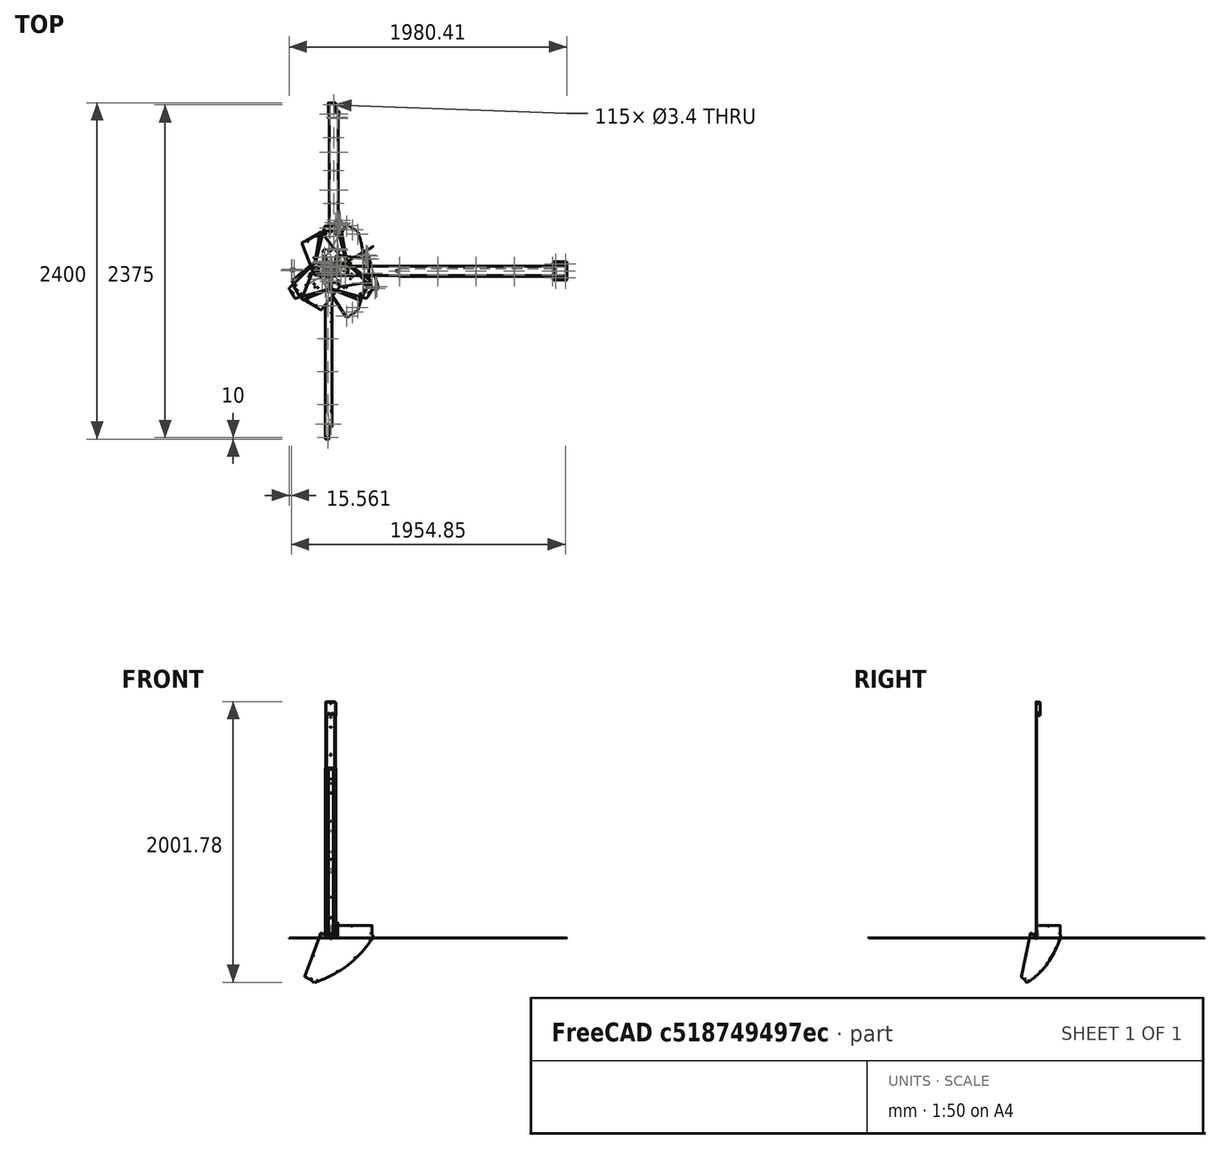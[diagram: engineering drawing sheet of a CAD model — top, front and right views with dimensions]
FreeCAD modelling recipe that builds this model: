
FCSTD DOCUMENT  (FreeCAD 0.22R37100 (Git))
Label: composit_full_size3_ss_unfold
License: All rights reserved
LicenseURL: http://en.wikipedia.org/wiki/All_rights_reserved
objects: Sketcher::SketchObject×72, TechDraw::DrawViewPart×63, TechDraw::DrawViewDimension×42, App::DocumentObjectGroup×27, Part::Feature×25, TechDraw::DrawPage×24, App::Link×23, TechDraw::DrawViewBalloon×16, PartDesign::Body×13, PartDesign::FeatureBase×12, Part::Mirroring×6, TechDraw::DrawSVGTemplate×3, PartDesign::SubShapeBinder×2, PartDesign::Pocket×2, PartDesign::FeatureAdditivePython×1, Measure::MeasureDistance×1
note: 211 computed .brp shape members not serialized (recipe doc carries the construction recipe); baked Part::Feature solids carry a one-line shape summary decoded from their .brp
EXTERNAL_REF file=composit_full_size3.FCStd obj=Body020
EXTERNAL_REF file=composit_full_size3.FCStd obj=Line
EXTERNAL_REF file=composit_full_size3.FCStd obj=Body014
EXTERNAL_REF file=composit_full_size3.FCStd obj=Body011
EXTERNAL_REF file=composit_full_size3.FCStd obj=Body010
EXTERNAL_REF file=composit_full_size3.FCStd obj=Body013
EXTERNAL_REF file=composit_full_size3.FCStd obj=Body012
EXTERNAL_REF file=composit_full_size3.FCStd obj=Body088
EXTERNAL_REF file=composit_full_size3.FCStd obj=Body095
EXTERNAL_REF file=composit_full_size3.FCStd obj=Body105
EXTERNAL_REF file=composit_full_size3.FCStd obj=Body107
EXTERNAL_REF file=composit_full_size3.FCStd obj=Body113
EXTERNAL_REF file=composit_full_size3.FCStd obj=Body112
EXTERNAL_REF file=composit_full_size3.FCStd obj=Body111
EXTERNAL_REF file=composit_full_size3.FCStd obj=Body141
EXTERNAL_REF file=composit_full_size3.FCStd obj=Body144
EXTERNAL_REF file=composit_full_size3.FCStd obj=Body147
EXTERNAL_REF file=composit_full_size3.FCStd obj=Body145
EXTERNAL_REF file=U-fix.FCStd obj=Page
EXTERNAL_REF file=U-fix.FCStd obj=Unfold_Sketch
EXTERNAL_REF file=U-fix.FCStd obj=Unfold_Sketch_Outline
EXTERNAL_REF file=U-fix.FCStd obj=Unfold_Sketch_Internal
EXTERNAL_REF file=U-fix.FCStd obj=Unfold
EXTERNAL_REF file=U-fix.FCStd obj=Unfold_Sketch_bends

FEATURE [App::Link] Link  label="sink_material_0.30ansi"
  LinkedObject = -> <external composit_full_size3.FCStd>#Body020
FEATURE [Part::Feature] Unfold
  Placement = pos=(0,0,0) rot=(-0.056475,0.056475,-0.996805;1.574rad)
  shape: bbox 311.2 x 661.7 x 0.5501 mm, 42 faces (baked)
  expr: Placement = placement(vector(0; 0; 0); rotation(270; 0; -<<composit_full_size3>>#<<sink_bend_line>>.BendAngle))
FEATURE [Sketcher::SketchObject] Unfold_Sketch_Outline
  FullyConstrained = false
  sketch-geometry (43):
    g0: LineSegment StartX=0.386884 StartY=-5.86581 StartZ=0 EndX=-12.2745 EndY=-14.2184 EndZ=0
    g1: ArcOfCircle CenterX=1.16253 CenterY=0.0838406 CenterZ=0 NormalX=0 NormalY=0 NormalZ=1 AngleXU=-1.5708 Radius=6 StartAngle=6.15355 EndAngle=6.28319
    g2: ArcOfCircle CenterX=1.16253 CenterY=0.0838406 CenterZ=0 NormalX=0 NormalY=0 NormalZ=1 AngleXU=-1.5708 Radius=6 StartAngle=0 EndAngle=0.208144
    g3: BSplineCurve PolesCount=15 KnotsCount=13 Degree=3 IsPeriodic=0
    g4: ArcOfCircle CenterX=1.01824 CenterY=-5.68e-14 CenterZ=0 NormalX=0 NormalY=0 NormalZ=1 AngleXU=-1.5708 Radius=6 StartAngle=0.844622 EndAngle=2.29697
    g5: BSplineCurve PolesCount=15 KnotsCount=13 Degree=3 IsPeriodic=0
    g6: ArcOfCircle CenterX=1.16253 CenterY=-0.0838406 CenterZ=0 NormalX=0 NormalY=0 NormalZ=1 AngleXU=-1.5708 Radius=6 StartAngle=2.93345 EndAngle=3.27123
    g7: LineSegment StartX=-12.2745 StartY=14.2184 StartZ=0 EndX=0.386884 EndY=5.86581 EndZ=0
    g8: ArcOfEllipse CenterX=-14.7094 CenterY=10.5287 CenterZ=0 NormalX=0 NormalY=0 NormalZ=1 MajorRadius=4.41375 MinorRadius=4.41323 AngleXU=-0.526269 StartAngle=1.51375 EndAngle=2.56133
    g9: ArcOfEllipse CenterX=-18.6691 CenterY=18.4369 CenterZ=0 NormalX=0 NormalY=0 NormalZ=1 MajorRadius=4.415 MinorRadius=4.41439 AngleXU=-0.524779 StartAngle=4.65412 EndAngle=5.7012
    g10: LineSegment StartX=-21.1041 StartY=14.745 StartZ=0 EndX=-68.9671 EndY=46.32 EndZ=0
    g11: LineSegment StartX=118.179 StartY=-330.006 StartZ=0 EndX=170.673 EndY=-295.376 EndZ=0
    g12: LineSegment StartX=173.776 StartY=-293.573 StartZ=0 EndX=170.673 EndY=-295.376 EndZ=0
    g13: ArcOfCircle CenterX=175.073 CenterY=-292.819 CenterZ=0 NormalX=0 NormalY=0 NormalZ=1 AngleXU=-1.5708 Radius=1.5 StartAngle=5.23877 EndAngle=6.83761
    g14: ArcOfCircle CenterX=146.907 CenterY=-247.333 CenterZ=0 NormalX=0 NormalY=0 NormalZ=1 AngleXU=-1.5708 Radius=55 StartAngle=0.554424 EndAngle=1.26385
    g15: ArcOfCircle CenterX=-630 CenterY=-1.08149 CenterZ=0 NormalX=0 NormalY=0 NormalZ=1 AngleXU=-1.5708 Radius=870 StartAngle=1.26385 EndAngle=1.88123
    g16: ArcOfCircle CenterX=146.043 CenterY=247.88 CenterZ=0 NormalX=0 NormalY=0 NormalZ=1 AngleXU=-1.5708 Radius=55 StartAngle=1.88123 EndAngle=2.56806
    g17: ArcOfCircle CenterX=175.073 CenterY=292.819 CenterZ=0 NormalX=0 NormalY=0 NormalZ=1 AngleXU=-1.5708 Radius=1.5 StartAngle=2.56806 EndAngle=4.18601
    g18: LineSegment StartX=173.776 StartY=293.573 StartZ=0 EndX=173.594 EndY=293.679 EndZ=0
    g19: LineSegment StartX=173.594 StartY=293.679 StartZ=0 EndX=172.802 EndY=294.139 EndZ=0
    g20: LineSegment StartX=172.802 StartY=294.139 StartZ=0 EndX=170.673 EndY=295.376 EndZ=0
    g21: LineSegment StartX=170.673 StartY=295.376 StartZ=0 EndX=118.179 EndY=330.006 EndZ=0
    g22: ArcOfEllipse CenterX=115.426 CenterY=325.833 CenterZ=0 NormalX=0 NormalY=0 NormalZ=1 MajorRadius=4.99274 MinorRadius=4.99229 AngleXU=-0.524687 StartAngle=1.51221 EndAngle=3.08331
    g23: LineSegment StartX=111.252 StartY=328.585 StartZ=0 EndX=-70.3874 EndY=53.2469 EndZ=0
    g24: ArcOfEllipse CenterX=-66.2147 CenterY=50.4931 CenterZ=0 NormalX=0 NormalY=0 NormalZ=1 MajorRadius=4.99283 MinorRadius=4.99237 AngleXU=-0.52491 StartAngle=3.08315 EndAngle=4.65425
    g25: ArcOfEllipse CenterX=-14.7108 CenterY=-10.5045 CenterZ=0 NormalX=0 NormalY=0 NormalZ=1 MajorRadius=4.43407 MinorRadius=4.43348 AngleXU=-2.61467 StartAngle=0.58231 EndAngle=1.62443
    g26: ArcOfEllipse CenterX=-18.6691 CenterY=-18.4349 CenterZ=0 NormalX=0 NormalY=0 NormalZ=1 MajorRadius=4.41385 MinorRadius=4.41333 AngleXU=-2.61724 StartAngle=3.72377 EndAngle=4.77132
    g27: LineSegment StartX=-21.1041 StartY=-14.745 StartZ=0 EndX=-68.9671 EndY=-46.32 EndZ=0
    g28: ArcOfEllipse CenterX=115.432 CenterY=-325.806 CenterZ=0 NormalX=0 NormalY=0 NormalZ=1 MajorRadius=5.01229 MinorRadius=5.01164 AngleXU=-2.61337 StartAngle=0.0587114 EndAngle=1.6218
    g29: LineSegment StartX=-70.3874 StartY=-53.2469 StartZ=0 EndX=111.252 EndY=-328.585 EndZ=0
    g30: ArcOfEllipse CenterX=-66.16 CenterY=-50.5033 CenterZ=0 NormalX=0 NormalY=0 NormalZ=1 MajorRadius=5.03229 MinorRadius=5.03046 AngleXU=-2.62463 StartAngle=4.78641 EndAngle=6.3419
    g31: Ellipse CenterX=-18.7978 CenterY=29.7538 CenterZ=0 NormalX=0 NormalY=0 NormalZ=-1 MajorRadius=1.7 MinorRadius=1.7 AngleXU=-2.61674
    g32: Ellipse CenterX=-18.7978 CenterY=-29.7538 CenterZ=0 NormalX=0 NormalY=0 NormalZ=-1 MajorRadius=1.7 MinorRadius=1.7 AngleXU=-0.524572
    g33: Ellipse CenterX=-60.5341 CenterY=57.2871 CenterZ=0 NormalX=0 NormalY=0 NormalZ=-1 MajorRadius=1.7 MinorRadius=1.7 AngleXU=-2.61674
    g34: Ellipse CenterX=-60.5341 CenterY=-57.2871 CenterZ=0 NormalX=0 NormalY=0 NormalZ=-1 MajorRadius=1.7 MinorRadius=1.7 AngleXU=-0.524572
    g35: Ellipse CenterX=155.902 CenterY=294.573 CenterZ=0 NormalX=0 NormalY=0 NormalZ=-1 MajorRadius=1.7 MinorRadius=1.7 AngleXU=-2.61674
    g36: Ellipse CenterX=155.902 CenterY=-294.573 CenterZ=0 NormalX=0 NormalY=0 NormalZ=-1 MajorRadius=1.7 MinorRadius=1.7 AngleXU=-0.524572
    g37: Ellipse CenterX=114.166 CenterY=322.106 CenterZ=0 NormalX=0 NormalY=0 NormalZ=-1 MajorRadius=1.7 MinorRadius=1.7 AngleXU=-2.61674
    g38: Ellipse CenterX=114.166 CenterY=-322.106 CenterZ=0 NormalX=0 NormalY=0 NormalZ=-1 MajorRadius=1.7 MinorRadius=1.7 AngleXU=-0.524572
    g39: Circle CenterX=228.865 CenterY=-88.3 CenterZ=0 NormalX=0 NormalY=0 NormalZ=-1 AngleXU=-1.5708 Radius=1.7
    g40: Circle CenterX=228.865 CenterY=88.3 CenterZ=0 NormalX=0 NormalY=0 NormalZ=-1 AngleXU=-1.5708 Radius=1.7
    g41: Circle CenterX=193.3 CenterY=-261.291 CenterZ=0 NormalX=0 NormalY=0 NormalZ=-1 AngleXU=-1.5708 Radius=1.7
    g42: Circle CenterX=193.3 CenterY=261.291 CenterZ=0 NormalX=0 NormalY=0 NormalZ=-1 AngleXU=-1.5708 Radius=1.7
FEATURE [Sketcher::SketchObject] Unfold_Sketch_bends
  FullyConstrained = false
  sketch-geometry (2):
    g0: LineSegment StartX=4.10484 StartY=5.14586 StartZ=0 EndX=172.225 EndY=294.474 EndZ=0
    g1: LineSegment StartX=4.10484 StartY=-5.14586 StartZ=0 EndX=172.225 EndY=-294.474 EndZ=0
FEATURE [Sketcher::SketchObject] Unfold_Sketch
  ExternalGeometry = -> [Unfold_Sketch_bends]
  FullyConstrained = false
  sketch-geometry (42):
    g0: LineSegment StartX=-12.2745 StartY=14.2184 StartZ=0 EndX=0.386884 EndY=5.86581 EndZ=0
    g1: LineSegment StartX=-21.1041 StartY=14.745 StartZ=0 EndX=-68.9671 EndY=46.32 EndZ=0
    g2: LineSegment StartX=170.673 StartY=295.376 StartZ=0 EndX=118.179 EndY=330.006 EndZ=0
    g3: ArcOfEllipse CenterX=115.426 CenterY=325.833 CenterZ=0 NormalX=0 NormalY=0 NormalZ=1 MajorRadius=4.99274 MinorRadius=4.99229 AngleXU=-0.524687 StartAngle=1.51221 EndAngle=3.08331
    g4: LineSegment StartX=111.252 StartY=328.585 StartZ=0 EndX=-70.3874 EndY=53.2469 EndZ=0
    g5: ArcOfEllipse CenterX=-66.2147 CenterY=50.4931 CenterZ=0 NormalX=0 NormalY=0 NormalZ=1 MajorRadius=4.99283 MinorRadius=4.99237 AngleXU=-0.52491 StartAngle=3.08315 EndAngle=4.65425
    g6: ArcOfCircle CenterX=175.073 CenterY=292.819 CenterZ=0 NormalX=0 NormalY=0 NormalZ=1 AngleXU=-1.5708 Radius=1.5 StartAngle=2.56806 EndAngle=4.18601
    g7: ArcOfCircle CenterX=146.043 CenterY=247.88 CenterZ=0 NormalX=0 NormalY=0 NormalZ=1 AngleXU=-1.5708 Radius=55 StartAngle=1.88123 EndAngle=2.56806
    g8: ArcOfCircle CenterX=-630 CenterY=-1.08149 CenterZ=0 NormalX=0 NormalY=0 NormalZ=1 AngleXU=-1.5708 Radius=870 StartAngle=1.26385 EndAngle=1.88123
    g9: ArcOfCircle CenterX=146.907 CenterY=-247.333 CenterZ=0 NormalX=0 NormalY=0 NormalZ=1 AngleXU=-1.5708 Radius=55 StartAngle=0.554424 EndAngle=1.26385
    g10: ArcOfCircle CenterX=175.073 CenterY=-292.819 CenterZ=0 NormalX=0 NormalY=0 NormalZ=1 AngleXU=-1.5708 Radius=1.5 StartAngle=5.23877 EndAngle=6.83761
    g11: LineSegment StartX=0.386884 StartY=-5.86581 StartZ=0 EndX=-12.2745 EndY=-14.2184 EndZ=0
    g12: LineSegment StartX=-21.1041 StartY=-14.745 StartZ=0 EndX=-68.9671 EndY=-46.32 EndZ=0
    g13: LineSegment StartX=118.179 StartY=-330.006 StartZ=0 EndX=170.673 EndY=-295.376 EndZ=0
    g14: ArcOfEllipse CenterX=115.432 CenterY=-325.806 CenterZ=0 NormalX=0 NormalY=0 NormalZ=1 MajorRadius=5.01229 MinorRadius=5.01164 AngleXU=-2.61337 StartAngle=0.0587114 EndAngle=1.6218
    g15: LineSegment StartX=-70.3874 StartY=-53.2469 StartZ=0 EndX=111.252 EndY=-328.585 EndZ=0
    g16: ArcOfEllipse CenterX=-66.16 CenterY=-50.5033 CenterZ=0 NormalX=0 NormalY=0 NormalZ=1 MajorRadius=5.03229 MinorRadius=5.03046 AngleXU=-2.62463 StartAngle=4.78641 EndAngle=6.3419
    g17: Ellipse CenterX=-18.7978 CenterY=29.7538 CenterZ=0 NormalX=0 NormalY=0 NormalZ=-1 MajorRadius=1.7 MinorRadius=1.7 AngleXU=-2.61674
    g18: Ellipse CenterX=-18.7978 CenterY=-29.7538 CenterZ=0 NormalX=0 NormalY=0 NormalZ=-1 MajorRadius=1.7 MinorRadius=1.7 AngleXU=-0.524572
    g19: Ellipse CenterX=-60.5341 CenterY=57.2871 CenterZ=0 NormalX=0 NormalY=0 NormalZ=-1 MajorRadius=1.7 MinorRadius=1.7 AngleXU=-2.61674
    g20: Ellipse CenterX=-60.5341 CenterY=-57.2871 CenterZ=0 NormalX=0 NormalY=0 NormalZ=-1 MajorRadius=1.7 MinorRadius=1.7 AngleXU=-0.524572
    g21: Ellipse CenterX=155.902 CenterY=294.573 CenterZ=0 NormalX=0 NormalY=0 NormalZ=-1 MajorRadius=1.7 MinorRadius=1.7 AngleXU=-2.61674
    g22: Ellipse CenterX=155.902 CenterY=-294.573 CenterZ=0 NormalX=0 NormalY=0 NormalZ=-1 MajorRadius=1.7 MinorRadius=1.7 AngleXU=-0.524572
    g23: Ellipse CenterX=114.166 CenterY=322.106 CenterZ=0 NormalX=0 NormalY=0 NormalZ=-1 MajorRadius=1.7 MinorRadius=1.7 AngleXU=-2.61674
    g24: Ellipse CenterX=114.166 CenterY=-322.106 CenterZ=0 NormalX=0 NormalY=0 NormalZ=-1 MajorRadius=1.7 MinorRadius=1.7 AngleXU=-0.524572
    g25: Circle CenterX=228.865 CenterY=-88.3 CenterZ=0 NormalX=0 NormalY=0 NormalZ=-1 AngleXU=-1.5708 Radius=1.7
    g26: Circle CenterX=228.865 CenterY=88.3 CenterZ=0 NormalX=0 NormalY=0 NormalZ=-1 AngleXU=-1.5708 Radius=1.7
    g27: Circle CenterX=193.3 CenterY=-261.291 CenterZ=0 NormalX=0 NormalY=0 NormalZ=-1 AngleXU=-1.5708 Radius=1.7
    g28: Circle CenterX=193.3 CenterY=261.291 CenterZ=0 NormalX=0 NormalY=0 NormalZ=-1 AngleXU=-1.5708 Radius=1.7
    g29: LineSegment StartX=173.776 StartY=-293.573 StartZ=0 EndX=170.673 EndY=-295.376 EndZ=0
    g30: LineSegment StartX=173.776 StartY=293.573 StartZ=0 EndX=173.594 EndY=293.679 EndZ=0
    g31: LineSegment StartX=173.594 StartY=293.679 StartZ=0 EndX=172.802 EndY=294.139 EndZ=0
    g32: LineSegment StartX=172.802 StartY=294.139 StartZ=0 EndX=170.673 EndY=295.376 EndZ=0
    g33: ArcOfCircle CenterX=1.64872 CenterY=3.2079e-12 CenterZ=0 NormalX=0 NormalY=0 NormalZ=1 AngleXU=0 Radius=6 StartAngle=4.5005 EndAngle=8.06587
    g34: ArcOfCircle CenterX=-14.7099 CenterY=10.5267 CenterZ=0 NormalX=0 NormalY=0 NormalZ=1 AngleXU=0 Radius=4.42265 StartAngle=0.987635 EndAngle=2.03483
    g35: ArcOfCircle CenterX=-18.6687 CenterY=18.4367 CenterZ=0 NormalX=0 NormalY=0 NormalZ=1 AngleXU=0 Radius=4.42265 StartAngle=4.12923 EndAngle=5.17643
    g36: ArcOfCircle CenterX=-14.7099 CenterY=-10.5267 CenterZ=0 NormalX=0 NormalY=0 NormalZ=1 AngleXU=0 Radius=4.42265 StartAngle=4.24835 EndAngle=5.29555
    g37: ArcOfCircle CenterX=-18.6687 CenterY=-18.4367 CenterZ=0 NormalX=0 NormalY=0 NormalZ=1 AngleXU=0 Radius=4.42265 StartAngle=1.10676 EndAngle=2.15396
    g38: LineSegment StartX=172.225 StartY=-294.474 StartZ=0 EndX=171.22 EndY=-292.745 EndZ=0
    g39: LineSegment StartX=4.25505 StartY=-5.40436 StartZ=0 EndX=5.25987 EndY=-7.13362 EndZ=0
    g40: LineSegment StartX=4.25505 StartY=5.40436 StartZ=0 EndX=5.25987 EndY=7.13362 EndZ=0
    g41: LineSegment StartX=172.225 StartY=294.474 StartZ=0 EndX=171.22 EndY=292.745 EndZ=0
  constraints (39):
    c: Coincident(g33,g0)
    c: Coincident(g33,g11)
    c: Diameter(g33) = 12
    c: Coincident(g13,g29)
    c: Coincident(g2,g32)
    c: Coincident(g31,g32)
    c: Coincident(g30,g31)
    c: Coincident(g10,g29)
    c: Coincident(g6,g30)
    c: Coincident(g9,g10)
    c: Coincident(g6,g7)
    c: Coincident(g7,g8)
    c: Coincident(g8,g9)
    c: Block(g12)
    c: Block(g11)
    c: Block(g1)
    c: Block(g0)
    c: Tangent(g1,g35) = 1.5708
    c: Tangent(g35,g34) = 1.5708
    c: Tangent(g34,g0) = 1.5708
    c: PointOnObject(g34,g1)
    c: Tangent(g37,g12) = -1.5708
    c: Tangent(g36,g11) = 1.5708
    c: Tangent(g37,g36) = 1.5708
    c: PointOnObject(g37,g11)
    c: Coincident(g41,g-4)
    c: PointOnObject(g41,g-4)
    c: PointOnObject(g40,g33)
    c: PointOnObject(g40,g-4)
    c: PointOnObject(g40,g-4)
    c: PointOnObject(g39,g-3)
    c: PointOnObject(g39,g33)
    c: PointOnObject(g39,g-3)
    c: Coincident(g38,g-3)
    c: PointOnObject(g38,g-3)
    c: Equal(g38,g39)
    c: Equal(g39,g40)
    c: Equal(g40,g41)
    c: Distance(g41) = 2
FEATURE [PartDesign::FeatureBase] BaseFeature
  BaseFeature = -> Unfold
  Placement = pos=(0,0,0) rot=(-0.056475,0.056475,-0.996805;1.574rad)
  Suppressed = false
  expr: Placement = .BaseFeature.Placement
FEATURE [PartDesign::SubShapeBinder] Binder
  BindCopyOnChange = 0
  BindMode = 0
  ClaimChildren = false
  Context = -> Body [Binder.]
  Fuse = false
  MakeFace = true
  OffsetFill = false
  OffsetIntersection = false
  OffsetJoinType = 0
  OffsetOpenResult = false
  PartialLoad = false
  Relative = true
  Support = -> [Unfold_Sketch_bends]
  _Version = 2
FEATURE [Sketcher::SketchObject] Sketch
  AttachmentSupport = -> [XY_Plane]
  ExternalGeometry = -> [Binder]
  FullyConstrained = false
  MapMode = 5
  sketch-geometry (9):
    g0: Circle CenterX=172.913 CenterY=-294.074 CenterZ=0 NormalX=0 NormalY=0 NormalZ=1 AngleXU=0 Radius=1
    g1: Circle CenterX=4.76114 CenterY=-4.69033 CenterZ=0 NormalX=0 NormalY=0 NormalZ=1 AngleXU=0 Radius=1
    g2: Circle CenterX=4.76114 CenterY=4.69033 CenterZ=0 NormalX=0 NormalY=0 NormalZ=1 AngleXU=0 Radius=1
    g3: Circle CenterX=172.913 CenterY=294.074 CenterZ=0 NormalX=0 NormalY=0 NormalZ=1 AngleXU=0 Radius=1
    g4: LineSegment StartX=172.225 StartY=-294.474 StartZ=0 EndX=172.913 EndY=-294.074 EndZ=0
    g5: LineSegment StartX=4.07262 StartY=-5.0904 StartZ=0 EndX=4.76114 EndY=-4.69033 EndZ=0
    g6: LineSegment StartX=4.07262 StartY=5.0904 StartZ=0 EndX=4.76114 EndY=4.69033 EndZ=0
    g7: ArcOfCircle CenterX=1.01937 CenterY=5.2064e-12 CenterZ=0 NormalX=0 NormalY=0 NormalZ=1 AngleXU=0 Radius=6 StartAngle=5.25252 EndAngle=7.31385
    g8: LineSegment StartX=172.225 StartY=294.474 StartZ=0 EndX=172.913 EndY=294.074 EndZ=0
  constraints (25):
    c: Diameter(g0) = 2
    c: Equal(g0,g1)
    c: Equal(g1,g2)
    c: Equal(g2,g3)
    c: Coincident(g4,g-3)
    c: Coincident(g4,g0)
    c: Perpendicular(g-3,g4)
    c: Distance(g4) = 0.796314
    c: PointOnObject(g5,g-3)
    c: Perpendicular(g-3,g5)
    c: PointOnObject(g6,g-4)
    c: Perpendicular(g-4,g6)
    c: Coincident(g7,g-3)
    c: Coincident(g7,g-4)
    c: Coincident(g2,g6)
    c: PointOnObject(g2,g7)
    c: Radius(g7) = 6
    c: Coincident(g5,g1)
    c: PointOnObject(g1,g7)
    c: Equal(g5,g6)
    c: Equal(g6,g4)
    c: Coincident(g8,g-4)
    c: Coincident(g8,g3)
    c: Perpendicular(g-4,g8)
    c: Equal(g8,g6)
FEATURE [PartDesign::Pocket] Pocket
  BaseFeature = -> BaseFeature
  Direction = (0,0,-1)
  Length = 5
  Length2 = 5
  Midplane = true
  Placement = pos=(0,0,0) rot=(-0.056475,0.056475,-0.996805;1.574rad)
  Profile = -> Sketch
  ReferenceAxis = -> Sketch [N_Axis]
  Suppressed = false
  Type = 1
FEATURE [PartDesign::Body] Body
  BaseFeature = -> Unfold
  Group = -> [BaseFeature,Binder,Sketch,Pocket]
  Origin = -> Origin
  Tip = -> Pocket
FEATURE [TechDraw::DrawSVGTemplate] Template
  Height = 210
  Orientation = 1
  Template = <path>
  Width = 297
FEATURE [TechDraw::DrawViewPart] View
  CoarseView = false
  Direction = (-0.866025,0.5,0.0566562)
  Focus = 100
  HardHidden = false
  IsoCount = 0
  IsoHidden = false
  IsoVisible = false
  LockPosition = false
  Perspective = false
  Rotation = 0
  Scale = 0.5
  ScaleType = 1
  ScrubCount = 0
  SeamHidden = false
  SeamVisible = true
  SmoothHidden = false
  SmoothVisible = true
  X = 94
  XDirection = (-0.5,-0.866025,-1.35524e-07)
  XSource = -> [Link]
  Y = 106.6
  expr: .Direction.x = sin(-60)
  expr: .Direction.y = cos(-60)
  expr: .Direction.z = sin(composit_full_size3#<<sink_bend_line>>.FaceAngle)
FEATURE [App::Link] Link001  label="top_dec_corner_0.30ansi"
  LinkedObject = -> <external composit_full_size3.FCStd>#Body014
FEATURE [App::Link] Link002  label="pillar_bottom_material_0.30ansi"
  LinkedObject = -> <external composit_full_size3.FCStd>#Body011
FEATURE [App::Link] Link003  label="pillar_material_0.30ansi"
  LinkedObject = -> <external composit_full_size3.FCStd>#Body010
FEATURE [App::Link] Link004  label="dec_corner_0.30ansi"
  LinkedObject = -> <external composit_full_size3.FCStd>#Body013
FEATURE [App::Link] Link005  label="pillar_top_element_0.30ansi"
  LinkedObject = -> <external composit_full_size3.FCStd>#Body012
FEATURE [Part::Feature] Unfold002  label="top_dec_unfold"
  Placement = pos=(0,0,2) rot=(0.57735,0.57735,0.57735;2.0944rad)
  shape: bbox 96 x 102.9 x 0.5612 mm, 18 faces (baked)
FEATURE [Sketcher::SketchObject] Unfold_Sketch002  label="top_dec_sketch"
  FullyConstrained = false
  sketch-geometry (16):
    g0: LineSegment StartX=1591 StartY=-65.3772 StartZ=0 EndX=1681 EndY=-65.3772 EndZ=0
    g1: LineSegment StartX=1594 StartY=-18.3 StartZ=0 EndX=1594 EndY=34.5 EndZ=0
    g2: ArcOfCircle CenterX=1597 CenterY=34.5 CenterZ=0 NormalX=0 NormalY=0 NormalZ=1 AngleXU=0 Radius=3 StartAngle=1.5708 EndAngle=3.14159
    g3: ArcOfCircle CenterX=1580.17 CenterY=-18.3 CenterZ=0 NormalX=0 NormalY=0 NormalZ=1 AngleXU=1.5708 Radius=13.8267 StartAngle=4.04111 EndAngle=4.71239
    g4: LineSegment StartX=1597 StartY=37.5 StartZ=0 EndX=1681 EndY=37.5 EndZ=0
    g5: ArcOfCircle CenterX=1601.83 CenterY=-35.5 CenterZ=0 NormalX=0 NormalY=0 NormalZ=1 AngleXU=1.5708 Radius=13.8267 StartAngle=0.899519 EndAngle=1.5708
    g6: Circle CenterX=1605 CenterY=12.5 CenterZ=0 NormalX=0 NormalY=0 NormalZ=1 AngleXU=1.5708 Radius=1.8
    g7: Circle CenterX=1605 CenterY=-12.5 CenterZ=0 NormalX=0 NormalY=0 NormalZ=1 AngleXU=1.5708 Radius=1.8
    g8: Circle CenterX=1674 CenterY=-50.3772 CenterZ=0 NormalX=0 NormalY=0 NormalZ=-1 AngleXU=0 Radius=1.7
    g9: Circle CenterX=1604 CenterY=-50.3772 CenterZ=0 NormalX=0 NormalY=0 NormalZ=-1 AngleXU=0 Radius=1.7
    g10: Circle CenterX=1673 CenterY=0 CenterZ=0 NormalX=0 NormalY=0 NormalZ=1 AngleXU=1.5708 Radius=1.7
    g11: LineSegment StartX=1684 StartY=34.5 StartZ=0 EndX=1684 EndY=-62.3772 EndZ=0
    g12: LineSegment StartX=1588 StartY=-62.3772 StartZ=0 EndX=1588 EndY=-35.5 EndZ=0
    g13: ArcOfCircle CenterX=1681 CenterY=-62.3772 CenterZ=0 NormalX=0 NormalY=0 NormalZ=1 AngleXU=0 Radius=3 StartAngle=4.71239 EndAngle=6.28319
    g14: ArcOfCircle CenterX=1681 CenterY=34.5 CenterZ=0 NormalX=0 NormalY=0 NormalZ=1 AngleXU=0 Radius=3 StartAngle=3.02e-14 EndAngle=1.5708
    g15: ArcOfCircle CenterX=1591 CenterY=-62.3772 CenterZ=0 NormalX=0 NormalY=0 NormalZ=1 AngleXU=0 Radius=3 StartAngle=3.14159 EndAngle=4.71239
  constraints (10):
    c: Block(g12)
    c: Block(g0)
    c: Block(g11)
    c: Block(g4)
    c: Tangent(g14,g4) = 1.5708
    c: Tangent(g13,g11) = 1.5708
    c: Tangent(g15,g0) = -1.5708
    c: Coincident(g14,g11)
    c: Coincident(g13,g0)
    c: Coincident(g15,g12)
FEATURE [Sketcher::SketchObject] Unfold_Sketch_bends002  label="top_dec_bends"
  FullyConstrained = false
  Placement = pos=(0,-15.2418,-18.2896) rot=(-1,0,0;0.694754rad)
  sketch-geometry (1):
    g0: LineSegment StartX=1684 StartY=-28.5687 StartZ=0 EndX=1588 EndY=-28.5687 EndZ=0
FEATURE [Part::Feature] Unfold005  label="dec_corner_Unfold"
  Placement = pos=(0,0,2) rot=(0.57735,0.57735,0.57735;2.0944rad)
  shape: bbox 1113 x 56.48 x 0.5612 mm, 20 faces (baked)
FEATURE [Sketcher::SketchObject] Unfold_Sketch005  label="dec_corner_Sketch"
  FullyConstrained = false
  sketch-geometry (18):
    g0: LineSegment StartX=486 StartY=-38.1772 StartZ=0 EndX=1589 EndY=-38.1772 EndZ=0
    g1: BSplineCurve PolesCount=22 KnotsCount=5 Degree=6 IsPeriodic=0
    g2: BSplineCurve PolesCount=22 KnotsCount=5 Degree=6 IsPeriodic=0
    g3: LineSegment StartX=1594 StartY=-33.1772 StartZ=0 EndX=1594 EndY=13.3 EndZ=0
    g4: BSplineCurve PolesCount=22 KnotsCount=5 Degree=6 IsPeriodic=0
    g5: LineSegment StartX=486 StartY=18.3 StartZ=0 EndX=1589 EndY=18.3 EndZ=0
    g6: BSplineCurve PolesCount=22 KnotsCount=5 Degree=6 IsPeriodic=0
    g7: LineSegment StartX=481 StartY=-33.1772 StartZ=0 EndX=481 EndY=13.3 EndZ=0
    g8: Circle CenterX=1584 CenterY=-31.062 CenterZ=0 NormalX=0 NormalY=0 NormalZ=1 AngleXU=1.5708 Radius=1.7
    g9: Circle CenterX=1310.75 CenterY=-31.062 CenterZ=0 NormalX=0 NormalY=0 NormalZ=1 AngleXU=1.5708 Radius=1.7
    g10: Circle CenterX=1037.5 CenterY=-31.062 CenterZ=0 NormalX=0 NormalY=0 NormalZ=1 AngleXU=1.5708 Radius=1.7
    g11: Circle CenterX=764.25 CenterY=-31.062 CenterZ=0 NormalX=0 NormalY=0 NormalZ=1 AngleXU=1.5708 Radius=1.7
    g12: Circle CenterX=1584 CenterY=0 CenterZ=0 NormalX=0 NormalY=0 NormalZ=1 AngleXU=1.5708 Radius=1.7
    g13: Circle CenterX=1310.75 CenterY=0 CenterZ=0 NormalX=0 NormalY=0 NormalZ=1 AngleXU=1.5708 Radius=1.7
    g14: Circle CenterX=1037.5 CenterY=0 CenterZ=0 NormalX=0 NormalY=0 NormalZ=1 AngleXU=1.5708 Radius=1.7
    g15: Circle CenterX=764.25 CenterY=0 CenterZ=0 NormalX=0 NormalY=0 NormalZ=1 AngleXU=1.5708 Radius=1.7
    g16: Circle CenterX=491 CenterY=-31.062 CenterZ=0 NormalX=0 NormalY=0 NormalZ=1 AngleXU=1.5708 Radius=1.7
    g17: Circle CenterX=491 CenterY=0 CenterZ=0 NormalX=0 NormalY=0 NormalZ=1 AngleXU=1.5708 Radius=1.7
FEATURE [Sketcher::SketchObject] Unfold_Sketch_bends005  label="dec_corner_bends"
  FullyConstrained = false
  Placement = pos=(0,-3.14497,-6.83248) rot=(-1,0,0;0.431384rad)
  sketch-geometry (1):
    g0: LineSegment StartX=1594 StartY=-16.3406 StartZ=0 EndX=481 EndY=-16.3406 EndZ=0
FEATURE [PartDesign::SubShapeBinder] Binder001
  BindCopyOnChange = 0
  BindMode = 0
  ClaimChildren = false
  Context = -> Body001 [Binder001.]
  Fuse = false
  MakeFace = true
  OffsetFill = false
  OffsetIntersection = false
  OffsetJoinType = 0
  OffsetOpenResult = false
  PartialLoad = false
  Relative = true
  Support = -> [Unfold_Sketch_bends023]
  _Version = 2
  expr: Support = <<pillar_top_Sketch_bends>>._self
FEATURE [Sketcher::SketchObject] Sketch001
  AttachmentSupport = -> [XY_Plane001]
  ExternalGeometry = -> [Binder001]
  FullyConstrained = true
  MapMode = 5
  sketch-geometry (6):
    g0: Circle CenterX=-34.042 CenterY=-80.0841 CenterZ=0 NormalX=0 NormalY=0 NormalZ=1 AngleXU=0 Radius=1
    g1: Circle CenterX=34.042 CenterY=-80.0841 CenterZ=0 NormalX=0 NormalY=0 NormalZ=1 AngleXU=0 Radius=1
    g2: Circle CenterX=34.042 CenterY=-0.0840704 CenterZ=0 NormalX=0 NormalY=0 NormalZ=1 AngleXU=0 Radius=1
    g3: Circle CenterX=32 CenterY=1.95796 CenterZ=0 NormalX=0 NormalY=0 NormalZ=1 AngleXU=0 Radius=1
    g4: Circle CenterX=-32 CenterY=1.95796 CenterZ=0 NormalX=0 NormalY=0 NormalZ=1 AngleXU=0 Radius=1
    g5: Circle CenterX=-34.042 CenterY=-0.0840704 CenterZ=0 NormalX=0 NormalY=0 NormalZ=1 AngleXU=0 Radius=1
  constraints (12):
    c: Coincident(g0,g-5)
    c: Coincident(g1,g-6)
    c: Coincident(g2,g-6)
    c: Coincident(g3,g-3)
    c: Coincident(g4,g-4)
    c: Coincident(g5,g-5)
    c: Equal(g0,g1)
    c: Equal(g0,g2)
    c: Equal(g0,g3)
    c: Equal(g0,g5)
    c: Equal(g0,g4)
    c: Diameter(g0) = 2
FEATURE [PartDesign::FeatureBase] BaseFeature002
  BaseFeature = -> Unfold002
  Placement = pos=(0,0,2) rot=(0.57735,0.57735,0.57735;2.0944rad)
  Suppressed = false
  expr: Placement = .BaseFeature.Placement
FEATURE [PartDesign::Body] Body002
  BaseFeature = -> Unfold002
  Group = -> [BaseFeature002]
  Origin = -> Origin002
  Tip = -> BaseFeature002
FEATURE [PartDesign::FeatureBase] BaseFeature005
  BaseFeature = -> Unfold005
  Placement = pos=(0,0,2) rot=(0.57735,0.57735,0.57735;2.0944rad)
  Suppressed = false
  expr: Placement = .BaseFeature.Placement
FEATURE [PartDesign::Body] Body005  label="dec_corner_Body"
  BaseFeature = -> Unfold005
  Group = -> [BaseFeature005]
  Origin = -> Origin005
  Tip = -> BaseFeature005
FEATURE [TechDraw::DrawSVGTemplate] Template001
  Height = 210
  Orientation = 1
  Template = <path>
  Width = 297
FEATURE [TechDraw::DrawViewPart] View001
  CoarseView = false
  Direction = (0,0,1)
  Focus = 100
  HardHidden = false
  IsoCount = 0
  IsoHidden = false
  IsoVisible = false
  LockPosition = false
  Perspective = false
  Rotation = 0
  ScaleType = 0
  ScrubCount = 0
  SeamHidden = false
  SeamVisible = true
  SmoothHidden = false
  SmoothVisible = true
  X = 49.8472
  XDirection = (-1,0,0)
  XSource = -> [Link005]
  Y = 56.0363
FEATURE [TechDraw::DrawViewPart] View002
  CoarseView = false
  Direction = (-1,0,0)
  Focus = 100
  HardHidden = false
  IsoCount = 0
  IsoHidden = false
  IsoVisible = false
  LockPosition = false
  Perspective = false
  Rotation = 0
  ScaleType = 0
  ScrubCount = 0
  SeamHidden = false
  SeamVisible = true
  SmoothHidden = false
  SmoothVisible = true
  X = 49.3333
  XDirection = (0,-1,1e-06)
  XSource = -> [Link005]
  Y = 154.075
FEATURE [TechDraw::DrawViewPart] View003
  CoarseView = false
  Direction = (-0.57735,0.57735,0.57735)
  Focus = 100
  HardHidden = false
  IsoCount = 0
  IsoHidden = false
  IsoVisible = false
  LockPosition = false
  Perspective = false
  Rotation = 0
  ScaleType = 0
  ScrubCount = 0
  SeamHidden = false
  SeamVisible = true
  SmoothHidden = false
  SmoothVisible = true
  X = 235.392
  XDirection = (-0.707107,-0.707107,5.7735e-07)
  XSource = -> [Link005]
  Y = 79.5516
FEATURE [TechDraw::DrawViewPart] View004
  CoarseView = false
  Direction = (0,1,0)
  Focus = 100
  HardHidden = false
  IsoCount = 0
  IsoHidden = false
  IsoVisible = false
  LockPosition = false
  Perspective = false
  Rotation = 0
  ScaleType = 0
  ScrubCount = 0
  SeamHidden = false
  SeamVisible = true
  SmoothHidden = false
  SmoothVisible = true
  X = 139.75
  XDirection = (-1,0,1e-06)
  XSource = -> [Link005]
  Y = 155.233
FEATURE [TechDraw::DrawViewDimension] Dimension
  AngleOverride = false
  Arbitrary = false
  ArbitraryTolerances = false
  BoxCorners = (2) [(-36,-35,-1e-07),(36,35,1e-07)]
  EqualTolerance = true
  ExtensionAngle = 0
  FormatSpec = R%.2w
  FormatSpecOverTolerance = %+.2w
  FormatSpecUnderTolerance = %+.2w
  Inverted = false
  LineAngle = 0
  LockPosition = false
  MeasureType = 1
  OverTolerance = 0
  References2D = -> [View001]
  Rotation = 0
  ScaleType = 0
  TheoreticalExact = false
  Type = 4
  UnderTolerance = 0
  X = 0
  Y = -10.2313
FEATURE [TechDraw::DrawViewDimension] Dimension001
  AngleOverride = false
  Arbitrary = false
  ArbitraryTolerances = false
  BoxCorners = (2) [(-36,-35,-1e-07),(36,35,1e-07)]
  EqualTolerance = true
  ExtensionAngle = 0
  FormatSpec = R%.2w
  FormatSpecOverTolerance = %+.2w
  FormatSpecUnderTolerance = %+.2w
  Inverted = false
  LineAngle = 0
  LockPosition = false
  MeasureType = 1
  OverTolerance = 0
  References2D = -> [View001]
  Rotation = 0
  ScaleType = 0
  TheoreticalExact = false
  Type = 4
  UnderTolerance = 0
  X = 20.3807
  Y = 2.20895
FEATURE [TechDraw::DrawViewDimension] Dimension002
  AngleOverride = false
  Arbitrary = false
  ArbitraryTolerances = false
  BoxCorners = (2) [(-35,-42,-1e-07),(35,42,1e-07)]
  EqualTolerance = true
  ExtensionAngle = 0
  FormatSpec = R%.2w
  FormatSpecOverTolerance = %+.2w
  FormatSpecUnderTolerance = %+.2w
  Inverted = false
  LineAngle = 0
  LockPosition = false
  MeasureType = 1
  OverTolerance = 0
  References2D = -> [View002]
  Rotation = 0
  ScaleType = 0
  TheoreticalExact = false
  Type = 4
  UnderTolerance = 0
  X = 17.6168
  Y = -24.0362
FEATURE [TechDraw::DrawSVGTemplate] Template002
  Height = 210
  Orientation = 1
  Template = <path>
  Width = 297
FEATURE [TechDraw::DrawViewPart] View005
  CoarseView = false
  Direction = (-0.57735,-0.57735,0.57735)
  Focus = 100
  HardHidden = false
  IsoCount = 0
  IsoHidden = false
  IsoVisible = false
  LockPosition = false
  Perspective = false
  Rotation = 0
  ScaleType = 0
  ScrubCount = 0
  SeamHidden = false
  SeamVisible = true
  SmoothHidden = false
  SmoothVisible = true
  X = 53.8368
  XDirection = (0.707107,-0.707107,0)
  XSource = -> [Link001]
  Y = 122.409
FEATURE [TechDraw::DrawViewPart] View006
  CoarseView = false
  Direction = (0,-1,0)
  Focus = 100
  HardHidden = false
  IsoCount = 0
  IsoHidden = false
  IsoVisible = false
  LockPosition = false
  Perspective = false
  Rotation = 0
  ScaleType = 0
  ScrubCount = 0
  SeamHidden = false
  SeamVisible = true
  SmoothHidden = false
  SmoothVisible = true
  X = 195.54
  XDirection = (1,0,0)
  XSource = -> [Link001]
  Y = 137.204
FEATURE [TechDraw::DrawViewPart] View007
  CoarseView = false
  Direction = (-1,0,0)
  Focus = 100
  HardHidden = false
  IsoCount = 0
  IsoHidden = false
  IsoVisible = false
  LockPosition = false
  Perspective = false
  Rotation = 0
  ScaleType = 0
  ScrubCount = 0
  SeamHidden = false
  SeamVisible = true
  SmoothHidden = false
  SmoothVisible = true
  X = 263.111
  XDirection = (0,-1,0)
  XSource = -> [Link001]
  Y = 104.275
FEATURE [TechDraw::DrawViewPart] View008
  CoarseView = false
  Direction = (0,0,1)
  Focus = 100
  HardHidden = false
  IsoCount = 0
  IsoHidden = false
  IsoVisible = false
  LockPosition = false
  Perspective = false
  Rotation = 0
  ScaleType = 0
  ScrubCount = 0
  SeamHidden = false
  SeamVisible = true
  SmoothHidden = false
  SmoothVisible = true
  X = 193.175
  XDirection = (1,0,0)
  XSource = -> [Link001]
  Y = 53.7375
FEATURE [TechDraw::DrawViewDimension] Dimension006
  AngleOverride = false
  Arbitrary = false
  ArbitraryTolerances = false
  EqualTolerance = true
  ExtensionAngle = 0
  FormatSpec = R%.2w
  FormatSpecOverTolerance = %+.2w
  FormatSpecUnderTolerance = %+.2w
  Inverted = false
  LineAngle = 0
  LockPosition = false
  MeasureType = 1
  OverTolerance = 0
  References2D = -> [View008]
  Rotation = 0
  ScaleType = 0
  TheoreticalExact = false
  Type = 4
  UnderTolerance = 0
  X = -40.2919
  Y = 3.24179
FEATURE [TechDraw::DrawViewDimension] Dimension007
  AngleOverride = false
  Arbitrary = false
  ArbitraryTolerances = false
  BoxCorners = (2) [(-37.75,-14.5,-1e-07),(37.75,14.5,1e-07)]
  EqualTolerance = true
  ExtensionAngle = 0
  FormatSpec = %.2w
  FormatSpecOverTolerance = %+.2w
  FormatSpecUnderTolerance = %+.2w
  Inverted = false
  LineAngle = 0
  LockPosition = false
  MeasureType = 1
  OverTolerance = 0
  References2D = -> [View008]
  Rotation = 0
  ScaleType = 0
  TheoreticalExact = false
  Type = 2
  UnderTolerance = 0
  X = -55.6811
  Y = 5.19003
FEATURE [TechDraw::DrawViewDimension] Dimension008
  AngleOverride = false
  Arbitrary = false
  ArbitraryTolerances = false
  BoxCorners = (2) [(-37.75,-14.5,-1e-07),(37.75,14.5,1e-07)]
  EqualTolerance = true
  ExtensionAngle = 0
  FormatSpec = %.2w
  FormatSpecOverTolerance = %+.2w
  FormatSpecUnderTolerance = %+.2w
  Inverted = false
  LineAngle = 0
  LockPosition = false
  MeasureType = 1
  OverTolerance = 0
  References2D = -> [View008]
  Rotation = 0
  ScaleType = 0
  TheoreticalExact = false
  Type = 1
  UnderTolerance = 0
  X = -0.304578
  Y = -1.10503
FEATURE [TechDraw::DrawViewDimension] Dimension009
  AngleOverride = false
  Arbitrary = false
  ArbitraryTolerances = false
  BoxCorners = (2) [(-37.75,-48,-1e-07),(37.75,48,1e-07)]
  EqualTolerance = true
  ExtensionAngle = 0
  FormatSpec = %.2w
  FormatSpecOverTolerance = %+.2w
  FormatSpecUnderTolerance = %+.2w
  Inverted = false
  LineAngle = 0
  LockPosition = false
  MeasureType = 1
  OverTolerance = 0
  References2D = -> [View006]
  Rotation = 0
  ScaleType = 0
  TheoreticalExact = false
  Type = 2
  UnderTolerance = 0
  X = -49.503
  Y = 10.7552
FEATURE [TechDraw::DrawViewBalloon] Balloon
  BubbleShape = 3
  EndType = 0
  EndTypeScale = 1
  KinkLength = 5
  LockPosition = false
  OriginX = 18.2143
  OriginY = 13.2347
  Rotation = 0
  ScaleType = 0
  ShapeScale = 1
  SourceView = -> View005
  Text = Лицевая сторона
  TextWrapLen = -1
  X = 56.9862
  Y = 68.2128
FEATURE [TechDraw::DrawPage] Page002  label="top_dec_page"
  KeepUpdated = true
  NextBalloonIndex = 4
  ProjectionType = 0
  Template = -> Template002
  Views = -> [View005,View006,View007,View008,Dimension006,Dimension007,Dimension008,Dimension009,Balloon]
FEATURE [TechDraw::DrawViewPart] View009
  CoarseView = false
  Direction = (-0.57735,0.57735,0.57735)
  Focus = 100
  HardHidden = false
  IsoCount = 0
  IsoHidden = false
  IsoVisible = false
  LockPosition = false
  Perspective = false
  Rotation = 90
  Scale = 0.2
  ScaleType = 2
  ScrubCount = 0
  SeamHidden = false
  SeamVisible = true
  SmoothHidden = false
  SmoothVisible = true
  X = 148.5
  XDirection = (-0.707107,-0.707107,-5.7735e-07)
  XSource = -> [Link003]
  Y = 195
FEATURE [TechDraw::DrawViewPart] View010
  CoarseView = false
  Direction = (0,1,0)
  Focus = 100
  HardHidden = false
  IsoCount = 0
  IsoHidden = false
  IsoVisible = false
  LockPosition = false
  Perspective = false
  Rotation = 90
  Scale = 0.16
  ScaleType = 2
  ScrubCount = 0
  SeamHidden = false
  SeamVisible = true
  SmoothHidden = false
  SmoothVisible = true
  X = 148.5
  XDirection = (-1,0,1e-06)
  XSource = -> [Link003]
  Y = 135
FEATURE [TechDraw::DrawViewPart] View011
  CoarseView = false
  Direction = (1,0,-1e-06)
  Focus = 100
  HardHidden = false
  IsoCount = 0
  IsoHidden = false
  IsoVisible = false
  LockPosition = false
  Perspective = false
  Rotation = 90
  Scale = 0.16
  ScaleType = 2
  ScrubCount = 0
  SeamHidden = false
  SeamVisible = true
  SmoothHidden = false
  SmoothVisible = true
  X = 148.5
  XDirection = (0,1,0)
  XSource = -> [Link003]
  Y = 85
FEATURE [TechDraw::DrawViewPart] View012
  CoarseView = false
  Direction = (0,0,1)
  Focus = 100
  HardHidden = false
  IsoCount = 0
  IsoHidden = false
  IsoVisible = false
  LockPosition = false
  Perspective = false
  Rotation = 90
  ScaleType = 0
  ScrubCount = 0
  SeamHidden = false
  SeamVisible = true
  SmoothHidden = false
  SmoothVisible = true
  X = 150.358
  XDirection = (0,1,0)
  XSource = -> [Link003]
  Y = 48.6118
FEATURE [TechDraw::DrawViewBalloon] Balloon003
  BubbleShape = 3
  EndType = 0
  EndTypeScale = 1
  KinkLength = 5
  LockPosition = false
  OriginX = 3.10544
  OriginY = -9.6917
  Rotation = 0
  ScaleType = 0
  ShapeScale = 1
  SourceView = -> View012
  Text = Лицевая сторона
  TextWrapLen = -1
  X = -34.8869
  Y = -24.2754
FEATURE [TechDraw::DrawViewDimension] Dimension014
  AngleOverride = false
  Arbitrary = false
  ArbitraryTolerances = false
  EqualTolerance = true
  ExtensionAngle = 0
  FormatSpec = R%.2w
  FormatSpecOverTolerance = %+.2w
  FormatSpecUnderTolerance = %+.2w
  Inverted = false
  LineAngle = 0
  LockPosition = false
  MeasureType = 1
  OverTolerance = 0
  References2D = -> [View012]
  Rotation = 0
  ScaleType = 0
  TheoreticalExact = false
  Type = 4
  UnderTolerance = 0
  X = -10.1622
  Y = 0.166593
FEATURE [TechDraw::DrawViewDimension] Dimension015
  AngleOverride = false
  Arbitrary = false
  ArbitraryTolerances = false
  EqualTolerance = true
  ExtensionAngle = 0
  FormatSpec = R%.2w
  FormatSpecOverTolerance = %+.2w
  FormatSpecUnderTolerance = %+.2w
  Inverted = false
  LineAngle = 0
  LockPosition = false
  MeasureType = 1
  OverTolerance = 0
  References2D = -> [View012]
  Rotation = 0
  ScaleType = 0
  TheoreticalExact = false
  Type = 4
  UnderTolerance = 0
  X = 8.66286
  Y = -0.666374
FEATURE [TechDraw::DrawViewBalloon] Balloon004
  BubbleShape = 3
  EndType = 0
  EndTypeScale = 1
  KinkLength = 5
  LockPosition = false
  OriginX = -663.294
  OriginY = -2.93551
  Rotation = 0
  ScaleType = 0
  ShapeScale = 1
  SourceView = -> View009
  Text = Оборотная сторона
  TextWrapLen = -1
  X = -348.376
  Y = -169.899
FEATURE [TechDraw::DrawPage] Page003  label="pillar_page"
  KeepUpdated = true
  NextBalloonIndex = 7
  ProjectionType = 0
  Template = -> Template002
  Views = -> [View009,View010,View011,View012,Balloon003,Dimension014,Dimension015,Balloon004]
FEATURE [TechDraw::DrawViewPart] View013
  CoarseView = false
  Direction = (0.57735,-0.57735,0.57735)
  Focus = 100
  HardHidden = false
  IsoCount = 0
  IsoHidden = false
  IsoVisible = false
  LockPosition = false
  Perspective = false
  Rotation = 0
  ScaleType = 0
  ScrubCount = 0
  SeamHidden = false
  SeamVisible = true
  SmoothHidden = false
  SmoothVisible = true
  X = 182.024
  XDirection = (0.707107,0.707107,0)
  XSource = -> [Link002]
  Y = 111.253
FEATURE [TechDraw::DrawViewPart] View014
  CoarseView = false
  Direction = (1,0,0)
  Focus = 100
  HardHidden = false
  IsoCount = 0
  IsoHidden = false
  IsoVisible = false
  LockPosition = false
  Perspective = false
  Rotation = 0
  ScaleType = 0
  ScrubCount = 0
  SeamHidden = false
  SeamVisible = true
  SmoothHidden = false
  SmoothVisible = true
  X = 71.9436
  XDirection = (0,1,1e-06)
  XSource = -> [Link002]
  Y = 106.184
FEATURE [TechDraw::DrawViewBalloon] Balloon005
  BubbleShape = 3
  EndType = 0
  EndTypeScale = 1
  KinkLength = 5
  LockPosition = false
  OriginX = -20.8037
  OriginY = 1.41747
  Rotation = 0
  ScaleType = 0
  ShapeScale = 1
  SourceView = -> View013
  Text = Лицевая сторона
  TextWrapLen = -1
  X = 33.0581
  Y = 22.871
FEATURE [TechDraw::DrawPage] Page004  label="pillar_bottom_page"
  KeepUpdated = true
  NextBalloonIndex = 2
  ProjectionType = 0
  Template = -> Template002
  Views = -> [View013,View014,Balloon005]
FEATURE [Part::Mirroring] Part__Mirroring  label="pillar_bottom_mirror_body"
  Base = (0,0,0)
  Normal = (1,0,0)
  Source = -> Link002
FEATURE [TechDraw::DrawViewPart] View015
  CoarseView = false
  Direction = (0.57735,-0.57735,0.57735)
  Focus = 100
  HardHidden = false
  IsoCount = 0
  IsoHidden = false
  IsoVisible = false
  LockPosition = false
  Perspective = false
  Rotation = 0
  ScaleType = 0
  ScrubCount = 0
  SeamHidden = false
  SeamVisible = true
  SmoothHidden = false
  SmoothVisible = true
  Source = -> [Part__Mirroring]
  X = 220
  XDirection = (0.707106,0.707107,1.1547e-06)
  Y = 105
FEATURE [TechDraw::DrawViewPart] View016
  CoarseView = false
  Direction = (1,0,0)
  Focus = 100
  HardHidden = false
  IsoCount = 0
  IsoHidden = false
  IsoVisible = false
  LockPosition = false
  Perspective = false
  Rotation = 0
  ScaleType = 0
  ScrubCount = 0
  SeamHidden = false
  SeamVisible = true
  SmoothHidden = false
  SmoothVisible = true
  Source = -> [Part__Mirroring]
  X = 90
  XDirection = (0,1,0)
  Y = 105
FEATURE [TechDraw::DrawViewBalloon] Balloon006
  BubbleShape = 3
  EndType = 0
  EndTypeScale = 1
  KinkLength = 5
  LockPosition = false
  OriginX = -2.73031
  OriginY = -3.23534
  Rotation = 0
  ScaleType = 0
  ShapeScale = 1
  SourceView = -> View015
  Text = Лицевая сторона
  TextWrapLen = -1
  X = -58.3551
  Y = 58.8019
FEATURE [TechDraw::DrawPage] Page006  label="pillar_bottom_mirror_page"
  KeepUpdated = true
  NextBalloonIndex = 3
  ProjectionType = 0
  Template = -> Template002
  Views = -> [View015,View016,Balloon006]
FEATURE [Part::Mirroring] Part__Mirroring002  label="top_dec_corner_mirror"
  Base = (0,0,0)
  Normal = (1,0,0)
  Source = -> Link001
FEATURE [Part::Mirroring] Part__Mirroring003  label="top_dec_corner_mirror_unfold"
  Base = (0,0,0)
  Normal = (0,1,0)
  Source = -> Unfold002
FEATURE [Sketcher::SketchObject] MirroredSketch001  label="top_dec_mirror_sketch"
  FullyConstrained = false
  sketch-geometry (16):
    g0: LineSegment StartX=1591 StartY=65.3772 StartZ=0 EndX=1681 EndY=65.3772 EndZ=0
    g1: BSplineCurve PolesCount=26 KnotsCount=9 Degree=4 IsPeriodic=0
    g2: BSplineCurve PolesCount=26 KnotsCount=9 Degree=4 IsPeriodic=0
    g3: LineSegment StartX=1594 StartY=18.3 StartZ=0 EndX=1594 EndY=-34.5 EndZ=0
    g4: ArcOfCircle CenterX=1597 CenterY=-34.5 CenterZ=0 NormalX=0 NormalY=0 NormalZ=1 AngleXU=0 Radius=3 StartAngle=3.14159 EndAngle=4.71239
    g5: ArcOfCircle CenterX=1580.17 CenterY=18.3 CenterZ=0 NormalX=0 NormalY=0 NormalZ=1 AngleXU=1.5708 Radius=13.8267 StartAngle=4.71239 EndAngle=5.38367
    g6: LineSegment StartX=1597 StartY=-37.5 StartZ=0 EndX=1681 EndY=-37.5 EndZ=0
    g7: ArcOfCircle CenterX=1601.83 CenterY=35.5 CenterZ=0 NormalX=0 NormalY=0 NormalZ=1 AngleXU=1.5708 Radius=13.8267 StartAngle=1.5708 EndAngle=2.24207
    g8: BSplineCurve PolesCount=26 KnotsCount=9 Degree=4 IsPeriodic=0
    g9: Circle CenterX=1605 CenterY=-12.5 CenterZ=0 NormalX=0 NormalY=0 NormalZ=1 AngleXU=1.5708 Radius=1.8
    g10: Circle CenterX=1605 CenterY=12.5 CenterZ=0 NormalX=0 NormalY=0 NormalZ=1 AngleXU=1.5708 Radius=1.8
    g11: Circle CenterX=1674 CenterY=50.3772 CenterZ=0 NormalX=0 NormalY=0 NormalZ=-1 AngleXU=0 Radius=1.7
    g12: Circle CenterX=1604 CenterY=50.3772 CenterZ=0 NormalX=0 NormalY=0 NormalZ=-1 AngleXU=0 Radius=1.7
    g13: Circle CenterX=1673 CenterY=0 CenterZ=0 NormalX=0 NormalY=0 NormalZ=1 AngleXU=1.5708 Radius=1.7
    g14: LineSegment StartX=1684 StartY=-34.5 StartZ=0 EndX=1684 EndY=62.3772 EndZ=0
    g15: LineSegment StartX=1588 StartY=62.3772 StartZ=0 EndX=1588 EndY=35.5 EndZ=0
FEATURE [TechDraw::DrawViewPart] View017
  CoarseView = false
  Direction = (0.57735,-0.57735,0.57735)
  Focus = 100
  HardHidden = false
  IsoCount = 0
  IsoHidden = false
  IsoVisible = false
  LockPosition = false
  Perspective = false
  Rotation = 0
  ScaleType = 0
  ScrubCount = 0
  SeamHidden = false
  SeamVisible = true
  SmoothHidden = false
  SmoothVisible = true
  Source = -> [Part__Mirroring002]
  X = 98.5
  XDirection = (0.707108,0.707104,-3.4641e-06)
  Y = 105
FEATURE [TechDraw::DrawViewPart] View018
  CoarseView = false
  Direction = (0,0,1)
  Focus = 100
  HardHidden = false
  IsoCount = 0
  IsoHidden = false
  IsoVisible = false
  LockPosition = false
  Perspective = false
  Rotation = 0
  ScaleType = 0
  ScrubCount = 0
  SeamHidden = false
  SeamVisible = true
  SmoothHidden = false
  SmoothVisible = true
  Source = -> [Part__Mirroring002]
  X = 208.5
  XDirection = (1,0,0)
  Y = 105
FEATURE [TechDraw::DrawViewBalloon] Balloon007
  BubbleShape = 3
  EndType = 0
  EndTypeScale = 1
  KinkLength = 5
  LockPosition = false
  OriginX = 3.75964
  OriginY = 17.1575
  Rotation = 0
  ScaleType = 0
  ShapeScale = 1
  SourceView = -> View017
  Text = Лицевая сторона
  TextWrapLen = -1
  X = 47.6874
  Y = 45.7211
FEATURE [TechDraw::DrawViewDimension] Dimension020
  AngleOverride = false
  Arbitrary = false
  ArbitraryTolerances = false
  BoxCorners = (2) [(-37.75,-14.5,-1e-07),(37.75,14.5,1e-07)]
  EqualTolerance = true
  ExtensionAngle = 0
  FormatSpec = %.2w
  FormatSpecOverTolerance = %+.2w
  FormatSpecUnderTolerance = %+.2w
  Inverted = false
  LineAngle = 0
  LockPosition = false
  MeasureType = 1
  OverTolerance = 0
  References2D = -> [View018]
  Rotation = 0
  ScaleType = 0
  TheoreticalExact = false
  Type = 1
  UnderTolerance = 0
  X = 0.165203
  Y = -27.4355
FEATURE [TechDraw::DrawViewDimension] Dimension021
  AngleOverride = false
  Arbitrary = false
  ArbitraryTolerances = false
  BoxCorners = (2) [(-37.75,-14.5,-1e-07),(37.75,14.5,1e-07)]
  EqualTolerance = true
  ExtensionAngle = 0
  FormatSpec = %.2w
  FormatSpecOverTolerance = %+.2w
  FormatSpecUnderTolerance = %+.2w
  Inverted = false
  LineAngle = 0
  LockPosition = false
  MeasureType = 1
  OverTolerance = 0
  References2D = -> [View018]
  Rotation = 0
  ScaleType = 0
  TheoreticalExact = false
  Type = 2
  UnderTolerance = 0
  X = 46.8537
  Y = 1.87878
FEATURE [TechDraw::DrawPage] Page007  label="top_dec_mirror_page"
  KeepUpdated = true
  NextBalloonIndex = 5
  ProjectionType = 0
  Template = -> Template002
  Views = -> [View017,View018,Balloon007,Dimension020,Dimension021]
FEATURE [App::DocumentObjectGroup] Group004  label="top_dec_unfolds"
  Group = -> [Unfold002,Unfold_Sketch002,Unfold_Sketch_bends002,Body002,Page002,Part__Mirroring002,Part__Mirroring003,MirroredSketch001,Page007]
FEATURE [TechDraw::DrawViewPart] View019
  CoarseView = false
  Direction = (0,0,1)
  Focus = 100
  HardHidden = false
  IsoCount = 0
  IsoHidden = false
  IsoVisible = false
  LockPosition = false
  Perspective = false
  Rotation = 0
  Scale = 3
  ScaleType = 2
  ScrubCount = 0
  SeamHidden = false
  SeamVisible = true
  SmoothHidden = false
  SmoothVisible = true
  X = 152.489
  XDirection = (1,0,0)
  XSource = -> [Link004]
  Y = 90.1614
FEATURE [TechDraw::DrawViewPart] View020
  CoarseView = false
  Direction = (-0.57735,-0.57735,0.57735)
  Focus = 100
  HardHidden = false
  IsoCount = 0
  IsoHidden = false
  IsoVisible = false
  LockPosition = false
  Perspective = false
  Rotation = 90
  Scale = 0.3
  ScaleType = 2
  ScrubCount = 0
  SeamHidden = false
  SeamVisible = true
  SmoothHidden = false
  SmoothVisible = true
  X = 146.126
  XDirection = (0.707107,-0.707107,0)
  XSource = -> [Link004]
  Y = 147.243
FEATURE [TechDraw::DrawViewDimension] Dimension022
  AngleOverride = false
  Arbitrary = false
  ArbitraryTolerances = false
  BoxCorners = (2) [(-55.65,-31.5,-1e-07),(55.65,31.5,1e-07)]
  EqualTolerance = true
  ExtensionAngle = 0
  FormatSpec = %.2w
  FormatSpecOverTolerance = %+.2w
  FormatSpecUnderTolerance = %+.2w
  Inverted = false
  LineAngle = 0
  LockPosition = false
  MeasureType = 1
  OverTolerance = 0
  References2D = -> [View019]
  Rotation = 0
  ScaleType = 0
  TheoreticalExact = false
  Type = 1
  UnderTolerance = 0
  X = 2.2001
  Y = -54.0026
FEATURE [TechDraw::DrawViewBalloon] Balloon008
  BubbleShape = 3
  EndType = 0
  EndTypeScale = 1
  KinkLength = 5
  LockPosition = false
  OriginX = 65.4387
  OriginY = 5.9603
  Rotation = 0
  ScaleType = 0
  ShapeScale = 1
  SourceView = -> View020
  Text = Лицевая сторона
  TextWrapLen = -1
  X = 289.194
  Y = 108.103
FEATURE [Part::Feature] Unfold006  label="pillar_bottom_unfold"
  shape: bbox 101 x 131.1 x 2.002 mm, 20 faces (baked)
FEATURE [PartDesign::FeatureBase] BaseFeature004
  BaseFeature = -> Unfold006
  Suppressed = false
  expr: BaseFeature = <<pillar_bottom_unfold>>._self
  expr: Placement = .BaseFeature.Placement
FEATURE [PartDesign::Body] Body004  label="pillar_bottom_Body"
  Group = -> [BaseFeature004]
  Origin = -> Origin004
  Tip = -> BaseFeature004
FEATURE [Part::Mirroring] Part__Mirroring001  label="pillar_bottom_mirror_unfold"
  Base = (0,0,0)
  Normal = (1,0,0)
  Source = -> Unfold006
  expr: Source = <<pillar_bottom_unfold>>._self
FEATURE [Sketcher::SketchObject] Unfold_Sketch_bends006  label="pillar_bottom_bends"
  FullyConstrained = false
  Placement = pos=(0,-0.141906,0.50765) rot=(1,0,0;0.272577rad)
  sketch-geometry (1):
    g0: LineSegment StartX=-50.5 StartY=-1.88568 StartZ=0 EndX=50.5 EndY=-1.88568 EndZ=0
FEATURE [Sketcher::SketchObject] Unfold_Sketch006  label="pillar_bottom_Sketch"
  ExternalGeometry = -> [Unfold_Sketch_bends006]
  FullyConstrained = false
  sketch-geometry (20):
    g0: ArcOfCircle CenterX=45.5 CenterY=0.0840704 CenterZ=0 NormalX=0 NormalY=0 NormalZ=1 AngleXU=-2e-16 Radius=5 StartAngle=0 EndAngle=1.13485
    g1: LineSegment StartX=-19.6724 StartY=35.9594 StartZ=0 EndX=47.6113 EndY=4.61643 EndZ=0
    g2: ArcOfCircle CenterX=-8.10401 CenterY=60.7931 CenterZ=0 NormalX=0 NormalY=0 NormalZ=1 AngleXU=-2e-16 Radius=27.396 StartAngle=3.14159 EndAngle=4.27645
    g3: LineSegment StartX=-35.5 StartY=101.084 StartZ=0 EndX=-35.5 EndY=60.7931 EndZ=0
    g4: ArcOfCircle CenterX=-40.5 CenterY=101.084 CenterZ=0 NormalX=0 NormalY=0 NormalZ=1 AngleXU=-2e-16 Radius=5 StartAngle=-2.7e-15 EndAngle=1.5708
    g5: LineSegment StartX=-40.5 StartY=106.084 StartZ=0 EndX=-45.5 EndY=106.084 EndZ=0
    g6: ArcOfCircle CenterX=-45.5 CenterY=101.084 CenterZ=0 NormalX=0 NormalY=0 NormalZ=1 AngleXU=-2e-16 Radius=5 StartAngle=1.5708 EndAngle=3.14159
    g7: LineSegment StartX=50.5 StartY=0.0840704 StartZ=0 EndX=50.5 EndY=-4 EndZ=0
    g8: ArcOfCircle CenterX=29.5 CenterY=-4 CenterZ=0 NormalX=0 NormalY=0 NormalZ=1 AngleXU=0 Radius=21 StartAngle=4.71239 EndAngle=6.28319
    g9: LineSegment StartX=29.5 StartY=-25 StartZ=0 EndX=-29.5 EndY=-25 EndZ=0
    g10: ArcOfCircle CenterX=-29.5 CenterY=-4 CenterZ=0 NormalX=0 NormalY=0 NormalZ=1 AngleXU=0 Radius=21 StartAngle=3.14159 EndAngle=4.71239
    g11: Circle CenterX=-40 CenterY=-12 CenterZ=0 NormalX=0 NormalY=0 NormalZ=1 AngleXU=0 Radius=2.75
    g12: Circle CenterX=40 CenterY=-12 CenterZ=0 NormalX=0 NormalY=0 NormalZ=1 AngleXU=0 Radius=2.75
    g13: Circle CenterX=-43 CenterY=36.4174 CenterZ=0 NormalX=0 NormalY=0 NormalZ=-1 AngleXU=-3.14159 Radius=1.7
    g14: Circle CenterX=-43 CenterY=67.7507 CenterZ=0 NormalX=0 NormalY=0 NormalZ=-1 AngleXU=-3.14159 Radius=1.7
    g15: Circle CenterX=-43 CenterY=99.0841 CenterZ=0 NormalX=0 NormalY=0 NormalZ=-1 AngleXU=-3.14159 Radius=1.7
    g16: Circle CenterX=-43 CenterY=5.08407 CenterZ=0 NormalX=0 NormalY=0 NormalZ=-1 AngleXU=-3.14159 Radius=1.7
    g17: LineSegment StartX=-50.5 StartY=-4 StartZ=0 EndX=-50.5 EndY=101.084 EndZ=0
    g18: LineSegment StartX=-48.5 StartY=-1.95796 StartZ=0 EndX=-50.5 EndY=-1.95796 EndZ=0
    g19: LineSegment StartX=48.5 StartY=-1.95796 StartZ=0 EndX=50.5 EndY=-1.95796 EndZ=0
  constraints (18):
    c: Coincident(g10,g17)
    c: Coincident(g6,g17)
    c: Coincident(g5,g6)
    c: Coincident(g4,g5)
    c: Coincident(g2,g3)
    c: Coincident(g3,g4)
    c: Coincident(g9,g10)
    c: Coincident(g1,g2)
    c: Coincident(g8,g9)
    c: Coincident(g0,g1)
    c: Coincident(g7,g8)
    c: Coincident(g0,g7)
    c: Coincident(g19,g-3)
    c: PointOnObject(g19,g-3)
    c: Coincident(g18,g-3)
    c: PointOnObject(g18,g-3)
    c: Equal(g18,g19)
    c: Distance(g19) = 2
FEATURE [Sketcher::SketchObject] MirroredSketch002  label="pillar_bottom_mirror_sketch"
  FullyConstrained = false
  sketch-geometry (18):
    g0: ArcOfCircle CenterX=-45.5 CenterY=0.0840704 CenterZ=0 NormalX=0 NormalY=0 NormalZ=1 AngleXU=-2e-16 Radius=5 StartAngle=2.00674 EndAngle=3.14159
    g1: LineSegment StartX=19.6724 StartY=35.9594 StartZ=0 EndX=-47.6113 EndY=4.61643 EndZ=0
    g2: ArcOfCircle CenterX=8.10401 CenterY=60.7931 CenterZ=0 NormalX=0 NormalY=0 NormalZ=1 AngleXU=-2e-16 Radius=27.396 StartAngle=5.14833 EndAngle=6.28319
    g3: LineSegment StartX=35.5 StartY=101.084 StartZ=0 EndX=35.5 EndY=60.7931 EndZ=0
    g4: ArcOfCircle CenterX=40.5 CenterY=101.084 CenterZ=0 NormalX=0 NormalY=0 NormalZ=1 AngleXU=-2e-16 Radius=5 StartAngle=1.5708 EndAngle=3.14159
    g5: LineSegment StartX=40.5 StartY=106.084 StartZ=0 EndX=45.5 EndY=106.084 EndZ=0
    g6: ArcOfCircle CenterX=45.5 CenterY=101.084 CenterZ=0 NormalX=0 NormalY=0 NormalZ=1 AngleXU=-2e-16 Radius=5 StartAngle=2e-16 EndAngle=1.5708
    g7: LineSegment StartX=-50.5 StartY=0.0840704 StartZ=0 EndX=-50.5 EndY=-4 EndZ=0
    g8: ArcOfCircle CenterX=-29.5 CenterY=-4 CenterZ=0 NormalX=0 NormalY=0 NormalZ=1 AngleXU=0 Radius=21 StartAngle=3.14159 EndAngle=4.71239
    g9: LineSegment StartX=-29.5 StartY=-25 StartZ=0 EndX=29.5 EndY=-25 EndZ=0
    g10: ArcOfCircle CenterX=29.5 CenterY=-4 CenterZ=0 NormalX=0 NormalY=0 NormalZ=1 AngleXU=0 Radius=21 StartAngle=4.71239 EndAngle=6.28319
    g11: Circle CenterX=40 CenterY=-12 CenterZ=0 NormalX=0 NormalY=0 NormalZ=1 AngleXU=0 Radius=2.75
    g12: Circle CenterX=-40 CenterY=-12 CenterZ=0 NormalX=0 NormalY=0 NormalZ=1 AngleXU=0 Radius=2.75
    g13: Circle CenterX=43 CenterY=36.4174 CenterZ=0 NormalX=0 NormalY=0 NormalZ=-1 AngleXU=-3.14159 Radius=1.7
    g14: Circle CenterX=43 CenterY=67.7507 CenterZ=0 NormalX=0 NormalY=0 NormalZ=-1 AngleXU=-3.14159 Radius=1.7
    g15: Circle CenterX=43 CenterY=99.0841 CenterZ=0 NormalX=0 NormalY=0 NormalZ=-1 AngleXU=-3.14159 Radius=1.7
    g16: Circle CenterX=43 CenterY=5.08407 CenterZ=0 NormalX=0 NormalY=0 NormalZ=-1 AngleXU=-3.14159 Radius=1.7
    g17: LineSegment StartX=50.5 StartY=-4 StartZ=0 EndX=50.5 EndY=101.084 EndZ=0
FEATURE [App::DocumentObjectGroup] Group006  label="pillar_bottom_unfolds"
  Group = -> [Body004,Part__Mirroring001,Part__Mirroring,Unfold_Sketch006,Unfold_Sketch_bends006,MirroredSketch002]
FEATURE [TechDraw::DrawViewBalloon] Balloon009
  BubbleShape = 3
  EndType = 0
  EndTypeScale = 1
  KinkLength = 5
  LockPosition = false
  OriginX = -17.4642
  OriginY = -9.41421
  Rotation = 0
  ScaleType = 0
  ShapeScale = 1
  SourceView = -> View019
  Text = Оборотная сторона
  TextWrapLen = -1
  X = 0.143924
  Y = -5.00672
FEATURE [TechDraw::DrawPage] Page005  label="dec_corner_page"
  KeepUpdated = true
  NextBalloonIndex = 4
  ProjectionType = 0
  Template = -> Template002
  Views = -> [View019,View020,Dimension022,Balloon008,Balloon009]
FEATURE [App::DocumentObjectGroup] Group007  label="dec_corner_unfolds"
  Group = -> [Unfold_Sketch_bends005,Unfold005,Unfold_Sketch005,Body005,Page005]
FEATURE [TechDraw::DrawViewBalloon] Balloon010
  BubbleShape = 3
  EndType = 0
  EndTypeScale = 1
  KinkLength = 5
  LockPosition = false
  OriginX = -28.4686
  OriginY = -32.6313
  Rotation = 0
  ScaleType = 0
  ShapeScale = 1
  SourceView = -> View003
  Text = Оборотная сторона
  TextWrapLen = -1
  X = -84.4203
  Y = -17.114
FEATURE [TechDraw::DrawPage] Page001  label="pillar_top_page"
  KeepUpdated = true
  NextBalloonIndex = 3
  ProjectionType = 0
  Template = -> Template001
  Views = -> [View001,View002,View003,View004,Dimension,Dimension001,Dimension002,Balloon010]
FEATURE [App::Link] Link006  label="basement_amplifier_old"
  LinkedObject = -> <external composit_full_size3.FCStd>#Body088
FEATURE [TechDraw::DrawViewPart] View021
  CoarseView = false
  Direction = (-0.57735,-0.57735,0.57735)
  Focus = 100
  HardHidden = false
  IsoCount = 0
  IsoHidden = false
  IsoVisible = false
  LockPosition = false
  Perspective = false
  Rotation = 0
  ScaleType = 0
  ScrubCount = 0
  SeamHidden = false
  SeamVisible = true
  SmoothHidden = false
  SmoothVisible = true
  X = 148.5
  XDirection = (0.707107,-0.707107,-5.7735e-07)
  XSource = -> [Link006]
  Y = 119.201
FEATURE [TechDraw::DrawViewPart] View022
  CoarseView = false
  Direction = (0,-1,0)
  Focus = 100
  HardHidden = false
  IsoCount = 0
  IsoHidden = false
  IsoVisible = false
  LockPosition = false
  Perspective = false
  Rotation = 0
  ScaleType = 0
  ScrubCount = 0
  SeamHidden = false
  SeamVisible = true
  SmoothHidden = false
  SmoothVisible = true
  X = 62.8212
  XDirection = (1,0,-1e-06)
  XSource = -> [Link006]
  Y = 59.496
FEATURE [TechDraw::DrawViewDimension] Dimension024
  AngleOverride = false
  Arbitrary = false
  ArbitraryTolerances = false
  BoxCorners = (2) [(-18,-7.50002,-1e-07),(18,7.50002,1e-07)]
  EqualTolerance = true
  ExtensionAngle = 0
  FormatSpec = %.2w
  FormatSpecOverTolerance = %+.2w
  FormatSpecUnderTolerance = %+.2w
  Inverted = false
  LineAngle = 0
  LockPosition = false
  MeasureType = 1
  OverTolerance = 0
  References2D = -> [View022]
  Rotation = 0
  ScaleType = 0
  TheoreticalExact = false
  Type = 1
  UnderTolerance = 0
  X = -0.224498
  Y = -17.7255
FEATURE [TechDraw::DrawViewDimension] Dimension025
  AngleOverride = false
  Arbitrary = false
  ArbitraryTolerances = false
  BoxCorners = (2) [(-18,-7.50002,-1e-07),(18,7.50002,1e-07)]
  EqualTolerance = true
  ExtensionAngle = 0
  FormatSpec = %.2w
  FormatSpecOverTolerance = %+.2w
  FormatSpecUnderTolerance = %+.2w
  Inverted = false
  LineAngle = 0
  LockPosition = false
  MeasureType = 1
  OverTolerance = 0
  References2D = -> [View022]
  Rotation = 0
  ScaleType = 0
  TheoreticalExact = false
  Type = 2
  UnderTolerance = 0
  X = 27.4497
  Y = 1.153
FEATURE [TechDraw::DrawPage] Page008  label="basement_amplifier_old_page"
  KeepUpdated = true
  NextBalloonIndex = 7
  ProjectionType = 0
  Template = -> Template002
  Views = -> [View021,View022,Dimension024,Dimension025]
FEATURE [Part::Feature] Unfold008  label="basement_amplifier_old_unfold"
  Placement = pos=(0,0,0) rot=(0,0,-1;1.5708rad)
  shape: bbox 245 x 58.17 x 2 mm, 26 faces (baked)
FEATURE [PartDesign::FeatureBase] BaseFeature006
  BaseFeature = -> Unfold008
  Placement = pos=(0,0,0) rot=(0,0,-1;1.5708rad)
  Suppressed = false
  expr: BaseFeature = <<basement_amplifier_old_unfold>>._self
  expr: Placement = .BaseFeature.Placement
FEATURE [PartDesign::Body] Body006  label="basement_amplifier_old_body"
  Group = -> [BaseFeature006]
  Origin = -> Origin006
  Tip = -> BaseFeature006
FEATURE [Sketcher::SketchObject] Unfold_Sketch008  label="basement_amplifier_old_sketch"
  FullyConstrained = false
  sketch-geometry (24):
    g0: ArcOfCircle CenterX=-117.5 CenterY=18.0841 CenterZ=0 NormalX=0 NormalY=0 NormalZ=1 AngleXU=0 Radius=5 StartAngle=2.35619 EndAngle=3.14159
    g1: LineSegment StartX=-121.036 StartY=21.6196 StartZ=0 EndX=-115.036 EndY=27.6196 EndZ=0
    g2: ArcOfCircle CenterX=-111.5 CenterY=24.0841 CenterZ=0 NormalX=0 NormalY=0 NormalZ=1 AngleXU=0 Radius=5 StartAngle=1.5708 EndAngle=2.35619
    g3: LineSegment StartX=111.5 StartY=29.0841 StartZ=0 EndX=-111.5 EndY=29.0841 EndZ=0
    g4: ArcOfCircle CenterX=111.5 CenterY=24.0841 CenterZ=0 NormalX=0 NormalY=0 NormalZ=1 AngleXU=0 Radius=5 StartAngle=0.785398 EndAngle=1.5708
    g5: LineSegment StartX=121.036 StartY=21.6196 StartZ=0 EndX=115.036 EndY=27.6196 EndZ=0
    g6: ArcOfCircle CenterX=117.5 CenterY=18.0841 CenterZ=0 NormalX=0 NormalY=0 NormalZ=1 AngleXU=0 Radius=5 StartAngle=1e-16 EndAngle=0.785398
    g7: LineSegment StartX=-122.5 StartY=18.0841 StartZ=0 EndX=-122.5 EndY=-18.0841 EndZ=0
    g8: ArcOfCircle CenterX=-117.5 CenterY=-18.0841 CenterZ=0 NormalX=0 NormalY=0 NormalZ=1 AngleXU=0 Radius=5 StartAngle=3.14159 EndAngle=3.92699
    g9: LineSegment StartX=-115.036 StartY=-27.6196 StartZ=0 EndX=-121.036 EndY=-21.6196 EndZ=0
    g10: ArcOfCircle CenterX=-111.5 CenterY=-24.0841 CenterZ=0 NormalX=0 NormalY=0 NormalZ=1 AngleXU=0 Radius=5 StartAngle=3.92699 EndAngle=4.71239
    g11: LineSegment StartX=111.5 StartY=-29.0841 StartZ=0 EndX=-111.5 EndY=-29.0841 EndZ=0
    g12: ArcOfCircle CenterX=111.5 CenterY=-24.0841 CenterZ=0 NormalX=0 NormalY=0 NormalZ=1 AngleXU=0 Radius=5 StartAngle=4.71239 EndAngle=5.49779
    g13: LineSegment StartX=115.036 StartY=-27.6196 StartZ=0 EndX=121.036 EndY=-21.6196 EndZ=0
    g14: ArcOfCircle CenterX=117.5 CenterY=-18.0841 CenterZ=0 NormalX=0 NormalY=0 NormalZ=1 AngleXU=0 Radius=5 StartAngle=5.49779 EndAngle=6.28319
    g15: LineSegment StartX=122.5 StartY=-18.0841 StartZ=0 EndX=122.5 EndY=18.0841 EndZ=0
    g16: Circle CenterX=-92.5 CenterY=0 CenterZ=0 NormalX=0 NormalY=0 NormalZ=-1 AngleXU=-1.5708 Radius=4
    g17: Circle CenterX=-115.5 CenterY=9 CenterZ=0 NormalX=0 NormalY=0 NormalZ=-1 AngleXU=-1.5708 Radius=2.5
    g18: Circle CenterX=-115.5 CenterY=-9 CenterZ=0 NormalX=0 NormalY=0 NormalZ=-1 AngleXU=-1.5708 Radius=2.5
    g19: Circle CenterX=0 CenterY=9 CenterZ=0 NormalX=0 NormalY=0 NormalZ=-1 AngleXU=-1.5708 Radius=2.5
    g20: Circle CenterX=115.5 CenterY=9 CenterZ=0 NormalX=0 NormalY=0 NormalZ=-1 AngleXU=-1.5708 Radius=2.5
    g21: Circle CenterX=0 CenterY=-9 CenterZ=0 NormalX=0 NormalY=0 NormalZ=-1 AngleXU=-1.5708 Radius=2.5
    g22: Circle CenterX=92.5 CenterY=0 CenterZ=0 NormalX=0 NormalY=0 NormalZ=-1 AngleXU=-1.5708 Radius=2.5
    g23: Circle CenterX=115.5 CenterY=-9 CenterZ=0 NormalX=0 NormalY=0 NormalZ=-1 AngleXU=-1.5708 Radius=2.5
  constraints (16):
    c: Coincident(g7,g8)
    c: Coincident(g0,g7)
    c: Coincident(g8,g9)
    c: Coincident(g0,g1)
    c: Coincident(g9,g10)
    c: Coincident(g1,g2)
    c: Coincident(g10,g11)
    c: Coincident(g2,g3)
    c: Coincident(g11,g12)
    c: Coincident(g3,g4)
    c: Coincident(g12,g13)
    c: Coincident(g4,g5)
    c: Coincident(g13,g14)
    c: Coincident(g5,g6)
    c: Coincident(g14,g15)
    c: Coincident(g6,g15)
FEATURE [Sketcher::SketchObject] Unfold_Sketch_bends008  label="basement_amplifier_old_bend"
  FullyConstrained = false
  sketch-geometry (2):
    g0: LineSegment StartX=-122.5 StartY=16.042 StartZ=0 EndX=122.5 EndY=16.042 EndZ=0
    g1: LineSegment StartX=-122.5 StartY=-16.042 StartZ=0 EndX=122.5 EndY=-16.042 EndZ=0
FEATURE [App::DocumentObjectGroup] Group008  label="basement_amplifier_old_unfolds"
  Group = -> [Body006,Page008,Unfold008,Unfold_Sketch008,Unfold_Sketch_bends008]
FEATURE [Part::Feature] Unfold009  label="pillar_unfold"
  Placement = pos=(0,0,0) rot=(0.57735,0.57735,0.57735;2.0944rad)
  shape: bbox 1684 x 75 x 2.247 mm, 52 faces (baked)
FEATURE [PartDesign::FeatureBase] BaseFeature003
  BaseFeature = -> Unfold009
  Placement = pos=(0,0,0) rot=(0.57735,0.57735,0.57735;2.0944rad)
  Suppressed = false
  expr: BaseFeature = <<pillar_unfold>>._self
  expr: Placement = .BaseFeature.Placement
FEATURE [PartDesign::Body] Body003  label="pillar_Body"
  Group = -> [BaseFeature003]
  Origin = -> Origin003
  Tip = -> BaseFeature003
FEATURE [Sketcher::SketchObject] Unfold_Sketch_bends009  label="pillar_bends"
  FullyConstrained = false
  sketch-geometry (2):
    g0: LineSegment StartX=1594 StartY=-16.342 StartZ=0 EndX=0 EndY=-16.342 EndZ=0
    g1: LineSegment StartX=1594 StartY=16.342 StartZ=0 EndX=0 EndY=16.342 EndZ=0
FEATURE [Sketcher::SketchObject] Unfold_Sketch009  label="pillar_Sketch"
  ExternalGeometry = -> [Unfold_Sketch_bends009]
  FullyConstrained = false
  sketch-geometry (54):
    g0: LineSegment StartX=5 StartY=-33.3841 StartZ=0 EndX=1589 EndY=-33.3841 EndZ=0
    g1: LineSegment StartX=1594 StartY=-28.3841 StartZ=0 EndX=1594 EndY=-14.3 EndZ=0
    g2: LineSegment StartX=1596 StartY=-14.3 StartZ=0 EndX=1594 EndY=-14.3 EndZ=0
    g3: LineSegment StartX=1596 StartY=-34.5 StartZ=0 EndX=1596 EndY=-14.3 EndZ=0
    g4: ArcOfCircle CenterX=1599 CenterY=-34.5 CenterZ=0 NormalX=0 NormalY=0 NormalZ=1 AngleXU=1.5708 Radius=3 StartAngle=1.5708 EndAngle=3.14159
    g5: LineSegment StartX=1681 StartY=-37.5 StartZ=0 EndX=1599 EndY=-37.5 EndZ=0
    g6: ArcOfCircle CenterX=1681 CenterY=-34.5 CenterZ=0 NormalX=0 NormalY=0 NormalZ=1 AngleXU=1.5708 Radius=3 StartAngle=3.14159 EndAngle=4.71239
    g7: LineSegment StartX=1684 StartY=34.5 StartZ=0 EndX=1684 EndY=-34.5 EndZ=0
    g8: ArcOfCircle CenterX=1681 CenterY=34.5 CenterZ=0 NormalX=0 NormalY=0 NormalZ=1 AngleXU=1.5708 Radius=3 StartAngle=4.71239 EndAngle=6.28319
    g9: LineSegment StartX=1599 StartY=37.5 StartZ=0 EndX=1681 EndY=37.5 EndZ=0
    g10: ArcOfCircle CenterX=1599 CenterY=34.5 CenterZ=0 NormalX=0 NormalY=0 NormalZ=1 AngleXU=1.5708 Radius=3 StartAngle=8.4928e-12 EndAngle=1.5708
    g11: LineSegment StartX=1596 StartY=14.3 StartZ=0 EndX=1596 EndY=34.5 EndZ=0
    g12: LineSegment StartX=1594 StartY=14.3 StartZ=0 EndX=1596 EndY=14.3 EndZ=0
    g13: LineSegment StartX=1594 StartY=14.3 StartZ=0 EndX=1594 EndY=28.3841 EndZ=0
    g14: LineSegment StartX=5 StartY=33.3841 StartZ=0 EndX=1589 EndY=33.3841 EndZ=0
    g15: LineSegment StartX=-1e-16 StartY=-28.3841 StartZ=0 EndX=-2.85245e-09 EndY=28.3841 EndZ=0
    g16: ArcOfCircle CenterX=473 CenterY=-2.274e-13 CenterZ=0 NormalX=0 NormalY=0 NormalZ=1 AngleXU=1.5708 Radius=1.8 StartAngle=3.14159 EndAngle=6.28319
    g17: LineSegment StartX=473 StartY=-1.8 StartZ=0 EndX=465 EndY=-1.8 EndZ=0
    g18: ArcOfCircle CenterX=465 CenterY=-2.274e-13 CenterZ=0 NormalX=0 NormalY=0 NormalZ=1 AngleXU=1.5708 Radius=1.8 StartAngle=0 EndAngle=3.14159
    g19: LineSegment StartX=465 StartY=1.8 StartZ=0 EndX=473 EndY=1.8 EndZ=0
    g20: Circle CenterX=1605 CenterY=-12.5 CenterZ=0 NormalX=0 NormalY=0 NormalZ=1 AngleXU=1.5708 Radius=1.8
    g21: Circle CenterX=1605 CenterY=12.5 CenterZ=0 NormalX=0 NormalY=0 NormalZ=1 AngleXU=1.5708 Radius=1.8
    g22: Circle CenterX=1673 CenterY=0 CenterZ=0 NormalX=0 NormalY=0 NormalZ=1 AngleXU=1.5708 Radius=1.7
    g23: Circle CenterX=764.25 CenterY=0 CenterZ=0 NormalX=0 NormalY=0 NormalZ=1 AngleXU=1.5708 Radius=1.7
    g24: Circle CenterX=1037.5 CenterY=0 CenterZ=0 NormalX=0 NormalY=0 NormalZ=1 AngleXU=1.5708 Radius=1.7
    g25: Circle CenterX=1310.75 CenterY=0 CenterZ=0 NormalX=0 NormalY=0 NormalZ=1 AngleXU=1.5708 Radius=1.7
    g26: Circle CenterX=1584 CenterY=0 CenterZ=0 NormalX=0 NormalY=0 NormalZ=1 AngleXU=1.5708 Radius=1.7
    g27: Circle CenterX=1584 CenterY=-26.2689 CenterZ=0 NormalX=0 NormalY=0 NormalZ=1 AngleXU=1.5708 Radius=1.7
    g28: Circle CenterX=764.25 CenterY=26.2689 CenterZ=0 NormalX=0 NormalY=0 NormalZ=1 AngleXU=-1.5708 Radius=1.7
    g29: Circle CenterX=1037.5 CenterY=26.2689 CenterZ=0 NormalX=0 NormalY=0 NormalZ=1 AngleXU=-1.5708 Radius=1.7
    g30: Circle CenterX=1310.75 CenterY=26.2689 CenterZ=0 NormalX=0 NormalY=0 NormalZ=1 AngleXU=-1.5708 Radius=1.7
    g31: Circle CenterX=1584 CenterY=26.2689 CenterZ=0 NormalX=0 NormalY=0 NormalZ=1 AngleXU=-1.5708 Radius=1.7
    g32: Circle CenterX=764.25 CenterY=-26.2689 CenterZ=0 NormalX=0 NormalY=0 NormalZ=1 AngleXU=1.5708 Radius=1.7
    g33: Circle CenterX=1037.5 CenterY=-26.2689 CenterZ=0 NormalX=0 NormalY=0 NormalZ=1 AngleXU=1.5708 Radius=1.7
    g34: Circle CenterX=1310.75 CenterY=-26.2689 CenterZ=0 NormalX=0 NormalY=0 NormalZ=1 AngleXU=1.5708 Radius=1.7
    g35: Circle CenterX=40.3333 CenterY=-25.8841 CenterZ=0 NormalX=0 NormalY=0 NormalZ=-1 AngleXU=0 Radius=1.7
    g36: Circle CenterX=71.6667 CenterY=-25.8841 CenterZ=0 NormalX=0 NormalY=0 NormalZ=-1 AngleXU=0 Radius=1.7
    g37: Circle CenterX=103 CenterY=-25.8841 CenterZ=0 NormalX=0 NormalY=0 NormalZ=-1 AngleXU=0 Radius=1.7
    g38: Circle CenterX=103 CenterY=25.8841 CenterZ=0 NormalX=0 NormalY=0 NormalZ=1 AngleXU=-3.14159 Radius=1.7
    g39: Circle CenterX=71.6667 CenterY=25.8841 CenterZ=0 NormalX=0 NormalY=0 NormalZ=1 AngleXU=-3.14159 Radius=1.7
    g40: Circle CenterX=40.3333 CenterY=25.8841 CenterZ=0 NormalX=0 NormalY=0 NormalZ=1 AngleXU=-3.14159 Radius=1.7
    g41: Circle CenterX=9 CenterY=-25.8841 CenterZ=0 NormalX=0 NormalY=0 NormalZ=-1 AngleXU=0 Radius=1.7
    g42: Circle CenterX=9 CenterY=25.8841 CenterZ=0 NormalX=0 NormalY=0 NormalZ=1 AngleXU=-3.14159 Radius=1.7
    g43: Circle CenterX=491 CenterY=0 CenterZ=0 NormalX=0 NormalY=0 NormalZ=1 AngleXU=1.5708 Radius=1.7
    g44: Circle CenterX=491 CenterY=-26.2689 CenterZ=0 NormalX=0 NormalY=0 NormalZ=1 AngleXU=1.5708 Radius=1.7
    g45: Circle CenterX=491 CenterY=26.2689 CenterZ=0 NormalX=0 NormalY=0 NormalZ=1 AngleXU=-1.5708 Radius=1.7
    g46: LineSegment StartX=1594 StartY=-16.342 StartZ=0 EndX=1592 EndY=-16.342 EndZ=0
    g47: LineSegment StartX=1594 StartY=16.342 StartZ=0 EndX=1592 EndY=16.342 EndZ=0
    g48: LineSegment StartX=2 StartY=-16.342 StartZ=0 EndX=0 EndY=-16.342 EndZ=0
    g49: LineSegment StartX=2 StartY=16.342 StartZ=0 EndX=0 EndY=16.342 EndZ=0
    g50: ArcOfCircle CenterX=5 CenterY=-28.3841 CenterZ=0 NormalX=0 NormalY=0 NormalZ=1 AngleXU=0 Radius=5 StartAngle=3.14159 EndAngle=4.71239
    g51: ArcOfCircle CenterX=5 CenterY=28.3841 CenterZ=0 NormalX=0 NormalY=0 NormalZ=1 AngleXU=0 Radius=5 StartAngle=1.5708 EndAngle=3.14159
    g52: ArcOfCircle CenterX=1589 CenterY=28.3841 CenterZ=0 NormalX=0 NormalY=0 NormalZ=1 AngleXU=0 Radius=5 StartAngle=1.20819e-11 EndAngle=1.5708
    g53: ArcOfCircle CenterX=1589 CenterY=-28.3841 CenterZ=0 NormalX=0 NormalY=0 NormalZ=1 AngleXU=0 Radius=5 StartAngle=4.71239 EndAngle=6.28319
  constraints (41):
    c: Equal(g48,g49)
    c: Equal(g49,g46)
    c: Equal(g46,g47)
    c: Distance(g46) = 2
    c: Coincident(g46,g-4)
    c: Coincident(g47,g-3)
    c: Coincident(g48,g-4)
    c: Coincident(g49,g-3)
    c: PointOnObject(g48,g-4)
    c: PointOnObject(g49,g-3)
    c: PointOnObject(g47,g-3)
    c: PointOnObject(g46,g-4)
    c: Coincident(g17,g18)
    c: Coincident(g18,g19)
    c: Coincident(g16,g17)
    c: Coincident(g16,g19)
    c: Coincident(g1,g2)
    c: Coincident(g12,g13)
    c: Coincident(g3,g4)
    c: Coincident(g2,g3)
    c: Coincident(g11,g12)
    c: Coincident(g10,g11)
    c: Coincident(g4,g5)
    c: Coincident(g9,g10)
    c: Coincident(g5,g6)
    c: Coincident(g8,g9)
    c: Coincident(g6,g7)
    c: Coincident(g7,g8)
    c: Block(g0)
    c: Block(g1)
    c: Block(g13)
    c: Block(g14)
    c: Block(g15)
    c: Tangent(g50,g0) = -1.5708
    c: Tangent(g51,g15) = 1.5708
    c: Tangent(g51,g14) = 1.5708
    c: Tangent(g52,g14) = 1.5708
    c: Tangent(g52,g13) = -1.5708
    c: Coincident(g15,g50)
    c: Tangent(g53,g0) = -1.5708
    c: Tangent(g53,g1) = -1.5708
FEATURE [App::DocumentObjectGroup] Group005  label="pillar_unfolds"
  Group = -> [Body003,Page003,Unfold_Sketch009,Unfold_Sketch_bends009,Unfold009]
FEATURE [App::Link] Link007  label="door_base_pillar_material_0.45ansi"
  LinkedObject = -> <external composit_full_size3.FCStd>#Body095
FEATURE [Part::Feature] Unfold010  label="door_conn_unfold"
  Placement = pos=(0,0,287.05) rot=(-0.774597,0.447214,0.447214;1.82348rad)
  shape: bbox 78.8 x 1200 x 1.122 mm, 45 faces (baked)
FEATURE [Sketcher::SketchObject] Unfold_Sketch010  label="door_conn_Sketch"
  FullyConstrained = false
  sketch-geometry (43):
    g0: LineSegment StartX=-12.2485 StartY=1116 StartZ=0 EndX=-15.8985 EndY=1116 EndZ=0
    g1: ArcOfEllipse CenterX=-12.2459 CenterY=1114 CenterZ=0 NormalX=0 NormalY=0 NormalZ=1 MajorRadius=1.98967 MinorRadius=1.98889 AngleXU=-1.56979 StartAngle=1.57213 EndAngle=3.14181
    g2: ArcOfCircle CenterX=-15.8985 CenterY=1118 CenterZ=0 NormalX=0 NormalY=0 NormalZ=1 AngleXU=0 Radius=2 StartAngle=3.14159 EndAngle=4.71239
    g3: LineSegment StartX=-10.2485 StartY=2 StartZ=0 EndX=-10.2485 EndY=1114 EndZ=0
    g4: LineSegment StartX=-17.8985 StartY=1118 StartZ=0 EndX=-17.8985 EndY=1198 EndZ=0
    g5: ArcOfEllipse CenterX=-8.20967 CenterY=2.05669 CenterZ=0 NormalX=0 NormalY=0 NormalZ=1 MajorRadius=2.02499 MinorRadius=2.02067 AngleXU=-1.58995 StartAngle=4.7595 EndAngle=6.28319
    g6: BSplineCurve PolesCount=26 KnotsCount=9 Degree=4 IsPeriodic=0
    g7: ArcOfEllipse CenterX=34.9612 CenterY=1197.94 CenterZ=0 NormalX=0 NormalY=0 NormalZ=1 MajorRadius=2.02499 MinorRadius=2.02067 AngleXU=1.55165 StartAngle=4.7595 EndAngle=6.28319
    g8: LineSegment StartX=37 StartY=1137.47 StartZ=0 EndX=37 EndY=1198 EndZ=0
    g9: LineSegment StartX=53.2485 StartY=2 StartZ=0 EndX=53.2485 EndY=1114 EndZ=0
    g10: ArcOfCircle CenterX=51.2485 CenterY=2 CenterZ=0 NormalX=0 NormalY=0 NormalZ=1 AngleXU=-3.14159 Radius=2 StartAngle=1.5708 EndAngle=3.14159
    g11: ArcOfCircle CenterX=55.2485 CenterY=1114 CenterZ=0 NormalX=0 NormalY=0 NormalZ=1 AngleXU=-3.14159 Radius=2 StartAngle=4.71239 EndAngle=6.28319
    g12: LineSegment StartX=55.2485 StartY=1116 StartZ=0 EndX=58.8985 EndY=1116 EndZ=0
    g13: ArcOfCircle CenterX=58.8985 CenterY=1118 CenterZ=0 NormalX=0 NormalY=0 NormalZ=1 AngleXU=3.14159 Radius=2 StartAngle=1.5708 EndAngle=3.14159
    g14: LineSegment StartX=60.8985 StartY=1118 StartZ=0 EndX=60.8985 EndY=1135.47 EndZ=0
    g15: ArcOfCircle CenterX=58.8985 CenterY=1135.47 CenterZ=0 NormalX=0 NormalY=0 NormalZ=1 AngleXU=-3.14159 Radius=2 StartAngle=3.14159 EndAngle=4.71239
    g16: LineSegment StartX=23.2 StartY=12 StartZ=0 EndX=23.2 EndY=5 EndZ=0
    g17: ArcOfCircle CenterX=21.5 CenterY=5 CenterZ=0 NormalX=0 NormalY=0 NormalZ=1 AngleXU=1e-16 Radius=1.7 StartAngle=3.14159 EndAngle=6.28319
    g18: LineSegment StartX=19.8 StartY=5 StartZ=0 EndX=19.8 EndY=12 EndZ=0
    g19: ArcOfCircle CenterX=21.5 CenterY=12 CenterZ=0 NormalX=0 NormalY=0 NormalZ=1 AngleXU=1e-16 Radius=1.7 StartAngle=-3.38e-14 EndAngle=3.14159
    g20: Circle CenterX=32.5346 CenterY=1133.99 CenterZ=0 NormalX=0 NormalY=0 NormalZ=1 AngleXU=1e-16 Radius=2.5
    g21: Circle CenterX=48.0485 CenterY=578 CenterZ=0 NormalX=0 NormalY=0 NormalZ=1 AngleXU=-3.14159 Radius=1.7
    g22: Circle CenterX=45.0493 CenterY=1097.3 CenterZ=0 NormalX=0 NormalY=0 NormalZ=1 AngleXU=-3.14159 Radius=1.7
    g23: Circle CenterX=48.0485 CenterY=848 CenterZ=0 NormalX=0 NormalY=0 NormalZ=1 AngleXU=-3.14159 Radius=1.7
    g24: Circle CenterX=48.0485 CenterY=1118 CenterZ=0 NormalX=0 NormalY=0 NormalZ=1 AngleXU=-3.14159 Radius=1.7
    g25: Circle CenterX=48.5493 CenterY=1088 CenterZ=0 NormalX=0 NormalY=0 NormalZ=1 AngleXU=-3.14159 Radius=1.7
    g26: Circle CenterX=21.5 CenterY=715.8 CenterZ=0 NormalX=0 NormalY=0 NormalZ=1 AngleXU=1e-16 Radius=1.7
    g27: Circle CenterX=21.5 CenterY=950.4 CenterZ=0 NormalX=0 NormalY=0 NormalZ=1 AngleXU=1e-16 Radius=1.7
    g28: Circle CenterX=21.5 CenterY=1185 CenterZ=0 NormalX=0 NormalY=0 NormalZ=1 AngleXU=1e-16 Radius=1.7
    g29: Ellipse CenterX=-5.04845 CenterY=578 CenterZ=0 NormalX=0 NormalY=0 NormalZ=-1 MajorRadius=1.7 MinorRadius=1.7 AngleXU=-1.5708
    g30: Ellipse CenterX=-5.04845 CenterY=848 CenterZ=0 NormalX=0 NormalY=0 NormalZ=-1 MajorRadius=1.7 MinorRadius=1.7 AngleXU=-1.5708
    g31: Ellipse CenterX=-5.04845 CenterY=1118 CenterZ=0 NormalX=0 NormalY=0 NormalZ=-1 MajorRadius=1.7 MinorRadius=1.7 AngleXU=-1.5708
    g32: Circle CenterX=48.0485 CenterY=38 CenterZ=0 NormalX=0 NormalY=0 NormalZ=1 AngleXU=-3.14159 Radius=1.7
    g33: Ellipse CenterX=-5.04845 CenterY=38 CenterZ=0 NormalX=0 NormalY=0 NormalZ=-1 MajorRadius=1.7 MinorRadius=1.7 AngleXU=-1.5708
    g34: Circle CenterX=48.5493 CenterY=148 CenterZ=0 NormalX=0 NormalY=0 NormalZ=1 AngleXU=-3.14159 Radius=1.7
    g35: Circle CenterX=45.0493 CenterY=157.3 CenterZ=0 NormalX=0 NormalY=0 NormalZ=1 AngleXU=-3.14159 Radius=1.7
    g36: Circle CenterX=48.0485 CenterY=308 CenterZ=0 NormalX=0 NormalY=0 NormalZ=1 AngleXU=-3.14159 Radius=1.7
    g37: Circle CenterX=21.5 CenterY=246.6 CenterZ=0 NormalX=0 NormalY=0 NormalZ=1 AngleXU=1e-16 Radius=1.7
    g38: Circle CenterX=21.5 CenterY=481.2 CenterZ=0 NormalX=0 NormalY=0 NormalZ=1 AngleXU=1e-16 Radius=1.7
    g39: Ellipse CenterX=-5.04845 CenterY=308 CenterZ=0 NormalX=0 NormalY=0 NormalZ=-1 MajorRadius=1.7 MinorRadius=1.7 AngleXU=-1.5708
    g40: LineSegment StartX=-8.24845 StartY=0 StartZ=0 EndX=51.2485 EndY=0 EndZ=0
    g41: LineSegment StartX=37 StartY=1137.47 StartZ=0 EndX=58.8985 EndY=1137.47 EndZ=0
    g42: LineSegment StartX=-15.8985 StartY=1200 StartZ=0 EndX=35 EndY=1200 EndZ=0
FEATURE [Sketcher::SketchObject] Unfold_Sketch_bends010  label="door_conn_bends"
  FullyConstrained = false
  sketch-geometry (2):
    g0: LineSegment StartX=3.07577 StartY=1200 StartZ=0 EndX=3.07577 EndY=0 EndZ=0
    g1: LineSegment StartX=39.9242 StartY=1137.47 StartZ=0 EndX=39.9242 EndY=0 EndZ=0
FEATURE [PartDesign::FeatureBase] BaseFeature007
  BaseFeature = -> Unfold010
  Placement = pos=(0,0,287.05) rot=(-0.774597,0.447214,0.447214;1.82348rad)
  Suppressed = false
  expr: Placement = .BaseFeature.Placement
FEATURE [PartDesign::Body] Body007  label="door_conn_body"
  BaseFeature = -> Unfold010
  Group = -> [BaseFeature007]
  Origin = -> Origin007
  Tip = -> BaseFeature007
FEATURE [Part::Feature] Unfold011  label="door_base_pillar_to_hor_fix_Unfold"
  shape: bbox 44.86 x 40.53 x 1.002 mm, 22 faces (baked)
FEATURE [Sketcher::SketchObject] Unfold_Sketch011  label="door_base_pillar_to_hor_fix_Sketch"
  FullyConstrained = false
  sketch-geometry (20):
    g0: ArcOfCircle CenterX=31.6515 CenterY=338.872 CenterZ=0 NormalX=0 NormalY=0 NormalZ=1 AngleXU=0 Radius=2 StartAngle=3.14159 EndAngle=4.71239
    g1: LineSegment StartX=29.6515 StartY=338.872 StartZ=0 EndX=29.6515 EndY=350.506 EndZ=0
    g2: ArcOfCircle CenterX=31.6515 CenterY=350.506 CenterZ=0 NormalX=0 NormalY=0 NormalZ=1 AngleXU=0 Radius=2 StartAngle=1.5708 EndAngle=3.14159
    g3: LineSegment StartX=43.5 StartY=352.506 StartZ=0 EndX=44.5327 EndY=364.31 EndZ=0
    g4: LineSegment StartX=43.5 StartY=352.506 StartZ=0 EndX=31.6515 EndY=352.506 EndZ=0
    g5: LineSegment StartX=43.5 StartY=336.872 StartZ=0 EndX=31.6515 EndY=336.872 EndZ=0
    g6: LineSegment StartX=59.1109 StartY=326.596 StartZ=0 EndX=43.5 EndY=336.872 EndZ=0
    g7: ArcOfCircle CenterX=62.4098 CenterY=331.608 CenterZ=0 NormalX=0 NormalY=0 NormalZ=1 AngleXU=0 Radius=6 StartAngle=4.13024 EndAngle=5.83473
    g8: LineSegment StartX=67.8165 StartY=329.006 StartZ=0 EndX=73.921 EndY=341.694 EndZ=0
    g9: ArcOfCircle CenterX=68.5143 CenterY=344.295 CenterZ=0 NormalX=0 NormalY=0 NormalZ=1 AngleXU=0 Radius=6 StartAngle=5.83473 EndAngle=7.76672
    g10: LineSegment StartX=69.0372 StartY=350.272 StartZ=0 EndX=70.0699 EndY=362.075 EndZ=0
    g11: ArcOfCircle CenterX=68.0775 CenterY=362.25 CenterZ=0 NormalX=0 NormalY=0 NormalZ=1 AngleXU=-0.0872665 Radius=2 StartAngle=0 EndAngle=1.5708
    g12: LineSegment StartX=46.6994 StartY=366.128 StartZ=0 EndX=68.2518 EndY=364.242 EndZ=0
    g13: ArcOfCircle CenterX=46.525 CenterY=364.135 CenterZ=0 NormalX=0 NormalY=0 NormalZ=1 AngleXU=-0.0872665 Radius=2 StartAngle=1.5708 EndAngle=3.14159
    g14: Circle CenterX=65.0802 CenterY=359.501 CenterZ=0 NormalX=0 NormalY=0 NormalZ=1 AngleXU=-0.0872665 Radius=1.7
    g15: Circle CenterX=49.1411 CenterY=360.895 CenterZ=0 NormalX=0 NormalY=0 NormalZ=1 AngleXU=-0.0872665 Radius=1.7
    g16: Circle CenterX=51.5 CenterY=336.872 CenterZ=0 NormalX=0 NormalY=0 NormalZ=1 AngleXU=0 Radius=1.7
    g17: Circle CenterX=68.34 CenterY=342.303 CenterZ=0 NormalX=0 NormalY=0 NormalZ=1 AngleXU=0 Radius=1.7
    g18: Circle CenterX=34.6515 CenterY=345 CenterZ=0 NormalX=0 NormalY=0 NormalZ=-1 AngleXU=1.5708 Radius=1.7
    g19: Circle CenterX=62.5438 CenterY=331.451 CenterZ=0 NormalX=0 NormalY=0 NormalZ=1 AngleXU=0 Radius=1.7
FEATURE [Sketcher::SketchObject] Unfold_Sketch_bends011  label="door_base_pillar_to_hor_fix_bends"
  FullyConstrained = false
  sketch-geometry (2):
    g0: LineSegment StartX=41.5758 StartY=352.506 StartZ=0 EndX=41.5758 EndY=336.872 EndZ=0
    g1: LineSegment StartX=69.2049 StartY=352.189 StartZ=0 EndX=43.6677 EndY=354.423 EndZ=0
FEATURE [PartDesign::FeatureBase] BaseFeature008
  BaseFeature = -> Unfold011
  Suppressed = false
FEATURE [PartDesign::Body] Body008  label="door_base_pillar_to_hor_fix_body"
  BaseFeature = -> Unfold011
  Group = -> [BaseFeature008]
  Origin = -> Origin008
  Tip = -> BaseFeature008
FEATURE [Part::Feature] Unfold012  label="door_hor_unfold"
  shape: bbox 97.51 x 256 x 1 mm, 25 faces (baked)
FEATURE [Sketcher::SketchObject] Unfold_Sketch012  label="door_hor_Sketch"
  FullyConstrained = false
  sketch-geometry (23):
    g0: ArcOfCircle CenterX=257.838 CenterY=117.511 CenterZ=0 NormalX=0 NormalY=0 NormalZ=1 AngleXU=0.523599 Radius=2 StartAngle=1.8e-15 EndAngle=1.5708
    g1: LineSegment StartX=256.838 StartY=119.243 StartZ=0 EndX=250.43 EndY=115.543 EndZ=0
    g2: ArcOfCircle CenterX=251.43 CenterY=113.811 CenterZ=0 NormalX=0 NormalY=0 NormalZ=1 AngleXU=0.523599 Radius=2 StartAngle=1.5708 EndAngle=3.14159
    g3: LineSegment StartX=249.698 StartY=112.811 StartZ=0 EndX=258.122 EndY=98.2199 EndZ=0
    g4: LineSegment StartX=241.745 StartY=94.2601 StartZ=0 EndX=258.122 EndY=98.2199 EndZ=0
    g5: ArcOfCircle CenterX=242.215 CenterY=92.3161 CenterZ=0 NormalX=0 NormalY=0 NormalZ=1 AngleXU=1.80804 Radius=2 StartAngle=0 EndAngle=1.5708
    g6: LineSegment StartX=240.271 StartY=91.8461 StartZ=0 EndX=294.699 EndY=-133.25 EndZ=0
    g7: ArcOfCircle CenterX=296.643 CenterY=-132.779 CenterZ=0 NormalX=0 NormalY=0 NormalZ=1 AngleXU=1.80804 Radius=2 StartAngle=1.5708 EndAngle=3.14159
    g8: LineSegment StartX=297.113 StartY=-134.723 StartZ=0 EndX=313.489 EndY=-130.764 EndZ=0
    g9: LineSegment StartX=313.489 StartY=-130.764 StartZ=0 EndX=322.304 EndY=-135.853 EndZ=0
    g10: ArcOfCircle CenterX=324.804 CenterY=-131.523 CenterZ=0 NormalX=0 NormalY=0 NormalZ=1 AngleXU=0 Radius=5 StartAngle=4.18879 EndAngle=5.84685
    g11: LineSegment StartX=329.335 StartY=-133.636 StartZ=0 EndX=337.533 EndY=-116.056 EndZ=0
    g12: ArcOfCircle CenterX=335.72 CenterY=-115.211 CenterZ=0 NormalX=0 NormalY=0 NormalZ=1 AngleXU=-1.5708 Radius=2 StartAngle=1.13446 EndAngle=1.87927
    g13: LineSegment StartX=337.626 StartY=-114.604 StartZ=0 EndX=267.995 EndY=103.92 EndZ=0
    g14: LineSegment StartX=259.57 StartY=118.511 StartZ=0 EndX=267.995 EndY=103.92 EndZ=0
    g15: Circle CenterX=261.948 CenterY=107.991 CenterZ=0 NormalX=0 NormalY=0 NormalZ=1 AngleXU=0.523599 Radius=1.7
    g16: Circle CenterX=254.267 CenterY=114.295 CenterZ=0 NormalX=0 NormalY=0 NormalZ=1 AngleXU=0.523599 Radius=1.7
    g17: Circle CenterX=317.489 CenterY=-123.835 CenterZ=0 NormalX=0 NormalY=0 NormalZ=1 AngleXU=1.0472 Radius=1.7
    g18: Circle CenterX=318.317 CenterY=-111.561 CenterZ=0 NormalX=0 NormalY=0 NormalZ=1 AngleXU=1.0472 Radius=1.7
    g19: Circle CenterX=330.613 CenterY=-111.967 CenterZ=0 NormalX=0 NormalY=0 NormalZ=1 AngleXU=1.0472 Radius=1.7
    g20: Circle CenterX=267.044 CenterY=85.865 CenterZ=0 NormalX=0 NormalY=0 NormalZ=1 AngleXU=0 Radius=1.7
    g21: Circle CenterX=249.341 CenterY=87.418 CenterZ=0 NormalX=0 NormalY=0 NormalZ=-1 AngleXU=1.33355 Radius=1.7
    g22: Circle CenterX=295.563 CenterY=-15.8437 CenterZ=0 NormalX=0 NormalY=0 NormalZ=1 AngleXU=0 Radius=1.7
FEATURE [Sketcher::SketchObject] Unfold_Sketch_bends012  label="door_hor_bends"
  FullyConstrained = false
  sketch-geometry (2):
    g0: LineSegment StartX=311.619 StartY=-131.216 StartZ=0 EndX=256.251 EndY=97.7676 EndZ=0
    g1: LineSegment StartX=257.16 StartY=99.8863 StartZ=0 EndX=267.032 EndY=105.586 EndZ=0
FEATURE [PartDesign::FeatureBase] BaseFeature009
  BaseFeature = -> Unfold012
  Suppressed = false
FEATURE [PartDesign::Body] Body009  label="door_hor_body"
  BaseFeature = -> Unfold012
  Group = -> [BaseFeature009]
  Origin = -> Origin009
  Tip = -> BaseFeature009
FEATURE [Part::Feature] Unfold013  label="door_hor_amplifier_unfold"
  Placement = pos=(0,0,-42) rot=(-0.186157,0.694747,-0.694747;3.50969rad)
  shape: bbox 24.66 x 15 x 1.122 mm, 13 faces (baked)
FEATURE [Sketcher::SketchObject] Unfold_Sketch013  label="door_hor_amplifier_Sketch"
  FullyConstrained = false
  sketch-geometry (11):
    g0: LineSegment StartX=-259.388 StartY=13 StartZ=0 EndX=-259.388 EndY=2 EndZ=0
    g1: BSplineCurve PolesCount=26 KnotsCount=9 Degree=4 IsPeriodic=0
    g2: BSplineCurve PolesCount=26 KnotsCount=9 Degree=4 IsPeriodic=0
    g3: LineSegment StartX=-282.05 StartY=15 StartZ=0 EndX=-261.388 EndY=15 EndZ=0
    g4: BSplineCurve PolesCount=26 KnotsCount=9 Degree=4 IsPeriodic=0
    g5: LineSegment StartX=-284.05 StartY=13 StartZ=0 EndX=-284.05 EndY=2 EndZ=0
    g6: BSplineCurve PolesCount=26 KnotsCount=9 Degree=4 IsPeriodic=0
    g7: LineSegment StartX=-282.05 StartY=0 StartZ=0 EndX=-261.388 EndY=0 EndZ=0
    g8: Circle CenterX=-262.352 CenterY=7.22528 CenterZ=0 NormalX=0 NormalY=0 NormalZ=1 AngleXU=-3.14159 Radius=1.7
    g9: Circle CenterX=-280.849 CenterY=2.7 CenterZ=0 NormalX=0 NormalY=0 NormalZ=-1 AngleXU=1e-16 Radius=1.7
    g10: Circle CenterX=-277.349 CenterY=12 CenterZ=0 NormalX=0 NormalY=0 NormalZ=-1 AngleXU=1e-16 Radius=1.7
FEATURE [Sketcher::SketchObject] Unfold_Sketch_bends013  label="door_hor_amplifier_bends"
  FullyConstrained = false
  Placement = pos=(-34.7832,0,-90.782) rot=(0,1,0;0.365897rad)
  sketch-geometry (1):
    g0: LineSegment StartX=-253.732 StartY=0 StartZ=0 EndX=-253.732 EndY=15 EndZ=0
FEATURE [PartDesign::FeatureBase] BaseFeature010
  BaseFeature = -> Unfold013
  Placement = pos=(0,0,-42) rot=(-0.186157,0.694747,-0.694747;3.50969rad)
  Suppressed = false
  expr: BaseFeature = <<door_hor_amplifier_unfold>>._self
  expr: Placement = .BaseFeature.Placement
FEATURE [PartDesign::Body] Body010  label="door_hor_amplifier_body"
  BaseFeature = -> Unfold013
  Group = -> [BaseFeature010]
  Origin = -> Origin010
  Tip = -> BaseFeature010
FEATURE [Part::Feature] Unfold014  label="door_base_pillar_unfold"
  Placement = pos=(0,0,358.956) rot=(0.030858,0.70677,-0.70677;3.0799rad)
  shape: bbox 47.52 x 1200 x 1.351 mm, 32 faces (baked)
FEATURE [Sketcher::SketchObject] Unfold_Sketch014  label="door_base_pillar_Sketch"
  FullyConstrained = false
  sketch-geometry (36):
    g0: LineSegment StartX=-12.7635 StartY=-1111 StartZ=0 EndX=-12.7635 EndY=-1198 EndZ=0
    g1: LineSegment StartX=-12.851 StartY=-1111 StartZ=0 EndX=-12.851 EndY=-1198 EndZ=0
    g2: ArcOfEllipse CenterX=-14.7711 CenterY=-1198 CenterZ=0 NormalX=0 NormalY=0 NormalZ=1 MajorRadius=2.00764 MinorRadius=2 AngleXU=-3.14159 StartAngle=1.5708 EndAngle=3.14159
    g3: LineSegment StartX=-14.7711 StartY=-1200 StartZ=0 EndX=-14.8586 EndY=-1200 EndZ=0
    g4: ArcOfEllipse CenterX=-14.8586 CenterY=-1198 CenterZ=0 NormalX=0 NormalY=0 NormalZ=1 MajorRadius=2.00764 MinorRadius=2 AngleXU=-3.14159 StartAngle=1.5708 EndAngle=3.14159
    g5: LineSegment StartX=-14.8586 StartY=-1200 StartZ=0 EndX=-36.2463 EndY=-1200 EndZ=0
    g6: LineSegment StartX=-12.851 StartY=-2 StartZ=0 EndX=-12.851 EndY=-128 EndZ=0
    g7: LineSegment StartX=-12.7635 StartY=-2 StartZ=0 EndX=-12.7635 EndY=-128 EndZ=0
    g8: ArcOfEllipse CenterX=-14.8586 CenterY=-2 CenterZ=0 NormalX=0 NormalY=0 NormalZ=1 MajorRadius=2.00764 MinorRadius=2 AngleXU=0 StartAngle=0 EndAngle=1.5708
    g9: LineSegment StartX=-14.8586 StartY=4e-16 StartZ=0 EndX=-14.7711 EndY=4e-16 EndZ=0
    g10: ArcOfEllipse CenterX=-14.7711 CenterY=-2 CenterZ=0 NormalX=0 NormalY=0 NormalZ=1 MajorRadius=2.00764 MinorRadius=2 AngleXU=0 StartAngle=0 EndAngle=1.5708
    g11: LineSegment StartX=-14.8586 StartY=0 StartZ=0 EndX=-36.2463 EndY=0 EndZ=0
    g12: BSplineCurve PolesCount=26 KnotsCount=9 Degree=4 IsPeriodic=0
    g13: LineSegment StartX=-38.2463 StartY=-2 StartZ=0 EndX=-38.2463 EndY=-1198 EndZ=0
    g14: BSplineCurve PolesCount=26 KnotsCount=9 Degree=4 IsPeriodic=0
    g15: LineSegment StartX=-12.851 StartY=-128 StartZ=0 EndX=7.26812 EndY=-128 EndZ=0
    g16: LineSegment StartX=7.26812 StartY=-1111 StartZ=0 EndX=-12.851 EndY=-1111 EndZ=0
    g17: ArcOfCircle CenterX=7.26812 CenterY=-1109 CenterZ=0 NormalX=0 NormalY=0 NormalZ=1 AngleXU=1.5708 Radius=2 StartAngle=3.14159 EndAngle=4.71239
    g18: LineSegment StartX=9.26812 StartY=-130 StartZ=0 EndX=9.26812 EndY=-1109 EndZ=0
    g19: ArcOfCircle CenterX=7.26812 CenterY=-130 CenterZ=0 NormalX=0 NormalY=0 NormalZ=1 AngleXU=-1.5708 Radius=2 StartAngle=1.5708 EndAngle=3.14159
    g20: Circle CenterX=2.87731 CenterY=-1063 CenterZ=0 NormalX=0 NormalY=0 NormalZ=1 AngleXU=-3.14159 Radius=2
    g21: Circle CenterX=2.87731 CenterY=-999.8 CenterZ=0 NormalX=0 NormalY=0 NormalZ=1 AngleXU=-3.14159 Radius=2
    g22: Circle CenterX=2.87731 CenterY=-363.2 CenterZ=0 NormalX=0 NormalY=0 NormalZ=1 AngleXU=-3.14159 Radius=2
    g23: Circle CenterX=2.87731 CenterY=-300 CenterZ=0 NormalX=0 NormalY=0 NormalZ=1 AngleXU=-3.14159 Radius=2
    g24: Circle CenterX=-33.5 CenterY=-1094 CenterZ=0 NormalX=0 NormalY=0 NormalZ=1 AngleXU=3.14159 Radius=1.7
    g25: Circle CenterX=-20 CenterY=-1190 CenterZ=0 NormalX=0 NormalY=0 NormalZ=1 AngleXU=3.14159 Radius=1.7
    g26: Circle CenterX=-20 CenterY=-720 CenterZ=0 NormalX=0 NormalY=0 NormalZ=1 AngleXU=3.14159 Radius=1.7
    g27: Circle CenterX=-20 CenterY=-955 CenterZ=0 NormalX=0 NormalY=0 NormalZ=1 AngleXU=3.14159 Radius=1.7
    g28: Circle CenterX=-17.5 CenterY=-1094 CenterZ=0 NormalX=0 NormalY=0 NormalZ=1 AngleXU=3.14159 Radius=1.7
    g29: Circle CenterX=1.1397 CenterY=-1094 CenterZ=0 NormalX=0 NormalY=0 NormalZ=1 AngleXU=-3.14159 Radius=1.7
    g30: Circle CenterX=-20 CenterY=-15 CenterZ=0 NormalX=0 NormalY=0 NormalZ=1 AngleXU=3.14159 Radius=1.7
    g31: Circle CenterX=-33.5 CenterY=-154 CenterZ=0 NormalX=0 NormalY=0 NormalZ=1 AngleXU=3.14159 Radius=1.7
    g32: Circle CenterX=1.1397 CenterY=-154 CenterZ=0 NormalX=0 NormalY=0 NormalZ=1 AngleXU=-3.14159 Radius=1.7
    g33: Circle CenterX=-20 CenterY=-485 CenterZ=0 NormalX=0 NormalY=0 NormalZ=1 AngleXU=3.14159 Radius=1.7
    g34: Circle CenterX=-20 CenterY=-250 CenterZ=0 NormalX=0 NormalY=0 NormalZ=1 AngleXU=3.14159 Radius=1.7
    g35: Circle CenterX=-17.5 CenterY=-154 CenterZ=0 NormalX=0 NormalY=0 NormalZ=1 AngleXU=3.14159 Radius=1.7
FEATURE [Sketcher::SketchObject] Unfold_Sketch_bends014  label="door_base_pillar_bends"
  FullyConstrained = false
  Placement = pos=(-2.34398,0,-4.09243) rot=(0,1,0;0.520149rad)
  sketch-geometry (1):
    g0: LineSegment StartX=-8.2341 StartY=-1111 StartZ=0 EndX=-8.2341 EndY=-128 EndZ=0
FEATURE [PartDesign::FeatureBase] BaseFeature011
  BaseFeature = -> Unfold014
  Placement = pos=(0,0,358.956) rot=(0.030858,0.70677,-0.70677;3.0799rad)
  Suppressed = false
  expr: BaseFeature = <<door_base_pillar_unfold>>._self
  expr: Placement = .BaseFeature.Placement
FEATURE [PartDesign::Body] Body011  label="door_base_pillar_body"
  BaseFeature = -> Unfold014
  Group = -> [BaseFeature011]
  Origin = -> Origin011
  Tip = -> BaseFeature011
FEATURE [TechDraw::DrawViewPart] View023
  CoarseView = false
  Direction = (0,0,1)
  Focus = 100
  HardHidden = false
  IsoCount = 0
  IsoHidden = false
  IsoVisible = false
  LockPosition = false
  Perspective = false
  Rotation = 0
  ScaleType = 0
  ScrubCount = 0
  SeamHidden = false
  SeamVisible = true
  SmoothHidden = false
  SmoothVisible = true
  X = 148.5
  XDirection = (0.5,-0.866025,0)
  Y = 65
FEATURE [TechDraw::DrawViewPart] View024
  CoarseView = false
  Direction = (0.5,-0.866025,0)
  Focus = 100
  HardHidden = false
  IsoCount = 0
  IsoHidden = false
  IsoVisible = false
  LockPosition = false
  Perspective = false
  Rotation = 0
  Scale = 0.2
  ScaleType = 2
  ScrubCount = 0
  SeamHidden = false
  SeamVisible = true
  SmoothHidden = false
  SmoothVisible = true
  X = 148.5
  XDirection = (0,0,-0.999999)
  Y = 185
FEATURE [TechDraw::DrawViewPart] View026
  CoarseView = false
  Direction = (-0.183013,-0.683013,0.707107)
  Focus = 100
  HardHidden = false
  IsoCount = 0
  IsoHidden = false
  IsoVisible = false
  LockPosition = false
  Perspective = false
  Rotation = 90
  Scale = 0.3
  ScaleType = 2
  ScrubCount = 0
  SeamHidden = false
  SeamVisible = true
  SmoothHidden = false
  SmoothVisible = true
  X = 148.5
  XDirection = (0.965927,-0.25882,0)
  Y = 155
FEATURE [TechDraw::DrawPage] Page009  label="door_conn_page"
  KeepUpdated = true
  NextBalloonIndex = 1
  ProjectionType = 0
  Template = -> Template
  Views = -> [View023,View024,View026]
FEATURE [App::DocumentObjectGroup] Group009  label="door_conn_unfolds"
  Group = -> [Body007,Unfold010,Unfold_Sketch010,Unfold_Sketch_bends010,Page009]
FEATURE [TechDraw::DrawViewPart] View027
  CoarseView = false
  Direction = (0,0,1)
  Focus = 100
  HardHidden = false
  IsoCount = 0
  IsoHidden = false
  IsoVisible = false
  LockPosition = false
  Perspective = false
  Rotation = 0
  Scale = 3
  ScaleType = 2
  ScrubCount = 0
  SeamHidden = false
  SeamVisible = true
  SmoothHidden = false
  SmoothVisible = true
  X = 84.9838
  XDirection = (1,0,0)
  Y = 103.549
FEATURE [TechDraw::DrawViewPart] View028
  CoarseView = false
  Direction = (0,-1,0)
  Focus = 100
  HardHidden = false
  IsoCount = 0
  IsoHidden = false
  IsoVisible = false
  LockPosition = false
  Perspective = false
  Rotation = 0
  Scale = 3
  ScaleType = 2
  ScrubCount = 0
  SeamHidden = false
  SeamVisible = true
  SmoothHidden = false
  SmoothVisible = true
  X = 216.601
  XDirection = (1,0,2.4e-05)
  Y = 104.771
FEATURE [TechDraw::DrawPage] Page010  label="door_base_pillar_to_hor_fix_page"
  KeepUpdated = true
  NextBalloonIndex = 1
  ProjectionType = 0
  Template = -> Template
  Views = -> [View027,View028]
FEATURE [App::DocumentObjectGroup] Group010  label="door_base_pillar_to_hor_fix_unfold"
  Group = -> [Unfold011,Unfold_Sketch011,Unfold_Sketch_bends011,Body008,Page010]
FEATURE [TechDraw::DrawViewPart] View029
  CoarseView = false
  Direction = (0,0,1)
  Focus = 100
  HardHidden = false
  IsoCount = 0
  IsoHidden = false
  IsoVisible = false
  LockPosition = false
  Perspective = false
  Rotation = 90
  ScaleType = 0
  ScrubCount = 0
  SeamHidden = false
  SeamVisible = true
  SmoothHidden = false
  SmoothVisible = true
  X = 147.589
  XDirection = (0.97199,0.235024,0)
  Y = 179.717
FEATURE [TechDraw::DrawViewPart] View030
  CoarseView = false
  Direction = (0.235024,-0.97199,0)
  Focus = 100
  HardHidden = false
  IsoCount = 0
  IsoHidden = false
  IsoVisible = false
  LockPosition = false
  Perspective = false
  Rotation = 0
  ScaleType = 0
  ScrubCount = 0
  SeamHidden = false
  SeamVisible = true
  SmoothHidden = false
  SmoothVisible = true
  X = 43.5221
  XDirection = (0.97199,0.235024,0)
  Y = 76.6747
FEATURE [TechDraw::DrawViewPart] View031
  CoarseView = false
  Direction = (0.804812,-0.319808,0.5)
  Focus = 100
  HardHidden = false
  IsoCount = 0
  IsoHidden = false
  IsoVisible = false
  LockPosition = false
  Perspective = false
  Rotation = 0
  ScaleType = 0
  ScrubCount = 0
  SeamHidden = false
  SeamVisible = true
  SmoothHidden = false
  SmoothVisible = true
  X = 182.026
  XDirection = (0.28539,0.947156,0.146446)
  Y = 78.5505
FEATURE [TechDraw::DrawPage] Page011  label="door_hor_page"
  KeepUpdated = true
  NextBalloonIndex = 1
  ProjectionType = 0
  Template = -> Template
  Views = -> [View029,View030,View031]
FEATURE [App::DocumentObjectGroup] Group011  label="door_hor_unfolds"
  Group = -> [Unfold012,Unfold_Sketch012,Unfold_Sketch_bends012,Body009,Page011]
FEATURE [TechDraw::DrawViewPart] View032
  CoarseView = false
  Direction = (0,0,1)
  Focus = 100
  HardHidden = false
  IsoCount = 0
  IsoHidden = false
  IsoVisible = false
  LockPosition = false
  Perspective = false
  Rotation = 0
  Scale = 3
  ScaleType = 2
  ScrubCount = 0
  SeamHidden = false
  SeamVisible = true
  SmoothHidden = false
  SmoothVisible = true
  X = 148.5
  XDirection = (0.469471,0.882948,0)
  Y = 105
FEATURE [TechDraw::DrawViewPart] View033
  CoarseView = false
  Direction = (0.624338,-0.331966,0.707107)
  Focus = 100
  HardHidden = false
  IsoCount = 0
  IsoHidden = false
  IsoVisible = false
  LockPosition = false
  Perspective = false
  Rotation = 0
  Scale = 3
  ScaleType = 2
  ScrubCount = 0
  SeamHidden = false
  SeamVisible = true
  SmoothHidden = false
  SmoothVisible = true
  X = 231.149
  XDirection = (0.469471,0.882948,0)
  Y = 106.924
FEATURE [TechDraw::DrawViewPart] View034
  CoarseView = false
  Direction = (0.882948,-0.469471,0)
  Focus = 100
  HardHidden = false
  IsoCount = 0
  IsoHidden = false
  IsoVisible = false
  LockPosition = false
  Perspective = false
  Rotation = 0
  Scale = 3
  ScaleType = 2
  ScrubCount = 0
  SeamHidden = false
  SeamVisible = true
  SmoothHidden = false
  SmoothVisible = true
  X = 66.4581
  XDirection = (0.469471,0.882948,0)
  Y = 109.877
FEATURE [TechDraw::DrawPage] Page012  label="door_hor_amplifier_page"
  KeepUpdated = true
  NextBalloonIndex = 1
  ProjectionType = 0
  Template = -> Template
  Views = -> [View032,View033,View034]
FEATURE [App::DocumentObjectGroup] Group012  label="door_hor_amplifier_unfolds"
  Group = -> [Unfold013,Unfold_Sketch013,Unfold_Sketch_bends013,Body010,Page012]
FEATURE [TechDraw::DrawViewPart] View035
  CoarseView = false
  Direction = (0,0,1)
  Focus = 100
  HardHidden = false
  IsoCount = 0
  IsoHidden = false
  IsoVisible = false
  LockPosition = false
  Perspective = false
  Rotation = 0
  ScaleType = 0
  ScrubCount = 0
  SeamHidden = false
  SeamVisible = true
  SmoothHidden = false
  SmoothVisible = true
  X = 151.117
  XDirection = (0,1,0)
  XSource = -> [Link007]
  Y = 96.5115
FEATURE [TechDraw::DrawViewPart] View036
  CoarseView = false
  Direction = (-0.087156,-0.996195,0)
  Focus = 100
  HardHidden = false
  IsoCount = 0
  IsoHidden = false
  IsoVisible = false
  LockPosition = false
  Perspective = false
  Rotation = 90
  Scale = 0.22
  ScaleType = 2
  ScrubCount = 0
  SeamHidden = false
  SeamVisible = true
  SmoothHidden = false
  SmoothVisible = true
  X = 149.059
  XDirection = (0.996195,-0.087156,0)
  XSource = -> [Link007]
  Y = 144.89
FEATURE [TechDraw::DrawViewDimension] Dimension037
  AngleOverride = false
  Arbitrary = false
  ArbitraryTolerances = false
  BoxCorners = (2) [(-132,-3.26987,-1e-07),(132,3.26987,1e-07)]
  EqualTolerance = true
  ExtensionAngle = 0
  FormatSpec = %.2w
  FormatSpecOverTolerance = %+.2w
  FormatSpecUnderTolerance = %+.2w
  Inverted = false
  LineAngle = 0
  LockPosition = false
  MeasureType = 1
  OverTolerance = 0
  References2D = -> [View036]
  Rotation = 0
  ScaleType = 0
  TheoreticalExact = false
  Type = 0
  UnderTolerance = 0
  X = 0
  Y = 19.4617
FEATURE [TechDraw::DrawPage] Page013  label="door_base_pillar_page"
  KeepUpdated = true
  NextBalloonIndex = 1
  ProjectionType = 0
  Template = -> Template
  Views = -> [View035,View036,Dimension037]
FEATURE [App::DocumentObjectGroup] Group013  label="door_base_pillar_unfolds"
  Group = -> [Unfold014,Unfold_Sketch014,Unfold_Sketch_bends014,Body011,Page013]
FEATURE [App::Link] Link013  label="basement_amplifier_material_0.30ansi001"
  LinkedObject = -> <external composit_full_size3.FCStd>#Body105
FEATURE [App::Link] Link014  label="basement2_amplifier_material_0.30ansi"
  LinkedObject = -> <external composit_full_size3.FCStd>#Body107
FEATURE [TechDraw::DrawViewPart] View037
  CoarseView = false
  Direction = (0,0,1)
  Focus = 100
  HardHidden = false
  IsoCount = 0
  IsoHidden = false
  IsoVisible = false
  LockPosition = false
  Perspective = false
  Rotation = 0
  Scale = 0.3
  ScaleType = 2
  ScrubCount = 0
  SeamHidden = false
  SeamVisible = true
  SmoothHidden = false
  SmoothVisible = true
  X = 148.5
  XDirection = (1,1.7e-05,0)
  XSource = -> [Link013]
  Y = 126.54
  expr: X = <<Template002>>.Width / 2
FEATURE [TechDraw::DrawViewPart] View038
  CoarseView = false
  Direction = (1,1.7e-05,0)
  Focus = 100
  HardHidden = false
  IsoCount = 0
  IsoHidden = false
  IsoVisible = false
  LockPosition = false
  Perspective = false
  Rotation = 0
  Scale = 0.5
  ScaleType = 1
  ScrubCount = 0
  SeamHidden = false
  SeamVisible = true
  SmoothHidden = false
  SmoothVisible = true
  X = 148.5
  XDirection = (-1.7e-05,1,0)
  XSource = -> [Link013]
  Y = 25
FEATURE [TechDraw::DrawViewPart] View039
  CoarseView = false
  Direction = (1,1.7e-05,0)
  Focus = 100
  HardHidden = false
  IsoCount = 0
  IsoHidden = false
  IsoVisible = false
  LockPosition = false
  Perspective = false
  Rotation = 0
  Scale = 0.45
  ScaleType = 2
  ScrubCount = 0
  SeamHidden = false
  SeamVisible = true
  SmoothHidden = false
  SmoothVisible = true
  X = 157.134
  XDirection = (-1.7e-05,1,0)
  XSource = -> [Link014]
  Y = 31.335
FEATURE [TechDraw::DrawViewPart] View040
  CoarseView = false
  Direction = (0,0,1)
  Focus = 100
  HardHidden = false
  IsoCount = 0
  IsoHidden = false
  IsoVisible = false
  LockPosition = false
  Perspective = false
  Rotation = 0
  Scale = 0.25
  ScaleType = 1
  ScrubCount = 0
  SeamHidden = false
  SeamVisible = true
  SmoothHidden = false
  SmoothVisible = true
  X = 148.5
  XDirection = (1,1.7e-05,0)
  XSource = -> [Link014]
  Y = 125
FEATURE [TechDraw::DrawPage] Page015  label="basement_amplifier_bottom_page"
  KeepUpdated = true
  NextBalloonIndex = 7
  ProjectionType = 0
  Template = -> Template002
  Views = -> [View039,View040]
FEATURE [TechDraw::DrawViewDimension] Dimension041
  AngleOverride = false
  Arbitrary = false
  ArbitraryTolerances = false
  BoxCorners = (2) [(-87.7243,-75.9722,-1e-07),(87.7243,75.9722,1e-07)]
  EqualTolerance = true
  ExtensionAngle = 0
  FormatSpec = %.2w
  FormatSpecOverTolerance = %+.2w
  FormatSpecUnderTolerance = %+.2w
  Inverted = false
  LineAngle = 0
  LockPosition = false
  MeasureType = 1
  OverTolerance = 0
  References2D = -> [View037]
  Rotation = 0
  ScaleType = 0
  TheoreticalExact = false
  Type = 1
  UnderTolerance = 0
  X = -0.815068
  Y = 6.99215
FEATURE [TechDraw::DrawViewDimension] Dimension042
  AngleOverride = false
  Arbitrary = false
  ArbitraryTolerances = false
  EqualTolerance = true
  ExtensionAngle = 0
  FormatSpec = %.2w
  FormatSpecOverTolerance = %+.2w
  FormatSpecUnderTolerance = %+.2w
  Inverted = false
  LineAngle = 0
  LockPosition = false
  MeasureType = 1
  OverTolerance = 0
  References2D = -> [View037]
  Rotation = 0
  ScaleType = 0
  TheoreticalExact = false
  Type = 1
  UnderTolerance = 0
  X = -0.570493
  Y = 72.6283
FEATURE [Part::Feature] Unfold017
  Placement = pos=(0,0,0) rot=(0,0,1;0.523599rad)
  shape: bbox 481.5 x 552.9 x 2 mm, 69 faces (baked)
FEATURE [PartDesign::FeatureAdditivePython] PDW_Add001  # link proxy (typed FeaturePython)
  Body = Body013
  ClaimChildren = true
  EditPlacementAdjustments = false
  Enabled = 1
  LinkedObject = -> Unfold017
  MeshTolerance = 0.1
  PatternBaseOffset = 0
  PatternBaseScale = 1
  PatternBaseScaleXYZ = (1,1,1)
  PatternOffsetCut = false
  PatternOffsetIntersection = false
  PatternOffsetJoin = 0
  PatternOffsetMode = 0
  PatternOffsetSelfIntersection = false
  PatternOperation = 0
  PatternOperationDefault = None
  PatternScaleCut = false
  PatternShapeOffset = 0
  PatternShapeScale = 1
  PatternShapeScaleXYZ = (1,1,1)
  PatternToolOffset = 0
  PatternToolScale = 1
  PatternToolScaleXYZ = (1,1,1)
  RefineMesh = true
  ShapeManagement = 0
  ShowMeshProps = false
  ShowOffsetProps = false
  ShowScaleProps = false
  ShowWarnings = true
  Suppressed = false
  TipBaseOffset = 0
  TipBaseScale = 1
  TipBaseScaleXYZ = (1,1,1)
  TipOffsetCut = false
  TipOffsetIntersection = false
  TipOffsetJoin = 0
  TipOffsetMode = 0
  TipOffsetSelfIntersection = false
  TipOperation = 0
  TipOperationDefault = Fuse
  TipScaleCut = false
  TipShapeOffset = 0
  TipShapeScale = 1
  TipShapeScaleXYZ = (1,1,1)
  TipTool = -> Unfold017
  TipToolOffset = 0
  TipToolScale = 1
  TipToolScaleXYZ = (1,1,1)
  Type = Additive
  UsePatternBaseAddSubShape = false
  UsePatternToolAddSubShape = false
  UseTipBaseAddSubShape = false
  UseTipToolAddSubShape = false
  Version = 0.2023.08.13
FEATURE [Sketcher::SketchObject] Unfold_Sketch_bends017  label="basement2_amplifier_bends"
  FullyConstrained = false
  sketch-geometry (6):
    g0: LineSegment StartX=48.4571 StartY=82.0288 StartZ=0 EndX=273.448 EndY=46.699 EndZ=0
    g1: LineSegment StartX=273.448 StartY=-46.699 StartZ=0 EndX=48.4571 EndY=-82.0288 EndZ=0
    g2: LineSegment StartX=-96.2817 StartY=260.163 StartZ=0 EndX=46.8104 EndY=82.9795 EndZ=0
    g3: LineSegment StartX=46.8104 StartY=-82.9795 StartZ=0 EndX=-96.2817 EndY=-260.163 EndZ=0
    g4: LineSegment StartX=-95.2675 StartY=0.950723 StartZ=0 EndX=-177.167 EndY=213.464 EndZ=0
    g5: LineSegment StartX=-177.167 StartY=-213.464 StartZ=0 EndX=-95.2675 EndY=-0.950723 EndZ=0
FEATURE [Sketcher::SketchObject] Unfold_Sketch017  label="basement2_amplifier_Sketch"
  ExternalGeometry = -> [Unfold_Sketch_bends017]
  FullyConstrained = false
  sketch-geometry (79):
    g0: ArcOfCircle CenterX=70.1267 CenterY=101.256 CenterZ=0 NormalX=0 NormalY=0 NormalZ=1 AngleXU=2.98584 Radius=10 StartAngle=4.71239 EndAngle=5.91534
    g1: LineSegment StartX=268.589 StartY=80.2148 StartZ=0 EndX=71.678 EndY=111.135 EndZ=0
    g2: ArcOfCircle CenterX=267.037 CenterY=70.3358 CenterZ=0 NormalX=0 NormalY=0 NormalZ=1 AngleXU=2.98584 Radius=10 StartAngle=3.14159 EndAngle=4.71239
    g3: LineSegment StartX=61.4665 StartY=106.256 StartZ=0 EndX=48.8226 EndY=84.3564 EndZ=0
    g4: LineSegment StartX=48.0916 StartY=79.7011 StartZ=0 EndX=48.8226 EndY=84.3564 EndZ=0
    g5: LineSegment StartX=48.0916 StartY=79.7011 StartZ=0 EndX=46.188 EndY=80 EndZ=0
    g6: LineSegment StartX=46.188 StartY=80 StartZ=0 EndX=44.9774 EndY=81.4991 EndZ=0
    g7: LineSegment StartX=48.6435 StartY=84.4599 StartZ=0 EndX=61.2873 EndY=106.36 EndZ=0
    g8: ArcOfCircle CenterX=52.6271 CenterY=111.36 CenterZ=0 NormalX=0 NormalY=0 NormalZ=1 AngleXU=-0.891442 Radius=10 StartAngle=0.367843 EndAngle=1.5708
    g9: ArcOfCircle CenterX=-72.6061 CenterY=266.429 CenterZ=0 NormalX=0 NormalY=0 NormalZ=1 AngleXU=-0.891442 Radius=10 StartAngle=1.5708 EndAngle=3.14159
    g10: LineSegment StartX=60.4069 StartY=117.643 StartZ=0 EndX=-64.8263 EndY=272.712 EndZ=0
    g11: LineSegment StartX=48.6435 StartY=84.4599 StartZ=0 EndX=44.9774 EndY=81.4991 EndZ=0
    g12: LineSegment StartX=-98.1147 StartY=258.682 StartZ=0 EndX=-78.889 EndY=274.209 EndZ=0
    g13: LineSegment StartX=-98.1147 StartY=258.682 StartZ=0 EndX=-174.968 EndY=214.311 EndZ=0
    g14: LineSegment StartX=-198.027 StartY=205.424 StartZ=0 EndX=-174.968 EndY=214.311 EndZ=0
    g15: ArcOfCircle CenterX=-194.431 CenterY=196.093 CenterZ=0 NormalX=0 NormalY=0 NormalZ=1 AngleXU=-1.20295 Radius=10 StartAngle=3.14159 EndAngle=4.71239
    g16: LineSegment StartX=-203.762 StartY=192.497 StartZ=0 EndX=-132.085 EndY=6.50739 EndZ=0
    g17: ArcOfCircle CenterX=-122.754 CenterY=10.1034 CenterZ=0 NormalX=0 NormalY=0 NormalZ=1 AngleXU=-1.20295 Radius=10 StartAngle=4.71239 EndAngle=5.91534
    g18: LineSegment StartX=-122.754 StartY=0.103426 StartZ=0 EndX=-97.4661 EndY=0.103426 EndZ=0
    g19: LineSegment StartX=-93.069 StartY=1.79802 StartZ=0 EndX=-97.4661 EndY=0.103426 EndZ=0
    g20: LineSegment StartX=-93.069 StartY=1.79802 StartZ=0 EndX=-92.376 EndY=-7.26482e-10 EndZ=0
    g21: LineSegment StartX=-92.376 StartY=-7.26482e-10 StartZ=0 EndX=-93.069 EndY=-1.79802 EndZ=0
    g22: LineSegment StartX=-97.4661 StartY=-0.103426 StartZ=0 EndX=-93.069 EndY=-1.79802 EndZ=0
    g23: LineSegment StartX=-97.4661 StartY=-0.103426 StartZ=0 EndX=-122.754 EndY=-0.103426 EndZ=0
    g24: ArcOfCircle CenterX=-122.754 CenterY=-10.1034 CenterZ=0 NormalX=0 NormalY=0 NormalZ=1 AngleXU=1.20295 Radius=10 StartAngle=0.367843 EndAngle=1.5708
    g25: LineSegment StartX=-132.085 StartY=-6.50739 StartZ=0 EndX=-203.762 EndY=-192.497 EndZ=0
    g26: ArcOfCircle CenterX=-194.431 CenterY=-196.093 CenterZ=0 NormalX=0 NormalY=0 NormalZ=1 AngleXU=1.20295 Radius=10 StartAngle=1.5708 EndAngle=3.14159
    g27: LineSegment StartX=-174.968 StartY=-214.311 StartZ=0 EndX=-198.027 EndY=-205.424 EndZ=0
    g28: LineSegment StartX=-174.968 StartY=-214.311 StartZ=0 EndX=-98.1147 EndY=-258.682 EndZ=0
    g29: LineSegment StartX=-78.889 StartY=-274.209 StartZ=0 EndX=-98.1147 EndY=-258.682 EndZ=0
    g30: ArcOfCircle CenterX=-72.6061 CenterY=-266.429 CenterZ=0 NormalX=0 NormalY=0 NormalZ=1 AngleXU=0.891442 Radius=10 StartAngle=3.14159 EndAngle=4.71239
    g31: LineSegment StartX=-64.8263 StartY=-272.712 StartZ=0 EndX=60.4069 EndY=-117.643 EndZ=0
    g32: ArcOfCircle CenterX=52.6271 CenterY=-111.36 CenterZ=0 NormalX=0 NormalY=0 NormalZ=1 AngleXU=0.891442 Radius=10 StartAngle=4.71239 EndAngle=5.91534
    g33: LineSegment StartX=61.2873 StartY=-106.36 StartZ=0 EndX=48.6435 EndY=-84.4599 EndZ=0
    g34: LineSegment StartX=44.9774 StartY=-81.4991 StartZ=0 EndX=48.6435 EndY=-84.4599 EndZ=0
    g35: LineSegment StartX=44.9774 StartY=-81.4991 StartZ=0 EndX=46.188 EndY=-80 EndZ=0
    g36: LineSegment StartX=46.188 StartY=-80 StartZ=0 EndX=48.0916 EndY=-79.7011 EndZ=0
    g37: LineSegment StartX=48.8226 StartY=-84.3564 StartZ=0 EndX=48.0916 EndY=-79.7011 EndZ=0
    g38: LineSegment StartX=48.8226 StartY=-84.3564 StartZ=0 EndX=61.4665 EndY=-106.256 EndZ=0
    g39: ArcOfCircle CenterX=70.1267 CenterY=-101.256 CenterZ=0 NormalX=0 NormalY=0 NormalZ=1 AngleXU=-2.98584 Radius=10 StartAngle=0.367843 EndAngle=1.5708
    g40: LineSegment StartX=71.678 StartY=-111.135 StartZ=0 EndX=268.589 EndY=-80.2148 EndZ=0
    g41: ArcOfCircle CenterX=267.037 CenterY=-70.3358 CenterZ=0 NormalX=0 NormalY=0 NormalZ=1 AngleXU=-2.98584 Radius=10 StartAngle=1.5708 EndAngle=3.14159
    g42: LineSegment StartX=273.083 StartY=-44.3713 StartZ=0 EndX=276.916 EndY=-68.7846 EndZ=0
    g43: LineSegment StartX=273.083 StartY=44.3713 StartZ=0 EndX=273.083 EndY=-44.3713 EndZ=0
    g44: LineSegment StartX=276.916 StartY=68.7846 StartZ=0 EndX=273.083 EndY=44.3713 EndZ=0
    g45: Circle CenterX=34.575 CenterY=34.575 CenterZ=0 NormalX=0 NormalY=0 NormalZ=1 AngleXU=-1.5708 Radius=5.4
    g46: Circle CenterX=-34.575 CenterY=-34.575 CenterZ=0 NormalX=0 NormalY=0 NormalZ=1 AngleXU=-1.5708 Radius=5.4
    g47: Circle CenterX=34.575 CenterY=-34.575 CenterZ=0 NormalX=0 NormalY=0 NormalZ=1 AngleXU=-1.5708 Radius=5.4
    g48: Circle CenterX=-34.575 CenterY=34.575 CenterZ=0 NormalX=0 NormalY=0 NormalZ=1 AngleXU=-1.5708 Radius=5.4
    g49: Circle CenterX=265 CenterY=-36 CenterZ=0 NormalX=0 NormalY=0 NormalZ=1 AngleXU=-1.5708 Radius=2.5
    g50: Circle CenterX=265 CenterY=36 CenterZ=0 NormalX=0 NormalY=0 NormalZ=1 AngleXU=1.5708 Radius=2.5
    g51: Circle CenterX=55.7258 CenterY=68.9742 CenterZ=0 NormalX=0 NormalY=0 NormalZ=1 AngleXU=1.5708 Radius=2.5
    g52: Circle CenterX=140.207 CenterY=56.173 CenterZ=0 NormalX=0 NormalY=0 NormalZ=1 AngleXU=1.5708 Radius=2.5
    g53: Circle CenterX=-21.4561 CenterY=149.509 CenterZ=0 NormalX=0 NormalY=0 NormalZ=1 AngleXU=0.523599 Radius=2.5
    g54: Circle CenterX=-101.323 CenterY=247.497 CenterZ=0 NormalX=0 NormalY=0 NormalZ=1 AngleXU=0.523599 Radius=2.5
    g55: Circle CenterX=-87.5963 CenterY=13.7728 CenterZ=0 NormalX=0 NormalY=0 NormalZ=1 AngleXU=-2.61799 Radius=2.5
    g56: Circle CenterX=140.207 CenterY=-56.173 CenterZ=0 NormalX=0 NormalY=0 NormalZ=1 AngleXU=-1.5708 Radius=2.5
    g57: Circle CenterX=55.7258 CenterY=-68.9742 CenterZ=0 NormalX=0 NormalY=0 NormalZ=1 AngleXU=-1.5708 Radius=2.5
    g58: Circle CenterX=-87.5963 CenterY=-13.7728 CenterZ=0 NormalX=0 NormalY=0 NormalZ=1 AngleXU=2.61799 Radius=2.5
    g59: Circle CenterX=-21.4561 CenterY=-149.509 CenterZ=0 NormalX=0 NormalY=0 NormalZ=1 AngleXU=-0.523599 Radius=2.5
    g60: Circle CenterX=31.8705 CenterY=-82.747 CenterZ=0 NormalX=0 NormalY=0 NormalZ=1 AngleXU=-0.523599 Radius=2.5
    g61: Circle CenterX=31.8705 CenterY=82.747 CenterZ=0 NormalX=0 NormalY=0 NormalZ=1 AngleXU=0.523599 Radius=2.5
    g62: Circle CenterX=-118.751 CenterY=93.336 CenterZ=0 NormalX=0 NormalY=0 NormalZ=1 AngleXU=-2.61799 Radius=2.5
    g63: Circle CenterX=-163.677 CenterY=211.497 CenterZ=0 NormalX=0 NormalY=0 NormalZ=1 AngleXU=-2.61799 Radius=2.5
    g64: Circle CenterX=-118.751 CenterY=-93.336 CenterZ=0 NormalX=0 NormalY=0 NormalZ=1 AngleXU=2.61799 Radius=2.5
    g65: Circle CenterX=-101.323 CenterY=-247.497 CenterZ=0 NormalX=0 NormalY=0 NormalZ=1 AngleXU=-0.523599 Radius=2.5
    g66: Circle CenterX=-163.677 CenterY=-211.497 CenterZ=0 NormalX=0 NormalY=0 NormalZ=1 AngleXU=2.61799 Radius=2.5
    g67: LineSegment StartX=48.4571 StartY=-82.0288 StartZ=0 EndX=50.4329 EndY=-81.7185 EndZ=0
    g68: LineSegment StartX=48.4571 StartY=82.0288 StartZ=0 EndX=50.4329 EndY=81.7185 EndZ=0
    g69: LineSegment StartX=273.448 StartY=46.699 StartZ=0 EndX=271.473 EndY=47.0092 EndZ=0
    g70: LineSegment StartX=273.448 StartY=-46.699 StartZ=0 EndX=271.473 EndY=-47.0092 EndZ=0
    g71: LineSegment StartX=-176.447 StartY=211.597 StartZ=0 EndX=-177.167 EndY=213.464 EndZ=0
    g72: LineSegment StartX=45.5538 StartY=84.5354 StartZ=0 EndX=46.8104 EndY=82.9795 EndZ=0
    g73: LineSegment StartX=-95.0251 StartY=258.607 StartZ=0 EndX=-96.2817 EndY=260.163 EndZ=0
    g74: LineSegment StartX=-95.2675 StartY=0.950723 StartZ=0 EndX=-95.9868 EndY=2.81693 EndZ=0
    g75: LineSegment StartX=-177.167 StartY=-213.464 StartZ=0 EndX=-176.447 EndY=-211.597 EndZ=0
    g76: LineSegment StartX=-95.9868 StartY=-2.81693 StartZ=0 EndX=-95.2675 EndY=-0.950723 EndZ=0
    g77: LineSegment StartX=46.8104 StartY=-82.9795 StartZ=0 EndX=45.5538 EndY=-84.5354 EndZ=0
    g78: LineSegment StartX=-95.0251 StartY=-258.607 StartZ=0 EndX=-96.2817 EndY=-260.163 EndZ=0
  constraints (81):
    c: Coincident(g67,g-5)
    c: PointOnObject(g67,g-5)
    c: Coincident(g68,g-7)
    c: PointOnObject(g68,g-7)
    c: Coincident(g69,g-7)
    c: PointOnObject(g69,g-7)
    c: Coincident(g70,g-5)
    c: PointOnObject(g70,g-5)
    c: Equal(g67,g68)
    c: Equal(g68,g69)
    c: Equal(g69,g70)
    c: Distance(g67) = 2
    c: Equal(g74,g71)
    c: Equal(g71,g72)
    c: Equal(g72,g73)
    c: Equal(g67,g74) = 2
    c: Coincident(g74,g-4)
    c: PointOnObject(g74,g-4)
    c: Coincident(g71,g-4)
    c: PointOnObject(g71,g-4)
    c: Coincident(g72,g-8)
    c: PointOnObject(g72,g-8)
    c: Coincident(g73,g-8)
    c: PointOnObject(g73,g-8)
    c: Equal(g75,g76)
    c: Equal(g76,g77)
    c: Equal(g77,g78)
    c: Equal(g67,g75) = 2
    c: Coincident(g78,g-6)
    c: PointOnObject(g78,g-6)
    c: Coincident(g75,g-3)
    c: PointOnObject(g75,g-3)
    c: Coincident(g76,g-3)
    c: PointOnObject(g76,g-3)
    c: Coincident(g77,g-6)
    c: PointOnObject(g77,g-6)
    c: Coincident(g25,g26)
    c: Coincident(g15,g16)
    c: Coincident(g26,g27)
    c: Coincident(g14,g15)
    c: Coincident(g27,g28)
    c: Coincident(g13,g14)
    c: Coincident(g24,g25)
    c: Coincident(g16,g17)
    c: Coincident(g23,g24)
    c: Coincident(g17,g18)
    c: Coincident(g28,g29)
    c: Coincident(g12,g13)
    c: Coincident(g22,g23)
    c: Coincident(g18,g19)
    c: Coincident(g21,g22)
    c: Coincident(g19,g20)
    c: Coincident(g20,g21)
    c: Coincident(g29,g30)
    c: Coincident(g9,g12)
    c: Coincident(g30,g31)
    c: Coincident(g9,g10)
    c: Coincident(g34,g35)
    c: Coincident(g6,g11)
    c: Coincident(g35,g36)
    c: Coincident(g5,g6)
    c: Coincident(g36,g37)
    c: Coincident(g4,g5)
    c: Coincident(g33,g34)
    c: Coincident(g7,g11)
    c: Coincident(g37,g38)
    c: Coincident(g3,g4)
    c: Coincident(g31,g32)
    c: Coincident(g8,g10)
    c: Coincident(g32,g33)
    c: Coincident(g7,g8)
    c: Coincident(g38,g39)
    c: Coincident(g0,g3)
    c: Coincident(g39,g40)
    c: Coincident(g0,g1)
    c: Coincident(g40,g41)
    c: Coincident(g1,g2)
    c: Coincident(g42,g43)
    c: Coincident(g43,g44)
    c: Coincident(g41,g42)
    c: Coincident(g2,g44)
FEATURE [PartDesign::Body] Body013  label="basement_amplifier_bottom_body"
  Group = -> [PDW_Add001,Unfold017,Unfold_Sketch017,Unfold_Sketch_bends017]
  Origin = -> Origin013
  Tip = -> PDW_Add001
FEATURE [App::Link] Link018  label="top_amplifier_cornrer_material_0.50ansi"
  LinkPlacement = pos=(0,0,0) rot=(0,0,1;-1.0472rad)
  LinkedObject = -> <external composit_full_size3.FCStd>#Body113
  Placement = pos=(0,0,0) rot=(0,0,1;-1.0472rad)
FEATURE [TechDraw::DrawViewPart] View041
  CoarseView = false
  Direction = (0,0,1)
  Focus = 100
  HardHidden = false
  IsoCount = 0
  IsoHidden = false
  IsoVisible = false
  LockPosition = false
  Perspective = false
  Rotation = 0
  ScaleType = 0
  ScrubCount = 0
  SeamHidden = false
  SeamVisible = true
  SmoothHidden = false
  SmoothVisible = true
  X = 234.047
  XDirection = (1,0,0)
  XSource = -> [Link018]
  Y = 105
FEATURE [TechDraw::DrawViewPart] View042
  CoarseView = false
  Direction = (0.5,0.866025,0)
  Focus = 100
  HardHidden = false
  IsoCount = 0
  IsoHidden = false
  IsoVisible = false
  LockPosition = false
  Perspective = false
  Rotation = 0
  ScaleType = 0
  ScrubCount = 0
  SeamHidden = false
  SeamVisible = true
  SmoothHidden = false
  SmoothVisible = true
  X = 166.922
  XDirection = (-0.866025,0.5,0)
  XSource = -> [Link018]
  Y = 105
FEATURE [App::Link] Link019  label="pillar2_material_0.50ansi"
  LinkedObject = -> <external composit_full_size3.FCStd>#Body112
FEATURE [App::Link] Link021  label="pillar2_bottom_material_0.50ansi"
  LinkedObject = -> <external composit_full_size3.FCStd>#Body111
FEATURE [Part::Mirroring] Part__Mirroring004  label="pillar2_bottom_material_0.50ansi (Mirror #5)"
  Base = (0,0,0)
  Normal = (1,0,0)
  Source = -> Link021
FEATURE [Part::Feature] Unfold019  label="pillar2_unfold"
  shape: bbox 58.02 x 2 x 1686 mm, 42 faces (baked)
FEATURE [Sketcher::SketchObject] Unfold_Sketch_bends019  label="pillar2_Sketch_bends"
  FullyConstrained = false
  sketch-geometry (2):
    g0: LineSegment StartX=1596 StartY=16.6562 StartZ=0 EndX=0 EndY=16.6562 EndZ=0
    g1: LineSegment StartX=1596 StartY=-16.6562 StartZ=0 EndX=0 EndY=-16.6562 EndZ=0
FEATURE [Sketcher::SketchObject] Unfold_Sketch019  label="pillar2_Sketch"
  ExternalGeometry = -> [Unfold_Sketch_bends019]
  FullyConstrained = false
  sketch-geometry (44):
    g0: ArcOfCircle CenterX=3 CenterY=26.0124 CenterZ=0 NormalX=0 NormalY=0 NormalZ=1 AngleXU=1.5708 Radius=3 StartAngle=6.2e-15 EndAngle=1.5708
    g1: LineSegment StartX=3 StartY=29.0124 StartZ=0 EndX=1593 EndY=29.0124 EndZ=0
    g2: ArcOfCircle CenterX=1593 CenterY=26.0124 CenterZ=0 NormalX=0 NormalY=0 NormalZ=1 AngleXU=1.5708 Radius=3 StartAngle=4.71239 EndAngle=6.28319
    g3: ArcOfCircle CenterX=1597 CenterY=-14.3 CenterZ=0 NormalX=0 NormalY=0 NormalZ=1 AngleXU=1.5708 Radius=1 StartAngle=4.71239 EndAngle=7.85398
    g4: LineSegment StartX=1598 StartY=-26.01 StartZ=0 EndX=1598 EndY=-14.3 EndZ=0
    g5: ArcOfCircle CenterX=1601 CenterY=-26.01 CenterZ=0 NormalX=0 NormalY=0 NormalZ=1 AngleXU=1.5708 Radius=3 StartAngle=1.5708 EndAngle=3.14159
    g6: LineSegment StartX=1683 StartY=-29.01 StartZ=0 EndX=1601 EndY=-29.01 EndZ=0
    g7: ArcOfCircle CenterX=1683 CenterY=-26.01 CenterZ=0 NormalX=0 NormalY=0 NormalZ=1 AngleXU=1.5708 Radius=3 StartAngle=3.14159 EndAngle=4.71239
    g8: LineSegment StartX=1686 StartY=26.01 StartZ=0 EndX=1686 EndY=-26.01 EndZ=0
    g9: ArcOfCircle CenterX=1683 CenterY=26.01 CenterZ=0 NormalX=0 NormalY=0 NormalZ=1 AngleXU=1.5708 Radius=3 StartAngle=4.71239 EndAngle=6.28319
    g10: LineSegment StartX=1601 StartY=29.01 StartZ=0 EndX=1683 EndY=29.01 EndZ=0
    g11: ArcOfCircle CenterX=1601 CenterY=26.01 CenterZ=0 NormalX=0 NormalY=0 NormalZ=1 AngleXU=1.5708 Radius=3 StartAngle=0 EndAngle=1.5708
    g12: LineSegment StartX=1598 StartY=14.3 StartZ=0 EndX=1598 EndY=26.01 EndZ=0
    g13: ArcOfCircle CenterX=1597 CenterY=14.3 CenterZ=0 NormalX=0 NormalY=0 NormalZ=1 AngleXU=1.5708 Radius=1 StartAngle=1.5708 EndAngle=4.71239
    g14: ArcOfCircle CenterX=3 CenterY=-26.0124 CenterZ=0 NormalX=0 NormalY=0 NormalZ=1 AngleXU=-1.5708 Radius=3 StartAngle=4.71239 EndAngle=6.28319
    g15: LineSegment StartX=3 StartY=-29.0124 StartZ=0 EndX=1593 EndY=-29.0124 EndZ=0
    g16: ArcOfCircle CenterX=1593 CenterY=-26.0124 CenterZ=0 NormalX=0 NormalY=0 NormalZ=1 AngleXU=-1.5708 Radius=3 StartAngle=0 EndAngle=1.5708
    g17: ArcOfCircle CenterX=475 CenterY=-2.274e-13 CenterZ=0 NormalX=0 NormalY=0 NormalZ=1 AngleXU=1.5708 Radius=1.8 StartAngle=3.14159 EndAngle=6.28319
    g18: LineSegment StartX=475 StartY=-1.8 StartZ=0 EndX=467 EndY=-1.8 EndZ=0
    g19: ArcOfCircle CenterX=467 CenterY=-2.274e-13 CenterZ=0 NormalX=0 NormalY=0 NormalZ=1 AngleXU=1.5708 Radius=1.8 StartAngle=0 EndAngle=3.14159
    g20: LineSegment StartX=467 StartY=1.8 StartZ=0 EndX=475 EndY=1.8 EndZ=0
    g21: Circle CenterX=1607 CenterY=-12.5 CenterZ=0 NormalX=0 NormalY=0 NormalZ=1 AngleXU=1.5708 Radius=1.8
    g22: Circle CenterX=1607 CenterY=12.5 CenterZ=0 NormalX=0 NormalY=0 NormalZ=1 AngleXU=1.5708 Radius=1.8
    g23: Circle CenterX=1586 CenterY=0 CenterZ=0 NormalX=0 NormalY=0 NormalZ=1 AngleXU=1.5708 Radius=1.7
    g24: Circle CenterX=1312.75 CenterY=0 CenterZ=0 NormalX=0 NormalY=0 NormalZ=1 AngleXU=1.5708 Radius=1.7
    g25: Circle CenterX=1039.5 CenterY=0 CenterZ=0 NormalX=0 NormalY=0 NormalZ=1 AngleXU=1.5708 Radius=1.7
    g26: Circle CenterX=766.25 CenterY=0 CenterZ=0 NormalX=0 NormalY=0 NormalZ=1 AngleXU=1.5708 Radius=1.7
    g27: Circle CenterX=1675 CenterY=0 CenterZ=0 NormalX=0 NormalY=0 NormalZ=1 AngleXU=1.5708 Radius=1.7
    g28: Circle CenterX=100 CenterY=23.0124 CenterZ=0 NormalX=0 NormalY=0 NormalZ=-1 AngleXU=-1.5708 Radius=1.7
    g29: Circle CenterX=70 CenterY=23.0124 CenterZ=0 NormalX=0 NormalY=0 NormalZ=-1 AngleXU=-1.5708 Radius=1.7
    g30: Circle CenterX=40 CenterY=23.0124 CenterZ=0 NormalX=0 NormalY=0 NormalZ=-1 AngleXU=-1.5708 Radius=1.7
    g31: Circle CenterX=40 CenterY=-23.0124 CenterZ=0 NormalX=0 NormalY=0 NormalZ=-1 AngleXU=-1.5708 Radius=1.7
    g32: Circle CenterX=100 CenterY=-23.0124 CenterZ=0 NormalX=0 NormalY=0 NormalZ=-1 AngleXU=-1.5708 Radius=1.7
    g33: Circle CenterX=70 CenterY=-23.0124 CenterZ=0 NormalX=0 NormalY=0 NormalZ=-1 AngleXU=-1.5708 Radius=1.7
    g34: Circle CenterX=10 CenterY=-23.0124 CenterZ=0 NormalX=0 NormalY=0 NormalZ=-1 AngleXU=-1.5708 Radius=1.7
    g35: Circle CenterX=10 CenterY=23.0124 CenterZ=0 NormalX=0 NormalY=0 NormalZ=-1 AngleXU=-1.5708 Radius=1.7
    g36: Circle CenterX=493 CenterY=0 CenterZ=0 NormalX=0 NormalY=0 NormalZ=1 AngleXU=1.5708 Radius=1.7
    g37: LineSegment StartX=9.59e-14 StartY=-26.0124 StartZ=0 EndX=1.03e-13 EndY=26.0124 EndZ=0
    g38: LineSegment StartX=1596 StartY=-26.0124 StartZ=0 EndX=1596 EndY=-14.3 EndZ=0
    g39: LineSegment StartX=1596 StartY=14.3 StartZ=0 EndX=1596 EndY=26.0124 EndZ=0
    g40: LineSegment StartX=2 StartY=16.6562 StartZ=0 EndX=2.04e-14 EndY=16.6562 EndZ=0
    g41: LineSegment StartX=1.68e-14 StartY=-16.6562 StartZ=0 EndX=2 EndY=-16.6562 EndZ=0
    g42: LineSegment StartX=1596 StartY=-16.6562 StartZ=0 EndX=1594 EndY=-16.6562 EndZ=0
    g43: LineSegment StartX=1596 StartY=16.6562 StartZ=0 EndX=1594 EndY=16.6562 EndZ=0
  constraints (36):
    c: PointOnObject(g40,g-4)
    c: Coincident(g40,g-4)
    c: Coincident(g41,g-3)
    c: PointOnObject(g41,g-3)
    c: Coincident(g42,g-3)
    c: PointOnObject(g42,g-3)
    c: Coincident(g43,g-4)
    c: PointOnObject(g43,g-4)
    c: Equal(g43,g42)
    c: Equal(g42,g41)
    c: Equal(g41,g40)
    c: Distance(g41) = 2
    c: Coincident(g14,g37)
    c: Coincident(g0,g37)
    c: Coincident(g14,g15)
    c: Coincident(g0,g1)
    c: Coincident(g18,g19)
    c: Coincident(g19,g20)
    c: Coincident(g17,g18)
    c: Coincident(g17,g20)
    c: Coincident(g15,g16)
    c: Coincident(g1,g2)
    c: Coincident(g16,g38)
    c: Coincident(g3,g38)
    c: Coincident(g13,g39)
    c: Coincident(g2,g39)
    c: Coincident(g4,g5)
    c: Coincident(g3,g4)
    c: Coincident(g12,g13)
    c: Coincident(g11,g12)
    c: Coincident(g5,g6)
    c: Coincident(g10,g11)
    c: Coincident(g6,g7)
    c: Coincident(g9,g10)
    c: Coincident(g7,g8)
    c: Coincident(g8,g9)
FEATURE [Part::Feature] Unfold020  label="pillar2_bottom_Unfold"
  shape: bbox 101 x 131.7 x 2 mm, 20 faces (baked)
FEATURE [Sketcher::SketchObject] Unfold_Sketch_bends020  label="pillar2_bottom_Unfold_Sketch_bends"
  FullyConstrained = false
  Placement = pos=(0,-0.278734,0.61684) rot=(1,0,0;0.424411rad)
  sketch-geometry (1):
    g0: LineSegment StartX=50.5 StartY=-1.49797 StartZ=0 EndX=-50.5 EndY=-1.49797 EndZ=0
FEATURE [Sketcher::SketchObject] Unfold_Sketch020  label="pillar2_bottom_Unfold_Sketch"
  ExternalGeometry = -> [Unfold_Sketch_bends020]
  FullyConstrained = false
  sketch-geometry (20):
    g0: ArcOfCircle CenterX=-48.5 CenterY=104.712 CenterZ=0 NormalX=0 NormalY=0 NormalZ=1 AngleXU=-6e-16 Radius=2 StartAngle=1.5708 EndAngle=3.14159
    g1: LineSegment StartX=-48.5 StartY=106.712 StartZ=0 EndX=-43.5 EndY=106.712 EndZ=0
    g2: ArcOfCircle CenterX=-43.5 CenterY=98.7124 CenterZ=0 NormalX=0 NormalY=0 NormalZ=1 AngleXU=-6e-16 Radius=8 StartAngle=8.31e-13 EndAngle=1.5708
    g3: ArcOfCircle CenterX=45.5 CenterY=0.712389 CenterZ=0 NormalX=0 NormalY=0 NormalZ=1 AngleXU=-7e-16 Radius=5 StartAngle=2.9243e-11 EndAngle=1.13731
    g4: LineSegment StartX=-18.1011 StartY=35.6594 StartZ=0 EndX=47.6002 EndY=5.24993 EndZ=0
    g5: ArcOfCircle CenterX=-5.5 CenterY=62.8846 CenterZ=0 NormalX=0 NormalY=0 NormalZ=1 AngleXU=-7e-16 Radius=30 StartAngle=3.14159 EndAngle=4.27891
    g6: LineSegment StartX=-35.5 StartY=98.7124 StartZ=0 EndX=-35.5 EndY=62.8846 EndZ=0
    g7: LineSegment StartX=50.5 StartY=-4 StartZ=0 EndX=50.5 EndY=0.712389 EndZ=0
    g8: ArcOfCircle CenterX=29.5 CenterY=-4 CenterZ=0 NormalX=0 NormalY=0 NormalZ=1 AngleXU=0 Radius=21 StartAngle=4.71239 EndAngle=6.28319
    g9: LineSegment StartX=29.5 StartY=-25 StartZ=0 EndX=-29.5 EndY=-25 EndZ=0
    g10: ArcOfCircle CenterX=-29.5 CenterY=-4 CenterZ=0 NormalX=0 NormalY=0 NormalZ=1 AngleXU=0 Radius=21 StartAngle=3.14159 EndAngle=4.71239
    g11: Circle CenterX=-40 CenterY=-12 CenterZ=0 NormalX=0 NormalY=0 NormalZ=-1 AngleXU=3.14159 Radius=2.75
    g12: Circle CenterX=40 CenterY=-12 CenterZ=0 NormalX=0 NormalY=0 NormalZ=-1 AngleXU=3.14159 Radius=2.75
    g13: Circle CenterX=-46.5 CenterY=36.7124 CenterZ=0 NormalX=0 NormalY=0 NormalZ=-1 AngleXU=5.96046e-08 Radius=1.7
    g14: Circle CenterX=-46.5 CenterY=66.7124 CenterZ=0 NormalX=0 NormalY=0 NormalZ=-1 AngleXU=5.96046e-08 Radius=1.7
    g15: Circle CenterX=-46.5 CenterY=96.7124 CenterZ=0 NormalX=0 NormalY=0 NormalZ=-1 AngleXU=5.96046e-08 Radius=1.7
    g16: Circle CenterX=-46.5 CenterY=6.71239 CenterZ=0 NormalX=0 NormalY=0 NormalZ=-1 AngleXU=5.96046e-08 Radius=1.7
    g17: LineSegment StartX=-50.5 StartY=-4 StartZ=0 EndX=-50.5 EndY=104.712 EndZ=0
    g18: LineSegment StartX=-48.5 StartY=-1.64381 StartZ=0 EndX=-50.5 EndY=-1.64381 EndZ=0
    g19: LineSegment StartX=50.5 StartY=-1.64381 StartZ=0 EndX=48.5 EndY=-1.64381 EndZ=0
  constraints (18):
    c: Coincident(g10,g17)
    c: Coincident(g0,g17)
    c: Coincident(g0,g1)
    c: Coincident(g1,g2)
    c: Coincident(g5,g6)
    c: Coincident(g2,g6)
    c: Coincident(g9,g10)
    c: Coincident(g4,g5)
    c: Coincident(g8,g9)
    c: Coincident(g3,g4)
    c: Coincident(g7,g8)
    c: Coincident(g3,g7)
    c: PointOnObject(g18,g-3)
    c: Coincident(g18,g-3)
    c: Coincident(g19,g-3)
    c: PointOnObject(g19,g-3)
    c: Equal(g19,g18)
    c: Distance(g18) = 2
FEATURE [TechDraw::DrawViewPart] View043
  CoarseView = false
  Direction = (0,0,1)
  Focus = 100
  HardHidden = false
  IsoCount = 0
  IsoHidden = false
  IsoVisible = false
  LockPosition = false
  Perspective = false
  Rotation = 0
  ScaleType = 0
  ScrubCount = 0
  SeamHidden = false
  SeamVisible = true
  SmoothHidden = false
  SmoothVisible = true
  X = 198.5
  XDirection = (-1,0,0)
  XSource = -> [Link019]
  Y = 105
FEATURE [TechDraw::DrawViewPart] View044
  CoarseView = false
  Direction = (0,1,0)
  Focus = 100
  HardHidden = false
  IsoCount = 0
  IsoHidden = false
  IsoVisible = false
  LockPosition = false
  Perspective = false
  Rotation = 0
  Scale = 0.12
  ScaleType = 2
  ScrubCount = 0
  SeamHidden = false
  SeamVisible = true
  SmoothHidden = false
  SmoothVisible = true
  X = 78.5
  XDirection = (-1,0,0)
  XSource = -> [Link019]
  Y = 105
FEATURE [TechDraw::DrawViewPart] View045
  CoarseView = false
  Direction = (-0.57735,0.57735,0.57735)
  Focus = 100
  HardHidden = false
  IsoCount = 0
  IsoHidden = false
  IsoVisible = false
  LockPosition = false
  Perspective = false
  Rotation = 0
  Scale = 0.14
  ScaleType = 2
  ScrubCount = 0
  SeamHidden = false
  SeamVisible = true
  SmoothHidden = false
  SmoothVisible = true
  X = 138.5
  XDirection = (-0.707107,-0.707107,0)
  XSource = -> [Link019]
  Y = 105
FEATURE [TechDraw::DrawViewDimension] Dimension054
  AngleOverride = false
  Arbitrary = false
  ArbitraryTolerances = false
  BoxCorners = (2) [(-3.4812,-101.16,-1e-07),(3.4812,101.16,1e-07)]
  EqualTolerance = true
  ExtensionAngle = 0
  FormatSpec = %.2w
  FormatSpecOverTolerance = %+.2w
  FormatSpecUnderTolerance = %+.2w
  Inverted = false
  LineAngle = 0
  LockPosition = false
  MeasureType = 1
  OverTolerance = 0
  References2D = -> [View044]
  Rotation = 0
  ScaleType = 0
  TheoreticalExact = false
  Type = 2
  UnderTolerance = 0
  X = -24.4618
  Y = 1.9445
FEATURE [TechDraw::DrawViewDimension] Dimension055
  AngleOverride = false
  Arbitrary = false
  ArbitraryTolerances = false
  BoxCorners = (2) [(-29.01,-7,-1e-07),(29.01,7,1e-07)]
  EqualTolerance = true
  ExtensionAngle = 0
  FormatSpec = %.2w
  FormatSpecOverTolerance = %+.2w
  FormatSpecUnderTolerance = %+.2w
  Inverted = false
  LineAngle = 0
  LockPosition = false
  MeasureType = 1
  OverTolerance = 0
  References2D = -> [View043]
  Rotation = 0
  ScaleType = 0
  TheoreticalExact = false
  Type = 1
  UnderTolerance = 0
  X = -1.07436
  Y = -22.414
FEATURE [TechDraw::DrawViewDimension] Dimension056
  AngleOverride = false
  Arbitrary = false
  ArbitraryTolerances = false
  BoxCorners = (2) [(-29.01,-7,-1e-07),(29.01,7,1e-07)]
  EqualTolerance = true
  ExtensionAngle = 0
  FormatSpec = %.2w
  FormatSpecOverTolerance = %+.2w
  FormatSpecUnderTolerance = %+.2w
  Inverted = false
  LineAngle = 0
  LockPosition = false
  MeasureType = 1
  OverTolerance = 0
  References2D = -> [View043]
  Rotation = 0
  ScaleType = 0
  TheoreticalExact = false
  Type = 2
  UnderTolerance = 0
  X = -35.2082
  Y = 2.5
FEATURE [TechDraw::DrawViewDimension] Dimension057
  AngleOverride = false
  Arbitrary = false
  ArbitraryTolerances = false
  EqualTolerance = true
  ExtensionAngle = 0
  FormatSpec = R%.2w
  FormatSpecOverTolerance = %+.2w
  FormatSpecUnderTolerance = %+.2w
  Inverted = false
  LineAngle = 0
  LockPosition = false
  MeasureType = 1
  OverTolerance = 0
  References2D = -> [View043]
  Rotation = 0
  ScaleType = 0
  TheoreticalExact = false
  Type = 4
  UnderTolerance = 0
  X = -8.03047
  Y = 6.79501
FEATURE [TechDraw::DrawViewDimension] Dimension058
  AngleOverride = false
  Arbitrary = false
  ArbitraryTolerances = false
  EqualTolerance = true
  ExtensionAngle = 0
  FormatSpec = R%.2w
  FormatSpecOverTolerance = %+.2w
  FormatSpecUnderTolerance = %+.2w
  Inverted = false
  LineAngle = 0
  LockPosition = false
  MeasureType = 1
  OverTolerance = 0
  References2D = -> [View043]
  Rotation = 0
  ScaleType = 0
  TheoreticalExact = false
  Type = 4
  UnderTolerance = 0
  X = 5.04478
  Y = 1.1325
FEATURE [TechDraw::DrawPage] Page017  label="pillar2_page"
  KeepUpdated = true
  NextBalloonIndex = 7
  ProjectionType = 0
  Template = -> Template002
  Views = -> [View043,View044,View045,Dimension054,Dimension055,Dimension056,Dimension057,Dimension058]
FEATURE [App::DocumentObjectGroup] Group017  label="pillar2_group"
  Group = -> [Unfold019,Unfold_Sketch019,Unfold_Sketch_bends019,Page017]
FEATURE [TechDraw::DrawViewPart] View046
  CoarseView = false
  Direction = (0,-1,0)
  Focus = 100
  HardHidden = false
  IsoCount = 0
  IsoHidden = false
  IsoVisible = false
  LockPosition = false
  Perspective = false
  Rotation = 0
  ScaleType = 0
  ScrubCount = 0
  SeamHidden = false
  SeamVisible = true
  SmoothHidden = false
  SmoothVisible = true
  X = 58.5
  XDirection = (1,0,0)
  XSource = -> [Link021]
  Y = 105
FEATURE [TechDraw::DrawViewPart] View047
  CoarseView = false
  Direction = (-1,0,0)
  Focus = 100
  HardHidden = false
  IsoCount = 0
  IsoHidden = false
  IsoVisible = false
  LockPosition = false
  Perspective = false
  Rotation = 0
  ScaleType = 0
  ScrubCount = 0
  SeamHidden = false
  SeamVisible = true
  SmoothHidden = false
  SmoothVisible = true
  X = 148.5
  XDirection = (0,-1,0)
  XSource = -> [Link021]
  Y = 105
FEATURE [TechDraw::DrawViewPart] View048
  CoarseView = false
  Direction = (0.57735,-0.57735,0.57735)
  Focus = 100
  HardHidden = false
  IsoCount = 0
  IsoHidden = false
  IsoVisible = false
  LockPosition = false
  Perspective = false
  Rotation = 0
  ScaleType = 0
  ScrubCount = 0
  SeamHidden = false
  SeamVisible = true
  SmoothHidden = false
  SmoothVisible = true
  X = 248.5
  XDirection = (0.707107,0.707107,0)
  XSource = -> [Link021]
  Y = 105
FEATURE [TechDraw::DrawViewDimension] Dimension060
  AngleOverride = false
  Arbitrary = false
  ArbitraryTolerances = false
  BoxCorners = (2) [(-50.5,-55,-1e-07),(50.5,55,1e-07)]
  EqualTolerance = true
  ExtensionAngle = 0
  FormatSpec = %.2w
  FormatSpecOverTolerance = %+.2w
  FormatSpecUnderTolerance = %+.2w
  Inverted = false
  LineAngle = 0
  LockPosition = false
  MeasureType = 1
  OverTolerance = 0
  References2D = -> [View046]
  Rotation = 0
  ScaleType = 0
  TheoreticalExact = false
  Type = 2
  UnderTolerance = 0
  X = -47.3837
  Y = 0.736413
FEATURE [TechDraw::DrawViewDimension] Dimension061
  AngleOverride = false
  Arbitrary = false
  ArbitraryTolerances = false
  BoxCorners = (2) [(-12.5,-55,-1e-07),(12.5,55,1e-07)]
  EqualTolerance = true
  ExtensionAngle = 0
  FormatSpec = %.2w
  FormatSpecOverTolerance = %+.2w
  FormatSpecUnderTolerance = %+.2w
  Inverted = false
  LineAngle = 0
  LockPosition = false
  MeasureType = 1
  OverTolerance = 0
  References2D = -> [View047]
  Rotation = 0
  ScaleType = 0
  TheoreticalExact = false
  Type = 1
  UnderTolerance = 0
  X = 0
  Y = -60.0782
FEATURE [TechDraw::DrawViewDimension] Dimension062
  AngleOverride = false
  Arbitrary = false
  ArbitraryTolerances = false
  BoxCorners = (2) [(-12.5,-55,-1e-07),(12.5,55,1e-07)]
  EqualTolerance = true
  ExtensionAngle = 0
  FormatSpec = %.2w
  FormatSpecOverTolerance = %+.2w
  FormatSpecUnderTolerance = %+.2w
  Inverted = false
  LineAngle = 0
  LockPosition = false
  MeasureType = 1
  OverTolerance = 0
  References2D = -> [View047]
  Rotation = 0
  ScaleType = 0
  TheoreticalExact = false
  Type = 2
  UnderTolerance = 0
  X = -28.1283
  Y = 2.04565
FEATURE [TechDraw::DrawPage] Page018  label="pillar2_bottom_page"
  KeepUpdated = true
  NextBalloonIndex = 7
  ProjectionType = 0
  Template = -> Template002
  Views = -> [View046,View047,View048,Dimension060,Dimension061,Dimension062]
FEATURE [TechDraw::DrawViewPart] View049
  CoarseView = false
  Direction = (0,-1,0)
  Focus = 100
  HardHidden = false
  IsoCount = 0
  IsoHidden = false
  IsoVisible = false
  LockPosition = false
  Perspective = false
  Rotation = 0
  ScaleType = 0
  ScrubCount = 0
  SeamHidden = false
  SeamVisible = true
  SmoothHidden = false
  SmoothVisible = true
  Source = -> [Part__Mirroring004]
  X = 68.5
  XDirection = (1,0,0)
  Y = 105
FEATURE [TechDraw::DrawViewPart] View050
  CoarseView = false
  Direction = (1,0,0)
  Focus = 100
  HardHidden = false
  IsoCount = 0
  IsoHidden = false
  IsoVisible = false
  LockPosition = false
  Perspective = false
  Rotation = 0
  ScaleType = 0
  ScrubCount = 0
  SeamHidden = false
  SeamVisible = true
  SmoothHidden = false
  SmoothVisible = true
  Source = -> [Part__Mirroring004]
  X = 158.5
  XDirection = (0,1,0)
  Y = 105
FEATURE [TechDraw::DrawViewPart] View051
  CoarseView = false
  Direction = (-0.57735,-0.57735,0.57735)
  Focus = 100
  HardHidden = false
  IsoCount = 0
  IsoHidden = false
  IsoVisible = false
  LockPosition = false
  Perspective = false
  Rotation = 0
  ScaleType = 0
  ScrubCount = 0
  SeamHidden = false
  SeamVisible = true
  SmoothHidden = false
  SmoothVisible = true
  Source = -> [Part__Mirroring004]
  X = 238.5
  XDirection = (0.707107,-0.707107,0)
  Y = 105
FEATURE [TechDraw::DrawViewDimension] Dimension063
  AngleOverride = false
  Arbitrary = false
  ArbitraryTolerances = false
  BoxCorners = (2) [(-12.5,-55,-1e-07),(12.5,55,1e-07)]
  EqualTolerance = true
  ExtensionAngle = 0
  FormatSpec = %.2w
  FormatSpecOverTolerance = %+.2w
  FormatSpecUnderTolerance = %+.2w
  Inverted = false
  LineAngle = 0
  LockPosition = false
  MeasureType = 1
  OverTolerance = 0
  References2D = -> [View050]
  Rotation = 0
  ScaleType = 0
  TheoreticalExact = false
  Type = 1
  UnderTolerance = 0
  X = 0.275333
  Y = -63.4406
FEATURE [TechDraw::DrawViewDimension] Dimension064
  AngleOverride = false
  Arbitrary = false
  ArbitraryTolerances = false
  BoxCorners = (2) [(-12.5,-55,-1e-07),(12.5,55,1e-07)]
  EqualTolerance = true
  ExtensionAngle = 0
  FormatSpec = %.2w
  FormatSpecOverTolerance = %+.2w
  FormatSpecUnderTolerance = %+.2w
  Inverted = false
  LineAngle = 0
  LockPosition = false
  MeasureType = 1
  OverTolerance = 0
  References2D = -> [View050]
  Rotation = 0
  ScaleType = 0
  TheoreticalExact = false
  Type = 2
  UnderTolerance = 0
  X = 22.0127
  Y = 2.5
FEATURE [TechDraw::DrawPage] Page019  label="pillar2_bottom_mirror_page"
  KeepUpdated = true
  NextBalloonIndex = 7
  ProjectionType = 0
  Template = -> Template002
  Views = -> [View049,View050,View051,Dimension063,Dimension064]
FEATURE [App::DocumentObjectGroup] Group018  label="pillar2_bottom_Group"
  Group = -> [Unfold020,Unfold_Sketch020,Unfold_Sketch_bends020,Page018,Page019]
FEATURE [TechDraw::DrawViewPart] View052
  CoarseView = false
  Direction = (0,1,0)
  Focus = 100
  HardHidden = false
  IsoCount = 0
  IsoHidden = false
  IsoVisible = false
  LockPosition = false
  Perspective = false
  Rotation = 0
  ScaleType = 0
  ScrubCount = 0
  SeamHidden = false
  SeamVisible = true
  SmoothHidden = false
  SmoothVisible = true
  X = 90.8082
  XDirection = (-1,0,0)
  XSource = -> [Link018]
  Y = 105
FEATURE [Part::Feature] Unfold023  label="pillar_top_Unfold"
  shape: bbox 114.2 x 150.1 x 2.247 mm, 39 faces (baked)
FEATURE [PartDesign::FeatureBase] BaseFeature001
  BaseFeature = -> Unfold023
  Suppressed = false
  expr: BaseFeature = <<pillar_top_Unfold>>._self
FEATURE [PartDesign::Pocket] Pocket001
  BaseFeature = -> BaseFeature001
  Direction = (0,0,-1)
  Length = 5
  Length2 = 5
  Profile = -> Sketch001
  ReferenceAxis = -> Sketch001 [N_Axis]
  Reversed = true
  Suppressed = false
  Type = 0
FEATURE [PartDesign::Body] Body001  label="pillar_top_Body"
  Group = -> [BaseFeature001,Binder001,Sketch001,Pocket001]
  Origin = -> Origin001
  Tip = -> Pocket001
FEATURE [Sketcher::SketchObject] Unfold_Sketch023  label="pillar_top_Sketch"
  ExternalGeometry = -> [Binder001]
  FullyConstrained = false
  sketch-geometry (44):
    g0: LineSegment StartX=-57.0841 StartY=-1.08407 StartZ=0 EndX=-57.0841 EndY=-75.0841 EndZ=0
    g1: LineSegment StartX=-52.0841 StartY=3.91593 StartZ=0 EndX=-36.0841 EndY=3.91593 EndZ=0
    g2: LineSegment StartX=-36.0841 StartY=3.91593 StartZ=0 EndX=-36.0841 EndY=-0.0840704 EndZ=0
    g3: LineSegment StartX=-36.0841 StartY=-0.0840704 StartZ=0 EndX=-32 EndY=-0.0840704 EndZ=0
    g4: LineSegment StartX=-52.0841 StartY=-80.0841 StartZ=0 EndX=52.0841 EndY=-80.0841 EndZ=0
    g5: LineSegment StartX=57.0841 StartY=-1.08407 StartZ=0 EndX=57.0841 EndY=-75.0841 EndZ=0
    g6: LineSegment StartX=36.0841 StartY=3.91593 StartZ=0 EndX=52.0841 EndY=3.91593 EndZ=0
    g7: LineSegment StartX=36.0841 StartY=3.91593 StartZ=0 EndX=36.0841 EndY=-0.0840704 EndZ=0
    g8: LineSegment StartX=32 StartY=-0.0840704 StartZ=0 EndX=36.0841 EndY=-0.0840704 EndZ=0
    g9: LineSegment StartX=32 StartY=-0.0840704 StartZ=0 EndX=32 EndY=65 EndZ=0
    g10: LineSegment StartX=27 StartY=70 StartZ=0 EndX=-27 EndY=70 EndZ=0
    g11: LineSegment StartX=-32 StartY=65 StartZ=0 EndX=-32 EndY=-0.0840704 EndZ=0
    g12: LineSegment StartX=-8.5 StartY=-1.08407 StartZ=0 EndX=-8.5 EndY=28 EndZ=0
    g13: LineSegment StartX=-8.5 StartY=28 StartZ=0 EndX=8.5 EndY=28 EndZ=0
    g14: LineSegment StartX=8.5 StartY=28 StartZ=0 EndX=8.5 EndY=20.9904 EndZ=0
    g15: ArcOfCircle CenterX=16 CenterY=20.9904 CenterZ=0 NormalX=0 NormalY=0 NormalZ=1 AngleXU=0 Radius=7.5 StartAngle=3.14159 EndAngle=4.18879
    g16: ArcOfCircle CenterX=8.5 CenterY=8 CenterZ=0 NormalX=0 NormalY=0 NormalZ=1 AngleXU=0 Radius=7.5 StartAngle=0 EndAngle=1.0472
    g17: LineSegment StartX=16 StartY=8 StartZ=0 EndX=16 EndY=6 EndZ=0
    g18: ArcOfCircle CenterX=15 CenterY=6 CenterZ=0 NormalX=0 NormalY=0 NormalZ=1 AngleXU=0 Radius=1 StartAngle=4.71239 EndAngle=6.28319
    g19: ArcOfCircle CenterX=15 CenterY=4 CenterZ=0 NormalX=0 NormalY=0 NormalZ=1 AngleXU=0 Radius=1 StartAngle=1.5708 EndAngle=3.14159
    g20: LineSegment StartX=14 StartY=4 StartZ=0 EndX=14 EndY=-1.08407 EndZ=0
    g21: LineSegment StartX=-8.5 StartY=-1.08407 StartZ=0 EndX=14 EndY=-1.08407 EndZ=0
    g22: Circle CenterX=-12.5 CenterY=-7.08407 CenterZ=0 NormalX=0 NormalY=0 NormalZ=-1 AngleXU=3.14159 Radius=1.8
    g23: Circle CenterX=12.5 CenterY=-7.08407 CenterZ=0 NormalX=0 NormalY=0 NormalZ=-1 AngleXU=3.14159 Radius=1.8
    g24: Circle CenterX=-42.0841 CenterY=-76.0841 CenterZ=0 NormalX=0 NormalY=0 NormalZ=1 AngleXU=3.14159 Radius=1.7
    g25: Circle CenterX=42.0841 CenterY=-76.0841 CenterZ=0 NormalX=0 NormalY=0 NormalZ=-1 AngleXU=3.14159 Radius=1.7
    g26: Circle CenterX=-42.0841 CenterY=-6.08407 CenterZ=0 NormalX=0 NormalY=0 NormalZ=1 AngleXU=3.14159 Radius=1.7
    g27: Circle CenterX=42.0841 CenterY=-6.08407 CenterZ=0 NormalX=0 NormalY=0 NormalZ=-1 AngleXU=3.14159 Radius=1.7
    g28: Circle CenterX=0 CenterY=35 CenterZ=0 NormalX=0 NormalY=0 NormalZ=1 AngleXU=-3.14159 Radius=1.7
    g29: Circle CenterX=0 CenterY=-75.0841 CenterZ=0 NormalX=0 NormalY=0 NormalZ=-1 AngleXU=3.14159 Radius=1.7
    g30: Circle CenterX=-25 CenterY=60 CenterZ=0 NormalX=0 NormalY=0 NormalZ=1 AngleXU=-3.14159 Radius=1.7
    g31: Circle CenterX=25 CenterY=60 CenterZ=0 NormalX=0 NormalY=0 NormalZ=1 AngleXU=-3.14159 Radius=1.7
    g32: ArcOfCircle CenterX=-52.0841 CenterY=-1.08407 CenterZ=0 NormalX=0 NormalY=0 NormalZ=1 AngleXU=0 Radius=5 StartAngle=1.5708 EndAngle=3.14159
    g33: ArcOfCircle CenterX=-52.0841 CenterY=-75.0841 CenterZ=0 NormalX=0 NormalY=0 NormalZ=1 AngleXU=0 Radius=5 StartAngle=3.14159 EndAngle=4.71239
    g34: ArcOfCircle CenterX=52.0841 CenterY=-75.0841 CenterZ=0 NormalX=0 NormalY=0 NormalZ=1 AngleXU=0 Radius=5 StartAngle=4.71239 EndAngle=6.28319
    g35: ArcOfCircle CenterX=52.0841 CenterY=-1.08407 CenterZ=0 NormalX=0 NormalY=0 NormalZ=1 AngleXU=0 Radius=5 StartAngle=-2.7e-15 EndAngle=1.5708
    g36: ArcOfCircle CenterX=27 CenterY=65 CenterZ=0 NormalX=0 NormalY=0 NormalZ=1 AngleXU=0 Radius=5 StartAngle=3.24e-14 EndAngle=1.5708
    g37: ArcOfCircle CenterX=-27 CenterY=65 CenterZ=0 NormalX=0 NormalY=0 NormalZ=1 AngleXU=0 Radius=5 StartAngle=1.5708 EndAngle=3.14159
    g38: LineSegment StartX=34.042 StartY=-80.0841 StartZ=0 EndX=34.042 EndY=-78.0841 EndZ=0
    g39: LineSegment StartX=-34.042 StartY=-80.0841 StartZ=0 EndX=-34.042 EndY=-78.0841 EndZ=0
    g40: LineSegment StartX=-34.042 StartY=-0.0840704 StartZ=0 EndX=-34.042 EndY=-2.08407 EndZ=0
    g41: LineSegment StartX=-32 StartY=1.95796 StartZ=0 EndX=-30 EndY=1.95796 EndZ=0
    g42: LineSegment StartX=32 StartY=1.95796 StartZ=0 EndX=30 EndY=1.95796 EndZ=0
    g43: LineSegment StartX=34.042 StartY=-0.0840704 StartZ=0 EndX=34.042 EndY=-2.08407 EndZ=0
  constraints (54):
    c: Block(g4)
    c: Block(g0)
    c: Block(g5)
    c: Block(g6)
    c: Block(g9)
    c: Block(g11)
    c: Block(g10)
    c: Block(g1)
    c: Coincident(g32,g0)
    c: Tangent(g32,g1) = 1.5708
    c: Coincident(g33,g0)
    c: Coincident(g34,g5)
    c: Coincident(g35,g5)
    c: Coincident(g36,g10)
    c: Coincident(g37,g10)
    c: Tangent(g37,g11) = -1.5708
    c: Tangent(g36,g9) = -1.5708
    c: Tangent(g35,g6) = 1.5708
    c: Tangent(g33,g4) = -1.5708
    c: Tangent(g34,g4) = -1.5708
    c: Coincident(g2,g3)
    c: Coincident(g1,g2)
    c: Coincident(g3,g11)
    c: Coincident(g12,g21)
    c: Coincident(g12,g13)
    c: Coincident(g14,g15)
    c: Coincident(g13,g14)
    c: Coincident(g15,g16)
    c: Coincident(g20,g21)
    c: Coincident(g19,g20)
    c: Coincident(g18,g19)
    c: Coincident(g17,g18)
    c: Coincident(g16,g17)
    c: Coincident(g8,g9)
    c: Coincident(g7,g8)
    c: Coincident(g6,g7)
    c: Coincident(g38,g-5)
    c: PointOnObject(g38,g-5)
    c: Coincident(g39,g-3)
    c: PointOnObject(g39,g-3)
    c: Coincident(g40,g-3)
    c: PointOnObject(g40,g-3)
    c: Coincident(g41,g-4)
    c: PointOnObject(g41,g-4)
    c: Coincident(g42,g-6)
    c: PointOnObject(g42,g-6)
    c: Coincident(g43,g-5)
    c: PointOnObject(g43,g-5)
    c: Equal(g41,g40)
    c: Equal(g40,g39)
    c: Equal(g39,g38)
    c: Equal(g38,g43)
    c: Equal(g43,g42)
    c: DistanceX(g41,g41) = 2
FEATURE [Sketcher::SketchObject] Unfold_Sketch_bends023  label="pillar_top_Sketch_bends"
  FullyConstrained = false
  sketch-geometry (4):
    g0: LineSegment StartX=-8.5 StartY=1.95796 StartZ=0 EndX=-32 EndY=1.95796 EndZ=0
    g1: LineSegment StartX=-34.042 StartY=-80.0841 StartZ=0 EndX=-34.042 EndY=-0.0840704 EndZ=0
    g2: LineSegment StartX=34.042 StartY=-80.0841 StartZ=0 EndX=34.042 EndY=-0.0840704 EndZ=0
    g3: LineSegment StartX=32 StartY=1.95796 StartZ=0 EndX=14 EndY=1.95796 EndZ=0
FEATURE [App::DocumentObjectGroup] Group003  label="pillar_top_unfolds"
  Group = -> [Body001,Page001,Unfold023,Unfold_Sketch023,Unfold_Sketch_bends023]
FEATURE [TechDraw::DrawViewDimension] Dimension069
  AngleOverride = false
  Arbitrary = false
  ArbitraryTolerances = false
  BoxCorners = (2) [(-126.62,-7.33215,-1e-07),(126.62,7.33215,1e-07)]
  EqualTolerance = true
  ExtensionAngle = 0
  FormatSpec = %.2w
  FormatSpecOverTolerance = %+.2w
  FormatSpecUnderTolerance = %+.2w
  Inverted = false
  LineAngle = 0
  LockPosition = false
  MeasureType = 1
  OverTolerance = 0
  References2D = -> [View038]
  Rotation = 0
  ScaleType = 0
  TheoreticalExact = false
  Type = 2
  UnderTolerance = 0
  X = 12.3153
  Y = -12.062
FEATURE [TechDraw::DrawPage] Page014  label="basement_amplifier_page"
  KeepUpdated = true
  NextBalloonIndex = 7
  ProjectionType = 0
  Template = -> Template002
  Views = -> [View037,View038,Dimension041,Dimension042,Dimension069]
FEATURE [TechDraw::DrawViewPart] View053
  CoarseView = false
  Direction = (0,1,0)
  Focus = 100
  HardHidden = false
  IsoCount = 0
  IsoHidden = false
  IsoVisible = false
  LockPosition = false
  Perspective = false
  Rotation = 0
  Scale = 0.4
  ScaleType = 2
  ScrubCount = 0
  SeamHidden = false
  SeamVisible = true
  SmoothHidden = false
  SmoothVisible = true
  X = 123
  XDirection = (-1,0,0)
  XSource = -> [Link]
  Y = 41
FEATURE [App::Link] Link022  label="pillar3"
  LinkedObject = -> <external composit_full_size3.FCStd>#Body141
FEATURE [App::Link] Link023  label="pillar3_hat_fix"
  LinkedObject = -> <external composit_full_size3.FCStd>#Body144
FEATURE [App::Link] Link024  label="pilllar3_dec_corner_mirror"
  LinkedObject = -> <external composit_full_size3.FCStd>#Body147
FEATURE [App::Link] Link025  label="pilllar3_dec_corner"
  LinkedObject = -> <external composit_full_size3.FCStd>#Body145
FEATURE [App::DocumentObjectGroup] Group  label="parts"
  Group = -> [Link,Link001,Link005,Link003,Link002,Link004,Link006,Link007,Link013,Link014,Link018,Link019,Part__Mirroring004,Link021,Link022,Link023,Link024,Link025]
FEATURE [TechDraw::DrawViewPart] View054
  CoarseView = false
  Direction = (0,0,1)
  Focus = 100
  HardHidden = false
  IsoCount = 0
  IsoHidden = false
  IsoVisible = false
  LockPosition = false
  Perspective = false
  Rotation = 0
  ScaleType = 0
  ScrubCount = 0
  SeamHidden = false
  SeamVisible = true
  SmoothHidden = false
  SmoothVisible = true
  X = 148.5
  XDirection = (1,0,0)
  XSource = -> [Link022]
  Y = 105
FEATURE [TechDraw::DrawViewPart] View055
  CoarseView = false
  Direction = (0,1,0)
  Focus = 100
  HardHidden = false
  IsoCount = 0
  IsoHidden = false
  IsoVisible = false
  LockPosition = false
  Perspective = false
  Rotation = 0
  Scale = 0.17
  ScaleType = 2
  ScrubCount = 0
  SeamHidden = false
  SeamVisible = true
  SmoothHidden = false
  SmoothVisible = true
  X = 148.5
  XDirection = (0,0,1)
  XSource = -> [Link022]
  Y = 185
FEATURE [TechDraw::DrawViewPart] View056
  CoarseView = false
  Direction = (-0.57735,0.57735,0.57735)
  Focus = 100
  HardHidden = false
  IsoCount = 0
  IsoHidden = false
  IsoVisible = false
  LockPosition = false
  Perspective = false
  Rotation = 90
  Scale = 0.2
  ScaleType = 2
  ScrubCount = 0
  SeamHidden = false
  SeamVisible = true
  SmoothHidden = false
  SmoothVisible = true
  X = 148.5
  XDirection = (-0.707107,-0.707107,0)
  XSource = -> [Link022]
  Y = 145
FEATURE [TechDraw::DrawViewPart] View057
  CoarseView = false
  Direction = (-1,0,0)
  Focus = 100
  HardHidden = false
  IsoCount = 0
  IsoHidden = false
  IsoVisible = false
  LockPosition = false
  Perspective = false
  Rotation = 0
  ScaleType = 0
  ScrubCount = 0
  SeamHidden = false
  SeamVisible = true
  SmoothHidden = false
  SmoothVisible = true
  X = 148.5
  XDirection = (0,-1,0)
  XSource = -> [Link023]
  Y = 105
FEATURE [TechDraw::DrawViewPart] View058
  CoarseView = false
  Direction = (-0.57735,0.57735,0.57735)
  Focus = 100
  HardHidden = false
  IsoCount = 0
  IsoHidden = false
  IsoVisible = false
  LockPosition = false
  Perspective = false
  Rotation = 0
  ScaleType = 0
  ScrubCount = 0
  SeamHidden = false
  SeamVisible = true
  SmoothHidden = false
  SmoothVisible = true
  X = 53.2256
  XDirection = (-0.707107,-0.707107,0)
  XSource = -> [Link023]
  Y = 104.669
FEATURE [TechDraw::DrawViewPart] View059
  CoarseView = false
  Direction = (0,0,1)
  Focus = 100
  HardHidden = false
  IsoCount = 0
  IsoHidden = false
  IsoVisible = false
  LockPosition = false
  Perspective = false
  Rotation = 0
  ScaleType = 0
  ScrubCount = 0
  SeamHidden = false
  SeamVisible = true
  SmoothHidden = false
  SmoothVisible = true
  X = 148.5
  XDirection = (1,0,0)
  XSource = -> [Link025]
  Y = 105
FEATURE [TechDraw::DrawViewPart] View060
  CoarseView = false
  Direction = (0.57735,0.57735,0.57735)
  Focus = 100
  HardHidden = false
  IsoCount = 0
  IsoHidden = false
  IsoVisible = false
  LockPosition = false
  Perspective = false
  Rotation = 90
  Scale = 0.2
  ScaleType = 2
  ScrubCount = 0
  SeamHidden = false
  SeamVisible = true
  SmoothHidden = false
  SmoothVisible = true
  X = 148.5
  XDirection = (-0.707107,0.707107,0)
  XSource = -> [Link025]
  Y = 155
FEATURE [TechDraw::DrawViewPart] View061
  CoarseView = false
  Direction = (-0.57735,0.57735,0.57735)
  Focus = 100
  HardHidden = false
  IsoCount = 0
  IsoHidden = false
  IsoVisible = false
  LockPosition = false
  Perspective = false
  Rotation = 90
  Scale = 0.25
  ScaleType = 2
  ScrubCount = 0
  SeamHidden = false
  SeamVisible = true
  SmoothHidden = false
  SmoothVisible = true
  X = 148.5
  XDirection = (-0.707107,-0.707107,0)
  XSource = -> [Link024]
  Y = 145
FEATURE [TechDraw::DrawViewPart] View062
  CoarseView = false
  Direction = (0,0,1)
  Focus = 100
  HardHidden = false
  IsoCount = 0
  IsoHidden = false
  IsoVisible = false
  LockPosition = false
  Perspective = false
  Rotation = 0
  ScaleType = 0
  ScrubCount = 0
  SeamHidden = false
  SeamVisible = true
  SmoothHidden = false
  SmoothVisible = true
  X = 148.5
  XDirection = (1,0,0)
  XSource = -> [Link024]
  Y = 105
FEATURE [Part::Feature] Unfold031
  shape: bbox 101 x 101.7 x 2.002 mm, 19 faces (baked)
FEATURE [Sketcher::SketchObject] Unfold_Sketch_Outline010
  FullyConstrained = false
  sketch-geometry (12):
    g0: ArcOfCircle CenterX=45.5 CenterY=0.712389 CenterZ=0 NormalX=0 NormalY=0 NormalZ=1 AngleXU=-2e-16 Radius=5 StartAngle=0 EndAngle=1.13485
    g1: LineSegment StartX=-19.6724 StartY=36.5877 StartZ=0 EndX=47.6113 EndY=5.24475 EndZ=0
    g2: ArcOfCircle CenterX=-8.10401 CenterY=61.4214 CenterZ=0 NormalX=0 NormalY=0 NormalZ=1 AngleXU=-2e-16 Radius=27.396 StartAngle=3.14159 EndAngle=4.27645
    g3: LineSegment StartX=-35.5 StartY=71.7124 StartZ=0 EndX=-35.5 EndY=61.4214 EndZ=0
    g4: ArcOfCircle CenterX=-40.5 CenterY=71.7124 CenterZ=0 NormalX=0 NormalY=0 NormalZ=1 AngleXU=-2e-16 Radius=5 StartAngle=0 EndAngle=1.5708
    g5: LineSegment StartX=-45.5 StartY=76.7124 StartZ=0 EndX=-40.5 EndY=76.7124 EndZ=0
    g6: ArcOfCircle CenterX=-45.5 CenterY=71.7124 CenterZ=0 NormalX=0 NormalY=0 NormalZ=1 AngleXU=-2e-16 Radius=5 StartAngle=1.5708 EndAngle=3.14159
    g7: LineSegment StartX=-50.5 StartY=-4 StartZ=0 EndX=-50.5 EndY=71.7124 EndZ=0
    g8: ArcOfCircle CenterX=-29.5 CenterY=-4 CenterZ=0 NormalX=0 NormalY=0 NormalZ=1 AngleXU=0 Radius=21 StartAngle=3.14159 EndAngle=4.71239
    g9: LineSegment StartX=29.5 StartY=-25 StartZ=0 EndX=-29.5 EndY=-25 EndZ=0
    g10: ArcOfCircle CenterX=29.5 CenterY=-4 CenterZ=0 NormalX=0 NormalY=0 NormalZ=1 AngleXU=0 Radius=21 StartAngle=4.71239 EndAngle=6.28319
    g11: LineSegment StartX=50.5 StartY=0.712389 StartZ=0 EndX=50.5 EndY=-4 EndZ=0
FEATURE [Sketcher::SketchObject] Unfold_Sketch_Internal005
  FullyConstrained = false
  sketch-geometry (5):
    g0: Circle CenterX=40 CenterY=-12 CenterZ=0 NormalX=0 NormalY=0 NormalZ=1 AngleXU=0 Radius=2.75
    g1: Circle CenterX=-40 CenterY=-12 CenterZ=0 NormalX=0 NormalY=0 NormalZ=1 AngleXU=0 Radius=2.75
    g2: Circle CenterX=-43 CenterY=68.3791 CenterZ=0 NormalX=0 NormalY=0 NormalZ=-1 AngleXU=-3.14159 Radius=1.7
    g3: Circle CenterX=-43 CenterY=37.0457 CenterZ=0 NormalX=0 NormalY=0 NormalZ=-1 AngleXU=-3.14159 Radius=1.7
    g4: Circle CenterX=-43 CenterY=5.71239 CenterZ=0 NormalX=0 NormalY=0 NormalZ=-1 AngleXU=-3.14159 Radius=1.7
FEATURE [Sketcher::SketchObject] Unfold_Sketch_bends031
  FullyConstrained = false
  Placement = pos=(0,-0.141109,0.460482) rot=(1,0,0;0.297352rad)
  sketch-geometry (1):
    g0: LineSegment StartX=-50.5 StartY=-1.57167 StartZ=0 EndX=50.5 EndY=-1.57167 EndZ=0
FEATURE [Sketcher::SketchObject] Unfold_Sketch031
  ExternalGeometry = -> [Unfold_Sketch_bends031]
  FullyConstrained = false
  sketch-geometry (19):
    g0: ArcOfCircle CenterX=45.5 CenterY=0.712389 CenterZ=0 NormalX=0 NormalY=0 NormalZ=1 AngleXU=-2e-16 Radius=5 StartAngle=0 EndAngle=1.13485
    g1: LineSegment StartX=-19.6724 StartY=36.5877 StartZ=0 EndX=47.6113 EndY=5.24475 EndZ=0
    g2: ArcOfCircle CenterX=-8.10401 CenterY=61.4214 CenterZ=0 NormalX=0 NormalY=0 NormalZ=1 AngleXU=-2e-16 Radius=27.396 StartAngle=3.14159 EndAngle=4.27645
    g3: LineSegment StartX=-35.5 StartY=71.7124 StartZ=0 EndX=-35.5 EndY=61.4214 EndZ=0
    g4: ArcOfCircle CenterX=-40.5 CenterY=71.7124 CenterZ=0 NormalX=0 NormalY=0 NormalZ=1 AngleXU=-2e-16 Radius=5 StartAngle=0 EndAngle=1.5708
    g5: LineSegment StartX=-45.5 StartY=76.7124 StartZ=0 EndX=-40.5 EndY=76.7124 EndZ=0
    g6: ArcOfCircle CenterX=-45.5 CenterY=71.7124 CenterZ=0 NormalX=0 NormalY=0 NormalZ=1 AngleXU=-2e-16 Radius=5 StartAngle=1.5708 EndAngle=3.14159
    g7: LineSegment StartX=-50.5 StartY=-4 StartZ=0 EndX=-50.5 EndY=71.7124 EndZ=0
    g8: ArcOfCircle CenterX=-29.5 CenterY=-4 CenterZ=0 NormalX=0 NormalY=0 NormalZ=1 AngleXU=0 Radius=21 StartAngle=3.14159 EndAngle=4.71239
    g9: LineSegment StartX=29.5 StartY=-25 StartZ=0 EndX=-29.5 EndY=-25 EndZ=0
    g10: ArcOfCircle CenterX=29.5 CenterY=-4 CenterZ=0 NormalX=0 NormalY=0 NormalZ=1 AngleXU=0 Radius=21 StartAngle=4.71239 EndAngle=6.28319
    g11: LineSegment StartX=50.5 StartY=0.712389 StartZ=0 EndX=50.5 EndY=-4 EndZ=0
    g12: Circle CenterX=-40 CenterY=-12 CenterZ=0 NormalX=0 NormalY=0 NormalZ=1 AngleXU=0 Radius=2.75
    g13: Circle CenterX=40 CenterY=-12 CenterZ=0 NormalX=0 NormalY=0 NormalZ=1 AngleXU=0 Radius=2.75
    g14: Circle CenterX=-43 CenterY=37.0457 CenterZ=0 NormalX=0 NormalY=0 NormalZ=-1 AngleXU=-3.14159 Radius=1.7
    g15: Circle CenterX=-43 CenterY=68.3791 CenterZ=0 NormalX=0 NormalY=0 NormalZ=-1 AngleXU=-3.14159 Radius=1.7
    g16: Circle CenterX=-43 CenterY=5.71239 CenterZ=0 NormalX=0 NormalY=0 NormalZ=-1 AngleXU=-3.14159 Radius=1.7
    g17: LineSegment StartX=-50.5 StartY=-1.64381 StartZ=0 EndX=-48.5 EndY=-1.64381 EndZ=0
    g18: LineSegment StartX=50.5 StartY=-1.64381 StartZ=0 EndX=48.5 EndY=-1.64381 EndZ=0
  constraints (6):
    c: Coincident(g17,g-3)
    c: PointOnObject(g17,g-3)
    c: Coincident(g18,g-3)
    c: PointOnObject(g18,g-3)
    c: Equal(g18,g17)
    c: DistanceX(g17,g17) = 2
FEATURE [Part::Feature] Unfold032
  shape: bbox 592.8 x 516.9 x 2 mm, 76 faces (baked)
FEATURE [Sketcher::SketchObject] Unfold_Sketch_Outline011
  FullyConstrained = false
  sketch-geometry (51):
    g0: LineSegment StartX=320.189 StartY=36.6774 StartZ=0 EndX=321.093 EndY=29.6202 EndZ=0
    g1: LineSegment StartX=320.166 StartY=25 StartZ=0 EndX=321.093 EndY=29.6202 EndZ=0
    g2: LineSegment StartX=320.166 StartY=25 StartZ=0 EndX=320.166 EndY=-25 EndZ=0
    g3: LineSegment StartX=321.093 StartY=-29.6202 StartZ=0 EndX=320.166 EndY=-25 EndZ=0
    g4: LineSegment StartX=321.093 StartY=-29.6202 StartZ=0 EndX=320.189 EndY=-36.6774 EndZ=0
    g5: ArcOfCircle CenterX=310.27 CenterY=-35.4072 CenterZ=0 NormalX=0 NormalY=0 NormalZ=1 AngleXU=-2.94348 Radius=10 StartAngle=1.61797 EndAngle=2.81611
    g6: LineSegment StartX=312.699 StartY=-45.1078 StartZ=0 EndX=70.2846 EndY=-105.792 EndZ=0
    g7: ArcOfCircle CenterX=67.8562 CenterY=-96.091 CenterZ=0 NormalX=0 NormalY=0 NormalZ=1 AngleXU=-2.94348 Radius=10 StartAngle=0.325486 EndAngle=1.61797
    g8: LineSegment StartX=59.1959 StartY=-101.091 StartZ=0 EndX=49.4195 EndY=-84.1577 EndZ=0
    g9: LineSegment StartX=48.492 StartY=-79.5375 StartZ=0 EndX=49.4195 EndY=-84.1577 EndZ=0
    g10: LineSegment StartX=48.492 StartY=-79.5375 StartZ=0 EndX=46.188 EndY=-80 EndZ=0
    g11: LineSegment StartX=46.188 StartY=-80 StartZ=0 EndX=44.6355 EndY=-81.7641 EndZ=0
    g12: LineSegment StartX=48.173 StartY=-84.8774 StartZ=0 EndX=44.6355 EndY=-81.7641 EndZ=0
    g13: LineSegment StartX=48.173 StartY=-84.8774 StartZ=0 EndX=57.9494 EndY=-101.811 EndZ=0
    g14: ArcOfCircle CenterX=49.2891 CenterY=-106.811 CenterZ=0 NormalX=0 NormalY=0 NormalZ=1 AngleXU=0.849084 Radius=10 StartAngle=4.66521 EndAngle=5.9577
    g15: LineSegment StartX=56.476 StartY=-113.764 StartZ=0 EndX=-117.285 EndY=-293.359 EndZ=0
    g16: ArcOfCircle CenterX=-124.472 CenterY=-286.406 CenterZ=0 NormalX=0 NormalY=0 NormalZ=1 AngleXU=0.849084 Radius=10 StartAngle=3.46708 EndAngle=4.66521
    g17: LineSegment StartX=-128.331 StartY=-295.631 StartZ=0 EndX=-134.895 EndY=-292.885 EndZ=0
    g18: LineSegment StartX=-138.432 StartY=-289.772 StartZ=0 EndX=-134.895 EndY=-292.885 EndZ=0
    g19: LineSegment StartX=-138.432 StartY=-289.772 StartZ=0 EndX=-181.733 EndY=-264.772 EndZ=0
    g20: LineSegment StartX=-186.198 StartY=-263.265 StartZ=0 EndX=-181.733 EndY=-264.772 EndZ=0
    g21: LineSegment StartX=-186.198 StartY=-263.265 StartZ=0 EndX=-191.858 EndY=-258.953 EndZ=0
    g22: ArcOfCircle CenterX=-185.799 CenterY=-250.998 CenterZ=0 NormalX=0 NormalY=0 NormalZ=1 AngleXU=1.24531 Radius=10 StartAngle=1.61797 EndAngle=2.81611
    g23: LineSegment StartX=-195.414 StartY=-248.251 StartZ=0 EndX=-126.761 EndY=-7.9724 EndZ=0
    g24: ArcOfCircle CenterX=-117.145 CenterY=-10.7197 CenterZ=0 NormalX=0 NormalY=0 NormalZ=1 AngleXU=1.24531 Radius=10 StartAngle=0.325486 EndAngle=1.61797
    g25: LineSegment StartX=-117.145 StartY=-0.719696 StartZ=0 EndX=-97.5925 EndY=-0.719696 EndZ=0
    g26: LineSegment StartX=-93.1275 StartY=-2.22657 StartZ=0 EndX=-97.5925 EndY=-0.719696 EndZ=0
    g27: LineSegment StartX=-93.1275 StartY=-2.22657 StartZ=0 EndX=-92.376 EndY=5.73e-14 EndZ=0
    g28: LineSegment StartX=-92.376 StartY=6.8e-15 StartZ=0 EndX=-93.1275 EndY=2.22657 EndZ=0
    g29: LineSegment StartX=-97.5925 StartY=0.719696 StartZ=0 EndX=-93.1275 EndY=2.22657 EndZ=0
    g30: LineSegment StartX=-97.5925 StartY=0.719696 StartZ=0 EndX=-117.145 EndY=0.719696 EndZ=0
    g31: ArcOfCircle CenterX=-117.145 CenterY=10.7197 CenterZ=0 NormalX=0 NormalY=0 NormalZ=1 AngleXU=-1.24531 Radius=10 StartAngle=4.66521 EndAngle=5.9577
    g32: LineSegment StartX=-126.761 StartY=7.9724 StartZ=0 EndX=-195.414 EndY=248.251 EndZ=0
    g33: ArcOfCircle CenterX=-185.799 CenterY=250.998 CenterZ=0 NormalX=0 NormalY=0 NormalZ=1 AngleXU=-1.24531 Radius=10 StartAngle=3.46708 EndAngle=4.66521
    g34: LineSegment StartX=-191.858 StartY=258.953 StartZ=0 EndX=-186.198 EndY=263.265 EndZ=0
    g35: LineSegment StartX=-181.733 StartY=264.772 StartZ=0 EndX=-186.198 EndY=263.265 EndZ=0
    g36: LineSegment StartX=-181.733 StartY=264.772 StartZ=0 EndX=-138.432 EndY=289.772 EndZ=0
    g37: LineSegment StartX=-134.895 StartY=292.885 StartZ=0 EndX=-138.432 EndY=289.772 EndZ=0
    g38: LineSegment StartX=-134.895 StartY=292.885 StartZ=0 EndX=-128.331 EndY=295.631 EndZ=0
    g39: ArcOfCircle CenterX=-124.472 CenterY=286.406 CenterZ=0 NormalX=0 NormalY=0 NormalZ=1 AngleXU=-0.849084 Radius=10 StartAngle=1.61797 EndAngle=2.81611
    g40: LineSegment StartX=-117.285 StartY=293.359 StartZ=0 EndX=56.476 EndY=113.764 EndZ=0
    g41: ArcOfCircle CenterX=49.2891 CenterY=106.811 CenterZ=0 NormalX=0 NormalY=0 NormalZ=1 AngleXU=-0.849084 Radius=10 StartAngle=0.325486 EndAngle=1.61797
    g42: LineSegment StartX=57.9494 StartY=101.811 StartZ=0 EndX=48.173 EndY=84.8774 EndZ=0
    g43: LineSegment StartX=44.6355 StartY=81.7641 StartZ=0 EndX=48.173 EndY=84.8774 EndZ=0
    g44: LineSegment StartX=44.6355 StartY=81.7641 StartZ=0 EndX=46.188 EndY=80 EndZ=0
    g45: LineSegment StartX=46.188 StartY=80 StartZ=0 EndX=48.492 EndY=79.5375 EndZ=0
    g46: LineSegment StartX=49.4195 StartY=84.1577 StartZ=0 EndX=48.492 EndY=79.5375 EndZ=0
    g47: LineSegment StartX=49.4195 StartY=84.1577 StartZ=0 EndX=59.1959 EndY=101.091 EndZ=0
    g48: ArcOfCircle CenterX=67.8562 CenterY=96.091 CenterZ=0 NormalX=0 NormalY=0 NormalZ=1 AngleXU=2.94348 Radius=10 StartAngle=4.66521 EndAngle=5.9577
    g49: LineSegment StartX=70.2846 StartY=105.792 StartZ=0 EndX=312.699 EndY=45.1078 EndZ=0
    g50: ArcOfCircle CenterX=310.27 CenterY=35.4072 CenterZ=0 NormalX=0 NormalY=0 NormalZ=1 AngleXU=2.94348 Radius=10 StartAngle=3.46708 EndAngle=4.66521
FEATURE [Sketcher::SketchObject] Unfold_Sketch_Internal006
  FullyConstrained = false
  sketch-geometry (23):
    g0: Circle CenterX=-2e-16 CenterY=2e-16 CenterZ=0 NormalX=0 NormalY=0 NormalZ=1 AngleXU=-1.5708 Radius=28
    g1: Circle CenterX=-28.0433 CenterY=-38.5425 CenterZ=0 NormalX=0 NormalY=0 NormalZ=1 AngleXU=-1.5708 Radius=5.1
    g2: Circle CenterX=-28.0433 CenterY=38.5425 CenterZ=0 NormalX=0 NormalY=0 NormalZ=1 AngleXU=-1.5708 Radius=5.1
    g3: Circle CenterX=20.1316 CenterY=-43.205 CenterZ=0 NormalX=0 NormalY=0 NormalZ=1 AngleXU=-1.5708 Radius=5.1
    g4: Circle CenterX=20.1316 CenterY=43.205 CenterZ=0 NormalX=0 NormalY=0 NormalZ=1 AngleXU=-1.5708 Radius=5.1
    g5: Circle CenterX=-138.436 CenterY=-239.778 CenterZ=0 NormalX=0 NormalY=0 NormalZ=1 AngleXU=2.61799 Radius=2.75
    g6: Circle CenterX=-138.436 CenterY=239.778 CenterZ=0 NormalX=0 NormalY=0 NormalZ=1 AngleXU=0.523599 Radius=2.75
    g7: Circle CenterX=-155.936 CenterY=270.089 CenterZ=0 NormalX=0 NormalY=0 NormalZ=1 AngleXU=0.523599 Radius=2.75
    g8: Circle CenterX=-155.936 CenterY=-270.089 CenterZ=0 NormalX=0 NormalY=0 NormalZ=1 AngleXU=2.61799 Radius=2.75
    g9: Circle CenterX=276.872 CenterY=0 CenterZ=0 NormalX=0 NormalY=0 NormalZ=1 AngleXU=-1.5708 Radius=2.75
    g10: Circle CenterX=311.872 CenterY=0 CenterZ=0 NormalX=0 NormalY=0 NormalZ=1 AngleXU=-1.5708 Radius=2.75
    g11: Circle CenterX=-82.398 CenterY=15.936 CenterZ=0 NormalX=0 NormalY=0 NormalZ=1 AngleXU=0.523599 Radius=2.55
    g12: Circle CenterX=27.398 CenterY=79.3268 CenterZ=0 NormalX=0 NormalY=0 NormalZ=1 AngleXU=0.523599 Radius=2.55
    g13: Circle CenterX=27.398 CenterY=-79.3268 CenterZ=0 NormalX=0 NormalY=0 NormalZ=1 AngleXU=2.61799 Radius=2.55
    g14: Circle CenterX=-115.013 CenterY=-112.576 CenterZ=0 NormalX=0 NormalY=0 NormalZ=1 AngleXU=2.61799 Radius=2.55
    g15: Circle CenterX=-115.013 CenterY=112.576 CenterZ=0 NormalX=0 NormalY=0 NormalZ=1 AngleXU=0.523599 Radius=2.55
    g16: Circle CenterX=-82.398 CenterY=-15.936 CenterZ=0 NormalX=0 NormalY=0 NormalZ=1 AngleXU=2.61799 Radius=2.55
    g17: Circle CenterX=-39.9871 CenterY=155.892 CenterZ=0 NormalX=0 NormalY=0 NormalZ=1 AngleXU=0.523599 Radius=2.55
    g18: Circle CenterX=-39.9871 CenterY=-155.892 CenterZ=0 NormalX=0 NormalY=0 NormalZ=1 AngleXU=2.61799 Radius=2.55
    g19: Circle CenterX=55 CenterY=63.3907 CenterZ=0 NormalX=0 NormalY=0 NormalZ=1 AngleXU=-1.5708 Radius=2.55
    g20: Circle CenterX=55 CenterY=-63.3907 CenterZ=0 NormalX=0 NormalY=0 NormalZ=1 AngleXU=-1.5708 Radius=2.55
    g21: Circle CenterX=155 CenterY=43.3161 CenterZ=0 NormalX=0 NormalY=0 NormalZ=1 AngleXU=-1.5708 Radius=2.55
    g22: Circle CenterX=155 CenterY=-43.3161 CenterZ=0 NormalX=0 NormalY=0 NormalZ=1 AngleXU=-1.5708 Radius=2.55
FEATURE [Sketcher::SketchObject] Unfold_Sketch_bends032
  FullyConstrained = false
  sketch-geometry (6):
    g0: LineSegment StartX=320.629 StartY=27.3101 StartZ=0 EndX=48.9558 EndY=81.8476 EndZ=0
    g1: LineSegment StartX=48.9558 StartY=-81.8476 StartZ=0 EndX=320.629 EndY=-27.3101 EndZ=0
    g2: LineSegment StartX=46.4042 StartY=83.3207 StartZ=0 EndX=-136.663 EndY=291.328 EndZ=0
    g3: LineSegment StartX=-136.663 StartY=-291.328 StartZ=0 EndX=46.4042 EndY=-83.3207 EndZ=0
    g4: LineSegment StartX=-183.966 StartY=264.018 StartZ=0 EndX=-95.36 EndY=1.47313 EndZ=0
    g5: LineSegment StartX=-95.36 StartY=-1.47313 StartZ=0 EndX=-183.966 EndY=-264.018 EndZ=0
FEATURE [Sketcher::SketchObject] Unfold_Sketch032
  ExternalGeometry = -> [Unfold_Sketch_bends032]
  FullyConstrained = false
  sketch-geometry (86):
    g0: LineSegment StartX=320.189 StartY=36.6774 StartZ=0 EndX=321.093 EndY=29.6202 EndZ=0
    g1: ArcOfCircle CenterX=310.27 CenterY=35.4072 CenterZ=0 NormalX=0 NormalY=0 NormalZ=1 AngleXU=2.94348 Radius=10 StartAngle=3.46708 EndAngle=4.66521
    g2: LineSegment StartX=70.2846 StartY=105.792 StartZ=0 EndX=312.699 EndY=45.1078 EndZ=0
    g3: ArcOfCircle CenterX=67.8562 CenterY=96.091 CenterZ=0 NormalX=0 NormalY=0 NormalZ=1 AngleXU=2.94348 Radius=10 StartAngle=4.66521 EndAngle=5.9577
    g4: LineSegment StartX=49.4195 StartY=84.1577 StartZ=0 EndX=59.1959 EndY=101.091 EndZ=0
    g5: LineSegment StartX=49.4195 StartY=84.1577 StartZ=0 EndX=48.492 EndY=79.5375 EndZ=0
    g6: LineSegment StartX=46.188 StartY=80 StartZ=0 EndX=48.492 EndY=79.5375 EndZ=0
    g7: LineSegment StartX=44.6355 StartY=81.7641 StartZ=0 EndX=46.188 EndY=80 EndZ=0
    g8: LineSegment StartX=44.6355 StartY=81.7641 StartZ=0 EndX=48.173 EndY=84.8774 EndZ=0
    g9: LineSegment StartX=57.9494 StartY=101.811 StartZ=0 EndX=48.173 EndY=84.8774 EndZ=0
    g10: ArcOfCircle CenterX=49.2891 CenterY=106.811 CenterZ=0 NormalX=0 NormalY=0 NormalZ=1 AngleXU=-0.849084 Radius=10 StartAngle=0.325486 EndAngle=1.61797
    g11: LineSegment StartX=-117.285 StartY=293.359 StartZ=0 EndX=56.476 EndY=113.764 EndZ=0
    g12: ArcOfCircle CenterX=-124.472 CenterY=286.406 CenterZ=0 NormalX=0 NormalY=0 NormalZ=1 AngleXU=-0.849084 Radius=10 StartAngle=1.61797 EndAngle=2.81611
    g13: LineSegment StartX=-134.895 StartY=292.885 StartZ=0 EndX=-128.331 EndY=295.631 EndZ=0
    g14: LineSegment StartX=-134.895 StartY=292.885 StartZ=0 EndX=-138.432 EndY=289.772 EndZ=0
    g15: LineSegment StartX=-181.733 StartY=264.772 StartZ=0 EndX=-138.432 EndY=289.772 EndZ=0
    g16: LineSegment StartX=-181.733 StartY=264.772 StartZ=0 EndX=-186.198 EndY=263.265 EndZ=0
    g17: LineSegment StartX=-191.858 StartY=258.953 StartZ=0 EndX=-186.198 EndY=263.265 EndZ=0
    g18: ArcOfCircle CenterX=-185.799 CenterY=250.998 CenterZ=0 NormalX=0 NormalY=0 NormalZ=1 AngleXU=-1.24531 Radius=10 StartAngle=3.46708 EndAngle=4.66521
    g19: LineSegment StartX=-126.761 StartY=7.9724 StartZ=0 EndX=-195.414 EndY=248.251 EndZ=0
    g20: ArcOfCircle CenterX=-117.145 CenterY=10.7197 CenterZ=0 NormalX=0 NormalY=0 NormalZ=1 AngleXU=-1.24531 Radius=10 StartAngle=4.66521 EndAngle=5.9577
    g21: LineSegment StartX=-97.5925 StartY=0.719696 StartZ=0 EndX=-117.145 EndY=0.719696 EndZ=0
    g22: LineSegment StartX=-97.5925 StartY=0.719696 StartZ=0 EndX=-93.1275 EndY=2.22657 EndZ=0
    g23: LineSegment StartX=-92.376 StartY=6.8e-15 StartZ=0 EndX=-93.1275 EndY=2.22657 EndZ=0
    g24: LineSegment StartX=-93.1275 StartY=-2.22657 StartZ=0 EndX=-92.376 EndY=5.73e-14 EndZ=0
    g25: LineSegment StartX=-93.1275 StartY=-2.22657 StartZ=0 EndX=-97.5925 EndY=-0.719696 EndZ=0
    g26: LineSegment StartX=-117.145 StartY=-0.719696 StartZ=0 EndX=-97.5925 EndY=-0.719696 EndZ=0
    g27: ArcOfCircle CenterX=-117.145 CenterY=-10.7197 CenterZ=0 NormalX=0 NormalY=0 NormalZ=1 AngleXU=1.24531 Radius=10 StartAngle=0.325486 EndAngle=1.61797
    g28: LineSegment StartX=-195.414 StartY=-248.251 StartZ=0 EndX=-126.761 EndY=-7.9724 EndZ=0
    g29: ArcOfCircle CenterX=-185.799 CenterY=-250.998 CenterZ=0 NormalX=0 NormalY=0 NormalZ=1 AngleXU=1.24531 Radius=10 StartAngle=1.61797 EndAngle=2.81611
    g30: LineSegment StartX=-186.198 StartY=-263.265 StartZ=0 EndX=-191.858 EndY=-258.953 EndZ=0
    g31: LineSegment StartX=-186.198 StartY=-263.265 StartZ=0 EndX=-181.733 EndY=-264.772 EndZ=0
    g32: LineSegment StartX=-138.432 StartY=-289.772 StartZ=0 EndX=-181.733 EndY=-264.772 EndZ=0
    g33: LineSegment StartX=-138.432 StartY=-289.772 StartZ=0 EndX=-134.895 EndY=-292.885 EndZ=0
    g34: LineSegment StartX=-128.331 StartY=-295.631 StartZ=0 EndX=-134.895 EndY=-292.885 EndZ=0
    g35: ArcOfCircle CenterX=-124.472 CenterY=-286.406 CenterZ=0 NormalX=0 NormalY=0 NormalZ=1 AngleXU=0.849084 Radius=10 StartAngle=3.46708 EndAngle=4.66521
    g36: LineSegment StartX=56.476 StartY=-113.764 StartZ=0 EndX=-117.285 EndY=-293.359 EndZ=0
    g37: ArcOfCircle CenterX=49.2891 CenterY=-106.811 CenterZ=0 NormalX=0 NormalY=0 NormalZ=1 AngleXU=0.849084 Radius=10 StartAngle=4.66521 EndAngle=5.9577
    g38: LineSegment StartX=48.173 StartY=-84.8774 StartZ=0 EndX=57.9494 EndY=-101.811 EndZ=0
    g39: LineSegment StartX=48.173 StartY=-84.8774 StartZ=0 EndX=44.6355 EndY=-81.7641 EndZ=0
    g40: LineSegment StartX=46.188 StartY=-80 StartZ=0 EndX=44.6355 EndY=-81.7641 EndZ=0
    g41: LineSegment StartX=48.492 StartY=-79.5375 StartZ=0 EndX=46.188 EndY=-80 EndZ=0
    g42: LineSegment StartX=48.492 StartY=-79.5375 StartZ=0 EndX=49.4195 EndY=-84.1577 EndZ=0
    g43: LineSegment StartX=59.1959 StartY=-101.091 StartZ=0 EndX=49.4195 EndY=-84.1577 EndZ=0
    g44: ArcOfCircle CenterX=67.8562 CenterY=-96.091 CenterZ=0 NormalX=0 NormalY=0 NormalZ=1 AngleXU=-2.94348 Radius=10 StartAngle=0.325486 EndAngle=1.61797
    g45: LineSegment StartX=312.699 StartY=-45.1078 StartZ=0 EndX=70.2846 EndY=-105.792 EndZ=0
    g46: ArcOfCircle CenterX=310.27 CenterY=-35.4072 CenterZ=0 NormalX=0 NormalY=0 NormalZ=1 AngleXU=-2.94348 Radius=10 StartAngle=1.61797 EndAngle=2.81611
    g47: LineSegment StartX=321.093 StartY=-29.6202 StartZ=0 EndX=320.189 EndY=-36.6774 EndZ=0
    g48: LineSegment StartX=321.093 StartY=-29.6202 StartZ=0 EndX=320.166 EndY=-25 EndZ=0
    g49: LineSegment StartX=320.166 StartY=25 StartZ=0 EndX=320.166 EndY=-25 EndZ=0
    g50: LineSegment StartX=320.166 StartY=25 StartZ=0 EndX=321.093 EndY=29.6202 EndZ=0
    g51: Circle CenterX=-2e-16 CenterY=2e-16 CenterZ=0 NormalX=0 NormalY=0 NormalZ=1 AngleXU=-1.5708 Radius=28
    g52: Circle CenterX=20.1316 CenterY=43.205 CenterZ=0 NormalX=0 NormalY=0 NormalZ=1 AngleXU=-1.5708 Radius=5.1
    g53: Circle CenterX=20.1316 CenterY=-43.205 CenterZ=0 NormalX=0 NormalY=0 NormalZ=1 AngleXU=-1.5708 Radius=5.1
    g54: Circle CenterX=-28.0433 CenterY=38.5425 CenterZ=0 NormalX=0 NormalY=0 NormalZ=1 AngleXU=-1.5708 Radius=5.1
    g55: Circle CenterX=-28.0433 CenterY=-38.5425 CenterZ=0 NormalX=0 NormalY=0 NormalZ=1 AngleXU=-1.5708 Radius=5.1
    g56: Circle CenterX=-155.936 CenterY=-270.089 CenterZ=0 NormalX=0 NormalY=0 NormalZ=1 AngleXU=2.61799 Radius=2.75
    g57: Circle CenterX=-155.936 CenterY=270.089 CenterZ=0 NormalX=0 NormalY=0 NormalZ=1 AngleXU=0.523599 Radius=2.75
    g58: Circle CenterX=-138.436 CenterY=239.778 CenterZ=0 NormalX=0 NormalY=0 NormalZ=1 AngleXU=0.523599 Radius=2.75
    g59: Circle CenterX=311.872 CenterY=0 CenterZ=0 NormalX=0 NormalY=0 NormalZ=1 AngleXU=-1.5708 Radius=2.75
    g60: Circle CenterX=276.872 CenterY=0 CenterZ=0 NormalX=0 NormalY=0 NormalZ=1 AngleXU=-1.5708 Radius=2.75
    g61: Circle CenterX=-138.436 CenterY=-239.778 CenterZ=0 NormalX=0 NormalY=0 NormalZ=1 AngleXU=2.61799 Radius=2.75
    g62: Circle CenterX=155 CenterY=-43.3161 CenterZ=0 NormalX=0 NormalY=0 NormalZ=1 AngleXU=-1.5708 Radius=2.55
    g63: Circle CenterX=-39.9871 CenterY=-155.892 CenterZ=0 NormalX=0 NormalY=0 NormalZ=1 AngleXU=2.61799 Radius=2.55
    g64: Circle CenterX=-39.9871 CenterY=155.892 CenterZ=0 NormalX=0 NormalY=0 NormalZ=1 AngleXU=0.523599 Radius=2.55
    g65: Circle CenterX=155 CenterY=43.3161 CenterZ=0 NormalX=0 NormalY=0 NormalZ=1 AngleXU=-1.5708 Radius=2.55
    g66: Circle CenterX=55 CenterY=-63.3907 CenterZ=0 NormalX=0 NormalY=0 NormalZ=1 AngleXU=-1.5708 Radius=2.55
    g67: Circle CenterX=27.398 CenterY=-79.3268 CenterZ=0 NormalX=0 NormalY=0 NormalZ=1 AngleXU=2.61799 Radius=2.55
    g68: Circle CenterX=-82.398 CenterY=15.936 CenterZ=0 NormalX=0 NormalY=0 NormalZ=1 AngleXU=0.523599 Radius=2.55
    g69: Circle CenterX=-82.398 CenterY=-15.936 CenterZ=0 NormalX=0 NormalY=0 NormalZ=1 AngleXU=2.61799 Radius=2.55
    g70: Circle CenterX=55 CenterY=63.3907 CenterZ=0 NormalX=0 NormalY=0 NormalZ=1 AngleXU=-1.5708 Radius=2.55
    g71: Circle CenterX=27.398 CenterY=79.3268 CenterZ=0 NormalX=0 NormalY=0 NormalZ=1 AngleXU=0.523599 Radius=2.55
    g72: Circle CenterX=-115.013 CenterY=112.576 CenterZ=0 NormalX=0 NormalY=0 NormalZ=1 AngleXU=0.523599 Radius=2.55
    g73: Circle CenterX=-115.013 CenterY=-112.576 CenterZ=0 NormalX=0 NormalY=0 NormalZ=1 AngleXU=2.61799 Radius=2.55
    g74: LineSegment StartX=-95.36 StartY=1.47313 StartZ=0 EndX=-95.9995 EndY=3.36812 EndZ=0
    g75: LineSegment StartX=46.4042 StartY=83.3207 StartZ=0 EndX=45.0829 EndY=84.8221 EndZ=0
    g76: LineSegment StartX=-183.966 StartY=264.018 StartZ=0 EndX=-183.326 EndY=262.123 EndZ=0
    g77: LineSegment StartX=-136.663 StartY=291.328 StartZ=0 EndX=-135.342 EndY=289.827 EndZ=0
    g78: LineSegment StartX=320.629 StartY=27.3101 StartZ=0 EndX=318.668 EndY=27.7037 EndZ=0
    g79: LineSegment StartX=320.629 StartY=-27.3101 StartZ=0 EndX=318.668 EndY=-27.7037 EndZ=0
    g80: LineSegment StartX=48.9558 StartY=-81.8476 StartZ=0 EndX=50.9166 EndY=-81.4539 EndZ=0
    g81: LineSegment StartX=46.4042 StartY=-83.3207 StartZ=0 EndX=45.0829 EndY=-84.8221 EndZ=0
    g82: LineSegment StartX=48.9558 StartY=81.8476 StartZ=0 EndX=50.9166 EndY=81.4539 EndZ=0
    g83: LineSegment StartX=-95.36 StartY=-1.47313 StartZ=0 EndX=-95.9995 EndY=-3.36812 EndZ=0
    g84: LineSegment StartX=-183.966 StartY=-264.018 StartZ=0 EndX=-183.326 EndY=-262.123 EndZ=0
    g85: LineSegment StartX=-136.663 StartY=-291.328 StartZ=0 EndX=-135.342 EndY=-289.827 EndZ=0
  constraints (36):
    c: Coincident(g74,g-3)
    c: PointOnObject(g74,g-3)
    c: Coincident(g75,g-4)
    c: PointOnObject(g75,g-4)
    c: Equal(g75,g74)
    c: Distance(g74) = 2
    c: Coincident(g76,g-3)
    c: PointOnObject(g76,g-3)
    c: Coincident(g77,g-4)
    c: PointOnObject(g77,g-4)
    c: Coincident(g78,g-5)
    c: PointOnObject(g78,g-5)
    c: Coincident(g79,g-6)
    c: PointOnObject(g79,g-6)
    c: Coincident(g80,g-6)
    c: PointOnObject(g80,g-6)
    c: Coincident(g81,g-7)
    c: PointOnObject(g81,g-7)
    c: Coincident(g82,g-5)
    c: PointOnObject(g82,g-5)
    c: Coincident(g83,g-8)
    c: PointOnObject(g83,g-8)
    c: Coincident(g84,g-8)
    c: PointOnObject(g84,g-8)
    c: Coincident(g85,g-7)
    c: PointOnObject(g85,g-7)
    c: Equal(g85,g84)
    c: Equal(g84,g81)
    c: Equal(g81,g80)
    c: Equal(g80,g79)
    c: Equal(g79,g78)
    c: Equal(g78,g82)
    c: Equal(g82,g75)
    c: Equal(g75,g77)
    c: Equal(g77,g76)
    c: Equal(g83,g74)
FEATURE [App::DocumentObjectGroup] Group014  label="basement_amplifier_top_unfolds"
  Group = -> [Page014,Unfold_Sketch032,Unfold032,Unfold_Sketch_Outline011,Unfold_Sketch_Internal006,Unfold_Sketch_bends032]
FEATURE [Part::Feature] Unfold034
  shape: bbox 69.24 x 1.5 x 1684 mm, 47 faces (baked)
FEATURE [Sketcher::SketchObject] Unfold_Sketch_Outline013
  FullyConstrained = false
  sketch-geometry (8):
    g0: LineSegment StartX=0 StartY=-29.6197 StartZ=0 EndX=0 EndY=29.6197 EndZ=0
    g1: ArcOfCircle CenterX=5 CenterY=29.6197 CenterZ=0 NormalX=0 NormalY=0 NormalZ=1 AngleXU=1.5708 Radius=5 StartAngle=0 EndAngle=1.5708
    g2: LineSegment StartX=5 StartY=34.6197 StartZ=0 EndX=1679 EndY=34.6197 EndZ=0
    g3: ArcOfCircle CenterX=1679 CenterY=29.6197 CenterZ=0 NormalX=0 NormalY=0 NormalZ=1 AngleXU=1.5708 Radius=5 StartAngle=4.71239 EndAngle=6.28319
    g4: LineSegment StartX=1684 StartY=-29.6197 StartZ=0 EndX=1684 EndY=29.6197 EndZ=0
    g5: ArcOfCircle CenterX=1679 CenterY=-29.6197 CenterZ=0 NormalX=0 NormalY=0 NormalZ=1 AngleXU=-1.5708 Radius=5 StartAngle=0 EndAngle=1.5708
    g6: LineSegment StartX=5 StartY=-34.6197 StartZ=0 EndX=1679 EndY=-34.6197 EndZ=0
    g7: ArcOfCircle CenterX=5 CenterY=-29.6197 CenterZ=0 NormalX=0 NormalY=0 NormalZ=1 AngleXU=-1.5708 Radius=5 StartAngle=4.71239 EndAngle=6.28319
FEATURE [Sketcher::SketchObject] Unfold_Sketch_Internal007
  FullyConstrained = false
  sketch-geometry (37):
    g0: LineSegment StartX=615.9 StartY=-5.75 StartZ=0 EndX=614.1 EndY=-5.75 EndZ=0
    g1: ArcOfCircle CenterX=614.1 CenterY=-4.15 CenterZ=0 NormalX=0 NormalY=0 NormalZ=1 AngleXU=-1.5708 Radius=1.6 StartAngle=3.14159 EndAngle=6.28319
    g2: LineSegment StartX=615.9 StartY=-2.55 StartZ=0 EndX=614.1 EndY=-2.55 EndZ=0
    g3: ArcOfCircle CenterX=615.9 CenterY=-4.15 CenterZ=0 NormalX=0 NormalY=0 NormalZ=1 AngleXU=-1.5708 Radius=1.6 StartAngle=0 EndAngle=3.14159
    g4: LineSegment StartX=615.9 StartY=2.55 StartZ=0 EndX=614.1 EndY=2.55 EndZ=0
    g5: ArcOfCircle CenterX=614.1 CenterY=4.15 CenterZ=0 NormalX=0 NormalY=0 NormalZ=1 AngleXU=1.5708 Radius=1.6 StartAngle=0 EndAngle=3.14159
    g6: LineSegment StartX=615.9 StartY=5.75 StartZ=0 EndX=614.1 EndY=5.75 EndZ=0
    g7: ArcOfCircle CenterX=615.9 CenterY=4.15 CenterZ=0 NormalX=0 NormalY=0 NormalZ=1 AngleXU=1.5708 Radius=1.6 StartAngle=3.14159 EndAngle=6.28319
    g8: Circle CenterX=1303 CenterY=0 CenterZ=0 NormalX=0 NormalY=0 NormalZ=-1 AngleXU=1.5708 Radius=1.7
    g9: Circle CenterX=1574 CenterY=0 CenterZ=0 NormalX=0 NormalY=0 NormalZ=-1 AngleXU=1.5708 Radius=1.7
    g10: Circle CenterX=1032 CenterY=0 CenterZ=0 NormalX=0 NormalY=0 NormalZ=-1 AngleXU=1.5708 Radius=1.7
    g11: Circle CenterX=1604 CenterY=-27.6197 CenterZ=0 NormalX=0 NormalY=0 NormalZ=-1 AngleXU=1.5708 Radius=1.7
    g12: Circle CenterX=1574 CenterY=-25.6197 CenterZ=0 NormalX=0 NormalY=0 NormalZ=-1 AngleXU=1.5708 Radius=1.7
    g13: Circle CenterX=1303 CenterY=-25.6197 CenterZ=0 NormalX=0 NormalY=0 NormalZ=-1 AngleXU=1.5708 Radius=1.7
    g14: Circle CenterX=1032 CenterY=-25.6197 CenterZ=0 NormalX=0 NormalY=0 NormalZ=-1 AngleXU=1.5708 Radius=1.7
    g15: Circle CenterX=1574 CenterY=25.6197 CenterZ=0 NormalX=0 NormalY=0 NormalZ=-1 AngleXU=1.5708 Radius=1.7
    g16: Circle CenterX=1303 CenterY=25.6197 CenterZ=0 NormalX=0 NormalY=0 NormalZ=-1 AngleXU=1.5708 Radius=1.7
    g17: Circle CenterX=1032 CenterY=25.6197 CenterZ=0 NormalX=0 NormalY=0 NormalZ=-1 AngleXU=1.5708 Radius=1.7
    g18: Circle CenterX=1674 CenterY=27.6197 CenterZ=0 NormalX=0 NormalY=0 NormalZ=-1 AngleXU=1.5708 Radius=1.7
    g19: Circle CenterX=1604 CenterY=27.6197 CenterZ=0 NormalX=0 NormalY=0 NormalZ=-1 AngleXU=1.5708 Radius=1.7
    g20: Circle CenterX=1674 CenterY=-27.6197 CenterZ=0 NormalX=0 NormalY=0 NormalZ=-1 AngleXU=1.5708 Radius=1.7
    g21: Circle CenterX=490 CenterY=0 CenterZ=0 NormalX=0 NormalY=0 NormalZ=-1 AngleXU=1.5708 Radius=1.7
    g22: Circle CenterX=490 CenterY=25.6197 CenterZ=0 NormalX=0 NormalY=0 NormalZ=-1 AngleXU=1.5708 Radius=1.7
    g23: Circle CenterX=490 CenterY=-25.6197 CenterZ=0 NormalX=0 NormalY=0 NormalZ=-1 AngleXU=1.5708 Radius=1.7
    g24: Circle CenterX=761 CenterY=0 CenterZ=0 NormalX=0 NormalY=0 NormalZ=-1 AngleXU=1.5708 Radius=1.7
    g25: Circle CenterX=761 CenterY=-25.6197 CenterZ=0 NormalX=0 NormalY=0 NormalZ=-1 AngleXU=1.5708 Radius=1.7
    g26: Circle CenterX=761 CenterY=25.6197 CenterZ=0 NormalX=0 NormalY=0 NormalZ=-1 AngleXU=1.5708 Radius=1.7
    g27: Circle CenterX=40.3333 CenterY=27.1197 CenterZ=0 NormalX=0 NormalY=0 NormalZ=-1 AngleXU=1.5708 Radius=1.7
    g28: Circle CenterX=71.6667 CenterY=27.1197 CenterZ=0 NormalX=0 NormalY=0 NormalZ=-1 AngleXU=1.5708 Radius=1.7
    g29: Circle CenterX=71.6667 CenterY=-27.1197 CenterZ=0 NormalX=0 NormalY=0 NormalZ=1 AngleXU=-1.5708 Radius=1.7
    g30: Circle CenterX=40.3333 CenterY=-27.1197 CenterZ=0 NormalX=0 NormalY=0 NormalZ=1 AngleXU=-1.5708 Radius=1.7
    g31: Circle CenterX=9 CenterY=27.1197 CenterZ=0 NormalX=0 NormalY=0 NormalZ=-1 AngleXU=1.5708 Radius=1.7
    g32: Circle CenterX=9 CenterY=-27.1197 CenterZ=0 NormalX=0 NormalY=0 NormalZ=1 AngleXU=-1.5708 Radius=1.7
    g33: Circle CenterX=1604 CenterY=0 CenterZ=0 NormalX=0 NormalY=0 NormalZ=-1 AngleXU=-1.5708 Radius=1.7
    g34: Circle CenterX=1672 CenterY=0 CenterZ=0 NormalX=0 NormalY=0 NormalZ=-1 AngleXU=-1.5708 Radius=1.7
    g35: Circle CenterX=1505 CenterY=-4.15 CenterZ=0 NormalX=0 NormalY=0 NormalZ=-1 AngleXU=1.5708 Radius=1.6
    g36: Circle CenterX=1505 CenterY=4.15 CenterZ=0 NormalX=0 NormalY=0 NormalZ=-1 AngleXU=-1.5708 Radius=1.6
FEATURE [Sketcher::SketchObject] Unfold_Sketch_bends034
  FullyConstrained = false
  sketch-geometry (2):
    g0: LineSegment StartX=1684 StartY=-16.9598 StartZ=0 EndX=0 EndY=-16.9598 EndZ=0
    g1: LineSegment StartX=1684 StartY=16.9598 StartZ=0 EndX=0 EndY=16.9598 EndZ=0
FEATURE [Sketcher::SketchObject] Unfold_Sketch034  label="pillar3_1.5mm_Unfold_Sketch034"
  ExternalGeometry = -> [Unfold_Sketch_bends034]
  FullyConstrained = false
  sketch-geometry (49):
    g0: LineSegment StartX=0 StartY=-29.6197 StartZ=0 EndX=0 EndY=29.6197 EndZ=0
    g1: ArcOfCircle CenterX=5 CenterY=-29.6197 CenterZ=0 NormalX=0 NormalY=0 NormalZ=1 AngleXU=-1.5708 Radius=5 StartAngle=4.71239 EndAngle=6.28319
    g2: LineSegment StartX=5 StartY=-34.6197 StartZ=0 EndX=1679 EndY=-34.6197 EndZ=0
    g3: ArcOfCircle CenterX=1679 CenterY=-29.6197 CenterZ=0 NormalX=0 NormalY=0 NormalZ=1 AngleXU=-1.5708 Radius=5 StartAngle=0 EndAngle=1.5708
    g4: LineSegment StartX=1684 StartY=-29.6197 StartZ=0 EndX=1684 EndY=29.6197 EndZ=0
    g5: ArcOfCircle CenterX=1679 CenterY=29.6197 CenterZ=0 NormalX=0 NormalY=0 NormalZ=1 AngleXU=1.5708 Radius=5 StartAngle=4.71239 EndAngle=6.28319
    g6: LineSegment StartX=5 StartY=34.6197 StartZ=0 EndX=1679 EndY=34.6197 EndZ=0
    g7: ArcOfCircle CenterX=5 CenterY=29.6197 CenterZ=0 NormalX=0 NormalY=0 NormalZ=1 AngleXU=1.5708 Radius=5 StartAngle=0 EndAngle=1.5708
    g8: LineSegment StartX=615.9 StartY=-5.75 StartZ=0 EndX=614.1 EndY=-5.75 EndZ=0
    g9: ArcOfCircle CenterX=614.1 CenterY=-4.15 CenterZ=0 NormalX=0 NormalY=0 NormalZ=1 AngleXU=-1.5708 Radius=1.6 StartAngle=3.14159 EndAngle=6.28319
    g10: LineSegment StartX=615.9 StartY=-2.55 StartZ=0 EndX=614.1 EndY=-2.55 EndZ=0
    g11: ArcOfCircle CenterX=615.9 CenterY=-4.15 CenterZ=0 NormalX=0 NormalY=0 NormalZ=1 AngleXU=-1.5708 Radius=1.6 StartAngle=0 EndAngle=3.14159
    g12: LineSegment StartX=615.9 StartY=2.55 StartZ=0 EndX=614.1 EndY=2.55 EndZ=0
    g13: ArcOfCircle CenterX=614.1 CenterY=4.15 CenterZ=0 NormalX=0 NormalY=0 NormalZ=1 AngleXU=1.5708 Radius=1.6 StartAngle=0 EndAngle=3.14159
    g14: LineSegment StartX=615.9 StartY=5.75 StartZ=0 EndX=614.1 EndY=5.75 EndZ=0
    g15: ArcOfCircle CenterX=615.9 CenterY=4.15 CenterZ=0 NormalX=0 NormalY=0 NormalZ=1 AngleXU=1.5708 Radius=1.6 StartAngle=3.14159 EndAngle=6.28319
    g16: Circle CenterX=761 CenterY=0 CenterZ=0 NormalX=0 NormalY=0 NormalZ=-1 AngleXU=1.5708 Radius=1.7
    g17: Circle CenterX=1032 CenterY=0 CenterZ=0 NormalX=0 NormalY=0 NormalZ=-1 AngleXU=1.5708 Radius=1.7
    g18: Circle CenterX=1672 CenterY=0 CenterZ=0 NormalX=0 NormalY=0 NormalZ=-1 AngleXU=-1.5708 Radius=1.7
    g19: Circle CenterX=1604 CenterY=0 CenterZ=0 NormalX=0 NormalY=0 NormalZ=-1 AngleXU=-1.5708 Radius=1.7
    g20: Circle CenterX=1574 CenterY=0 CenterZ=0 NormalX=0 NormalY=0 NormalZ=-1 AngleXU=1.5708 Radius=1.7
    g21: Circle CenterX=1303 CenterY=0 CenterZ=0 NormalX=0 NormalY=0 NormalZ=-1 AngleXU=1.5708 Radius=1.7
    g22: Circle CenterX=1674 CenterY=-27.6197 CenterZ=0 NormalX=0 NormalY=0 NormalZ=-1 AngleXU=1.5708 Radius=1.7
    g23: Circle CenterX=761 CenterY=25.6197 CenterZ=0 NormalX=0 NormalY=0 NormalZ=-1 AngleXU=1.5708 Radius=1.7
    g24: Circle CenterX=1604 CenterY=27.6197 CenterZ=0 NormalX=0 NormalY=0 NormalZ=-1 AngleXU=1.5708 Radius=1.7
    g25: Circle CenterX=1674 CenterY=27.6197 CenterZ=0 NormalX=0 NormalY=0 NormalZ=-1 AngleXU=1.5708 Radius=1.7
    g26: Circle CenterX=1032 CenterY=25.6197 CenterZ=0 NormalX=0 NormalY=0 NormalZ=-1 AngleXU=1.5708 Radius=1.7
    g27: Circle CenterX=1303 CenterY=25.6197 CenterZ=0 NormalX=0 NormalY=0 NormalZ=-1 AngleXU=1.5708 Radius=1.7
    g28: Circle CenterX=1574 CenterY=25.6197 CenterZ=0 NormalX=0 NormalY=0 NormalZ=-1 AngleXU=1.5708 Radius=1.7
    g29: Circle CenterX=761 CenterY=-25.6197 CenterZ=0 NormalX=0 NormalY=0 NormalZ=-1 AngleXU=1.5708 Radius=1.7
    g30: Circle CenterX=1032 CenterY=-25.6197 CenterZ=0 NormalX=0 NormalY=0 NormalZ=-1 AngleXU=1.5708 Radius=1.7
    g31: Circle CenterX=1303 CenterY=-25.6197 CenterZ=0 NormalX=0 NormalY=0 NormalZ=-1 AngleXU=1.5708 Radius=1.7
    g32: Circle CenterX=1574 CenterY=-25.6197 CenterZ=0 NormalX=0 NormalY=0 NormalZ=-1 AngleXU=1.5708 Radius=1.7
    g33: Circle CenterX=1604 CenterY=-27.6197 CenterZ=0 NormalX=0 NormalY=0 NormalZ=-1 AngleXU=1.5708 Radius=1.7
    g34: Circle CenterX=40.3333 CenterY=-27.1197 CenterZ=0 NormalX=0 NormalY=0 NormalZ=1 AngleXU=-1.5708 Radius=1.7
    g35: Circle CenterX=71.6667 CenterY=-27.1197 CenterZ=0 NormalX=0 NormalY=0 NormalZ=1 AngleXU=-1.5708 Radius=1.7
    g36: Circle CenterX=71.6667 CenterY=27.1197 CenterZ=0 NormalX=0 NormalY=0 NormalZ=-1 AngleXU=1.5708 Radius=1.7
    g37: Circle CenterX=40.3333 CenterY=27.1197 CenterZ=0 NormalX=0 NormalY=0 NormalZ=-1 AngleXU=1.5708 Radius=1.7
    g38: Circle CenterX=9 CenterY=-27.1197 CenterZ=0 NormalX=0 NormalY=0 NormalZ=1 AngleXU=-1.5708 Radius=1.7
    g39: Circle CenterX=9 CenterY=27.1197 CenterZ=0 NormalX=0 NormalY=0 NormalZ=-1 AngleXU=1.5708 Radius=1.7
    g40: Circle CenterX=490 CenterY=0 CenterZ=0 NormalX=0 NormalY=0 NormalZ=-1 AngleXU=1.5708 Radius=1.7
    g41: Circle CenterX=490 CenterY=-25.6197 CenterZ=0 NormalX=0 NormalY=0 NormalZ=-1 AngleXU=1.5708 Radius=1.7
    g42: Circle CenterX=490 CenterY=25.6197 CenterZ=0 NormalX=0 NormalY=0 NormalZ=-1 AngleXU=1.5708 Radius=1.7
    g43: Circle CenterX=1505 CenterY=4.15 CenterZ=0 NormalX=0 NormalY=0 NormalZ=-1 AngleXU=-1.5708 Radius=1.6
    g44: Circle CenterX=1505 CenterY=-4.15 CenterZ=0 NormalX=0 NormalY=0 NormalZ=-1 AngleXU=1.5708 Radius=1.6
    g45: LineSegment StartX=1684 StartY=16.9598 StartZ=0 EndX=1682 EndY=16.9598 EndZ=0
    g46: LineSegment StartX=1684 StartY=-16.9598 StartZ=0 EndX=1682 EndY=-16.9598 EndZ=0
    g47: LineSegment StartX=0 StartY=16.9598 StartZ=0 EndX=2 EndY=16.9598 EndZ=0
    g48: LineSegment StartX=0 StartY=-16.9598 StartZ=0 EndX=2 EndY=-16.9598 EndZ=0
  constraints (28):
    c: Coincident(g45,g-3)
    c: PointOnObject(g45,g-3)
    c: Coincident(g46,g-4)
    c: PointOnObject(g46,g-4)
    c: Coincident(g47,g-3)
    c: PointOnObject(g47,g-3)
    c: Coincident(g48,g-4)
    c: PointOnObject(g48,g-4)
    c: Equal(g48,g47)
    c: Equal(g47,g46)
    c: Equal(g46,g45)
    c: DistanceX(g48,g48) = 2
    c: Coincident(g0,g1)
    c: Coincident(g0,g7)
    c: Coincident(g1,g2)
    c: Coincident(g6,g7)
    c: Coincident(g8,g9)
    c: Coincident(g9,g10)
    c: Coincident(g12,g13)
    c: Coincident(g13,g14)
    c: Coincident(g8,g11)
    c: Coincident(g10,g11)
    c: Coincident(g12,g15)
    c: Coincident(g14,g15)
    c: Coincident(g2,g3)
    c: Coincident(g5,g6)
    c: Coincident(g3,g4)
    c: Coincident(g4,g5)
FEATURE [App::DocumentObjectGroup] Group023  label="pillar3_1.5mm_Group"
  Group = -> [Unfold034,Unfold_Sketch034,Unfold_Sketch_Outline013,Unfold_Sketch_Internal007,Unfold_Sketch_bends034]
FEATURE [Part::Feature] Unfold035
  shape: bbox 68.02 x 2 x 1684 mm, 47 faces (baked)
FEATURE [Sketcher::SketchObject] Unfold_Sketch_Outline014
  FullyConstrained = false
  sketch-geometry (8):
    g0: LineSegment StartX=0 StartY=-29.0124 StartZ=0 EndX=0 EndY=29.0124 EndZ=0
    g1: ArcOfCircle CenterX=5 CenterY=29.0124 CenterZ=0 NormalX=0 NormalY=0 NormalZ=1 AngleXU=1.5708 Radius=5 StartAngle=0 EndAngle=1.5708
    g2: LineSegment StartX=5 StartY=34.0124 StartZ=0 EndX=1679 EndY=34.0124 EndZ=0
    g3: ArcOfCircle CenterX=1679 CenterY=29.0124 CenterZ=0 NormalX=0 NormalY=0 NormalZ=1 AngleXU=1.5708 Radius=5 StartAngle=4.71239 EndAngle=6.28319
    g4: LineSegment StartX=1684 StartY=-29.0124 StartZ=0 EndX=1684 EndY=29.0124 EndZ=0
    g5: ArcOfCircle CenterX=1679 CenterY=-29.0124 CenterZ=0 NormalX=0 NormalY=0 NormalZ=1 AngleXU=-1.5708 Radius=5 StartAngle=0 EndAngle=1.5708
    g6: LineSegment StartX=5 StartY=-34.0124 StartZ=0 EndX=1679 EndY=-34.0124 EndZ=0
    g7: ArcOfCircle CenterX=5 CenterY=-29.0124 CenterZ=0 NormalX=0 NormalY=0 NormalZ=1 AngleXU=-1.5708 Radius=5 StartAngle=4.71239 EndAngle=6.28319
FEATURE [Sketcher::SketchObject] Unfold_Sketch_Internal008
  FullyConstrained = false
  sketch-geometry (37):
    g0: LineSegment StartX=615.9 StartY=-5.75 StartZ=0 EndX=614.1 EndY=-5.75 EndZ=0
    g1: ArcOfCircle CenterX=614.1 CenterY=-4.15 CenterZ=0 NormalX=0 NormalY=0 NormalZ=1 AngleXU=-1.5708 Radius=1.6 StartAngle=3.14159 EndAngle=6.28319
    g2: LineSegment StartX=615.9 StartY=-2.55 StartZ=0 EndX=614.1 EndY=-2.55 EndZ=0
    g3: ArcOfCircle CenterX=615.9 CenterY=-4.15 CenterZ=0 NormalX=0 NormalY=0 NormalZ=1 AngleXU=-1.5708 Radius=1.6 StartAngle=0 EndAngle=3.14159
    g4: LineSegment StartX=615.9 StartY=2.55 StartZ=0 EndX=614.1 EndY=2.55 EndZ=0
    g5: ArcOfCircle CenterX=614.1 CenterY=4.15 CenterZ=0 NormalX=0 NormalY=0 NormalZ=1 AngleXU=1.5708 Radius=1.6 StartAngle=0 EndAngle=3.14159
    g6: LineSegment StartX=615.9 StartY=5.75 StartZ=0 EndX=614.1 EndY=5.75 EndZ=0
    g7: ArcOfCircle CenterX=615.9 CenterY=4.15 CenterZ=0 NormalX=0 NormalY=0 NormalZ=1 AngleXU=1.5708 Radius=1.6 StartAngle=3.14159 EndAngle=6.28319
    g8: Circle CenterX=1303 CenterY=0 CenterZ=0 NormalX=0 NormalY=0 NormalZ=-1 AngleXU=1.5708 Radius=1.7
    g9: Circle CenterX=1574 CenterY=0 CenterZ=0 NormalX=0 NormalY=0 NormalZ=-1 AngleXU=1.5708 Radius=1.7
    g10: Circle CenterX=1032 CenterY=0 CenterZ=0 NormalX=0 NormalY=0 NormalZ=-1 AngleXU=1.5708 Radius=1.7
    g11: Circle CenterX=1604 CenterY=-27.0124 CenterZ=0 NormalX=0 NormalY=0 NormalZ=-1 AngleXU=1.5708 Radius=1.7
    g12: Circle CenterX=1574 CenterY=-25.0124 CenterZ=0 NormalX=0 NormalY=0 NormalZ=-1 AngleXU=1.5708 Radius=1.7
    g13: Circle CenterX=1303 CenterY=-25.0124 CenterZ=0 NormalX=0 NormalY=0 NormalZ=-1 AngleXU=1.5708 Radius=1.7
    g14: Circle CenterX=1032 CenterY=-25.0124 CenterZ=0 NormalX=0 NormalY=0 NormalZ=-1 AngleXU=1.5708 Radius=1.7
    g15: Circle CenterX=1574 CenterY=25.0124 CenterZ=0 NormalX=0 NormalY=0 NormalZ=-1 AngleXU=1.5708 Radius=1.7
    g16: Circle CenterX=1303 CenterY=25.0124 CenterZ=0 NormalX=0 NormalY=0 NormalZ=-1 AngleXU=1.5708 Radius=1.7
    g17: Circle CenterX=1032 CenterY=25.0124 CenterZ=0 NormalX=0 NormalY=0 NormalZ=-1 AngleXU=1.5708 Radius=1.7
    g18: Circle CenterX=1674 CenterY=27.0124 CenterZ=0 NormalX=0 NormalY=0 NormalZ=-1 AngleXU=1.5708 Radius=1.7
    g19: Circle CenterX=1604 CenterY=27.0124 CenterZ=0 NormalX=0 NormalY=0 NormalZ=-1 AngleXU=1.5708 Radius=1.7
    g20: Circle CenterX=1674 CenterY=-27.0124 CenterZ=0 NormalX=0 NormalY=0 NormalZ=-1 AngleXU=1.5708 Radius=1.7
    g21: Circle CenterX=490 CenterY=0 CenterZ=0 NormalX=0 NormalY=0 NormalZ=-1 AngleXU=1.5708 Radius=1.7
    g22: Circle CenterX=490 CenterY=25.0124 CenterZ=0 NormalX=0 NormalY=0 NormalZ=-1 AngleXU=1.5708 Radius=1.7
    g23: Circle CenterX=490 CenterY=-25.0124 CenterZ=0 NormalX=0 NormalY=0 NormalZ=-1 AngleXU=1.5708 Radius=1.7
    g24: Circle CenterX=761 CenterY=0 CenterZ=0 NormalX=0 NormalY=0 NormalZ=-1 AngleXU=1.5708 Radius=1.7
    g25: Circle CenterX=761 CenterY=-25.0124 CenterZ=0 NormalX=0 NormalY=0 NormalZ=-1 AngleXU=1.5708 Radius=1.7
    g26: Circle CenterX=761 CenterY=25.0124 CenterZ=0 NormalX=0 NormalY=0 NormalZ=-1 AngleXU=1.5708 Radius=1.7
    g27: Circle CenterX=40.3333 CenterY=26.5124 CenterZ=0 NormalX=0 NormalY=0 NormalZ=-1 AngleXU=1.5708 Radius=1.7
    g28: Circle CenterX=71.6667 CenterY=26.5124 CenterZ=0 NormalX=0 NormalY=0 NormalZ=-1 AngleXU=1.5708 Radius=1.7
    g29: Circle CenterX=71.6667 CenterY=-26.5124 CenterZ=0 NormalX=0 NormalY=0 NormalZ=1 AngleXU=-1.5708 Radius=1.7
    g30: Circle CenterX=40.3333 CenterY=-26.5124 CenterZ=0 NormalX=0 NormalY=0 NormalZ=1 AngleXU=-1.5708 Radius=1.7
    g31: Circle CenterX=9 CenterY=26.5124 CenterZ=0 NormalX=0 NormalY=0 NormalZ=-1 AngleXU=1.5708 Radius=1.7
    g32: Circle CenterX=9 CenterY=-26.5124 CenterZ=0 NormalX=0 NormalY=0 NormalZ=1 AngleXU=-1.5708 Radius=1.7
    g33: Circle CenterX=1604 CenterY=0 CenterZ=0 NormalX=0 NormalY=0 NormalZ=-1 AngleXU=-1.5708 Radius=1.7
    g34: Circle CenterX=1672 CenterY=0 CenterZ=0 NormalX=0 NormalY=0 NormalZ=-1 AngleXU=-1.5708 Radius=1.7
    g35: Circle CenterX=1505 CenterY=-4.15 CenterZ=0 NormalX=0 NormalY=0 NormalZ=-1 AngleXU=1.5708 Radius=1.6
    g36: Circle CenterX=1505 CenterY=4.15 CenterZ=0 NormalX=0 NormalY=0 NormalZ=-1 AngleXU=-1.5708 Radius=1.6
FEATURE [Sketcher::SketchObject] Unfold_Sketch_bends035
  FullyConstrained = false
  sketch-geometry (2):
    g0: LineSegment StartX=1684 StartY=-16.6562 StartZ=0 EndX=0 EndY=-16.6562 EndZ=0
    g1: LineSegment StartX=1684 StartY=16.6562 StartZ=0 EndX=0 EndY=16.6562 EndZ=0
FEATURE [Sketcher::SketchObject] Unfold_Sketch035
  ExternalGeometry = -> [Unfold_Sketch_bends035]
  FullyConstrained = false
  sketch-geometry (49):
    g0: LineSegment StartX=0 StartY=-29.0124 StartZ=0 EndX=0 EndY=29.0124 EndZ=0
    g1: ArcOfCircle CenterX=5 CenterY=-29.0124 CenterZ=0 NormalX=0 NormalY=0 NormalZ=1 AngleXU=-1.5708 Radius=5 StartAngle=4.71239 EndAngle=6.28319
    g2: LineSegment StartX=5 StartY=-34.0124 StartZ=0 EndX=1679 EndY=-34.0124 EndZ=0
    g3: ArcOfCircle CenterX=1679 CenterY=-29.0124 CenterZ=0 NormalX=0 NormalY=0 NormalZ=1 AngleXU=-1.5708 Radius=5 StartAngle=0 EndAngle=1.5708
    g4: LineSegment StartX=1684 StartY=-29.0124 StartZ=0 EndX=1684 EndY=29.0124 EndZ=0
    g5: ArcOfCircle CenterX=1679 CenterY=29.0124 CenterZ=0 NormalX=0 NormalY=0 NormalZ=1 AngleXU=1.5708 Radius=5 StartAngle=4.71239 EndAngle=6.28319
    g6: LineSegment StartX=5 StartY=34.0124 StartZ=0 EndX=1679 EndY=34.0124 EndZ=0
    g7: ArcOfCircle CenterX=5 CenterY=29.0124 CenterZ=0 NormalX=0 NormalY=0 NormalZ=1 AngleXU=1.5708 Radius=5 StartAngle=0 EndAngle=1.5708
    g8: LineSegment StartX=615.9 StartY=-5.75 StartZ=0 EndX=614.1 EndY=-5.75 EndZ=0
    g9: ArcOfCircle CenterX=614.1 CenterY=-4.15 CenterZ=0 NormalX=0 NormalY=0 NormalZ=1 AngleXU=-1.5708 Radius=1.6 StartAngle=3.14159 EndAngle=6.28319
    g10: LineSegment StartX=615.9 StartY=-2.55 StartZ=0 EndX=614.1 EndY=-2.55 EndZ=0
    g11: ArcOfCircle CenterX=615.9 CenterY=-4.15 CenterZ=0 NormalX=0 NormalY=0 NormalZ=1 AngleXU=-1.5708 Radius=1.6 StartAngle=0 EndAngle=3.14159
    g12: LineSegment StartX=615.9 StartY=2.55 StartZ=0 EndX=614.1 EndY=2.55 EndZ=0
    g13: ArcOfCircle CenterX=614.1 CenterY=4.15 CenterZ=0 NormalX=0 NormalY=0 NormalZ=1 AngleXU=1.5708 Radius=1.6 StartAngle=0 EndAngle=3.14159
    g14: LineSegment StartX=615.9 StartY=5.75 StartZ=0 EndX=614.1 EndY=5.75 EndZ=0
    g15: ArcOfCircle CenterX=615.9 CenterY=4.15 CenterZ=0 NormalX=0 NormalY=0 NormalZ=1 AngleXU=1.5708 Radius=1.6 StartAngle=3.14159 EndAngle=6.28319
    g16: Circle CenterX=761 CenterY=0 CenterZ=0 NormalX=0 NormalY=0 NormalZ=-1 AngleXU=1.5708 Radius=1.7
    g17: Circle CenterX=1032 CenterY=0 CenterZ=0 NormalX=0 NormalY=0 NormalZ=-1 AngleXU=1.5708 Radius=1.7
    g18: Circle CenterX=1672 CenterY=0 CenterZ=0 NormalX=0 NormalY=0 NormalZ=-1 AngleXU=-1.5708 Radius=1.7
    g19: Circle CenterX=1604 CenterY=0 CenterZ=0 NormalX=0 NormalY=0 NormalZ=-1 AngleXU=-1.5708 Radius=1.7
    g20: Circle CenterX=1574 CenterY=0 CenterZ=0 NormalX=0 NormalY=0 NormalZ=-1 AngleXU=1.5708 Radius=1.7
    g21: Circle CenterX=1303 CenterY=0 CenterZ=0 NormalX=0 NormalY=0 NormalZ=-1 AngleXU=1.5708 Radius=1.7
    g22: Circle CenterX=1674 CenterY=-27.0124 CenterZ=0 NormalX=0 NormalY=0 NormalZ=-1 AngleXU=1.5708 Radius=1.7
    g23: Circle CenterX=761 CenterY=25.0124 CenterZ=0 NormalX=0 NormalY=0 NormalZ=-1 AngleXU=1.5708 Radius=1.7
    g24: Circle CenterX=1604 CenterY=27.0124 CenterZ=0 NormalX=0 NormalY=0 NormalZ=-1 AngleXU=1.5708 Radius=1.7
    g25: Circle CenterX=1674 CenterY=27.0124 CenterZ=0 NormalX=0 NormalY=0 NormalZ=-1 AngleXU=1.5708 Radius=1.7
    g26: Circle CenterX=1032 CenterY=25.0124 CenterZ=0 NormalX=0 NormalY=0 NormalZ=-1 AngleXU=1.5708 Radius=1.7
    g27: Circle CenterX=1303 CenterY=25.0124 CenterZ=0 NormalX=0 NormalY=0 NormalZ=-1 AngleXU=1.5708 Radius=1.7
    g28: Circle CenterX=1574 CenterY=25.0124 CenterZ=0 NormalX=0 NormalY=0 NormalZ=-1 AngleXU=1.5708 Radius=1.7
    g29: Circle CenterX=761 CenterY=-25.0124 CenterZ=0 NormalX=0 NormalY=0 NormalZ=-1 AngleXU=1.5708 Radius=1.7
    g30: Circle CenterX=1032 CenterY=-25.0124 CenterZ=0 NormalX=0 NormalY=0 NormalZ=-1 AngleXU=1.5708 Radius=1.7
    g31: Circle CenterX=1303 CenterY=-25.0124 CenterZ=0 NormalX=0 NormalY=0 NormalZ=-1 AngleXU=1.5708 Radius=1.7
    g32: Circle CenterX=1574 CenterY=-25.0124 CenterZ=0 NormalX=0 NormalY=0 NormalZ=-1 AngleXU=1.5708 Radius=1.7
    g33: Circle CenterX=1604 CenterY=-27.0124 CenterZ=0 NormalX=0 NormalY=0 NormalZ=-1 AngleXU=1.5708 Radius=1.7
    g34: Circle CenterX=40.3333 CenterY=-26.5124 CenterZ=0 NormalX=0 NormalY=0 NormalZ=1 AngleXU=-1.5708 Radius=1.7
    g35: Circle CenterX=71.6667 CenterY=-26.5124 CenterZ=0 NormalX=0 NormalY=0 NormalZ=1 AngleXU=-1.5708 Radius=1.7
    g36: Circle CenterX=71.6667 CenterY=26.5124 CenterZ=0 NormalX=0 NormalY=0 NormalZ=-1 AngleXU=1.5708 Radius=1.7
    g37: Circle CenterX=40.3333 CenterY=26.5124 CenterZ=0 NormalX=0 NormalY=0 NormalZ=-1 AngleXU=1.5708 Radius=1.7
    g38: Circle CenterX=9 CenterY=-26.5124 CenterZ=0 NormalX=0 NormalY=0 NormalZ=1 AngleXU=-1.5708 Radius=1.7
    g39: Circle CenterX=9 CenterY=26.5124 CenterZ=0 NormalX=0 NormalY=0 NormalZ=-1 AngleXU=1.5708 Radius=1.7
    g40: Circle CenterX=490 CenterY=0 CenterZ=0 NormalX=0 NormalY=0 NormalZ=-1 AngleXU=1.5708 Radius=1.7
    g41: Circle CenterX=490 CenterY=-25.0124 CenterZ=0 NormalX=0 NormalY=0 NormalZ=-1 AngleXU=1.5708 Radius=1.7
    g42: Circle CenterX=490 CenterY=25.0124 CenterZ=0 NormalX=0 NormalY=0 NormalZ=-1 AngleXU=1.5708 Radius=1.7
    g43: Circle CenterX=1505 CenterY=4.15 CenterZ=0 NormalX=0 NormalY=0 NormalZ=-1 AngleXU=-1.5708 Radius=1.6
    g44: Circle CenterX=1505 CenterY=-4.15 CenterZ=0 NormalX=0 NormalY=0 NormalZ=-1 AngleXU=1.5708 Radius=1.6
    g45: LineSegment StartX=1684 StartY=16.6562 StartZ=0 EndX=1682 EndY=16.6562 EndZ=0
    g46: LineSegment StartX=1684 StartY=-16.6562 StartZ=0 EndX=1682 EndY=-16.6562 EndZ=0
    g47: LineSegment StartX=0 StartY=-16.6562 StartZ=0 EndX=2 EndY=-16.6562 EndZ=0
    g48: LineSegment StartX=0 StartY=16.6562 StartZ=0 EndX=2 EndY=16.6562 EndZ=0
  constraints (28):
    c: Coincident(g45,g-3)
    c: PointOnObject(g45,g-3)
    c: Coincident(g46,g-4)
    c: PointOnObject(g46,g-4)
    c: Coincident(g47,g-4)
    c: PointOnObject(g47,g-4)
    c: Coincident(g48,g-3)
    c: PointOnObject(g48,g-3)
    c: Equal(g48,g47)
    c: Equal(g47,g45)
    c: Equal(g45,g46)
    c: DistanceX(g48,g48) = 2
    c: Coincident(g0,g1)
    c: Coincident(g0,g7)
    c: Coincident(g1,g2)
    c: Coincident(g6,g7)
    c: Coincident(g8,g9)
    c: Coincident(g9,g10)
    c: Coincident(g12,g13)
    c: Coincident(g13,g14)
    c: Coincident(g8,g11)
    c: Coincident(g10,g11)
    c: Coincident(g12,g15)
    c: Coincident(g14,g15)
    c: Coincident(g2,g3)
    c: Coincident(g5,g6)
    c: Coincident(g3,g4)
    c: Coincident(g4,g5)
FEATURE [Sketcher::SketchObject] MirroredSketch
  FullyConstrained = false
  sketch-geometry (19):
    g0: ArcOfCircle CenterX=-45.5 CenterY=0.712389 CenterZ=0 NormalX=0 NormalY=0 NormalZ=1 AngleXU=-2e-16 Radius=5 StartAngle=2.00674 EndAngle=3.14159
    g1: LineSegment StartX=19.6724 StartY=36.5877 StartZ=0 EndX=-47.6113 EndY=5.24475 EndZ=0
    g2: ArcOfCircle CenterX=8.10401 CenterY=61.4214 CenterZ=0 NormalX=0 NormalY=0 NormalZ=1 AngleXU=-2e-16 Radius=27.396 StartAngle=5.14833 EndAngle=6.28319
    g3: LineSegment StartX=35.5 StartY=71.7124 StartZ=0 EndX=35.5 EndY=61.4214 EndZ=0
    g4: ArcOfCircle CenterX=40.5 CenterY=71.7124 CenterZ=0 NormalX=0 NormalY=0 NormalZ=1 AngleXU=-2e-16 Radius=5 StartAngle=1.5708 EndAngle=3.14159
    g5: LineSegment StartX=45.5 StartY=76.7124 StartZ=0 EndX=40.5 EndY=76.7124 EndZ=0
    g6: ArcOfCircle CenterX=45.5 CenterY=71.7124 CenterZ=0 NormalX=0 NormalY=0 NormalZ=1 AngleXU=-2e-16 Radius=5 StartAngle=2e-16 EndAngle=1.5708
    g7: LineSegment StartX=50.5 StartY=-4 StartZ=0 EndX=50.5 EndY=71.7124 EndZ=0
    g8: ArcOfCircle CenterX=29.5 CenterY=-4 CenterZ=0 NormalX=0 NormalY=0 NormalZ=1 AngleXU=0 Radius=21 StartAngle=4.71239 EndAngle=6.28319
    g9: LineSegment StartX=-29.5 StartY=-25 StartZ=0 EndX=29.5 EndY=-25 EndZ=0
    g10: ArcOfCircle CenterX=-29.5 CenterY=-4 CenterZ=0 NormalX=0 NormalY=0 NormalZ=1 AngleXU=0 Radius=21 StartAngle=3.14159 EndAngle=4.71239
    g11: LineSegment StartX=-50.5 StartY=0.712389 StartZ=0 EndX=-50.5 EndY=-4 EndZ=0
    g12: Circle CenterX=40 CenterY=-12 CenterZ=0 NormalX=0 NormalY=0 NormalZ=1 AngleXU=0 Radius=2.75
    g13: Circle CenterX=-40 CenterY=-12 CenterZ=0 NormalX=0 NormalY=0 NormalZ=1 AngleXU=0 Radius=2.75
    g14: Circle CenterX=43 CenterY=37.0457 CenterZ=0 NormalX=0 NormalY=0 NormalZ=-1 AngleXU=-3.14159 Radius=1.7
    g15: Circle CenterX=43 CenterY=68.3791 CenterZ=0 NormalX=0 NormalY=0 NormalZ=-1 AngleXU=-3.14159 Radius=1.7
    g16: Circle CenterX=43 CenterY=5.71239 CenterZ=0 NormalX=0 NormalY=0 NormalZ=-1 AngleXU=-3.14159 Radius=1.7
    g17: LineSegment StartX=50.5 StartY=-1.64381 StartZ=0 EndX=48.5 EndY=-1.64381 EndZ=0
    g18: LineSegment StartX=-50.5 StartY=-1.64381 StartZ=0 EndX=-48.5 EndY=-1.64381 EndZ=0
  constraints (1):
    c: Equal(g18,g17)
FEATURE [Part::Feature] Unfold036
  shape: bbox 28.6 x 178.6 x 1.652 mm, 23 faces (baked)
FEATURE [Sketcher::SketchObject] Unfold_Sketch036
  FullyConstrained = false
  sketch-geometry (21):
    g0: LineSegment StartX=14.3 StartY=-7 StartZ=0 EndX=14.3 EndY=-103.639 EndZ=0
    g1: ArcOfCircle CenterX=11.3 CenterY=-7 CenterZ=0 NormalX=0 NormalY=0 NormalZ=1 AngleXU=0 Radius=3 StartAngle=-7.46e-14 EndAngle=1.5708
    g2: LineSegment StartX=10 StartY=-4 StartZ=0 EndX=11.3 EndY=-4 EndZ=0
    g3: ArcOfCircle CenterX=10 CenterY=1 CenterZ=0 NormalX=0 NormalY=0 NormalZ=1 AngleXU=0 Radius=5 StartAngle=3.51408 EndAngle=4.71239
    g4: BSplineCurve PolesCount=15 KnotsCount=13 Degree=3 IsPeriodic=0
    g5: LineSegment StartX=5 StartY=1 StartZ=0 EndX=5 EndY=9 EndZ=0
    g6: ArcOfCircle CenterX=10 CenterY=9 CenterZ=0 NormalX=0 NormalY=0 NormalZ=1 AngleXU=0 Radius=5 StartAngle=1.5708 EndAngle=3.14159
    g7: LineSegment StartX=11.3 StartY=14 StartZ=0 EndX=10 EndY=14 EndZ=0
    g8: ArcOfCircle CenterX=11.3 CenterY=17 CenterZ=0 NormalX=0 NormalY=0 NormalZ=1 AngleXU=0 Radius=3 StartAngle=4.71239 EndAngle=6.28319
    g9: LineSegment StartX=14.3 StartY=65 StartZ=0 EndX=14.3 EndY=17 EndZ=0
    g10: ArcOfCircle CenterX=9.3 CenterY=65 CenterZ=0 NormalX=0 NormalY=0 NormalZ=1 AngleXU=0 Radius=5 StartAngle=0 EndAngle=1.5708
    g11: LineSegment StartX=9.3 StartY=70 StartZ=0 EndX=-9.3 EndY=70 EndZ=0
    g12: ArcOfCircle CenterX=-9.3 CenterY=65 CenterZ=0 NormalX=0 NormalY=0 NormalZ=1 AngleXU=0 Radius=5 StartAngle=1.5708 EndAngle=3.14159
    g13: LineSegment StartX=-14.3 StartY=65 StartZ=0 EndX=-14.3 EndY=-103.639 EndZ=0
    g14: ArcOfCircle CenterX=-9.3 CenterY=-103.639 CenterZ=0 NormalX=0 NormalY=0 NormalZ=1 AngleXU=0 Radius=5 StartAngle=3.14159 EndAngle=4.71239
    g15: LineSegment StartX=9.3 StartY=-108.639 StartZ=0 EndX=-9.3 EndY=-108.639 EndZ=0
    g16: ArcOfCircle CenterX=9.3 CenterY=-103.639 CenterZ=0 NormalX=0 NormalY=0 NormalZ=1 AngleXU=0 Radius=5 StartAngle=4.71239 EndAngle=6.28319
    g17: Circle CenterX=-1.73e-14 CenterY=-75.3197 CenterZ=0 NormalX=0 NormalY=0 NormalZ=-1 AngleXU=2e-16 Radius=1.7
    g18: Circle CenterX=-3e-16 CenterY=50 CenterZ=0 NormalX=0 NormalY=0 NormalZ=-1 AngleXU=5.96046e-08 Radius=1.7
    g19: Circle CenterX=-2.2e-15 CenterY=-7.31969 CenterZ=0 NormalX=0 NormalY=0 NormalZ=-1 AngleXU=2e-16 Radius=1.7
    g20: Circle CenterX=-3e-16 CenterY=20 CenterZ=0 NormalX=0 NormalY=0 NormalZ=-1 AngleXU=5.96046e-08 Radius=1.7
FEATURE [Sketcher::SketchObject] Unfold_Sketch_Outline015
  FullyConstrained = false
  sketch-geometry (17):
    g0: LineSegment StartX=14.3 StartY=-7 StartZ=0 EndX=14.3 EndY=-103.639 EndZ=0
    g1: ArcOfCircle CenterX=9.3 CenterY=-103.639 CenterZ=0 NormalX=0 NormalY=0 NormalZ=1 AngleXU=0 Radius=5 StartAngle=4.71239 EndAngle=6.28319
    g2: LineSegment StartX=9.3 StartY=-108.639 StartZ=0 EndX=-9.3 EndY=-108.639 EndZ=0
    g3: ArcOfCircle CenterX=-9.3 CenterY=-103.639 CenterZ=0 NormalX=0 NormalY=0 NormalZ=1 AngleXU=0 Radius=5 StartAngle=3.14159 EndAngle=4.71239
    g4: LineSegment StartX=-14.3 StartY=65 StartZ=0 EndX=-14.3 EndY=-103.639 EndZ=0
    g5: ArcOfCircle CenterX=-9.3 CenterY=65 CenterZ=0 NormalX=0 NormalY=0 NormalZ=1 AngleXU=0 Radius=5 StartAngle=1.5708 EndAngle=3.14159
    g6: LineSegment StartX=9.3 StartY=70 StartZ=0 EndX=-9.3 EndY=70 EndZ=0
    g7: ArcOfCircle CenterX=9.3 CenterY=65 CenterZ=0 NormalX=0 NormalY=0 NormalZ=1 AngleXU=0 Radius=5 StartAngle=0 EndAngle=1.5708
    g8: LineSegment StartX=14.3 StartY=65 StartZ=0 EndX=14.3 EndY=17 EndZ=0
    g9: ArcOfCircle CenterX=11.3 CenterY=17 CenterZ=0 NormalX=0 NormalY=0 NormalZ=1 AngleXU=0 Radius=3 StartAngle=4.71239 EndAngle=6.28319
    g10: LineSegment StartX=11.3 StartY=14 StartZ=0 EndX=10 EndY=14 EndZ=0
    g11: ArcOfCircle CenterX=10 CenterY=9 CenterZ=0 NormalX=0 NormalY=0 NormalZ=1 AngleXU=0 Radius=5 StartAngle=1.5708 EndAngle=3.14159
    g12: LineSegment StartX=5 StartY=1 StartZ=0 EndX=5 EndY=9 EndZ=0
    g13: BSplineCurve PolesCount=15 KnotsCount=13 Degree=3 IsPeriodic=0
    g14: ArcOfCircle CenterX=10 CenterY=1 CenterZ=0 NormalX=0 NormalY=0 NormalZ=1 AngleXU=0 Radius=5 StartAngle=3.51408 EndAngle=4.71239
    g15: LineSegment StartX=10 StartY=-4 StartZ=0 EndX=11.3 EndY=-4 EndZ=0
    g16: ArcOfCircle CenterX=11.3 CenterY=-7 CenterZ=0 NormalX=0 NormalY=0 NormalZ=1 AngleXU=0 Radius=3 StartAngle=-7.46e-14 EndAngle=1.5708
FEATURE [Sketcher::SketchObject] Unfold_Sketch_Internal009
  FullyConstrained = false
  sketch-geometry (4):
    g0: Circle CenterX=-3e-16 CenterY=50 CenterZ=0 NormalX=0 NormalY=0 NormalZ=-1 AngleXU=5.96046e-08 Radius=1.7
    g1: Circle CenterX=-3e-16 CenterY=20 CenterZ=0 NormalX=0 NormalY=0 NormalZ=-1 AngleXU=5.96046e-08 Radius=1.7
    g2: Circle CenterX=-1.73e-14 CenterY=-75.3197 CenterZ=0 NormalX=0 NormalY=0 NormalZ=-1 AngleXU=2e-16 Radius=1.7
    g3: Circle CenterX=-2.2e-15 CenterY=-7.31969 CenterZ=0 NormalX=0 NormalY=0 NormalZ=-1 AngleXU=2e-16 Radius=1.7
FEATURE [Sketcher::SketchObject] Unfold_Sketch_bends036
  FullyConstrained = false
  sketch-geometry (2):
    g0: LineSegment StartX=-14.3 StartY=-79.9795 StartZ=0 EndX=14.3 EndY=-79.9795 EndZ=0
    g1: LineSegment StartX=-14.3 StartY=1.34016 StartZ=0 EndX=5 EndY=1.34016 EndZ=0
FEATURE [Part::Feature] Unfold037
  shape: bbox 56.63 x 0.5 x 1214 mm, 34 faces (baked)
FEATURE [Sketcher::SketchObject] Unfold_Sketch037
  FullyConstrained = false
  sketch-geometry (32):
    g0: LineSegment StartX=0 StartY=-33.3343 StartZ=0 EndX=0 EndY=13.3 EndZ=0
    g1: ArcOfCircle CenterX=5 CenterY=-33.3343 CenterZ=0 NormalX=0 NormalY=0 NormalZ=1 AngleXU=-1.5708 Radius=5 StartAngle=4.71239 EndAngle=6.28319
    g2: LineSegment StartX=5 StartY=-38.3343 StartZ=0 EndX=1209 EndY=-38.3343 EndZ=0
    g3: ArcOfCircle CenterX=1209 CenterY=-33.3343 CenterZ=0 NormalX=0 NormalY=0 NormalZ=1 AngleXU=-1.5708 Radius=5 StartAngle=0 EndAngle=1.5708
    g4: LineSegment StartX=1214 StartY=-33.3343 StartZ=0 EndX=1214 EndY=13.3 EndZ=0
    g5: ArcOfCircle CenterX=1209 CenterY=13.3 CenterZ=0 NormalX=0 NormalY=0 NormalZ=1 AngleXU=1.5708 Radius=5 StartAngle=4.71239 EndAngle=6.28319
    g6: LineSegment StartX=5 StartY=18.3 StartZ=0 EndX=1209 EndY=18.3 EndZ=0
    g7: ArcOfCircle CenterX=5 CenterY=13.3 CenterZ=0 NormalX=0 NormalY=0 NormalZ=1 AngleXU=1.5708 Radius=5 StartAngle=0 EndAngle=1.5708
    g8: LineSegment StartX=145.9 StartY=-5.75 StartZ=0 EndX=144.1 EndY=-5.75 EndZ=0
    g9: ArcOfCircle CenterX=144.1 CenterY=-4.15 CenterZ=0 NormalX=0 NormalY=0 NormalZ=1 AngleXU=-1.5708 Radius=1.6 StartAngle=3.14159 EndAngle=6.28319
    g10: LineSegment StartX=145.9 StartY=-2.55 StartZ=0 EndX=144.1 EndY=-2.55 EndZ=0
    g11: ArcOfCircle CenterX=145.9 CenterY=-4.15 CenterZ=0 NormalX=0 NormalY=0 NormalZ=1 AngleXU=-1.5708 Radius=1.6 StartAngle=1.78e-14 EndAngle=3.14159
    g12: LineSegment StartX=145.9 StartY=2.55 StartZ=0 EndX=144.1 EndY=2.55 EndZ=0
    g13: ArcOfCircle CenterX=144.1 CenterY=4.15 CenterZ=0 NormalX=0 NormalY=0 NormalZ=1 AngleXU=1.5708 Radius=1.6 StartAngle=1.78e-14 EndAngle=3.14159
    g14: LineSegment StartX=145.9 StartY=5.75 StartZ=0 EndX=144.1 EndY=5.75 EndZ=0
    g15: ArcOfCircle CenterX=145.9 CenterY=4.15 CenterZ=0 NormalX=0 NormalY=0 NormalZ=1 AngleXU=1.5708 Radius=1.6 StartAngle=3.14159 EndAngle=6.28319
    g16: Circle CenterX=1204 CenterY=-31.3343 CenterZ=0 NormalX=0 NormalY=0 NormalZ=-1 AngleXU=1.5708 Radius=1.7
    g17: Circle CenterX=1134 CenterY=-31.3343 CenterZ=0 NormalX=0 NormalY=0 NormalZ=-1 AngleXU=1.5708 Radius=1.7
    g18: Circle CenterX=1202 CenterY=0 CenterZ=0 NormalX=0 NormalY=0 NormalZ=-1 AngleXU=-1.5708 Radius=1.7
    g19: Circle CenterX=1134 CenterY=0 CenterZ=0 NormalX=0 NormalY=0 NormalZ=-1 AngleXU=-1.5708 Radius=1.7
    g20: Circle CenterX=1104 CenterY=0 CenterZ=0 NormalX=0 NormalY=0 NormalZ=-1 AngleXU=1.5708 Radius=1.7
    g21: Circle CenterX=833 CenterY=0 CenterZ=0 NormalX=0 NormalY=0 NormalZ=-1 AngleXU=1.5708 Radius=1.7
    g22: Circle CenterX=562 CenterY=0 CenterZ=0 NormalX=0 NormalY=0 NormalZ=-1 AngleXU=1.5708 Radius=1.7
    g23: Circle CenterX=833 CenterY=-29.3343 CenterZ=0 NormalX=0 NormalY=0 NormalZ=-1 AngleXU=1.5708 Radius=1.7
    g24: Circle CenterX=562 CenterY=-29.3343 CenterZ=0 NormalX=0 NormalY=0 NormalZ=-1 AngleXU=1.5708 Radius=1.7
    g25: Circle CenterX=1104 CenterY=-29.3343 CenterZ=0 NormalX=0 NormalY=0 NormalZ=-1 AngleXU=1.5708 Radius=1.7
    g26: Circle CenterX=20 CenterY=0 CenterZ=0 NormalX=0 NormalY=0 NormalZ=-1 AngleXU=1.5708 Radius=1.7
    g27: Circle CenterX=20 CenterY=-29.3343 CenterZ=0 NormalX=0 NormalY=0 NormalZ=-1 AngleXU=1.5708 Radius=1.7
    g28: Circle CenterX=291 CenterY=0 CenterZ=0 NormalX=0 NormalY=0 NormalZ=-1 AngleXU=1.5708 Radius=1.7
    g29: Circle CenterX=291 CenterY=-29.3343 CenterZ=0 NormalX=0 NormalY=0 NormalZ=-1 AngleXU=1.5708 Radius=1.7
    g30: Circle CenterX=1035 CenterY=-4.15 CenterZ=0 NormalX=0 NormalY=0 NormalZ=-1 AngleXU=1.5708 Radius=1.6
    g31: Circle CenterX=1035 CenterY=4.15 CenterZ=0 NormalX=0 NormalY=0 NormalZ=-1 AngleXU=-1.5708 Radius=1.6
FEATURE [Sketcher::SketchObject] Unfold_Sketch_Outline016
  FullyConstrained = false
  sketch-geometry (8):
    g0: LineSegment StartX=0 StartY=-33.3343 StartZ=0 EndX=0 EndY=13.3 EndZ=0
    g1: ArcOfCircle CenterX=5 CenterY=13.3 CenterZ=0 NormalX=0 NormalY=0 NormalZ=1 AngleXU=1.5708 Radius=5 StartAngle=0 EndAngle=1.5708
    g2: LineSegment StartX=5 StartY=18.3 StartZ=0 EndX=1209 EndY=18.3 EndZ=0
    g3: ArcOfCircle CenterX=1209 CenterY=13.3 CenterZ=0 NormalX=0 NormalY=0 NormalZ=1 AngleXU=1.5708 Radius=5 StartAngle=4.71239 EndAngle=6.28319
    g4: LineSegment StartX=1214 StartY=-33.3343 StartZ=0 EndX=1214 EndY=13.3 EndZ=0
    g5: ArcOfCircle CenterX=1209 CenterY=-33.3343 CenterZ=0 NormalX=0 NormalY=0 NormalZ=1 AngleXU=-1.5708 Radius=5 StartAngle=0 EndAngle=1.5708
    g6: LineSegment StartX=5 StartY=-38.3343 StartZ=0 EndX=1209 EndY=-38.3343 EndZ=0
    g7: ArcOfCircle CenterX=5 CenterY=-33.3343 CenterZ=0 NormalX=0 NormalY=0 NormalZ=1 AngleXU=-1.5708 Radius=5 StartAngle=4.71239 EndAngle=6.28319
FEATURE [Sketcher::SketchObject] Unfold_Sketch_Internal010
  FullyConstrained = false
  sketch-geometry (24):
    g0: LineSegment StartX=145.9 StartY=-5.75 StartZ=0 EndX=144.1 EndY=-5.75 EndZ=0
    g1: ArcOfCircle CenterX=144.1 CenterY=-4.15 CenterZ=0 NormalX=0 NormalY=0 NormalZ=1 AngleXU=-1.5708 Radius=1.6 StartAngle=3.14159 EndAngle=6.28319
    g2: LineSegment StartX=145.9 StartY=-2.55 StartZ=0 EndX=144.1 EndY=-2.55 EndZ=0
    g3: ArcOfCircle CenterX=145.9 CenterY=-4.15 CenterZ=0 NormalX=0 NormalY=0 NormalZ=1 AngleXU=-1.5708 Radius=1.6 StartAngle=1.78e-14 EndAngle=3.14159
    g4: LineSegment StartX=145.9 StartY=2.55 StartZ=0 EndX=144.1 EndY=2.55 EndZ=0
    g5: ArcOfCircle CenterX=144.1 CenterY=4.15 CenterZ=0 NormalX=0 NormalY=0 NormalZ=1 AngleXU=1.5708 Radius=1.6 StartAngle=1.78e-14 EndAngle=3.14159
    g6: LineSegment StartX=145.9 StartY=5.75 StartZ=0 EndX=144.1 EndY=5.75 EndZ=0
    g7: ArcOfCircle CenterX=145.9 CenterY=4.15 CenterZ=0 NormalX=0 NormalY=0 NormalZ=1 AngleXU=1.5708 Radius=1.6 StartAngle=3.14159 EndAngle=6.28319
    g8: Circle CenterX=1104 CenterY=0 CenterZ=0 NormalX=0 NormalY=0 NormalZ=-1 AngleXU=1.5708 Radius=1.7
    g9: Circle CenterX=1104 CenterY=-29.3343 CenterZ=0 NormalX=0 NormalY=0 NormalZ=-1 AngleXU=1.5708 Radius=1.7
    g10: Circle CenterX=1134 CenterY=-31.3343 CenterZ=0 NormalX=0 NormalY=0 NormalZ=-1 AngleXU=1.5708 Radius=1.7
    g11: Circle CenterX=1204 CenterY=-31.3343 CenterZ=0 NormalX=0 NormalY=0 NormalZ=-1 AngleXU=1.5708 Radius=1.7
    g12: Circle CenterX=291 CenterY=0 CenterZ=0 NormalX=0 NormalY=0 NormalZ=-1 AngleXU=1.5708 Radius=1.7
    g13: Circle CenterX=291 CenterY=-29.3343 CenterZ=0 NormalX=0 NormalY=0 NormalZ=-1 AngleXU=1.5708 Radius=1.7
    g14: Circle CenterX=20 CenterY=0 CenterZ=0 NormalX=0 NormalY=0 NormalZ=-1 AngleXU=1.5708 Radius=1.7
    g15: Circle CenterX=20 CenterY=-29.3343 CenterZ=0 NormalX=0 NormalY=0 NormalZ=-1 AngleXU=1.5708 Radius=1.7
    g16: Circle CenterX=562 CenterY=0 CenterZ=0 NormalX=0 NormalY=0 NormalZ=-1 AngleXU=1.5708 Radius=1.7
    g17: Circle CenterX=833 CenterY=0 CenterZ=0 NormalX=0 NormalY=0 NormalZ=-1 AngleXU=1.5708 Radius=1.7
    g18: Circle CenterX=562 CenterY=-29.3343 CenterZ=0 NormalX=0 NormalY=0 NormalZ=-1 AngleXU=1.5708 Radius=1.7
    g19: Circle CenterX=833 CenterY=-29.3343 CenterZ=0 NormalX=0 NormalY=0 NormalZ=-1 AngleXU=1.5708 Radius=1.7
    g20: Circle CenterX=1134 CenterY=0 CenterZ=0 NormalX=0 NormalY=0 NormalZ=-1 AngleXU=-1.5708 Radius=1.7
    g21: Circle CenterX=1202 CenterY=0 CenterZ=0 NormalX=0 NormalY=0 NormalZ=-1 AngleXU=-1.5708 Radius=1.7
    g22: Circle CenterX=1035 CenterY=4.15 CenterZ=0 NormalX=0 NormalY=0 NormalZ=-1 AngleXU=-1.5708 Radius=1.6
    g23: Circle CenterX=1035 CenterY=-4.15 CenterZ=0 NormalX=0 NormalY=0 NormalZ=-1 AngleXU=1.5708 Radius=1.6
FEATURE [Sketcher::SketchObject] Unfold_Sketch_bends037
  FullyConstrained = false
  Placement = pos=(0,-7.51224,-8.90455) rot=(-1,0,0;0.700791rad)
  sketch-geometry (1):
    g0: LineSegment StartX=1214 StartY=-13.8093 StartZ=0 EndX=0 EndY=-13.8093 EndZ=0
FEATURE [TechDraw::DrawViewBalloon] Balloon013
  BubbleShape = 3
  EndType = 0
  EndTypeScale = 1
  KinkLength = 5
  LockPosition = false
  OriginX = -290.364
  OriginY = -13.8673
  Rotation = 0
  ScaleType = 0
  ShapeScale = 1
  SourceView = -> View060
  Text = Оборотная сторона
  TextWrapLen = -1
  X = -54.4723
  Y = 96.8328
FEATURE [TechDraw::DrawViewBalloon] Balloon014
  BubbleShape = 3
  EndType = 0
  EndTypeScale = 1
  KinkLength = 5
  LockPosition = false
  OriginX = -279.854
  OriginY = 4.58537
  Rotation = 0
  ScaleType = 0
  ShapeScale = 1
  SourceView = -> View061
  Text = Оборотная сторона
  TextWrapLen = -1
  X = -67.3659
  Y = 81.8537
FEATURE [Part::Feature] Unfold038
  shape: bbox 56.63 x 0.5 x 1214 mm, 34 faces (baked)
FEATURE [Sketcher::SketchObject] Unfold_Sketch038
  FullyConstrained = false
  sketch-geometry (32):
    g0: LineSegment StartX=0 StartY=33.3343 StartZ=0 EndX=0 EndY=-13.3 EndZ=0
    g1: ArcOfCircle CenterX=5 CenterY=-13.3 CenterZ=0 NormalX=0 NormalY=0 NormalZ=1 AngleXU=1.5708 Radius=5 StartAngle=1.5708 EndAngle=3.14159
    g2: LineSegment StartX=5 StartY=-18.3 StartZ=0 EndX=1209 EndY=-18.3 EndZ=0
    g3: ArcOfCircle CenterX=1209 CenterY=-13.3 CenterZ=0 NormalX=0 NormalY=0 NormalZ=1 AngleXU=1.5708 Radius=5 StartAngle=3.14159 EndAngle=4.71239
    g4: LineSegment StartX=1214 StartY=33.3343 StartZ=0 EndX=1214 EndY=-13.3 EndZ=0
    g5: ArcOfCircle CenterX=1209 CenterY=33.3343 CenterZ=0 NormalX=0 NormalY=0 NormalZ=1 AngleXU=1.5708 Radius=5 StartAngle=4.71239 EndAngle=6.28319
    g6: LineSegment StartX=5 StartY=38.3343 StartZ=0 EndX=1209 EndY=38.3343 EndZ=0
    g7: ArcOfCircle CenterX=5 CenterY=33.3343 CenterZ=0 NormalX=0 NormalY=0 NormalZ=1 AngleXU=1.5708 Radius=5 StartAngle=0 EndAngle=1.5708
    g8: ArcOfCircle CenterX=144.1 CenterY=4.15 CenterZ=0 NormalX=0 NormalY=0 NormalZ=1 AngleXU=1.5708 Radius=1.6 StartAngle=1.78e-14 EndAngle=3.14159
    g9: LineSegment StartX=144.1 StartY=5.75 StartZ=0 EndX=145.9 EndY=5.75 EndZ=0
    g10: ArcOfCircle CenterX=145.9 CenterY=4.15 CenterZ=0 NormalX=0 NormalY=0 NormalZ=1 AngleXU=1.5708 Radius=1.6 StartAngle=3.14159 EndAngle=6.28319
    g11: LineSegment StartX=144.1 StartY=2.55 StartZ=0 EndX=145.9 EndY=2.55 EndZ=0
    g12: ArcOfCircle CenterX=144.1 CenterY=-4.15 CenterZ=0 NormalX=0 NormalY=0 NormalZ=1 AngleXU=-1.5708 Radius=1.6 StartAngle=3.14159 EndAngle=6.28319
    g13: LineSegment StartX=144.1 StartY=-2.55 StartZ=0 EndX=145.9 EndY=-2.55 EndZ=0
    g14: ArcOfCircle CenterX=145.9 CenterY=-4.15 CenterZ=0 NormalX=0 NormalY=0 NormalZ=1 AngleXU=-1.5708 Radius=1.6 StartAngle=1.78e-14 EndAngle=3.14159
    g15: LineSegment StartX=144.1 StartY=-5.75 StartZ=0 EndX=145.9 EndY=-5.75 EndZ=0
    g16: Circle CenterX=1204 CenterY=31.3343 CenterZ=0 NormalX=0 NormalY=0 NormalZ=-1 AngleXU=1.5708 Radius=1.7
    g17: Circle CenterX=1134 CenterY=31.3343 CenterZ=0 NormalX=0 NormalY=0 NormalZ=-1 AngleXU=1.5708 Radius=1.7
    g18: Circle CenterX=1202 CenterY=0 CenterZ=0 NormalX=0 NormalY=0 NormalZ=-1 AngleXU=-1.5708 Radius=1.7
    g19: Circle CenterX=1134 CenterY=0 CenterZ=0 NormalX=0 NormalY=0 NormalZ=-1 AngleXU=-1.5708 Radius=1.7
    g20: Circle CenterX=1104 CenterY=0 CenterZ=0 NormalX=0 NormalY=0 NormalZ=-1 AngleXU=1.5708 Radius=1.7
    g21: Circle CenterX=833 CenterY=0 CenterZ=0 NormalX=0 NormalY=0 NormalZ=-1 AngleXU=1.5708 Radius=1.7
    g22: Circle CenterX=562 CenterY=0 CenterZ=0 NormalX=0 NormalY=0 NormalZ=-1 AngleXU=1.5708 Radius=1.7
    g23: Circle CenterX=833 CenterY=29.3343 CenterZ=0 NormalX=0 NormalY=0 NormalZ=-1 AngleXU=1.5708 Radius=1.7
    g24: Circle CenterX=562 CenterY=29.3343 CenterZ=0 NormalX=0 NormalY=0 NormalZ=-1 AngleXU=1.5708 Radius=1.7
    g25: Circle CenterX=1104 CenterY=29.3343 CenterZ=0 NormalX=0 NormalY=0 NormalZ=-1 AngleXU=1.5708 Radius=1.7
    g26: Circle CenterX=20 CenterY=0 CenterZ=0 NormalX=0 NormalY=0 NormalZ=-1 AngleXU=1.5708 Radius=1.7
    g27: Circle CenterX=20 CenterY=29.3343 CenterZ=0 NormalX=0 NormalY=0 NormalZ=-1 AngleXU=1.5708 Radius=1.7
    g28: Circle CenterX=291 CenterY=0 CenterZ=0 NormalX=0 NormalY=0 NormalZ=-1 AngleXU=1.5708 Radius=1.7
    g29: Circle CenterX=291 CenterY=29.3343 CenterZ=0 NormalX=0 NormalY=0 NormalZ=-1 AngleXU=1.5708 Radius=1.7
    g30: Circle CenterX=1035 CenterY=4.15 CenterZ=0 NormalX=0 NormalY=0 NormalZ=-1 AngleXU=-1.5708 Radius=1.6
    g31: Circle CenterX=1035 CenterY=-4.15 CenterZ=0 NormalX=0 NormalY=0 NormalZ=-1 AngleXU=1.5708 Radius=1.6
FEATURE [Sketcher::SketchObject] Unfold_Sketch_Outline017
  FullyConstrained = false
  sketch-geometry (8):
    g0: LineSegment StartX=0 StartY=33.3343 StartZ=0 EndX=0 EndY=-13.3 EndZ=0
    g1: ArcOfCircle CenterX=5 CenterY=-13.3 CenterZ=0 NormalX=0 NormalY=0 NormalZ=1 AngleXU=1.5708 Radius=5 StartAngle=1.5708 EndAngle=3.14159
    g2: LineSegment StartX=5 StartY=-18.3 StartZ=0 EndX=1209 EndY=-18.3 EndZ=0
    g3: ArcOfCircle CenterX=1209 CenterY=-13.3 CenterZ=0 NormalX=0 NormalY=0 NormalZ=1 AngleXU=1.5708 Radius=5 StartAngle=3.14159 EndAngle=4.71239
    g4: LineSegment StartX=1214 StartY=33.3343 StartZ=0 EndX=1214 EndY=-13.3 EndZ=0
    g5: ArcOfCircle CenterX=1209 CenterY=33.3343 CenterZ=0 NormalX=0 NormalY=0 NormalZ=1 AngleXU=1.5708 Radius=5 StartAngle=4.71239 EndAngle=6.28319
    g6: LineSegment StartX=5 StartY=38.3343 StartZ=0 EndX=1209 EndY=38.3343 EndZ=0
    g7: ArcOfCircle CenterX=5 CenterY=33.3343 CenterZ=0 NormalX=0 NormalY=0 NormalZ=1 AngleXU=1.5708 Radius=5 StartAngle=0 EndAngle=1.5708
FEATURE [Sketcher::SketchObject] Unfold_Sketch_Internal011
  FullyConstrained = false
  sketch-geometry (24):
    g0: ArcOfCircle CenterX=144.1 CenterY=4.15 CenterZ=0 NormalX=0 NormalY=0 NormalZ=1 AngleXU=1.5708 Radius=1.6 StartAngle=1.78e-14 EndAngle=3.14159
    g1: LineSegment StartX=144.1 StartY=2.55 StartZ=0 EndX=145.9 EndY=2.55 EndZ=0
    g2: ArcOfCircle CenterX=145.9 CenterY=4.15 CenterZ=0 NormalX=0 NormalY=0 NormalZ=1 AngleXU=1.5708 Radius=1.6 StartAngle=3.14159 EndAngle=6.28319
    g3: LineSegment StartX=144.1 StartY=5.75 StartZ=0 EndX=145.9 EndY=5.75 EndZ=0
    g4: ArcOfCircle CenterX=144.1 CenterY=-4.15 CenterZ=0 NormalX=0 NormalY=0 NormalZ=1 AngleXU=-1.5708 Radius=1.6 StartAngle=3.14159 EndAngle=6.28319
    g5: LineSegment StartX=144.1 StartY=-5.75 StartZ=0 EndX=145.9 EndY=-5.75 EndZ=0
    g6: ArcOfCircle CenterX=145.9 CenterY=-4.15 CenterZ=0 NormalX=0 NormalY=0 NormalZ=1 AngleXU=-1.5708 Radius=1.6 StartAngle=1.78e-14 EndAngle=3.14159
    g7: LineSegment StartX=144.1 StartY=-2.55 StartZ=0 EndX=145.9 EndY=-2.55 EndZ=0
    g8: Circle CenterX=1104 CenterY=0 CenterZ=0 NormalX=0 NormalY=0 NormalZ=-1 AngleXU=1.5708 Radius=1.7
    g9: Circle CenterX=1104 CenterY=29.3343 CenterZ=0 NormalX=0 NormalY=0 NormalZ=-1 AngleXU=1.5708 Radius=1.7
    g10: Circle CenterX=1134 CenterY=31.3343 CenterZ=0 NormalX=0 NormalY=0 NormalZ=-1 AngleXU=1.5708 Radius=1.7
    g11: Circle CenterX=1204 CenterY=31.3343 CenterZ=0 NormalX=0 NormalY=0 NormalZ=-1 AngleXU=1.5708 Radius=1.7
    g12: Circle CenterX=291 CenterY=0 CenterZ=0 NormalX=0 NormalY=0 NormalZ=-1 AngleXU=1.5708 Radius=1.7
    g13: Circle CenterX=291 CenterY=29.3343 CenterZ=0 NormalX=0 NormalY=0 NormalZ=-1 AngleXU=1.5708 Radius=1.7
    g14: Circle CenterX=20 CenterY=0 CenterZ=0 NormalX=0 NormalY=0 NormalZ=-1 AngleXU=1.5708 Radius=1.7
    g15: Circle CenterX=20 CenterY=29.3343 CenterZ=0 NormalX=0 NormalY=0 NormalZ=-1 AngleXU=1.5708 Radius=1.7
    g16: Circle CenterX=562 CenterY=0 CenterZ=0 NormalX=0 NormalY=0 NormalZ=-1 AngleXU=1.5708 Radius=1.7
    g17: Circle CenterX=833 CenterY=0 CenterZ=0 NormalX=0 NormalY=0 NormalZ=-1 AngleXU=1.5708 Radius=1.7
    g18: Circle CenterX=562 CenterY=29.3343 CenterZ=0 NormalX=0 NormalY=0 NormalZ=-1 AngleXU=1.5708 Radius=1.7
    g19: Circle CenterX=833 CenterY=29.3343 CenterZ=0 NormalX=0 NormalY=0 NormalZ=-1 AngleXU=1.5708 Radius=1.7
    g20: Circle CenterX=1134 CenterY=0 CenterZ=0 NormalX=0 NormalY=0 NormalZ=-1 AngleXU=-1.5708 Radius=1.7
    g21: Circle CenterX=1202 CenterY=0 CenterZ=0 NormalX=0 NormalY=0 NormalZ=-1 AngleXU=-1.5708 Radius=1.7
    g22: Circle CenterX=1035 CenterY=-4.15 CenterZ=0 NormalX=0 NormalY=0 NormalZ=-1 AngleXU=1.5708 Radius=1.6
    g23: Circle CenterX=1035 CenterY=4.15 CenterZ=0 NormalX=0 NormalY=0 NormalZ=-1 AngleXU=-1.5708 Radius=1.6
FEATURE [Sketcher::SketchObject] Unfold_Sketch_bends038
  FullyConstrained = false
  Placement = pos=(0,2.54422,6.2844) rot=(-1,0,0;0.384677rad)
  sketch-geometry (1):
    g0: LineSegment StartX=1214 StartY=16.7468 StartZ=0 EndX=0 EndY=16.7468 EndZ=0
FEATURE [Part::Feature] Unfold039
  shape: bbox 48.55 x 29.2 x 50.71 mm, 24 faces (baked)
FEATURE [Sketcher::SketchObject] Unfold_Sketch_bends039
  FullyConstrained = false
  sketch-geometry (2):
    g0: LineSegment StartX=-1.1547 StartY=-32.3562 StartZ=0 EndX=-27 EndY=-32.3562 EndZ=0
    g1: LineSegment StartX=0.416096 StartY=-30 StartZ=0 EndX=0.416096 EndY=0 EndZ=0
FEATURE [Sketcher::SketchObject] Unfold_Sketch039
  ExternalGeometry = -> [Unfold_Sketch_bends039]
  FullyConstrained = false
  sketch-geometry (26):
    g0: LineSegment StartX=27.8322 StartY=-21.3669 StartZ=0 EndX=27.8322 EndY=-28 EndZ=0
    g1: ArcOfEllipse CenterX=24.835 CenterY=-21.4304 CenterZ=0 NormalX=0 NormalY=0 NormalZ=1 MajorRadius=3.03559 MinorRadius=3.03253 AngleXU=1.59173 StartAngle=4.71238 EndAngle=5.56044
    g2: LineSegment StartX=26.8007 StartY=-19.1031 StartZ=0 EndX=5.6788 EndY=-0.736183 EndZ=0
    g3: ArcOfEllipse CenterX=3.719 CenterY=-3.0565 CenterZ=0 NormalX=0 NormalY=0 NormalZ=1 MajorRadius=3.0252 MinorRadius=3.02213 AngleXU=1.57368 StartAngle=5.57849 EndAngle=6.28319
    g4: LineSegment StartX=-2.87807 StartY=0 StartZ=0 EndX=3.71027 EndY=0 EndZ=0
    g5: ArcOfEllipse CenterX=-2.88681 CenterY=-3.0565 CenterZ=0 NormalX=0 NormalY=0 NormalZ=1 MajorRadius=3.0252 MinorRadius=3.02213 AngleXU=1.5679 StartAngle=7.72063e-06 EndAngle=0.704699
    g6: LineSegment StartX=-25.9685 StartY=-19.1031 StartZ=0 EndX=-4.84661 EndY=-0.736183 EndZ=0
    g7: ArcOfEllipse CenterX=-24.0029 CenterY=-21.4304 CenterZ=0 NormalX=0 NormalY=0 NormalZ=1 MajorRadius=3.03559 MinorRadius=3.03253 AngleXU=1.54985 StartAngle=0.722749 EndAngle=1.57081
    g8: LineSegment StartX=-27 StartY=-21.3669 StartZ=0 EndX=-27 EndY=-48.7124 EndZ=0
    g9: ArcOfCircle CenterX=-25 CenterY=-48.7124 CenterZ=0 NormalX=0 NormalY=0 NormalZ=1 AngleXU=0.523599 Radius=2 StartAngle=2.61799 EndAngle=4.18879
    g10: LineSegment StartX=-25 StartY=-50.7124 StartZ=0 EndX=-3.1547 EndY=-50.7124 EndZ=0
    g11: ArcOfCircle CenterX=-3.1547 CenterY=-48.7124 CenterZ=0 NormalX=0 NormalY=0 NormalZ=1 AngleXU=0.523599 Radius=2 StartAngle=4.18879 EndAngle=5.75959
    g12: LineSegment StartX=-1.1547 StartY=-48.7124 StartZ=0 EndX=-1.1547 EndY=-30 EndZ=0
    g13: LineSegment StartX=-1.1547 StartY=-30 StartZ=0 EndX=25.8322 EndY=-30 EndZ=0
    g14: Circle CenterX=-20.5 CenterY=-38.2124 CenterZ=0 NormalX=0 NormalY=0 NormalZ=-1 AngleXU=-3.14159 Radius=2.05
    g15: Ellipse CenterX=-22 CenterY=-24 CenterZ=0 NormalX=0 NormalY=0 NormalZ=1 MajorRadius=1.7 MinorRadius=1.7 AngleXU=-1.5708
    g16: Circle CenterX=22.8322 CenterY=-24 CenterZ=0 NormalX=0 NormalY=0 NormalZ=1 AngleXU=-1.5708 Radius=1.7
    g17: Ellipse CenterX=-10 CenterY=-24 CenterZ=0 NormalX=0 NormalY=0 NormalZ=1 MajorRadius=1.7 MinorRadius=1.7 AngleXU=-1.5708
    g18: Ellipse CenterX=-10 CenterY=-12 CenterZ=0 NormalX=0 NormalY=0 NormalZ=1 MajorRadius=1.7 MinorRadius=1.7 AngleXU=-1.5708
    g19: Circle CenterX=10.8322 CenterY=-24 CenterZ=0 NormalX=0 NormalY=0 NormalZ=1 AngleXU=-1.5708 Radius=1.7
    g20: Circle CenterX=10.8322 CenterY=-12 CenterZ=0 NormalX=0 NormalY=0 NormalZ=1 AngleXU=-1.5708 Radius=1.7
    g21: ArcOfCircle CenterX=25.8322 CenterY=-28 CenterZ=0 NormalX=0 NormalY=0 NormalZ=1 AngleXU=0 Radius=2 StartAngle=4.71239 EndAngle=6.28319
    g22: LineSegment StartX=-1.1547 StartY=-32.3562 StartZ=0 EndX=-3.1547 EndY=-32.3562 EndZ=0
    g23: LineSegment StartX=-27 StartY=-32.3562 StartZ=0 EndX=-25 EndY=-32.3562 EndZ=0
    g24: LineSegment StartX=0.416096 StartY=-30 StartZ=0 EndX=0.416096 EndY=-28 EndZ=0
    g25: LineSegment StartX=0.416096 StartY=0 StartZ=0 EndX=0.416096 EndY=-2 EndZ=0
  constraints (16):
    c: Block(g13)
    c: Block(g0)
    c: Coincident(g21,g13)
    c: Tangent(g21,g0) = 1.5708
    c: Coincident(g22,g-4)
    c: PointOnObject(g22,g-4)
    c: Coincident(g23,g-4)
    c: PointOnObject(g23,g-4)
    c: Coincident(g24,g-3)
    c: PointOnObject(g24,g-3)
    c: Coincident(g25,g-3)
    c: PointOnObject(g25,g-3)
    c: Equal(g25,g24)
    c: Equal(g24,g22)
    c: Equal(g22,g23)
    c: DistanceX(g23,g23) = 2
FEATURE [Part::Feature] Unfold040
  shape: bbox 561 x 492.4 x 2 mm, 70 faces (baked)
FEATURE [Sketcher::SketchObject] Unfold_Sketch_Outline018
  FullyConstrained = false
  Placement = pos=(0,0,0) rot=(0,0,1;3.14159rad)
  sketch-geometry (45):
    g0: LineSegment StartX=64.898 StartY=-112.2 StartZ=0 EndX=48.8226 EndY=-84.3564 EndZ=0
    g1: LineSegment StartX=48.8226 StartY=-84.3564 StartZ=0 EndX=48.0916 EndY=-79.7011 EndZ=0
    g2: LineSegment StartX=48.0916 StartY=-79.7011 StartZ=0 EndX=46.188 EndY=-80 EndZ=0
    g3: LineSegment StartX=46.188 StartY=-80 StartZ=0 EndX=44.9774 EndY=-81.4991 EndZ=0
    g4: LineSegment StartX=48.6435 StartY=-84.4599 StartZ=0 EndX=44.9774 EndY=-81.4991 EndZ=0
    g5: LineSegment StartX=48.6435 StartY=-84.4599 StartZ=0 EndX=64.7189 EndY=-112.303 EndZ=0
    g6: LineSegment StartX=64.7189 StartY=-112.303 StartZ=0 EndX=-71.1092 EndY=-280.492 EndZ=0
    g7: LineSegment StartX=-98.1147 StartY=-258.682 StartZ=0 EndX=-71.1092 EndY=-280.492 EndZ=0
    g8: LineSegment StartX=-98.1147 StartY=-258.682 StartZ=0 EndX=-103.007 EndY=-264.741 EndZ=0
    g9: ArcOfCircle CenterX=-106.897 CenterY=-261.599 CenterZ=0 NormalX=0 NormalY=0 NormalZ=1 AngleXU=-0.523599 Radius=5 StartAngle=4.71239 EndAngle=6.12743
    g10: LineSegment StartX=-109.397 StartY=-265.929 StartZ=0 EndX=-175.603 EndY=-227.705 EndZ=0
    g11: ArcOfCircle CenterX=-173.103 CenterY=-223.375 CenterZ=0 NormalX=0 NormalY=0 NormalZ=1 AngleXU=2.61799 Radius=5 StartAngle=0.155755 EndAngle=1.5708
    g12: LineSegment StartX=-177.768 StartY=-221.577 StartZ=0 EndX=-174.968 EndY=-214.311 EndZ=0
    g13: LineSegment StartX=-174.968 StartY=-214.311 StartZ=0 EndX=-207.358 EndY=-201.828 EndZ=0
    g14: LineSegment StartX=-207.358 StartY=-201.828 StartZ=0 EndX=-129.617 EndY=-0.103426 EndZ=0
    g15: LineSegment StartX=-129.617 StartY=-0.103426 StartZ=0 EndX=-97.4661 EndY=-0.103426 EndZ=0
    g16: LineSegment StartX=-97.4661 StartY=-0.103426 StartZ=0 EndX=-93.069 EndY=-1.79802 EndZ=0
    g17: LineSegment StartX=-93.069 StartY=-1.79802 StartZ=0 EndX=-92.376 EndY=7.26515e-10 EndZ=0
    g18: LineSegment StartX=-92.376 StartY=-5.08075e-10 StartZ=0 EndX=-93.069 EndY=1.79802 EndZ=0
    g19: LineSegment StartX=-97.4661 StartY=0.103426 StartZ=0 EndX=-93.069 EndY=1.79802 EndZ=0
    g20: LineSegment StartX=-97.4661 StartY=0.103426 StartZ=0 EndX=-129.617 EndY=0.103426 EndZ=0
    g21: LineSegment StartX=-129.617 StartY=0.103426 StartZ=0 EndX=-207.358 EndY=201.828 EndZ=0
    g22: LineSegment StartX=-174.968 StartY=214.311 StartZ=0 EndX=-207.358 EndY=201.828 EndZ=0
    g23: LineSegment StartX=-174.968 StartY=214.311 StartZ=0 EndX=-177.768 EndY=221.577 EndZ=0
    g24: ArcOfCircle CenterX=-173.103 CenterY=223.375 CenterZ=0 NormalX=0 NormalY=0 NormalZ=1 AngleXU=-2.61799 Radius=5 StartAngle=4.71239 EndAngle=6.12743
    g25: LineSegment StartX=-175.603 StartY=227.705 StartZ=0 EndX=-109.397 EndY=265.929 EndZ=0
    g26: ArcOfCircle CenterX=-106.897 CenterY=261.599 CenterZ=0 NormalX=0 NormalY=0 NormalZ=1 AngleXU=0.523599 Radius=5 StartAngle=0.155755 EndAngle=1.5708
    g27: LineSegment StartX=-103.007 StartY=264.741 StartZ=0 EndX=-98.1147 EndY=258.682 EndZ=0
    g28: LineSegment StartX=-98.1147 StartY=258.682 StartZ=0 EndX=-71.1092 EndY=280.492 EndZ=0
    g29: LineSegment StartX=-71.1092 StartY=280.492 StartZ=0 EndX=64.7189 EndY=112.303 EndZ=0
    g30: LineSegment StartX=64.7189 StartY=112.303 StartZ=0 EndX=48.6435 EndY=84.4599 EndZ=0
    g31: LineSegment StartX=48.6435 StartY=84.4599 StartZ=0 EndX=44.9774 EndY=81.4991 EndZ=0
    g32: LineSegment StartX=44.9774 StartY=81.4991 StartZ=0 EndX=46.188 EndY=80 EndZ=0
    g33: LineSegment StartX=46.188 StartY=80 StartZ=0 EndX=48.0916 EndY=79.7011 EndZ=0
    g34: LineSegment StartX=48.8226 StartY=84.3564 StartZ=0 EndX=48.0916 EndY=79.7011 EndZ=0
    g35: LineSegment StartX=48.8226 StartY=84.3564 StartZ=0 EndX=64.898 EndY=112.2 EndZ=0
    g36: LineSegment StartX=64.898 StartY=112.2 StartZ=0 EndX=278.468 EndY=78.6635 EndZ=0
    g37: LineSegment StartX=273.083 StartY=44.3713 StartZ=0 EndX=278.468 EndY=78.6635 EndZ=0
    g38: LineSegment StartX=273.083 StartY=44.3713 StartZ=0 EndX=280.776 EndY=43.1633 EndZ=0
    g39: ArcOfCircle CenterX=280 CenterY=38.2239 CenterZ=0 NormalX=0 NormalY=0 NormalZ=1 AngleXU=1.5708 Radius=5 StartAngle=4.71239 EndAngle=6.12743
    g40: LineSegment StartX=285 StartY=38.2239 StartZ=0 EndX=285 EndY=-38.2239 EndZ=0
    g41: ArcOfCircle CenterX=280 CenterY=-38.2239 CenterZ=0 NormalX=0 NormalY=0 NormalZ=1 AngleXU=-1.5708 Radius=5 StartAngle=0.155755 EndAngle=1.5708
    g42: LineSegment StartX=280.776 StartY=-43.1633 StartZ=0 EndX=273.083 EndY=-44.3713 EndZ=0
    g43: LineSegment StartX=273.083 StartY=-44.3713 StartZ=0 EndX=278.468 EndY=-78.6635 EndZ=0
    g44: LineSegment StartX=278.468 StartY=-78.6635 StartZ=0 EndX=64.898 EndY=-112.2 EndZ=0
FEATURE [Sketcher::SketchObject] Unfold_Sketch_Internal
  FullyConstrained = false
  Placement = pos=(0,0,0) rot=(0,0,1;3.14159rad)
  sketch-geometry (23):
    g0: Circle CenterX=34.575 CenterY=34.575 CenterZ=0 NormalX=0 NormalY=0 NormalZ=-1 AngleXU=1.5708 Radius=5.4
    g1: Circle CenterX=34.575 CenterY=-34.575 CenterZ=0 NormalX=0 NormalY=0 NormalZ=-1 AngleXU=1.5708 Radius=5.4
    g2: Circle CenterX=-34.575 CenterY=34.575 CenterZ=0 NormalX=0 NormalY=0 NormalZ=-1 AngleXU=1.5708 Radius=5.4
    g3: Circle CenterX=-34.575 CenterY=-34.575 CenterZ=0 NormalX=0 NormalY=0 NormalZ=-1 AngleXU=1.5708 Radius=5.4
    g4: Circle CenterX=145.633 CenterY=-5.68e-14 CenterZ=0 NormalX=0 NormalY=0 NormalZ=-1 AngleXU=1.5708 Radius=4.25
    g5: Circle CenterX=-163.677 CenterY=-211.497 CenterZ=0 NormalX=0 NormalY=0 NormalZ=-1 AngleXU=-1.0472 Radius=2.5
    g6: Circle CenterX=-163.677 CenterY=211.497 CenterZ=0 NormalX=0 NormalY=0 NormalZ=-1 AngleXU=1.0472 Radius=2.5
    g7: Circle CenterX=-101.323 CenterY=-247.497 CenterZ=0 NormalX=0 NormalY=0 NormalZ=-1 AngleXU=-1.0472 Radius=2.5
    g8: Circle CenterX=-21.4561 CenterY=149.509 CenterZ=0 NormalX=0 NormalY=0 NormalZ=-1 AngleXU=1.0472 Radius=2.5
    g9: Circle CenterX=-21.4561 CenterY=-149.509 CenterZ=0 NormalX=0 NormalY=0 NormalZ=-1 AngleXU=-1.0472 Radius=2.5
    g10: Circle CenterX=-101.323 CenterY=247.497 CenterZ=0 NormalX=0 NormalY=0 NormalZ=-1 AngleXU=1.0472 Radius=2.5
    g11: Circle CenterX=-87.5963 CenterY=13.7728 CenterZ=0 NormalX=0 NormalY=0 NormalZ=-1 AngleXU=1.0472 Radius=2.5
    g12: Circle CenterX=31.8705 CenterY=-82.747 CenterZ=0 NormalX=0 NormalY=0 NormalZ=-1 AngleXU=-1.0472 Radius=2.5
    g13: Circle CenterX=-87.5963 CenterY=-13.7728 CenterZ=0 NormalX=0 NormalY=0 NormalZ=-1 AngleXU=-1.0472 Radius=2.5
    g14: Circle CenterX=31.8705 CenterY=82.747 CenterZ=0 NormalX=0 NormalY=0 NormalZ=-1 AngleXU=1.0472 Radius=2.5
    g15: Circle CenterX=-118.751 CenterY=-93.336 CenterZ=0 NormalX=0 NormalY=0 NormalZ=-1 AngleXU=-1.0472 Radius=2.5
    g16: Circle CenterX=-118.751 CenterY=93.336 CenterZ=0 NormalX=0 NormalY=0 NormalZ=-1 AngleXU=1.0472 Radius=2.5
    g17: Circle CenterX=265 CenterY=36 CenterZ=0 NormalX=0 NormalY=0 NormalZ=-1 AngleXU=-3.14159 Radius=2.5
    g18: Circle CenterX=55.7258 CenterY=68.9742 CenterZ=0 NormalX=0 NormalY=0 NormalZ=-1 AngleXU=-3.14159 Radius=2.5
    g19: Circle CenterX=140.207 CenterY=56.173 CenterZ=0 NormalX=0 NormalY=0 NormalZ=-1 AngleXU=-3.14159 Radius=2.5
    g20: Circle CenterX=265 CenterY=-36 CenterZ=0 NormalX=0 NormalY=0 NormalZ=-1 AngleXU=-3.14159 Radius=2.5
    g21: Circle CenterX=140.207 CenterY=-56.173 CenterZ=0 NormalX=0 NormalY=0 NormalZ=-1 AngleXU=-3.14159 Radius=2.5
    g22: Circle CenterX=55.7258 CenterY=-68.9742 CenterZ=0 NormalX=0 NormalY=0 NormalZ=-1 AngleXU=-3.14159 Radius=2.5
FEATURE [Sketcher::SketchObject] Unfold_Sketch_bends040
  FullyConstrained = false
  Placement = pos=(0,0,0) rot=(0,0,1;3.14159rad)
  sketch-geometry (6):
    g0: LineSegment StartX=273.448 StartY=-46.699 StartZ=0 EndX=48.4571 EndY=-82.0288 EndZ=0
    g1: LineSegment StartX=46.8104 StartY=-82.9795 StartZ=0 EndX=-96.2817 EndY=-260.163 EndZ=0
    g2: LineSegment StartX=48.4571 StartY=82.0288 StartZ=0 EndX=273.448 EndY=46.699 EndZ=0
    g3: LineSegment StartX=-96.2817 StartY=260.163 StartZ=0 EndX=46.8104 EndY=82.9795 EndZ=0
    g4: LineSegment StartX=-177.167 StartY=-213.464 StartZ=0 EndX=-95.2675 EndY=-0.950723 EndZ=0
    g5: LineSegment StartX=-95.2675 StartY=0.950723 StartZ=0 EndX=-177.167 EndY=213.464 EndZ=0
FEATURE [Sketcher::SketchObject] Unfold_Sketch040
  ExternalGeometry = -> [Unfold_Sketch_bends040]
  FullyConstrained = false
  Placement = pos=(0,0,0) rot=(0,0,1;3.14159rad)
  sketch-geometry (80):
    g0: LineSegment StartX=64.898 StartY=-112.2 StartZ=0 EndX=48.8226 EndY=-84.3564 EndZ=0
    g1: LineSegment StartX=278.468 StartY=-78.6635 StartZ=0 EndX=64.898 EndY=-112.2 EndZ=0
    g2: LineSegment StartX=273.083 StartY=-44.3713 StartZ=0 EndX=278.468 EndY=-78.6635 EndZ=0
    g3: LineSegment StartX=280.776 StartY=-43.1633 StartZ=0 EndX=273.083 EndY=-44.3713 EndZ=0
    g4: ArcOfCircle CenterX=280 CenterY=-38.2239 CenterZ=0 NormalX=0 NormalY=0 NormalZ=1 AngleXU=-1.5708 Radius=5 StartAngle=0.155755 EndAngle=1.5708
    g5: LineSegment StartX=285 StartY=38.2239 StartZ=0 EndX=285 EndY=-38.2239 EndZ=0
    g6: ArcOfCircle CenterX=280 CenterY=38.2239 CenterZ=0 NormalX=0 NormalY=0 NormalZ=1 AngleXU=1.5708 Radius=5 StartAngle=4.71239 EndAngle=6.12743
    g7: LineSegment StartX=273.083 StartY=44.3713 StartZ=0 EndX=280.776 EndY=43.1633 EndZ=0
    g8: LineSegment StartX=273.083 StartY=44.3713 StartZ=0 EndX=278.468 EndY=78.6635 EndZ=0
    g9: LineSegment StartX=64.898 StartY=112.2 StartZ=0 EndX=278.468 EndY=78.6635 EndZ=0
    g10: LineSegment StartX=48.8226 StartY=84.3564 StartZ=0 EndX=64.898 EndY=112.2 EndZ=0
    g11: LineSegment StartX=48.8226 StartY=84.3564 StartZ=0 EndX=48.0916 EndY=79.7011 EndZ=0
    g12: LineSegment StartX=46.188 StartY=80 StartZ=0 EndX=48.0916 EndY=79.7011 EndZ=0
    g13: LineSegment StartX=44.9774 StartY=81.4991 StartZ=0 EndX=46.188 EndY=80 EndZ=0
    g14: LineSegment StartX=48.6435 StartY=84.4599 StartZ=0 EndX=44.9774 EndY=81.4991 EndZ=0
    g15: LineSegment StartX=64.7189 StartY=112.303 StartZ=0 EndX=48.6435 EndY=84.4599 EndZ=0
    g16: LineSegment StartX=-71.1092 StartY=280.492 StartZ=0 EndX=64.7189 EndY=112.303 EndZ=0
    g17: LineSegment StartX=-98.1147 StartY=258.682 StartZ=0 EndX=-71.1092 EndY=280.492 EndZ=0
    g18: LineSegment StartX=-103.007 StartY=264.741 StartZ=0 EndX=-98.1147 EndY=258.682 EndZ=0
    g19: ArcOfCircle CenterX=-106.897 CenterY=261.599 CenterZ=0 NormalX=0 NormalY=0 NormalZ=1 AngleXU=0.523599 Radius=5 StartAngle=0.155755 EndAngle=1.5708
    g20: LineSegment StartX=-175.603 StartY=227.705 StartZ=0 EndX=-109.397 EndY=265.929 EndZ=0
    g21: ArcOfCircle CenterX=-173.103 CenterY=223.375 CenterZ=0 NormalX=0 NormalY=0 NormalZ=1 AngleXU=-2.61799 Radius=5 StartAngle=4.71239 EndAngle=6.12743
    g22: LineSegment StartX=-174.968 StartY=214.311 StartZ=0 EndX=-177.768 EndY=221.577 EndZ=0
    g23: LineSegment StartX=-174.968 StartY=214.311 StartZ=0 EndX=-207.358 EndY=201.828 EndZ=0
    g24: LineSegment StartX=-129.617 StartY=0.103426 StartZ=0 EndX=-207.358 EndY=201.828 EndZ=0
    g25: LineSegment StartX=-97.4661 StartY=0.103426 StartZ=0 EndX=-129.617 EndY=0.103426 EndZ=0
    g26: LineSegment StartX=-97.4661 StartY=0.103426 StartZ=0 EndX=-93.069 EndY=1.79802 EndZ=0
    g27: LineSegment StartX=-92.376 StartY=-5.08098e-10 StartZ=0 EndX=-93.069 EndY=1.79802 EndZ=0
    g28: LineSegment StartX=-93.069 StartY=-1.79802 StartZ=0 EndX=-92.376 EndY=7.26493e-10 EndZ=0
    g29: LineSegment StartX=-97.4661 StartY=-0.103426 StartZ=0 EndX=-93.069 EndY=-1.79802 EndZ=0
    g30: LineSegment StartX=-129.617 StartY=-0.103426 StartZ=0 EndX=-97.4661 EndY=-0.103426 EndZ=0
    g31: LineSegment StartX=-207.358 StartY=-201.828 StartZ=0 EndX=-129.617 EndY=-0.103426 EndZ=0
    g32: LineSegment StartX=-174.968 StartY=-214.311 StartZ=0 EndX=-207.358 EndY=-201.828 EndZ=0
    g33: LineSegment StartX=-177.768 StartY=-221.577 StartZ=0 EndX=-174.968 EndY=-214.311 EndZ=0
    g34: ArcOfCircle CenterX=-173.103 CenterY=-223.375 CenterZ=0 NormalX=0 NormalY=0 NormalZ=1 AngleXU=2.61799 Radius=5 StartAngle=0.155755 EndAngle=1.5708
    g35: LineSegment StartX=-109.397 StartY=-265.929 StartZ=0 EndX=-175.603 EndY=-227.705 EndZ=0
    g36: ArcOfCircle CenterX=-106.897 CenterY=-261.599 CenterZ=0 NormalX=0 NormalY=0 NormalZ=1 AngleXU=-0.523599 Radius=5 StartAngle=4.71239 EndAngle=6.12743
    g37: LineSegment StartX=-98.1147 StartY=-258.682 StartZ=0 EndX=-103.007 EndY=-264.741 EndZ=0
    g38: LineSegment StartX=-98.1147 StartY=-258.682 StartZ=0 EndX=-71.1092 EndY=-280.492 EndZ=0
    g39: LineSegment StartX=64.7189 StartY=-112.303 StartZ=0 EndX=-71.1092 EndY=-280.492 EndZ=0
    g40: LineSegment StartX=48.6435 StartY=-84.4599 StartZ=0 EndX=64.7189 EndY=-112.303 EndZ=0
    g41: LineSegment StartX=48.6435 StartY=-84.4599 StartZ=0 EndX=44.9774 EndY=-81.4991 EndZ=0
    g42: LineSegment StartX=46.188 StartY=-80 StartZ=0 EndX=44.9774 EndY=-81.4991 EndZ=0
    g43: LineSegment StartX=48.0916 StartY=-79.7011 StartZ=0 EndX=46.188 EndY=-80 EndZ=0
    g44: LineSegment StartX=48.8226 StartY=-84.3564 StartZ=0 EndX=48.0916 EndY=-79.7011 EndZ=0
    g45: Circle CenterX=34.575 CenterY=-34.575 CenterZ=0 NormalX=0 NormalY=0 NormalZ=-1 AngleXU=1.5708 Radius=5.4
    g46: Circle CenterX=-34.575 CenterY=-34.575 CenterZ=0 NormalX=0 NormalY=0 NormalZ=-1 AngleXU=1.5708 Radius=5.4
    g47: Circle CenterX=-34.575 CenterY=34.575 CenterZ=0 NormalX=0 NormalY=0 NormalZ=-1 AngleXU=1.5708 Radius=5.4
    g48: Circle CenterX=34.575 CenterY=34.575 CenterZ=0 NormalX=0 NormalY=0 NormalZ=-1 AngleXU=1.5708 Radius=5.4
    g49: Circle CenterX=145.633 CenterY=0 CenterZ=0 NormalX=0 NormalY=0 NormalZ=-1 AngleXU=1.5708 Radius=4.25
    g50: Circle CenterX=31.8705 CenterY=82.747 CenterZ=0 NormalX=0 NormalY=0 NormalZ=-1 AngleXU=1.0472 Radius=2.5
    g51: Circle CenterX=55.7258 CenterY=-68.9742 CenterZ=0 NormalX=0 NormalY=0 NormalZ=-1 AngleXU=-3.14159 Radius=2.5
    g52: Circle CenterX=140.207 CenterY=-56.173 CenterZ=0 NormalX=0 NormalY=0 NormalZ=-1 AngleXU=-3.14159 Radius=2.5
    g53: Circle CenterX=265 CenterY=-36 CenterZ=0 NormalX=0 NormalY=0 NormalZ=-1 AngleXU=-3.14159 Radius=2.5
    g54: Circle CenterX=-21.4561 CenterY=-149.509 CenterZ=0 NormalX=0 NormalY=0 NormalZ=-1 AngleXU=-1.0472 Radius=2.5
    g55: Circle CenterX=-21.4561 CenterY=149.509 CenterZ=0 NormalX=0 NormalY=0 NormalZ=-1 AngleXU=1.0472 Radius=2.5
    g56: Circle CenterX=140.207 CenterY=56.173 CenterZ=0 NormalX=0 NormalY=0 NormalZ=-1 AngleXU=-3.14159 Radius=2.5
    g57: Circle CenterX=55.7258 CenterY=68.9742 CenterZ=0 NormalX=0 NormalY=0 NormalZ=-1 AngleXU=-3.14159 Radius=2.5
    g58: Circle CenterX=265 CenterY=36 CenterZ=0 NormalX=0 NormalY=0 NormalZ=-1 AngleXU=-3.14159 Radius=2.5
    g59: Circle CenterX=-87.5963 CenterY=13.7728 CenterZ=0 NormalX=0 NormalY=0 NormalZ=-1 AngleXU=1.0472 Radius=2.5
    g60: Circle CenterX=-87.5963 CenterY=-13.7728 CenterZ=0 NormalX=0 NormalY=0 NormalZ=-1 AngleXU=-1.0472 Radius=2.5
    g61: Circle CenterX=31.8705 CenterY=-82.747 CenterZ=0 NormalX=0 NormalY=0 NormalZ=-1 AngleXU=-1.0472 Radius=2.5
    g62: Circle CenterX=-118.751 CenterY=93.336 CenterZ=0 NormalX=0 NormalY=0 NormalZ=-1 AngleXU=1.0472 Radius=2.5
    g63: Circle CenterX=-163.677 CenterY=211.497 CenterZ=0 NormalX=0 NormalY=0 NormalZ=-1 AngleXU=1.0472 Radius=2.5
    g64: Circle CenterX=-118.751 CenterY=-93.336 CenterZ=0 NormalX=0 NormalY=0 NormalZ=-1 AngleXU=-1.0472 Radius=2.5
    g65: Circle CenterX=-101.323 CenterY=247.497 CenterZ=0 NormalX=0 NormalY=0 NormalZ=-1 AngleXU=1.0472 Radius=2.5
    g66: Circle CenterX=-101.323 CenterY=-247.497 CenterZ=0 NormalX=0 NormalY=0 NormalZ=-1 AngleXU=-1.0472 Radius=2.5
    g67: Circle CenterX=-163.677 CenterY=-211.497 CenterZ=0 NormalX=0 NormalY=0 NormalZ=-1 AngleXU=-1.0472 Radius=2.5
    g68: LineSegment StartX=273.448 StartY=-46.699 StartZ=0 EndX=271.473 EndY=-47.0092 EndZ=0
    g69: LineSegment StartX=48.4571 StartY=-82.0288 StartZ=0 EndX=50.4329 EndY=-81.7185 EndZ=0
    g70: LineSegment StartX=46.8104 StartY=-82.9795 StartZ=0 EndX=45.5538 EndY=-84.5354 EndZ=0
    g71: LineSegment StartX=-96.2817 StartY=-260.163 StartZ=0 EndX=-95.0251 EndY=-258.607 EndZ=0
    g72: LineSegment StartX=-177.167 StartY=-213.464 StartZ=0 EndX=-176.447 EndY=-211.598 EndZ=0
    g73: LineSegment StartX=-95.2675 StartY=-0.950723 StartZ=0 EndX=-95.9868 EndY=-2.81693 EndZ=0
    g74: LineSegment StartX=-95.2675 StartY=0.950723 StartZ=0 EndX=-95.9868 EndY=2.81693 EndZ=0
    g75: LineSegment StartX=-177.167 StartY=213.464 StartZ=0 EndX=-176.447 EndY=211.598 EndZ=0
    g76: LineSegment StartX=-96.2817 StartY=260.163 StartZ=0 EndX=-95.0251 EndY=258.607 EndZ=0
    g77: LineSegment StartX=46.8104 StartY=82.9795 StartZ=0 EndX=45.5538 EndY=84.5354 EndZ=0
    g78: LineSegment StartX=48.4571 StartY=82.0288 StartZ=0 EndX=50.4329 EndY=81.7185 EndZ=0
    g79: LineSegment StartX=273.448 StartY=46.699 StartZ=0 EndX=271.473 EndY=47.0092 EndZ=0
  constraints (36):
    c: Coincident(g68,g-7)
    c: PointOnObject(g68,g-7)
    c: Coincident(g69,g-7)
    c: PointOnObject(g69,g-7)
    c: Coincident(g70,g-6)
    c: PointOnObject(g70,g-6)
    c: Coincident(g71,g-6)
    c: PointOnObject(g71,g-6)
    c: Coincident(g72,g-5)
    c: PointOnObject(g72,g-5)
    c: Coincident(g73,g-5)
    c: PointOnObject(g73,g-5)
    c: Coincident(g74,g-4)
    c: PointOnObject(g74,g-4)
    c: Coincident(g75,g-4)
    c: PointOnObject(g75,g-4)
    c: Coincident(g76,g-3)
    c: PointOnObject(g76,g-3)
    c: Coincident(g77,g-3)
    c: PointOnObject(g77,g-3)
    c: Coincident(g78,g-8)
    c: PointOnObject(g78,g-8)
    c: Coincident(g79,g-8)
    c: PointOnObject(g79,g-8)
    c: Equal(g79,g68)
    c: Equal(g68,g69)
    c: Equal(g69,g70)
    c: Equal(g70,g78)
    c: Equal(g78,g77)
    c: Equal(g77,g76)
    c: Equal(g76,g75)
    c: Equal(g75,g74)
    c: Equal(g74,g73)
    c: Equal(g73,g72)
    c: Equal(g72,g71)
    c: Distance(g78) = 2
FEATURE [App::DocumentObjectGroup] Group015  label="basement_amplifier_bottom"
  Group = -> [Body013,Page015,Unfold040,Unfold_Sketch040,Unfold_Sketch_Outline018,Unfold_Sketch_Internal,Unfold_Sketch_bends040]
FEATURE [Part::Mirroring] Part__Mirroring005  label="Unfold_Sketch031 (Mirror #6)"
  Base = (0,0,0)
  Normal = (1,0,0)
  Source = -> Unfold_Sketch031
FEATURE [App::DocumentObjectGroup] Group024  label="pillar3_bottom_corner_Group"
  Group = -> [Unfold031,Unfold_Sketch031,Unfold_Sketch_Outline010,Unfold_Sketch_Internal005,Unfold_Sketch_bends031,MirroredSketch,Part__Mirroring005,Page004,Page006]
FEATURE [TechDraw::DrawViewBalloon] Balloon015
  BubbleShape = 3
  EndType = 0
  EndTypeScale = 1
  KinkLength = 5
  LockPosition = false
  OriginX = 18.05
  OriginY = -1.25
  Rotation = 0
  ScaleType = 0
  ShapeScale = 1
  SourceView = -> View062
  Text = Оборотная сторона
  TextWrapLen = -1
  X = -57.9578
  Y = -1.47767
FEATURE [TechDraw::DrawViewBalloon] Balloon016
  BubbleShape = 3
  EndType = 0
  EndTypeScale = 1
  KinkLength = 5
  LockPosition = false
  OriginX = 18.7569
  OriginY = -2.04248
  Rotation = 0
  ScaleType = 0
  ShapeScale = 1
  SourceView = -> View062
  Text = Лицевая сторона
  TextWrapLen = -1
  X = 81.703
  Y = -1.91203
FEATURE [TechDraw::DrawViewBalloon] Balloon017
  BubbleShape = 3
  EndType = 0
  EndTypeScale = 1
  KinkLength = 5
  LockPosition = false
  OriginX = 18.3
  OriginY = -0.5
  Rotation = 0
  ScaleType = 0
  ShapeScale = 1
  SourceView = -> View054
  Text = Лицевая сторона
  TextWrapLen = -1
  X = 64.0196
  Y = 6.69421
FEATURE [TechDraw::DrawViewBalloon] Balloon018
  BubbleShape = 3
  EndType = 0
  EndTypeScale = 1
  KinkLength = 5
  LockPosition = false
  OriginX = 16.3377
  OriginY = 0.235099
  Rotation = 0
  ScaleType = 0
  ShapeScale = 1
  SourceView = -> View054
  Text = Оборотная сторона
  TextWrapLen = -1
  X = 59.4501
  Y = -12.9164
FEATURE [TechDraw::DrawViewPart] View063
  CoarseView = false
  Direction = (-0.57735,0.57735,0.57735)
  Focus = 100
  HardHidden = false
  IsoCount = 0
  IsoHidden = false
  IsoVisible = false
  LockPosition = false
  Perspective = false
  Rotation = 0
  Scale = 0.3
  ScaleType = 2
  ScrubCount = 0
  SeamHidden = false
  SeamVisible = true
  SmoothHidden = false
  SmoothVisible = true
  X = 230
  XDirection = (-0.707107,-0.707107,0)
  XSource = -> [Link]
  Y = 156
FEATURE [TechDraw::DrawViewBalloon] Balloon019
  BubbleShape = 3
  EndType = 0
  EndTypeScale = 1
  KinkLength = 5
  LockPosition = false
  OriginX = -139.613
  OriginY = 108.981
  Rotation = 0
  ScaleType = 0
  ShapeScale = 1
  SourceView = -> View063
  Text = Лицевая сторона
  TextWrapLen = -1
  X = -372.543
  Y = 108.614
FEATURE [TechDraw::DrawViewDimension] Dimension088
  AngleOverride = false
  Arbitrary = false
  ArbitraryTolerances = false
  BoxCorners = (2) [(-21.6913,-21.116,-1e-07),(21.6913,21.116,1e-07)]
  EqualTolerance = true
  ExtensionAngle = 0
  FormatSpec = %.2w
  FormatSpecOverTolerance = %+.2w
  FormatSpecUnderTolerance = %+.2w
  Inverted = false
  LineAngle = 0
  LockPosition = false
  MeasureType = 1
  OverTolerance = 0
  References2D = -> [View041]
  Rotation = 0
  ScaleType = 0
  TheoreticalExact = false
  Type = 6
  UnderTolerance = 0
  X = 5.54814
  Y = 17.0632
FEATURE [TechDraw::DrawViewDimension] Dimension089
  AngleOverride = false
  Arbitrary = false
  ArbitraryTolerances = false
  BoxCorners = (2) [(-21.6913,-21.116,-1e-07),(21.6913,21.116,1e-07)]
  EqualTolerance = true
  ExtensionAngle = 0
  FormatSpec = %.2w
  FormatSpecOverTolerance = %+.2w
  FormatSpecUnderTolerance = %+.2w
  Inverted = false
  LineAngle = 0
  LockPosition = false
  MeasureType = 1
  OverTolerance = 0
  References2D = -> [View041]
  Rotation = 0
  ScaleType = 0
  TheoreticalExact = false
  Type = 0
  UnderTolerance = 0
  X = 5.71615
  Y = -20.0538
FEATURE [TechDraw::DrawViewDimension] Dimension090
  AngleOverride = false
  Arbitrary = false
  ArbitraryTolerances = false
  BoxCorners = (2) [(-21.6913,-21.116,-1e-07),(21.6913,21.116,1e-07)]
  EqualTolerance = true
  ExtensionAngle = 0
  FormatSpec = %.2w
  FormatSpecOverTolerance = %+.2w
  FormatSpecUnderTolerance = %+.2w
  Inverted = false
  LineAngle = 0
  LockPosition = false
  MeasureType = 1
  OverTolerance = 0
  References2D = -> [View041]
  Rotation = 0
  ScaleType = 0
  TheoreticalExact = false
  Type = 2
  UnderTolerance = 0
  X = 30.6896
  Y = 10.7986
FEATURE [TechDraw::DrawViewDimension] Dimension091
  AngleOverride = false
  Arbitrary = false
  ArbitraryTolerances = false
  BoxCorners = (2) [(-21.6913,-21.116,-1e-07),(21.6913,21.116,1e-07)]
  EqualTolerance = true
  ExtensionAngle = 0
  FormatSpec = %.2w
  FormatSpecOverTolerance = %+.2w
  FormatSpecUnderTolerance = %+.2w
  Inverted = false
  LineAngle = 0
  LockPosition = false
  MeasureType = 1
  OverTolerance = 0
  References2D = -> [View041]
  Rotation = 0
  ScaleType = 0
  TheoreticalExact = false
  Type = 0
  UnderTolerance = 0
  X = -11.6913
  Y = 32.0503
FEATURE [TechDraw::DrawPage] Page016  label="top_amplifier_cornrer_page"
  KeepUpdated = true
  NextBalloonIndex = 7
  ProjectionType = 0
  Template = -> Template002
  Views = -> [View041,View042,View052,Dimension088,Dimension089,Dimension090,Dimension091]
FEATURE [App::DocumentObjectGroup] Group016  label="top_amplifier_cornrer_unfolds"
  Group = -> [Page016,Unfold039,Unfold_Sketch039,Unfold_Sketch_bends039]
FEATURE [Part::Feature] Unfold041
  shape: bbox 486.6 x 281.2 x 405.8 mm, 48 faces (baked)
FEATURE [Sketcher::SketchObject] Unfold_Sketch_bends041
  FullyConstrained = false
  sketch-geometry (2):
    g0: LineSegment StartX=-2.20963 StartY=4.46496 StartZ=0 EndX=-151.142 EndY=304.122 EndZ=0
    g1: LineSegment StartX=6.45112 StartY=-1.2485 StartZ=0 EndX=340.539 EndY=-20.2377 EndZ=0
FEATURE [Sketcher::SketchObject] Unfold_Sketch041
  ExternalGeometry = -> [Unfold_Sketch_bends041]
  FullyConstrained = false
  sketch-geometry (49):
    g0: LineSegment StartX=5 StartY=-4.83173 StartZ=0 EndX=5 EndY=-20 EndZ=0
    g1: ArcOfEllipse CenterX=0.564676 CenterY=-20.0001 CenterZ=0 NormalX=0 NormalY=0 NormalZ=1 MajorRadius=4.43592 MinorRadius=4.43532 AngleXU=-1.63576 StartAngle=0.588449 EndAngle=1.63577
    g2: ArcOfEllipse CenterX=4.98556 CenterY=-27.6602 CenterZ=0 NormalX=0 NormalY=0 NormalZ=1 MajorRadius=4.40872 MinorRadius=4.40821 AngleXU=-1.62926 StartAngle=3.72356 EndAngle=4.77086
    g3: LineSegment StartX=0.57735 StartY=-27.6603 StartZ=0 EndX=0.57735 EndY=-85 EndZ=0
    g4: ArcOfEllipse CenterX=5.63567 CenterY=-84.9336 CenterZ=0 NormalX=0 NormalY=0 NormalZ=1 MajorRadius=5.0533 MinorRadius=5.05134 AngleXU=-1.64071 StartAngle=4.79543 EndAngle=6.34159
    g5: LineSegment StartX=5.57735 StartY=-90 StartZ=0 EndX=335.432 EndY=-90 EndZ=0
    g6: LineSegment StartX=340.432 StartY=-85 StartZ=0 EndX=340.432 EndY=-22.112 EndZ=0
    g7: LineSegment StartX=340.445 StartY=-21.8919 StartZ=0 EndX=340.432 EndY=-22.112 EndZ=0
    g8: LineSegment StartX=340.473 StartY=-21.3987 StartZ=0 EndX=340.445 EndY=-21.8919 EndZ=0
    g9: LineSegment StartX=340.645 StartY=-18.3633 StartZ=0 EndX=340.473 EndY=-21.3987 EndZ=0
    g10: LineSegment StartX=346.141 StartY=-17.7132 StartZ=0 EndX=340.645 EndY=-18.3633 EndZ=0
    g11: ArcOfCircle CenterX=345.906 CenterY=-15.727 CenterZ=0 NormalX=0 NormalY=0 NormalZ=1 AngleXU=-0.583161 Radius=2 StartAngle=5.41331 EndAngle=7.14996
    g12: LineSegment StartX=347.826 StartY=-15.1674 StartZ=0 EndX=340.993 EndY=8.27833 EndZ=0
    g13: ArcOfCircle CenterX=339.073 CenterY=7.71868 CenterZ=0 NormalX=0 NormalY=0 NormalZ=1 AngleXU=-0.583161 Radius=2 StartAngle=0.866771 EndAngle=2.27171
    g14: LineSegment StartX=337.346 StartY=9.52832 StartZ=0 EndX=338.838 EndY=9.70483 EndZ=0
    g15: ArcOfCircle CenterX=-347.019 CenterY=-527.635 CenterZ=0 NormalX=0 NormalY=0 NormalZ=1 AngleXU=-0.583161 Radius=870 StartAngle=1.24863 EndAngle=1.89296
    g16: LineSegment StartX=-122.521 StartY=312.901 StartZ=0 EndX=-122.946 EndY=314.342 EndZ=0
    g17: ArcOfCircle CenterX=-124.864 CenterY=313.776 CenterZ=0 NormalX=0 NormalY=0 NormalZ=1 AngleXU=2.55843 Radius=2 StartAngle=4.01147 EndAngle=5.41641
    g18: LineSegment StartX=-149.349 StartY=312.817 StartZ=0 EndX=-125.106 EndY=315.761 EndZ=0
    g19: ArcOfCircle CenterX=-149.108 CenterY=310.832 CenterZ=0 NormalX=0 NormalY=0 NormalZ=1 AngleXU=2.55843 Radius=2 StartAngle=5.41641 EndAngle=7.15307
    g20: LineSegment StartX=-151.026 StartY=310.266 StartZ=0 EndX=-149.461 EndY=304.958 EndZ=0
    g21: LineSegment StartX=-149.461 StartY=304.958 StartZ=0 EndX=-152.626 EndY=303.385 EndZ=0
    g22: LineSegment StartX=-152.626 StartY=303.385 StartZ=0 EndX=-152.823 EndY=303.286 EndZ=0
    g23: LineSegment StartX=-152.823 StartY=303.286 StartZ=0 EndX=-210.637 EndY=278.538 EndZ=0
    g24: LineSegment StartX=-213.266 StartY=271.974 StartZ=0 EndX=-83.4559 EndY=-31.2652 EndZ=0
    g25: LineSegment StartX=-24.1787 StartY=-11.3288 StartZ=0 EndX=-76.8916 EndY=-33.8941 EndZ=0
    g26: ArcOfEllipse CenterX=-25.9184 CenterY=-7.26461 CenterZ=0 NormalX=0 NormalY=0 NormalZ=1 MajorRadius=4.42149 MinorRadius=4.4209 AngleXU=0.463024 StartAngle=4.65383 EndAngle=5.70115
    g27: ArcOfEllipse CenterX=-17.1366 CenterY=-8.31427 CenterZ=0 NormalX=0 NormalY=0 NormalZ=1 MajorRadius=4.42316 MinorRadius=4.42266 AngleXU=0.463016 StartAngle=1.51225 EndAngle=2.55955
    g28: LineSegment StartX=-18.877 StartY=-4.24845 StartZ=0 EndX=-4.93266 EndY=1.7208 EndZ=0
    g29: Circle CenterX=324.45 CenterY=15.7109 CenterZ=0 NormalX=0 NormalY=0 NormalZ=-1 AngleXU=-2.55843 Radius=1.7
    g30: Ellipse CenterX=173.002 CenterY=-84 CenterZ=0 NormalX=0 NormalY=0 NormalZ=-1 MajorRadius=1.7 MinorRadius=1.7 AngleXU=-1.51199
    g31: Ellipse CenterX=331.628 CenterY=-84 CenterZ=0 NormalX=0 NormalY=0 NormalZ=-1 MajorRadius=1.7 MinorRadius=1.7 AngleXU=-1.51199
    g32: Ellipse CenterX=331.628 CenterY=-34 CenterZ=0 NormalX=0 NormalY=0 NormalZ=-1 MajorRadius=1.7 MinorRadius=1.7 AngleXU=-1.51199
    g33: Ellipse CenterX=-143.828 CenterY=125.011 CenterZ=0 NormalX=0 NormalY=0 NormalZ=-1 MajorRadius=1.7 MinorRadius=1.7 AngleXU=2.67856
    g34: Ellipse CenterX=14.3756 CenterY=-84 CenterZ=0 NormalX=0 NormalY=0 NormalZ=-1 MajorRadius=1.7 MinorRadius=1.7 AngleXU=-1.51199
    g35: Ellipse CenterX=-81.4024 CenterY=-20.8156 CenterZ=0 NormalX=0 NormalY=0 NormalZ=-1 MajorRadius=1.7 MinorRadius=1.7 AngleXU=2.67856
    g36: Ellipse CenterX=-160.287 CenterY=290.515 CenterZ=0 NormalX=0 NormalY=0 NormalZ=-1 MajorRadius=1.7 MinorRadius=1.7 AngleXU=2.67856
    g37: Ellipse CenterX=-206.253 CenterY=270.838 CenterZ=0 NormalX=0 NormalY=0 NormalZ=-1 MajorRadius=1.7 MinorRadius=1.7 AngleXU=2.67856
    g38: Circle CenterX=-111.762 CenterY=303.478 CenterZ=0 NormalX=0 NormalY=0 NormalZ=-1 AngleXU=-2.55843 Radius=1.7
    g39: Circle CenterX=52.2217 CenterY=237.905 CenterZ=0 NormalX=0 NormalY=0 NormalZ=-1 AngleXU=-2.55843 Radius=1.7
    g40: Circle CenterX=199.634 CenterY=140.658 CenterZ=0 NormalX=0 NormalY=0 NormalZ=-1 AngleXU=-2.55843 Radius=1.7
    g41: ArcOfCircle CenterX=0.460789 CenterY=-0.908016 CenterZ=0 NormalX=0 NormalY=0 NormalZ=1 AngleXU=0 Radius=6 StartAngle=5.57039 EndAngle=8.97125
    g42: ArcOfCircle CenterX=335.432 CenterY=-85 CenterZ=0 NormalX=0 NormalY=0 NormalZ=1 AngleXU=0 Radius=5 StartAngle=4.71239 EndAngle=6.28319
    g43: ArcOfCircle CenterX=-208.669 CenterY=273.941 CenterZ=0 NormalX=0 NormalY=0 NormalZ=1 AngleXU=0 Radius=5 StartAngle=1.97527 EndAngle=3.54607
    g44: ArcOfCircle CenterX=-78.8593 CenterY=-29.2975 CenterZ=0 NormalX=0 NormalY=0 NormalZ=1 AngleXU=0 Radius=5 StartAngle=3.54607 EndAngle=5.11686
    g45: LineSegment StartX=6.45112 StartY=-1.2485 StartZ=0 EndX=8.4479 EndY=-1.36199 EndZ=0
    g46: LineSegment StartX=-2.20963 StartY=4.46496 StartZ=0 EndX=-3.09977 EndY=6.25595 EndZ=0
    g47: LineSegment StartX=340.539 StartY=-20.2377 StartZ=0 EndX=338.542 EndY=-20.1242 EndZ=0
    g48: LineSegment StartX=-151.142 StartY=304.122 StartZ=0 EndX=-150.252 EndY=302.331 EndZ=0
  constraints (52):
    c: Coincident(g22,g23)
    c: Coincident(g21,g22)
    c: Coincident(g19,g20)
    c: Coincident(g20,g21)
    c: Coincident(g18,g19)
    c: Coincident(g17,g18)
    c: Coincident(g16,g17)
    c: Coincident(g15,g16)
    c: Coincident(g14,g15)
    c: Coincident(g13,g14)
    c: Coincident(g6,g7)
    c: Coincident(g7,g8)
    c: Coincident(g8,g9)
    c: Coincident(g9,g10)
    c: Coincident(g12,g13)
    c: Coincident(g10,g11)
    c: Coincident(g11,g12)
    c: Block(g3)
    c: Block(g0)
    c: Block(g28)
    c: Block(g25)
    c: Tangent(g2,g1) = 1.5708
    c: Tangent(g2,g3) = -1.5708
    c: Tangent(g1,g0) = 1.5708
    c: Tangent(g27,g28) = 1.5708
    c: Tangent(g26,g25) = 1.5708
    c: Tangent(g26,g27) = 1.5708
    c: Coincident(g41,g28)
    c: Coincident(g41,g0)
    c: PointOnObject(g-4,g41)
    c: Block(g5)
    c: Block(g6)
    c: Coincident(g42,g6)
    c: Tangent(g42,g5) = -1.5708
    c: Block(g24)
    c: Block(g23)
    c: Tangent(g43,g24) = -1.5708
    c: Tangent(g43,g23) = -1.5708
    c: Tangent(g44,g24) = -1.5708
    c: Tangent(g44,g25) = 1.5708
    c: Coincident(g45,g-3)
    c: PointOnObject(g45,g-3)
    c: Coincident(g46,g-4)
    c: PointOnObject(g46,g-4)
    c: Coincident(g47,g-3)
    c: PointOnObject(g47,g-3)
    c: Coincident(g48,g-4)
    c: PointOnObject(g48,g-4)
    c: Equal(g48,g46)
    c: Equal(g45,g47)
    c: Equal(g46,g45)
    c: Distance(g45) = 2
FEATURE [TechDraw::DrawViewDimension] Dimension092
  AngleOverride = false
  Arbitrary = false
  ArbitraryTolerances = false
  BoxCorners = (2) [(-77.1148,-24.7714,-1e-07),(77.1148,24.7714,1e-07)]
  EqualTolerance = true
  ExtensionAngle = 0
  FormatSpec = %.2w
  FormatSpecOverTolerance = %+.2w
  FormatSpecUnderTolerance = %+.2w
  Inverted = false
  LineAngle = 0
  LockPosition = false
  MeasureType = 1
  OverTolerance = 0
  References2D = -> [View]
  Rotation = 0
  ScaleType = 0
  TheoreticalExact = false
  Type = 6
  UnderTolerance = 0
  X = 65.1215
  Y = -5.17094
FEATURE [TechDraw::DrawPage] Page
  KeepUpdated = true
  NextBalloonIndex = 6
  ProjectionType = 0
  Template = -> Template
  Views = -> [View,View053,View063,Balloon019,Dimension092]
FEATURE [App::DocumentObjectGroup] Group002  label="sink_unfolds"
  Group = -> [Unfold,Unfold_Sketch,Unfold_Sketch_Outline,Unfold_Sketch_bends,Body,Page,Unfold041,Unfold_Sketch041,Unfold_Sketch_bends041]
FEATURE [TechDraw::DrawViewDimension] Dimension093
  AngleOverride = false
  Arbitrary = false
  ArbitraryTolerances = false
  BoxCorners = (2) [(-18.3,-9.5,-1e-07),(18.3,9.5,1e-07)]
  EqualTolerance = true
  ExtensionAngle = 0
  FormatSpec = %.2w
  FormatSpecOverTolerance = %+.2w
  FormatSpecUnderTolerance = %+.2w
  Inverted = false
  LineAngle = 0
  LockPosition = false
  MeasureType = 1
  OverTolerance = 0
  References2D = -> [View054]
  Rotation = 0
  ScaleType = 0
  TheoreticalExact = false
  Type = 2
  UnderTolerance = 0
  X = -30
  Y = 3
FEATURE [TechDraw::DrawViewDimension] Dimension094
  AngleOverride = false
  Arbitrary = false
  ArbitraryTolerances = false
  BoxCorners = (2) [(-18.3,-9.5,-1e-07),(18.3,9.5,1e-07)]
  EqualTolerance = true
  ExtensionAngle = 0
  FormatSpec = %.2w
  FormatSpecOverTolerance = %+.2w
  FormatSpecUnderTolerance = %+.2w
  Inverted = false
  LineAngle = 0
  LockPosition = false
  MeasureType = 1
  OverTolerance = 0
  References2D = -> [View054]
  Rotation = 0
  ScaleType = 0
  TheoreticalExact = false
  Type = 1
  UnderTolerance = 0
  X = 0
  Y = 23.0445
FEATURE [TechDraw::DrawPage] Page020
  KeepUpdated = true
  NextBalloonIndex = 9
  ProjectionType = 0
  Template = -> Template
  Views = -> [View054,View055,View056,Balloon017,Balloon018,Dimension093,Dimension094]
FEATURE [App::DocumentObjectGroup] Group019  label="pillar3_Group"
  Group = -> [Page020,Unfold035,Unfold_Sketch035,Unfold_Sketch_Outline014,Unfold_Sketch_Internal008,Unfold_Sketch_bends035]
FEATURE [TechDraw::DrawViewDimension] Dimension095
  AngleOverride = false
  Arbitrary = false
  ArbitraryTolerances = false
  BoxCorners = (2) [(-35,-42,-1e-07),(35,42,1e-07)]
  EqualTolerance = true
  ExtensionAngle = 0
  FormatSpec = %.2w
  FormatSpecOverTolerance = %+.2w
  FormatSpecUnderTolerance = %+.2w
  Inverted = false
  LineAngle = 0
  LockPosition = false
  MeasureType = 1
  OverTolerance = 0
  References2D = -> [View057]
  Rotation = 0
  ScaleType = 0
  TheoreticalExact = false
  Type = 1
  UnderTolerance = 0
  X = 0.141544
  Y = -55.1599
FEATURE [TechDraw::DrawViewDimension] Dimension096
  AngleOverride = false
  Arbitrary = false
  ArbitraryTolerances = false
  BoxCorners = (2) [(-35,-42,-1e-07),(35,42,1e-07)]
  EqualTolerance = true
  ExtensionAngle = 0
  FormatSpec = %.2w
  FormatSpecOverTolerance = %+.2w
  FormatSpecUnderTolerance = %+.2w
  Inverted = false
  LineAngle = 0
  LockPosition = false
  MeasureType = 1
  OverTolerance = 0
  References2D = -> [View057]
  Rotation = 0
  ScaleType = 0
  TheoreticalExact = false
  Type = 2
  UnderTolerance = 0
  X = 65.8794
  Y = 3.80555
FEATURE [TechDraw::DrawViewDimension] Dimension097
  AngleOverride = false
  Arbitrary = false
  ArbitraryTolerances = false
  BoxCorners = (2) [(-35,-42,-1e-07),(35,42,1e-07)]
  EqualTolerance = true
  ExtensionAngle = 0
  FormatSpec = %.2w
  FormatSpecOverTolerance = %+.2w
  FormatSpecUnderTolerance = %+.2w
  Inverted = false
  LineAngle = 0
  LockPosition = false
  MeasureType = 1
  OverTolerance = 0
  References2D = -> [View057]
  Rotation = 0
  ScaleType = 0
  TheoreticalExact = false
  Type = 1
  UnderTolerance = 0
  X = 20.0729
  Y = 59.2188
FEATURE [TechDraw::DrawPage] Page021
  KeepUpdated = true
  NextBalloonIndex = 5
  ProjectionType = 0
  Template = -> Template
  Views = -> [View057,View058,Dimension095,Dimension096,Dimension097]
FEATURE [App::DocumentObjectGroup] Group020  label="pillar3_hat_fix_Group"
  Group = -> [Page021,Unfold036,Unfold_Sketch036,Unfold_Sketch_Outline015,Unfold_Sketch_Internal009,Unfold_Sketch_bends036]
FEATURE [TechDraw::DrawViewDimension] Dimension098
  AngleOverride = false
  Arbitrary = false
  ArbitraryTolerances = false
  BoxCorners = (2) [(-18.55,-10.5,-1e-07),(18.55,10.5,1e-07)]
  EqualTolerance = true
  ExtensionAngle = 0
  FormatSpec = %.2w
  FormatSpecOverTolerance = %+.2w
  FormatSpecUnderTolerance = %+.2w
  Inverted = false
  LineAngle = 0
  LockPosition = false
  MeasureType = 1
  OverTolerance = 0
  References2D = -> [View059]
  Rotation = 0
  ScaleType = 0
  TheoreticalExact = false
  Type = 2
  UnderTolerance = 0
  X = -32.431
  Y = 3.58078
FEATURE [TechDraw::DrawViewDimension] Dimension099
  AngleOverride = false
  Arbitrary = false
  ArbitraryTolerances = false
  BoxCorners = (2) [(-18.55,-10.5,-1e-07),(18.55,10.5,1e-07)]
  EqualTolerance = true
  ExtensionAngle = 0
  FormatSpec = %.2w
  FormatSpecOverTolerance = %+.2w
  FormatSpecUnderTolerance = %+.2w
  Inverted = false
  LineAngle = 0
  LockPosition = false
  MeasureType = 1
  OverTolerance = 0
  References2D = -> [View059]
  Rotation = 0
  ScaleType = 0
  TheoreticalExact = false
  Type = 1
  UnderTolerance = 0
  X = 0
  Y = -27.025
FEATURE [TechDraw::DrawPage] Page022
  KeepUpdated = true
  NextBalloonIndex = 6
  ProjectionType = 0
  Template = -> Template
  Views = -> [View059,View060,Balloon013,Dimension098,Dimension099]
FEATURE [App::DocumentObjectGroup] Group021  label="pilllar3_dec_corner_Group"
  Group = -> [Page022,Unfold037,Unfold_Sketch037,Unfold_Sketch_Outline016,Unfold_Sketch_Internal010,Unfold_Sketch_bends037]
FEATURE [TechDraw::DrawViewDimension] Dimension100
  AngleOverride = false
  Arbitrary = false
  ArbitraryTolerances = false
  BoxCorners = (2) [(-18.55,-10.5,-1e-07),(18.55,10.5,1e-07)]
  EqualTolerance = true
  ExtensionAngle = 0
  FormatSpec = %.2w
  FormatSpecOverTolerance = %+.2w
  FormatSpecUnderTolerance = %+.2w
  Inverted = false
  LineAngle = 0
  LockPosition = false
  MeasureType = 1
  OverTolerance = 0
  References2D = -> [View062]
  Rotation = 0
  ScaleType = 0
  TheoreticalExact = false
  Type = 1
  UnderTolerance = 0
  X = 0.667888
  Y = -24.1151
FEATURE [TechDraw::DrawViewDimension] Dimension101
  AngleOverride = false
  Arbitrary = false
  ArbitraryTolerances = false
  BoxCorners = (2) [(-18.55,-10.5,-1e-07),(18.55,10.5,1e-07)]
  EqualTolerance = true
  ExtensionAngle = 0
  FormatSpec = %.2w
  FormatSpecOverTolerance = %+.2w
  FormatSpecUnderTolerance = %+.2w
  Inverted = false
  LineAngle = 0
  LockPosition = false
  MeasureType = 1
  OverTolerance = 0
  References2D = -> [View062]
  Rotation = 0
  ScaleType = 0
  TheoreticalExact = false
  Type = 2
  UnderTolerance = 0
  X = 32.9536
  Y = 4.23929
FEATURE [TechDraw::DrawPage] Page023
  KeepUpdated = true
  NextBalloonIndex = 8
  ProjectionType = 0
  Template = -> Template
  Views = -> [View061,View062,Balloon014,Balloon015,Balloon016,Dimension100,Dimension101]
FEATURE [App::DocumentObjectGroup] Group022  label="pilllar3_dec_corner_mirror_Group"
  Group = -> [Page023,Unfold038,Unfold_Sketch038,Unfold_Sketch_Outline017,Unfold_Sketch_Internal011,Unfold_Sketch_bends038]
FEATURE [Measure::MeasureDistance] Distance
  Distance = 27.9333
  Element1 = -> Unfold_Sketch035 [Edge40]
  Element2 = -> Unfold_Sketch035 [Edge38]
  Position1 = (10.7,26.5124,0)
  Position2 = (38.6333,26.5124,0)
FEATURE [App::DocumentObjectGroup] Measurements
  Group = -> [Distance]
FEATURE [App::Link] Link026  label="Page024"
  LinkedObject = -> <external U-fix.FCStd>#Page
FEATURE [App::Link] Link027  label="Unfold_Sketch042"
  LinkedObject = -> <external U-fix.FCStd>#Unfold_Sketch
FEATURE [App::Link] Link028  label="Unfold_Sketch_Outline019"
  LinkedObject = -> <external U-fix.FCStd>#Unfold_Sketch_Outline
FEATURE [App::Link] Link029  label="Unfold_Sketch_Internal012"
  LinkedObject = -> <external U-fix.FCStd>#Unfold_Sketch_Internal
FEATURE [App::Link] Link030  label="Unfold042"
  LinkedObject = -> <external U-fix.FCStd>#Unfold
FEATURE [App::Link] Link031  label="Unfold_Sketch_bends042"
  LinkedObject = -> <external U-fix.FCStd>#Unfold_Sketch_bends
FEATURE [App::DocumentObjectGroup] Group025  label="U-fix_Group"
  Group = -> [Link026,Link030,Link027,Link028,Link029,Link031]
FEATURE [App::DocumentObjectGroup] Group001  label="unfolds"
  Group = -> [Group002,Group003,Group004,Group005,Group006,Group007,Group008,Group009,Group010,Group011,Group012,Group013,Group014,Group015,Group017,Group016,Group018,Group019,Group020,Group021,Group022,Group023,Group024,Group025]
note: 3 file-system paths scrubbed to <path> (originals preserved in the JSON sidecar)

RESOLVED EXTERNAL PARTS (link-assembly join: the EXTERNAL_REF files above that resolve inside this repo's crawl, each included once):
---- part U-fix.FCStd = doc fcstd_8b42821c5992 ----
FCSTD DOCUMENT  (FreeCAD 1.1R38827 (Git))
Label: U-fix
License: All rights reserved
LicenseURL: http://en.wikipedia.org/wiki/All_rights_reserved
objects: Sketcher::SketchObject×7, TechDraw::DrawViewDimension×4, TechDraw::DrawViewPart×3, PartDesign::SubShapeBinder×2, PartDesign::Pocket×2, PartDesign::FeaturePython×1, PartDesign::Mirrored×1, TechDraw::DrawSVGTemplate×1, Part::Feature×1, PartDesign::Hole×1, PartDesign::Body×1, TechDraw::DrawPage×1, App::DocumentObjectGroup×1
note: 37 computed .brp shape members not serialized (recipe doc carries the construction recipe); baked Part::Feature solids carry a one-line shape summary decoded from their .brp
EXTERNAL_REF file=ugol90degX40mm.FCStd obj=Binder002
EXTERNAL_REF file=wheel50mm.FCStd obj=Populate001

FEATURE [Sketcher::SketchObject] Sketch
  ArcFitTolerance = 0
  AttachmentSupport = -> [XZ_Plane]
  FullyConstrained = true
  MakeInternals = false
  MapMode = 5
  Placement = pos=(0,0,0) rot=(1,0,0;1.5708rad)
  sketch-geometry (5):
    g0: LineSegment StartX=-11.5 StartY=16 StartZ=0 EndX=-11.5 EndY=0 EndZ=0
    g1: LineSegment StartX=-11.5 StartY=0 StartZ=0 EndX=11.5 EndY=0 EndZ=0
    g2: LineSegment StartX=11.5 StartY=0 StartZ=0 EndX=11.5 EndY=16 EndZ=0
    g3: LineSegment [constr] StartX=11.5 StartY=16 StartZ=0 EndX=-11.5 EndY=16 EndZ=0
    g4: GeomPoint [constr] X=0 Y=8 Z=0
  constraints (13):
    c: Coincident(g0,g1)
    c: Coincident(g1,g2)
    c: Coincident(g2,g3)
    c: Coincident(g3,g0)
    c: Horizontal(g1)
    c: Horizontal(g3)
    c: Vertical(g0)
    c: Vertical(g2)
    c: Symmetric(g1,g0,g4)
    c: PointOnObject(g4,g-2)
    c: PointOnObject(g1,g-1)
    c: DistanceX(g1,g1) = 23  'width'
    c: DistanceY(g2) = 16  'height'
FEATURE [PartDesign::FeaturePython] BaseBend  # WARN: FeaturePython — macro-defined, semantics opaque (R4)
  BendSide = 1
  BendSketch = -> Sketch
  MidPlane = true
  Reverse = false
  Suppressed = false
  length = 65
  radius = 2
  thickness = 1
FEATURE [PartDesign::SubShapeBinder] Binder  label="U-fix_vert_holes"
  BindCopyOnChange = 0
  BindMode = 0
  ClaimChildren = false
  Context = -> Body [Binder.]
  Fuse = false
  MakeFace = true
  OffsetFill = false
  OffsetIntersection = false
  OffsetJoinType = 0
  OffsetOpenResult = false
  PartialLoad = false
  Placement = pos=(0,0,0) rot=(0,0,1;1.5708rad)
  Relative = true
  Support = -> [<external ugol90degX40mm.FCStd>#Binder002]
  _Version = 2
  expr: Support = <<ugol90degX40mm>>#<<vert>>._self
FEATURE [PartDesign::Pocket] Pocket
  BaseFeature = -> BaseBend
  Direction = (1,-2e-16,0)
  Length = 5
  Length2 = 5
  Midplane = true
  Profile = -> Binder
  Suppressed = false
  Type = 1
FEATURE [Sketcher::SketchObject] Sketch001
  ArcFitTolerance = 0
  AttachmentOffset = pos=(32.5,16,0) rot=(0,0,1;0rad)
  AttachmentSupport = -> [YZ_Plane]
  FullyConstrained = true
  MakeInternals = false
  MapMode = 5
  Placement = pos=(0,32.5,16) rot=(0.57735,0.57735,0.57735;2.0944rad)
  expr: .AttachmentOffset.Base.x = BaseBend.length / 2
  expr: .AttachmentOffset.Base.y = Sketch.Constraints.height
  sketch-geometry (3):
    g0: ArcOfCircle CenterX=-5 CenterY=-5 CenterZ=0 NormalX=0 NormalY=0 NormalZ=1 AngleXU=0 Radius=5 StartAngle=0 EndAngle=1.5708
    g1: LineSegment StartX=-9e-16 StartY=-5 StartZ=0 EndX=0 EndY=0 EndZ=0
    g2: LineSegment StartX=0 StartY=0 StartZ=0 EndX=-5.00003 EndY=-4.65468e-11 EndZ=0
  constraints (8):
    c: PointOnObject(g0,g-1)
    c: PointOnObject(g0,g-2)
    c: Coincident(g1,g2)
    c: Coincident(g2,g0)
    c: Tangent(g2,g0)
    c: Tangent(g0,g1) = -1.5708
    c: Coincident(g1,g-1)
    c: Diameter(g0) = 10
FEATURE [PartDesign::Pocket] Pocket001
  BaseFeature = -> Pocket
  Direction = (-1,0,0)
  Length = 5
  Length2 = 5
  Midplane = true
  Profile = -> Sketch001
  ReferenceAxis = -> Sketch001 [N_Axis]
  Suppressed = false
  Type = 1
FEATURE [PartDesign::Mirrored] Mirrored
  BaseFeature = -> Pocket001
  MirrorPlane = -> XZ_Plane
  Originals = -> [Pocket001]
  Suppressed = false
  TransformMode = 0
FEATURE [Sketcher::SketchObject] Sketch002  label="holes_bottom"
  ArcFitTolerance = 0
  AttachmentSupport = -> [XY_Plane]
  FullyConstrained = true
  MakeInternals = false
  MapMode = 5
  sketch-geometry (2):
    g0: Circle CenterX=0 CenterY=17.5 CenterZ=0 NormalX=0 NormalY=0 NormalZ=1 AngleXU=0 Radius=2.5
    g1: Circle CenterX=0 CenterY=-17.5 CenterZ=0 NormalX=0 NormalY=0 NormalZ=1 AngleXU=0 Radius=2.5
  constraints (5):
    c: PointOnObject(g0,g-2)
    c: Symmetric(g1,g0,g-1)
    c: Equal(g1,g0)
    c: Diameter(g1) = 5
    c: DistanceY(g1,g0) = 35
FEATURE [TechDraw::DrawSVGTemplate] Template
  Height = 210
  Orientation = 1
  Template = <path>
  Width = 297
FEATURE [Part::Feature] Unfold
  Placement = pos=(0,0,0) rot=(0,0,1;1.5708rad)
  shape: bbox 53 x 50.85 x 1 mm, 16 faces (baked)
FEATURE [Sketcher::SketchObject] Unfold_Sketch_Outline
  ArcFitTolerance = 0
  FullyConstrained = false
  MakeInternals = false
  sketch-geometry (8):
    g0: ArcOfCircle CenterX=21.5 CenterY=-20.427 CenterZ=0 NormalX=0 NormalY=0 NormalZ=1 AngleXU=4e-16 Radius=5 StartAngle=4.71238 EndAngle=6.28319
    g1: LineSegment StartX=26.5 StartY=20.427 StartZ=0 EndX=26.5 EndY=-20.427 EndZ=0
    g2: ArcOfCircle CenterX=21.5 CenterY=20.427 CenterZ=0 NormalX=0 NormalY=0 NormalZ=1 AngleXU=-4e-16 Radius=5 StartAngle=0 EndAngle=1.5708
    g3: LineSegment StartX=21.5 StartY=25.427 StartZ=0 EndX=-21.5 EndY=25.427 EndZ=0
    g4: ArcOfCircle CenterX=-21.5 CenterY=20.427 CenterZ=0 NormalX=0 NormalY=0 NormalZ=1 AngleXU=-3.14159 Radius=5 StartAngle=4.71238 EndAngle=6.28319
    g5: LineSegment StartX=-26.5 StartY=20.427 StartZ=0 EndX=-26.5 EndY=-20.427 EndZ=0
    g6: ArcOfCircle CenterX=-21.5 CenterY=-20.427 CenterZ=0 NormalX=0 NormalY=0 NormalZ=1 AngleXU=3.14159 Radius=5 StartAngle=0 EndAngle=1.5708
    g7: LineSegment StartX=21.5 StartY=-25.427 StartZ=0 EndX=-21.5 EndY=-25.427 EndZ=0
FEATURE [Sketcher::SketchObject] Unfold_Sketch_Internal
  ArcFitTolerance = 0
  FullyConstrained = false
  MakeInternals = false
  sketch-geometry (6):
    g0: Circle CenterX=17.5 CenterY=0 CenterZ=0 NormalX=0 NormalY=0 NormalZ=1 AngleXU=1.5708 Radius=2.75
    g1: Circle CenterX=-17.5 CenterY=0 CenterZ=0 NormalX=0 NormalY=0 NormalZ=1 AngleXU=1.5708 Radius=2.75
    g2: Circle CenterX=20 CenterY=-19.927 CenterZ=0 NormalX=0 NormalY=0 NormalZ=1 AngleXU=2e-16 Radius=1.7
    g3: Circle CenterX=-20 CenterY=-19.927 CenterZ=0 NormalX=0 NormalY=0 NormalZ=1 AngleXU=2e-16 Radius=1.7
    g4: Circle CenterX=20 CenterY=19.927 CenterZ=0 NormalX=0 NormalY=0 NormalZ=-1 AngleXU=-3.14159 Radius=1.7
    g5: Circle CenterX=-20 CenterY=19.927 CenterZ=0 NormalX=0 NormalY=0 NormalZ=-1 AngleXU=-3.14159 Radius=1.7
FEATURE [Sketcher::SketchObject] Unfold_Sketch_bends
  ArcFitTolerance = 0
  FullyConstrained = false
  MakeInternals = false
  sketch-geometry (2):
    g0: LineSegment StartX=-26.5 StartY=10.4635 StartZ=0 EndX=26.5 EndY=10.4635 EndZ=0
    g1: LineSegment StartX=-26.5 StartY=-10.4635 StartZ=0 EndX=26.5 EndY=-10.4635 EndZ=0
FEATURE [Sketcher::SketchObject] Unfold_Sketch
  ArcFitTolerance = 0
  ExternalGeometry = -> [Unfold_Sketch_bends]
  FullyConstrained = false
  MakeInternals = false
  sketch-geometry (18):
    g0: ArcOfCircle CenterX=21.5 CenterY=-20.427 CenterZ=0 NormalX=0 NormalY=0 NormalZ=1 AngleXU=4e-16 Radius=5 StartAngle=4.71238 EndAngle=6.28319
    g1: LineSegment StartX=21.5 StartY=-25.427 StartZ=0 EndX=-21.5 EndY=-25.427 EndZ=0
    g2: ArcOfCircle CenterX=-21.5 CenterY=-20.427 CenterZ=0 NormalX=0 NormalY=0 NormalZ=1 AngleXU=3.14159 Radius=5 StartAngle=0 EndAngle=1.5708
    g3: ArcOfCircle CenterX=-21.5 CenterY=20.427 CenterZ=0 NormalX=0 NormalY=0 NormalZ=1 AngleXU=-3.14159 Radius=5 StartAngle=4.71238 EndAngle=6.28319
    g4: LineSegment StartX=21.5 StartY=25.427 StartZ=0 EndX=-21.5 EndY=25.427 EndZ=0
    g5: ArcOfCircle CenterX=21.5 CenterY=20.427 CenterZ=0 NormalX=0 NormalY=0 NormalZ=1 AngleXU=-4e-16 Radius=5 StartAngle=0 EndAngle=1.5708
    g6: Circle CenterX=-17.5 CenterY=0 CenterZ=0 NormalX=0 NormalY=0 NormalZ=1 AngleXU=1.5708 Radius=2.75
    g7: Circle CenterX=17.5 CenterY=0 CenterZ=0 NormalX=0 NormalY=0 NormalZ=1 AngleXU=1.5708 Radius=2.75
    g8: Circle CenterX=-20 CenterY=19.927 CenterZ=0 NormalX=0 NormalY=0 NormalZ=-1 AngleXU=-3.14159 Radius=1.7
    g9: Circle CenterX=20 CenterY=19.927 CenterZ=0 NormalX=0 NormalY=0 NormalZ=-1 AngleXU=-3.14159 Radius=1.7
    g10: Circle CenterX=-20 CenterY=-19.927 CenterZ=0 NormalX=0 NormalY=0 NormalZ=1 AngleXU=2e-16 Radius=1.7
    g11: Circle CenterX=20 CenterY=-19.927 CenterZ=0 NormalX=0 NormalY=0 NormalZ=1 AngleXU=2e-16 Radius=1.7
    g12: LineSegment StartX=26.5 StartY=20.427 StartZ=0 EndX=26.5 EndY=-20.427 EndZ=0
    g13: LineSegment StartX=-26.5 StartY=20.427 StartZ=0 EndX=-26.5 EndY=-20.427 EndZ=0
    g14: LineSegment StartX=26.5 StartY=-10.4635 StartZ=0 EndX=24.5 EndY=-10.4635 EndZ=0
    g15: LineSegment StartX=26.5 StartY=10.4635 StartZ=0 EndX=24.5 EndY=10.4635 EndZ=0
    g16: LineSegment StartX=-26.5 StartY=10.4635 StartZ=0 EndX=-24.5 EndY=10.4635 EndZ=0
    g17: LineSegment StartX=-26.5 StartY=-10.4635 StartZ=0 EndX=-24.5 EndY=-10.4635 EndZ=0
  constraints (20):
    c: Coincident(g2,g13)
    c: Coincident(g3,g13)
    c: Coincident(g1,g2)
    c: Coincident(g3,g4)
    c: Coincident(g0,g1)
    c: Coincident(g4,g5)
    c: Coincident(g0,g12)
    c: Coincident(g5,g12)
    c: Coincident(g14,g-4)
    c: Coincident(g15,g-3)
    c: Coincident(g16,g-3)
    c: Coincident(g17,g-4)
    c: PointOnObject(g17,g-4)
    c: PointOnObject(g16,g-3)
    c: PointOnObject(g15,g-3)
    c: PointOnObject(g14,g-4)
    c: Equal(g14,g15)
    c: Equal(g15,g16)
    c: Equal(g16,g17)
    c: Distance(g17) = 2
FEATURE [PartDesign::SubShapeBinder] Binder001
  BindCopyOnChange = 0
  BindMode = 0
  ClaimChildren = false
  Context = -> Body [Binder001.]
  Fuse = false
  MakeFace = true
  OffsetFill = false
  OffsetIntersection = false
  OffsetJoinType = 0
  OffsetOpenResult = false
  PartialLoad = false
  Placement = pos=(0,0,0) rot=(0,0,1;0.785398rad)
  Relative = true
  Support = -> [<external wheel50mm.FCStd>#Populate001]
  _Version = 2
  expr: Support = wheel50mm#<<holes_max>>._self
FEATURE [PartDesign::Hole] Hole
  BaseFeature = -> Mirrored
  CustomThreadClearance = 0
  Depth = 25
  DepthType = 0
  Diameter = 5.5
  DrillForDepth = false
  DrillPoint = 1
  DrillPointAngle = 118
  HoleCutCountersinkAngle = 90
  HoleCutCustomValues = false
  HoleCutDepth = 0
  HoleCutDiameter = 6.1
  HoleCutType = 0
  ModelThread = false
  Profile = -> Binder001
  Reversed = true
  Suppressed = false
  Tapered = false
  TaperedAngle = 90
  ThreadClass = 0
  ThreadDepth = 25
  ThreadDepthType = 0
  ThreadDirection = 0
  ThreadFit = 0
  ThreadSize = 0
  ThreadType = 0
  Threaded = false
  UseCustomThreadClearance = false
FEATURE [PartDesign::Body] Body  label="U_fix_material_0.50ansi"
  AllowCompound = false
  Group = -> [Sketch,BaseBend,Binder,Pocket,Sketch001,Pocket001,Mirrored,Sketch002,Hole,Binder001]
  Origin = -> Origin
  Tip = -> Hole
FEATURE [TechDraw::DrawViewPart] View
  CoarseView = false
  Direction = (0,-1,0)
  Focus = 100
  HardHidden = false
  IsoCount = 0
  IsoHidden = false
  IsoVisible = false
  LockPosition = false
  Perspective = false
  Rotation = 0
  ScaleType = 0
  ScrubCount = 0
  SeamHidden = false
  SeamVisible = true
  SmoothHidden = false
  SmoothVisible = true
  Source = -> [Body]
  X = 69.5
  XDirection = (1,0,0)
  Y = 105
  expr: Y = Template.Height / 2
FEATURE [TechDraw::DrawViewPart] View001
  CoarseView = false
  Direction = (1,0,0)
  Focus = 100
  HardHidden = false
  IsoCount = 0
  IsoHidden = false
  IsoVisible = false
  LockPosition = false
  Perspective = false
  Rotation = 0
  ScaleType = 0
  ScrubCount = 0
  SeamHidden = false
  SeamVisible = true
  SmoothHidden = false
  SmoothVisible = true
  Source = -> [Body]
  X = 226.5
  XDirection = (0,1,-1.19209e-07)
  Y = 105
  expr: Y = Template.Height / 2
FEATURE [TechDraw::DrawViewPart] View002
  CoarseView = false
  Direction = (0,0,1)
  Focus = 100
  HardHidden = false
  IsoCount = 0
  IsoHidden = false
  IsoVisible = false
  LockPosition = false
  Perspective = false
  Rotation = 0
  ScaleType = 0
  ScrubCount = 0
  SeamHidden = false
  SeamVisible = true
  SmoothHidden = false
  SmoothVisible = true
  Source = -> [Body]
  X = 148.5
  XDirection = (1,0,0)
  Y = 105
  expr: Y = Template.Height / 2
FEATURE [TechDraw::DrawViewDimension] Dimension004
  AngleOverride = false
  Arbitrary = false
  ArbitraryTolerances = false
  EqualTolerance = true
  ExtensionAngle = 0
  FormatSpec = R%.2w
  FormatSpecOverTolerance = %+.2w
  FormatSpecUnderTolerance = %+.2w
  Inverted = false
  LineAngle = 0
  LockPosition = false
  MeasureType = 1
  OverTolerance = 0
  References2D = -> [View]
  Rotation = 0
  ScaleType = 0
  TheoreticalExact = false
  Type = 4
  UnderTolerance = 0
  X = -23.1952
  Y = -5.48414
FEATURE [TechDraw::DrawViewDimension] Dimension005
  AngleOverride = false
  Arbitrary = false
  ArbitraryTolerances = false
  EqualTolerance = true
  ExtensionAngle = 0
  FormatSpec = R%.2w
  FormatSpecOverTolerance = %+.2w
  FormatSpecUnderTolerance = %+.2w
  Inverted = false
  LineAngle = 0
  LockPosition = false
  MeasureType = 1
  OverTolerance = 0
  References2D = -> [View]
  Rotation = 0
  ScaleType = 0
  TheoreticalExact = false
  Type = 4
  UnderTolerance = 0
  X = 1.1181
  Y = 3.75976
FEATURE [TechDraw::DrawViewDimension] Dimension
  AngleOverride = false
  Arbitrary = false
  ArbitraryTolerances = false
  BoxCorners = (2) [(-11.5,-8,-1e-07),(11.5,8,1e-07)]
  EqualTolerance = true
  ExtensionAngle = 0
  FormatSpec = %.2w
  FormatSpecOverTolerance = %+.2w
  FormatSpecUnderTolerance = %+.2w
  Inverted = false
  LineAngle = 0
  LockPosition = false
  MeasureType = 1
  OverTolerance = 0
  References2D = -> [View]
  Rotation = 0
  ScaleType = 0
  TheoreticalExact = false
  Type = 1
  UnderTolerance = 0
  X = -0.401552
  Y = 25.4578
FEATURE [TechDraw::DrawViewDimension] Dimension006
  AngleOverride = false
  Arbitrary = false
  ArbitraryTolerances = false
  BoxCorners = (2) [(-11.5,-8,-1e-07),(11.5,8,1e-07)]
  EqualTolerance = true
  ExtensionAngle = 0
  FormatSpec = %.2w
  FormatSpecOverTolerance = %+.2w
  FormatSpecUnderTolerance = %+.2w
  Inverted = false
  LineAngle = 0
  LockPosition = false
  MeasureType = 1
  OverTolerance = 0
  References2D = -> [View]
  Rotation = 0
  ScaleType = 0
  TheoreticalExact = false
  Type = 2
  UnderTolerance = 0
  X = 18.6275
  Y = 2.60039
FEATURE [TechDraw::DrawPage] Page
  KeepUpdated = true
  NextBalloonIndex = 1
  ProjectionType = 0
  Template = -> Template
  Views = -> [View,View001,View002,Dimension004,Dimension005,Dimension,Dimension006]
FEATURE [App::DocumentObjectGroup] Group  label="unfold_Group"
  Group = -> [Page,Unfold,Unfold_Sketch,Unfold_Sketch_Outline,Unfold_Sketch_Internal,Unfold_Sketch_bends]
note: 1 file-system path scrubbed to <path> (originals preserved in the JSON sidecar)
---- part composit_full_size3.FCStd = doc fcstd_eedd87f2b88b (600288 chars; too large to inline — full recipe in that document) ----
